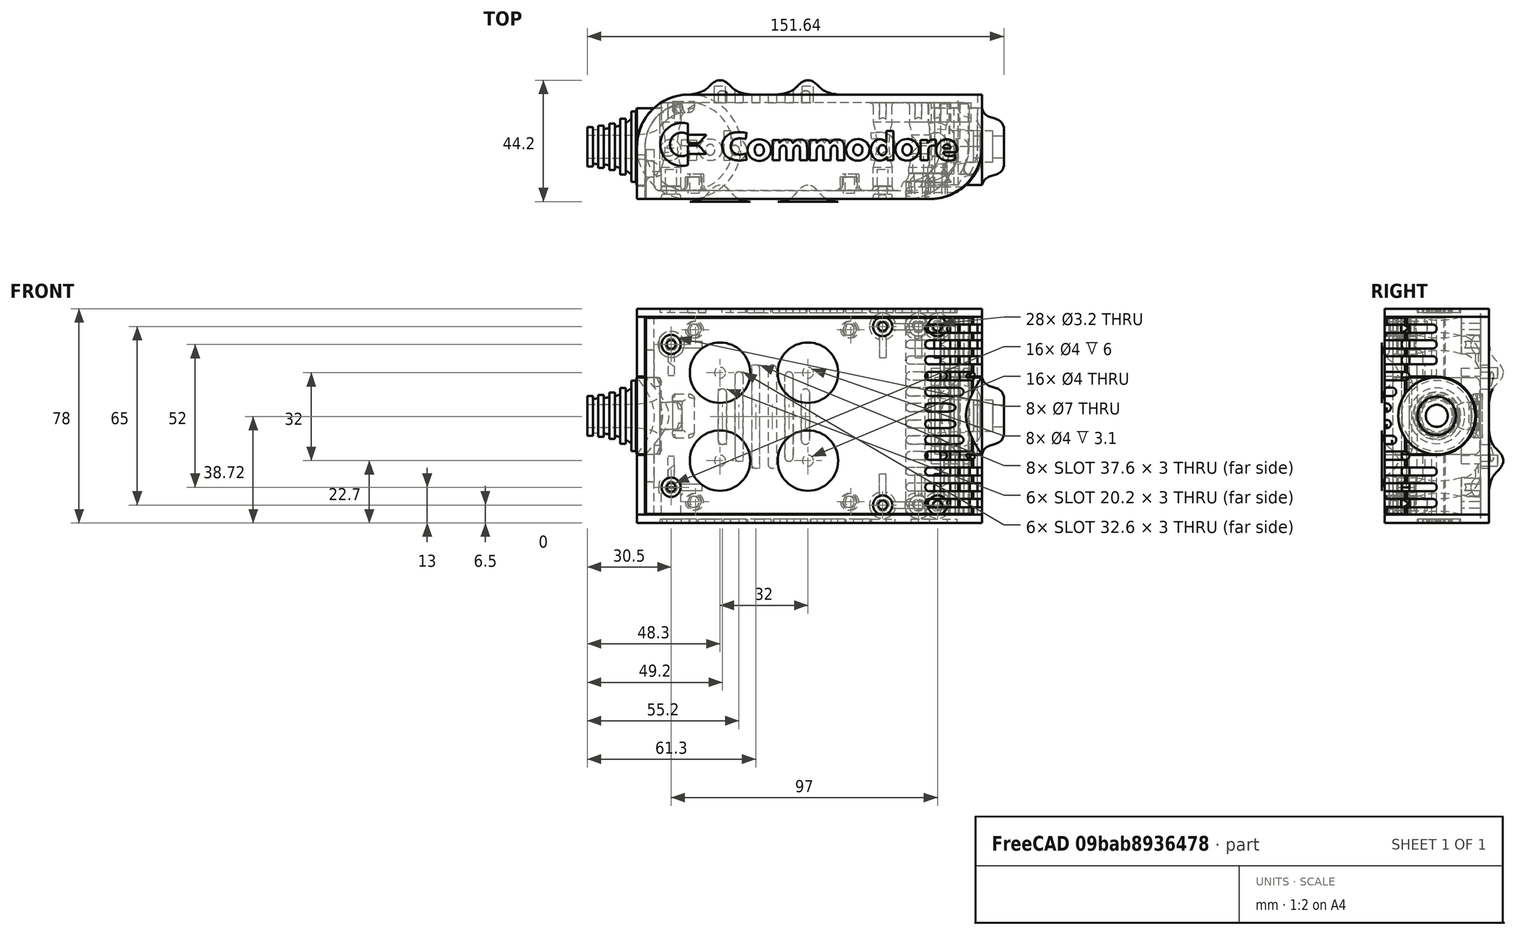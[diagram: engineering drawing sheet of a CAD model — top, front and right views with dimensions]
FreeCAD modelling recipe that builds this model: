
FCSTD DOCUMENT  (FreeCAD 0.19R0.19.2)
Label: enclosure_211FCStd
License: All rights reserved
LicenseURL: http://en.wikipedia.org/wiki/All_rights_reserved
objects: Part::Revolution×152, Part::MultiFuse×146, Part::Feature×146, Sketcher::SketchObject×84, Part::Cut×72, Part::Cylinder×70, Part::Extrusion×69, Part::Fillet×58, Part::Box×37, App::MeasureDistance×4, Part::FeaturePython×2, Image::ImagePlane×1, PartDesign::Body×1, Part::Mirroring×1
note: 838 computed .brp shape members not serialized (recipe doc carries the construction recipe); baked Part::Feature solids carry a one-line shape summary decoded from their .brp

FEATURE [Sketcher::SketchObject] Sketch  label="topSketch"
  FullyConstrained = true
  sketch-geometry (20):
    g0: LineSegment StartX=5.21097e-06 StartY=3 StartZ=0 EndX=5.21097e-06 EndY=19 EndZ=0
    g1: ArcOfCircle CenterX=19 CenterY=19 CenterZ=0 NormalX=0 NormalY=0 NormalZ=1 AngleXU=0 Radius=19 StartAngle=1.5708 EndAngle=3.14159
    g2: ArcOfCircle CenterX=19 CenterY=19 CenterZ=0 NormalX=0 NormalY=0 NormalZ=1 AngleXU=0 Radius=16 StartAngle=1.5708 EndAngle=3.14159
    g3: LineSegment StartX=114 StartY=35 StartZ=0 EndX=19 EndY=35 EndZ=0
    g4: LineSegment StartX=5.21097e-06 StartY=3 StartZ=0 EndX=5.21097e-06 EndY=0 EndZ=0
    g5: LineSegment StartX=3 StartY=0 StartZ=0 EndX=5.21097e-06 EndY=0 EndZ=0
    g6: LineSegment StartX=3 StartY=19 StartZ=0 EndX=3 EndY=0 EndZ=0
    g7: LineSegment StartX=19 StartY=38 StartZ=0 EndX=124 EndY=38 EndZ=0
    g8: Circle CenterX=119 CenterY=35 CenterZ=0 NormalX=0 NormalY=0 NormalZ=1 AngleXU=0 Radius=1
    g9: Circle CenterX=121 CenterY=35 CenterZ=0 NormalX=0 NormalY=0 NormalZ=1 AngleXU=0 Radius=1
    g10: Circle CenterX=121 CenterY=33 CenterZ=0 NormalX=0 NormalY=0 NormalZ=1 AngleXU=0 Radius=1
    g11: BSplineCurve PolesCount=3 KnotsCount=2 Degree=2 IsPeriodic=0
    g12: GeomPoint X=119 Y=35 Z=0
    g13: GeomPoint X=121 Y=33 Z=0
    g14: LineSegment StartX=119 StartY=35 StartZ=0 EndX=114 EndY=35 EndZ=0
    g15: ArcOfCircle CenterX=105 CenterY=19 CenterZ=0 NormalX=0 NormalY=0 NormalZ=1 AngleXU=0 Radius=19 StartAngle=5.7297 EndAngle=6.28319
    g16: ArcOfCircle CenterX=105 CenterY=19 CenterZ=0 NormalX=0 NormalY=0 NormalZ=1 AngleXU=0 Radius=16 StartAngle=5.60905 EndAngle=6.28319
    g17: LineSegment StartX=121 StartY=33 StartZ=0 EndX=121 EndY=19 EndZ=0
    g18: LineSegment StartX=124 StartY=38 StartZ=0 EndX=124 EndY=19 EndZ=0
    g19: LineSegment StartX=117.5 StartY=9.01251 StartZ=0 EndX=121.163 EndY=9.0125 EndZ=0
  constraints (46):
    c: Vertical(g0)
    c: Block(g0)
    c: Coincident(g1,g0)
    c: Block(g1)
    c: Coincident(g2,g1)
    c: Block(g2)
    c: Coincident(g3,g2)
    c: Horizontal(g3)
    c: Tangent(g3,g2)
    c: Coincident(g4,g0)
    c: Distance(g4) = 3
    c: Vertical(g4)
    c: Coincident(g5,g4)
    c: Horizontal(g5)
    c: Coincident(g6,g2)
    c: Coincident(g6,g5)
    c: Vertical(g6)
    c: Horizontal(g7)
    c: Distance(g7) = 105
    c: Coincident(g7,g1)
    c: Block(g3)
    c: Weight(g8) = 1
    c: Equal(g8,g9)
    c: Equal(g8,g10)
    c: InternalAlignment(g8,g11)
    c: InternalAlignment(g9,g11)
    c: InternalAlignment(g10,g11)
    c: InternalAlignment(g12,g11)
    c: InternalAlignment(g13,g11)
    c: Block(g11)
    c: Coincident(g14,g11)
    c: Coincident(g14,g3)
    c: Horizontal(g14)
    c: Block(g15)
    c: Coincident(g16,g15)
    c: Block(g16)
    c: Coincident(g17,g11)
    c: Coincident(g17,g16)
    c: Vertical(g17)
    c: Distance(g17) = 14
    c: Coincident(g18,g7)
    c: Coincident(g18,g15)
    c: Vertical(g18)
    c: Distance(g18) = 19
    c: Coincident(g19,g16)
    c: Coincident(g19,g15)
FEATURE [Sketcher::SketchObject] Sketch001  label="bottomSketch"
  FullyConstrained = true
  sketch-geometry (32):
    g0: LineSegment StartX=3.3 StartY=-6.03275e-07 StartZ=0 EndX=98 EndY=-6.03275e-07 EndZ=0
    g1: ArcOfCircle CenterX=98 CenterY=19 CenterZ=0 NormalX=0 NormalY=0 NormalZ=1 AngleXU=0 Radius=19 StartAngle=4.71239 EndAngle=5.71103
    g2: LineSegment StartX=6.3 StartY=8 StartZ=0 EndX=3.3 EndY=8 EndZ=0
    g3: LineSegment StartX=3.3 StartY=8 StartZ=0 EndX=3.3 EndY=-6.03275e-07 EndZ=0
    g4: ArcOfCircle CenterX=8.3 CenterY=5 CenterZ=0 NormalX=0 NormalY=0 NormalZ=1 AngleXU=0 Radius=2 StartAngle=3.14159 EndAngle=4.71239
    g5: LineSegment StartX=6.3 StartY=8 StartZ=0 EndX=6.3 EndY=5 EndZ=0
    g6: ArcOfCircle CenterX=98 CenterY=19 CenterZ=0 NormalX=0 NormalY=0 NormalZ=1 AngleXU=0 Radius=12.7 StartAngle=4.71239 EndAngle=6.28319
    g7: LineSegment StartX=94.7 StartY=3 StartZ=0 EndX=8.3 EndY=3 EndZ=0
    g8-g12: Circle x5 (B-spline internal-alignment scaffolding for g13; pole/knot coordinates omitted)
    g13: BSplineCurve PolesCount=5 KnotsCount=3 Degree=3 IsPeriodic=0
    g14: GeomPoint X=98 Y=6.3 Z=0
    g15: GeomPoint X=96.3938 Y=4.71946 Z=0
    g16: GeomPoint X=94.7 Y=3 Z=0
    g17-g23: Circle x7 (B-spline internal-alignment scaffolding for g24; pole/knot coordinates omitted)
    g24: BSplineCurve PolesCount=7 KnotsCount=5 Degree=3 IsPeriodic=0
    g25-g29: GeomPoint x5 (B-spline internal-alignment scaffolding for g24; pole/knot coordinates omitted)
    g30: ArcOfCircle CenterX=98 CenterY=19 CenterZ=0 NormalX=0 NormalY=0 NormalZ=1 AngleXU=0 Radius=15.7 StartAngle=5.81226 EndAngle=6.28319
    g31: LineSegment StartX=110.7 StartY=19 StartZ=0 EndX=113.7 EndY=19 EndZ=0
  constraints (41):
    c: Horizontal(g0)
    c: Coincident(g1,g0)
    c: Block(g1)
    c: Horizontal(g2)
    c: Distance(g2) = 3
    c: Coincident(g3,g2)
    c: Vertical(g3)
    c: Coincident(g3,g0)
    c: Block(g4)
    c: Block(g2)
    c: Coincident(g5,g2)
    c: Coincident(g5,g4)
    c: Vertical(g5)
    c: Coincident(g6,g1)
    c: Block(g6)
    c: Coincident(g7,g4)
    c: Horizontal(g7)
    c: Block(g0)
    c: Block(g7)
    c: Block(g3)
    c: Coincident(g13,g6)
    c: Weight(g8) = 1
    c: Equal(g8, g9-g12) x4
    c: Coincident(g13,g7)
    c: InternalAlignment(g8-g12 -> g13) x5
    c: InternalAlignment(g14,g13)
    c: InternalAlignment(g15,g13)
    c: InternalAlignment(g16,g13)
    c: Block(g13)
    c: Weight(g17) = 1
    c: Equal(g17, g18-g23) x6
    c: Coincident(g24,g1)
    c: InternalAlignment(g17-g23 -> g24) x7
    c: InternalAlignment(g25-g29 -> g24) x5
    c: Block(g24)
    c: Coincident(g30,g24)
    c: Coincident(g31,g6)
    c: Coincident(g31,g30)
    c: Horizontal(g31)
    c: Block(g31)
    c: Block(g30)
FEATURE [Part::Extrusion] Extrude  label="top"
  Base = -> Sketch
  Dir = (0,0,1)
  DirMode = 2
  FaceMakerClass = Part::FaceMakerBullseye
  LengthFwd = 72
  LengthRev = 0
  Solid = true
  Symmetric = false
FEATURE [Part::Extrusion] Extrude001  label="bottom"
  Base = -> Sketch001
  Dir = (0,0,1)
  DirMode = 2
  FaceMakerClass = Part::FaceMakerBullseye
  LengthFwd = 71.4
  LengthRev = 0
  Placement = pos=(0,0,0.3) rot=(0,0,1;0rad)
  Solid = true
  Symmetric = false
FEATURE [Sketcher::SketchObject] Sketch002  label="topSketch001"
  FullyConstrained = true
  sketch-geometry (8):
    g0: ArcOfCircle CenterX=19 CenterY=19.0975 CenterZ=0 NormalX=0 NormalY=0 NormalZ=1 AngleXU=0 Radius=18.9025 StartAngle=1.5708 EndAngle=3.14674
    g1: LineSegment StartX=0.0977805 StartY=19.0003 StartZ=0 EndX=0.0977805 EndY=0.000251602 EndZ=0
    g2: LineSegment StartX=19 StartY=38 StartZ=0 EndX=124 EndY=38 EndZ=0
    g3: LineSegment StartX=0.0977805 StartY=0.000251602 StartZ=0 EndX=105.098 EndY=0.000251602 EndZ=0
    g4: LineSegment StartX=124 StartY=38 StartZ=0 EndX=125.616 EndY=38 EndZ=0
    g5: LineSegment StartX=105.098 StartY=0.000251602 StartZ=0 EndX=106.713 EndY=0.000251602 EndZ=0
    g6: ArcOfCircle CenterX=106.616 CenterY=19 CenterZ=0 NormalX=0 NormalY=0 NormalZ=1 AngleXU=0 Radius=19 StartAngle=4.71754 EndAngle=6.28319
    g7: LineSegment StartX=125.616 StartY=38 StartZ=0 EndX=125.616 EndY=19 EndZ=0
  constraints (21):
    c: Block(g0)
    c: Coincident(g1,g0)
    c: Vertical(g1)
    c: Horizontal(g2)
    c: Distance(g2) = 105
    c: Coincident(g2,g0)
    c: Distance(g1) = 19
    c: Coincident(g3,g1)
    c: Horizontal(g3)
    c: Distance(g3) = 105
    c: Coincident(g4,g2)
    c: Horizontal(g4)
    c: Distance(g4) = 1.61553
    c: Horizontal(g5)
    c: Equal(g4,g5) = 1.61553
    c: Coincident(g5,g3)
    c: Block(g6)
    c: Coincident(g6,g5)
    c: Coincident(g7,g4)
    c: Coincident(g7,g6)
    c: Vertical(g7)
FEATURE [Part::Extrusion] Extrude002  label="sideA"
  Base = -> Sketch002
  Dir = (0,0,1)
  DirMode = 2
  FaceMakerClass = Part::FaceMakerBullseye
  LengthFwd = 3
  LengthRev = 0
  Placement = pos=(0,0,-3) rot=(0,0,1;0rad)
  Solid = true
  Symmetric = false
FEATURE [Sketcher::SketchObject] Sketch003  label="topSketch002"
  FullyConstrained = true
  sketch-geometry (6):
    g0: LineSegment StartX=19 StartY=38 StartZ=0 EndX=117 EndY=38 EndZ=0
    g1: ArcOfCircle CenterX=19 CenterY=19 CenterZ=0 NormalX=0 NormalY=0 NormalZ=1 AngleXU=0 Radius=19 StartAngle=1.5708 EndAngle=3.14159
    g2: LineSegment StartX=117 StartY=38 StartZ=0 EndX=117 EndY=19 EndZ=0
    g3: LineSegment StartX=98 StartY=1.0161e-12 StartZ=0 EndX=5.22862e-06 EndY=1.0161e-12 EndZ=0
    g4: LineSegment StartX=5.22862e-06 StartY=19 StartZ=0 EndX=5.22862e-06 EndY=1.0161e-12 EndZ=0
    g5: ArcOfCircle CenterX=98 CenterY=19 CenterZ=0 NormalX=0 NormalY=0 NormalZ=1 AngleXU=0 Radius=19 StartAngle=4.71239 EndAngle=6.28319
  constraints (16):
    c: Horizontal(g0)
    c: Distance(g0) = 98
    c: Coincident(g1,g0)
    c: Block(g1)
    c: Coincident(g2,g0)
    c: Vertical(g2)
    c: Distance(g2) = 19
    c: Horizontal(g3)
    c: Coincident(g4,g1)
    c: Vertical(g4)
    c: Coincident(g3,g4)
    c: Block(g3)
    c: Coincident(g5,g2)
    c: Coincident(g5,g3)
    c: Block(g0)
    c: Block(g5)
FEATURE [Sketcher::SketchObject] Sketch004
  FullyConstrained = true
  MapMode = 3
  Placement = pos=(0,0,0) rot=(1,0,0;1.5708rad)
  Support = -> [Extrude]
  sketch-geometry (8):
    g0: Circle CenterX=80.351 CenterY=-67.6202 CenterZ=0 NormalX=0 NormalY=0 NormalZ=1 AngleXU=0 Radius=2
    g1: Circle CenterX=80.351 CenterY=-67.6202 CenterZ=0 NormalX=0 NormalY=0 NormalZ=1 AngleXU=0 Radius=3
    g2: Circle CenterX=80.351 CenterY=-4.92017 CenterZ=0 NormalX=0 NormalY=0 NormalZ=1 AngleXU=0 Radius=2
    g3: Circle CenterX=80.351 CenterY=-4.92017 CenterZ=0 NormalX=0 NormalY=0 NormalZ=1 AngleXU=0 Radius=3
    g4: Circle CenterX=23.851 CenterY=-4.92017 CenterZ=0 NormalX=0 NormalY=0 NormalZ=1 AngleXU=0 Radius=2
    g5: Circle CenterX=23.851 CenterY=-4.92017 CenterZ=0 NormalX=0 NormalY=0 NormalZ=1 AngleXU=0 Radius=3
    g6: Circle CenterX=23.851 CenterY=-67.6202 CenterZ=0 NormalX=0 NormalY=0 NormalZ=1 AngleXU=0 Radius=2
    g7: Circle CenterX=23.851 CenterY=-67.6202 CenterZ=0 NormalX=0 NormalY=0 NormalZ=1 AngleXU=0 Radius=3
  constraints (8):
    c: Block(g3)
    c: Block(g2)
    c: Block(g1)
    c: Block(g0)
    c: Block(g6)
    c: Block(g7)
    c: Block(g4)
    c: Block(g5)
FEATURE [Part::Extrusion] Extrude004
  Base = -> Sketch004
  Dir = (0,-1,2e-16)
  DirMode = 2
  FaceMakerClass = Part::FaceMakerBullseye
  LengthFwd = 6
  LengthRev = 0
  Placement = pos=(0,9,0) rot=(0,0,1;0rad)
  Solid = true
  Symmetric = false
FEATURE [Sketcher::SketchObject] Sketch005
  FullyConstrained = true
  MapMode = 3
  Placement = pos=(0,0,0) rot=(1,0,0;1.5708rad)
  Support = -> [Extrude]
  sketch-geometry (8):
    g0: Circle CenterX=80.351 CenterY=-67.6202 CenterZ=0 NormalX=0 NormalY=0 NormalZ=1 AngleXU=0 Radius=3
    g1: Circle CenterX=80.351 CenterY=-4.92017 CenterZ=0 NormalX=0 NormalY=0 NormalZ=1 AngleXU=0 Radius=3
    g2: Circle CenterX=23.851 CenterY=-4.92017 CenterZ=0 NormalX=0 NormalY=0 NormalZ=1 AngleXU=0 Radius=3
    g3: Circle CenterX=23.851 CenterY=-67.6202 CenterZ=0 NormalX=0 NormalY=0 NormalZ=1 AngleXU=0 Radius=3
    g4: Circle CenterX=23.851 CenterY=-67.6202 CenterZ=0 NormalX=0 NormalY=0 NormalZ=1 AngleXU=0 Radius=5
    g5: Circle CenterX=80.351 CenterY=-67.6202 CenterZ=0 NormalX=0 NormalY=0 NormalZ=1 AngleXU=0 Radius=5
    g6: Circle CenterX=23.851 CenterY=-4.92017 CenterZ=0 NormalX=0 NormalY=0 NormalZ=1 AngleXU=0 Radius=5
    g7: Circle CenterX=80.351 CenterY=-4.92017 CenterZ=0 NormalX=0 NormalY=0 NormalZ=1 AngleXU=0 Radius=5
  constraints (8):
    c: Block(g1)
    c: Block(g0)
    c: Block(g3)
    c: Block(g2)
    c: Block(g5)
    c: Block(g4)
    c: Block(g6)
    c: Block(g7)
FEATURE [Part::Extrusion] Extrude005
  Base = -> Sketch005
  Dir = (0,-1,2e-16)
  DirMode = 2
  FaceMakerClass = Part::FaceMakerBullseye
  LengthFwd = 2
  LengthRev = 0
  Solid = true
  Symmetric = false
FEATURE [Sketcher::SketchObject] Sketch006
  FullyConstrained = true
  MapMode = 3
  Placement = pos=(0,0,0) rot=(1,0,0;1.5708rad)
  sketch-geometry (8):
    g0: Circle CenterX=80.351 CenterY=-67.6202 CenterZ=0 NormalX=0 NormalY=0 NormalZ=1 AngleXU=0 Radius=3
    g1: Circle CenterX=80.351 CenterY=-4.92017 CenterZ=0 NormalX=0 NormalY=0 NormalZ=1 AngleXU=0 Radius=3
    g2: Circle CenterX=23.851 CenterY=-4.92017 CenterZ=0 NormalX=0 NormalY=0 NormalZ=1 AngleXU=0 Radius=3
    g3: Circle CenterX=23.851 CenterY=-67.6202 CenterZ=0 NormalX=0 NormalY=0 NormalZ=1 AngleXU=0 Radius=3
    g4: Circle CenterX=23.851 CenterY=-67.6202 CenterZ=0 NormalX=0 NormalY=0 NormalZ=1 AngleXU=0 Radius=5
    g5: Circle CenterX=80.351 CenterY=-67.6202 CenterZ=0 NormalX=0 NormalY=0 NormalZ=1 AngleXU=0 Radius=5
    g6: Circle CenterX=23.851 CenterY=-4.92017 CenterZ=0 NormalX=0 NormalY=0 NormalZ=1 AngleXU=0 Radius=5
    g7: Circle CenterX=80.351 CenterY=-4.92017 CenterZ=0 NormalX=0 NormalY=0 NormalZ=1 AngleXU=0 Radius=5
  constraints (8):
    c: Block(g1)
    c: Block(g0)
    c: Block(g3)
    c: Block(g2)
    c: Block(g5)
    c: Block(g4)
    c: Block(g6)
    c: Block(g7)
FEATURE [Part::Extrusion] Extrude007
  Base = -> Sketch006
  Dir = (0,-1,2e-16)
  DirMode = 2
  FaceMakerClass = Part::FaceMakerBullseye
  LengthFwd = 2
  LengthRev = 0
  Solid = true
  Symmetric = false
FEATURE [Part::Fillet] Fillet
  Base = -> Extrude007
  Edges = 4 edges r=1.99: [Edge6,Edge12,Edge18,Edge24]
FEATURE [Part::Cut] Cut
  Base = -> Extrude005
  Placement = pos=(0,5,0) rot=(0,0,1;0rad)
  Tool = -> Fillet
FEATURE [Part::MultiFuse] Fusion  label="pCBScrews"
  Placement = pos=(-2.5,0,72.3) rot=(0,0,1;0rad)
  Shapes = -> [Extrude004,Cut]
FEATURE [App::MeasureDistance] Distance  label="Distance: 0.69 mm"
  Distance = 0.685967
  P1 = (24.0138,2.9647,0.3)
  P2 = (23.8901,3,-0.373787)
FEATURE [App::MeasureDistance] Distance001  label="Distance: 0.53 mm"
  Distance = 0.533607
  P1 = (80.2939,3,72.2334)
  P2 = (80.281,2.99661,71.7)
FEATURE [Part::Fillet] Fillet001
  Base = -> Extrude001
  Edges = 1 edges r=2.4: [Edge17]
FEATURE [Part::Fillet] Fillet002  label="bottom001"
  Base = -> Fillet001
  Edges = 1 edges r=2.4: [Edge36]
FEATURE [Part::Fillet] Fillet003  label="top001"
  Base = -> Extrude
  Edges = 1 edges r=2: [Edge1]
FEATURE [Sketcher::SketchObject] Sketch007
  FullyConstrained = true
  sketch-geometry (16):
    g0: LineSegment StartX=4 StartY=0 StartZ=0 EndX=4 EndY=2.4 EndZ=0
    g1: LineSegment StartX=4 StartY=2.4 StartZ=0 EndX=7 EndY=2.4 EndZ=0
    g2: LineSegment StartX=4 StartY=0 StartZ=0 EndX=5.7 EndY=0 EndZ=0
    g3: LineSegment StartX=5.7 StartY=0 StartZ=0 EndX=5.7 EndY=-5.6 EndZ=0
    g4-g8: Circle x5 (B-spline internal-alignment scaffolding for g9; pole/knot coordinates omitted)
    g9: BSplineCurve PolesCount=5 KnotsCount=3 Degree=3 IsPeriodic=0
    g10: GeomPoint X=7 Y=2.4 Z=0
    g11: GeomPoint X=10.4582 Y=-1.55472 Z=0
    g12: GeomPoint X=14 Y=-5.6 Z=0
    g13: LineSegment StartX=14 StartY=-5.6 StartZ=0 EndX=14 EndY=-14.1 EndZ=0
    g14: LineSegment StartX=14 StartY=-14.1 StartZ=0 EndX=6.5 EndY=-14.1 EndZ=0
    g15: LineSegment StartX=5.7 StartY=-5.6 StartZ=0 EndX=6.5 EndY=-14.1 EndZ=0
  constraints (28):
    c: Distance(g0) = 2.4
    c: Vertical(g0)
    c: Block(g0)
    c: Coincident(g1,g0)
    c: Horizontal(g1)
    c: Distance(g1) = 3
    c: Coincident(g2,g0)
    c: Horizontal(g2)
    c: Distance(g2) = 1.7
    c: Coincident(g3,g2)
    c: Vertical(g3)
    c: Distance(g3) = 5.6
    c: Coincident(g9,g1)
    c: Weight(g4) = 1
    c: Equal(g4, g5-g8) x4
    c: InternalAlignment(g4-g8 -> g9) x5
    c: InternalAlignment(g10,g9)
    c: InternalAlignment(g11,g9)
    c: InternalAlignment(g12,g9)
    c: Block(g9)
    c: Coincident(g13,g9)
    c: Vertical(g13)
    c: Distance(g13) = 8.5
    c: Coincident(g14,g13)
    c: Horizontal(g14)
    c: Distance(g14) = 7.5
    c: Coincident(g15,g3)
    c: Coincident(g15,g14)
FEATURE [Part::Feature] Face
  shape: bbox 10 x 16.5 x 2e-07 mm, 1 faces, 0 solids (baked)
FEATURE [Part::Revolution] Revolve  label="plugHousing"
  Angle = 360
  Axis = (0,1,0)
  Base = (0,0,0)
  FaceMakerClass = Part::FaceMakerBullseye
  Placement = pos=(0,0,36.15) rot=(0,0,1;0rad)
  Solid = false
  Source = -> Face
  Symmetric = false
FEATURE [Part::Feature] Face001
  shape: bbox 10 x 16.5 x 2e-07 mm, 1 faces, 0 solids (baked)
FEATURE [Part::Revolution] Revolve001  label="plugHousing001"
  Angle = 360
  Axis = (0,1,0)
  Base = (0,0,0)
  FaceMakerClass = Part::FaceMakerBullseye
  Placement = pos=(0,0,36.15) rot=(0,0,1;0rad)
  Solid = false
  Source = -> Face001
  Symmetric = false
FEATURE [Part::MultiFuse] Fusion001  label="plugHousing002"
  Placement = pos=(0,0,0) rot=(0,0,1;1.5708rad)
  Shapes = -> [Revolve001,Revolve]
FEATURE [Part::Feature] Face002
  shape: bbox 10 x 16.5 x 2e-07 mm, 1 faces, 0 solids (baked)
FEATURE [Part::Revolution] Revolve003  label="plugHousing005"
  Angle = 360
  Axis = (0,1,0)
  Base = (0,0,0)
  FaceMakerClass = Part::FaceMakerBullseye
  Placement = pos=(0,0,36.15) rot=(0,0,1;0rad)
  Solid = false
  Source = -> Face002
  Symmetric = false
FEATURE [Part::Feature] Face003
  shape: bbox 10 x 16.5 x 2e-07 mm, 1 faces, 0 solids (baked)
FEATURE [Part::Revolution] Revolve002  label="plugHousing003"
  Angle = 360
  Axis = (0,1,0)
  Base = (0,0,0)
  FaceMakerClass = Part::FaceMakerBullseye
  Placement = pos=(0,0,36.15) rot=(0,0,1;0rad)
  Solid = false
  Source = -> Face003
  Symmetric = false
FEATURE [Part::MultiFuse] Fusion002  label="plugHousing004"
  Placement = pos=(0,0,0) rot=(0,0,1;1.5708rad)
  Shapes = -> [Revolve002,Revolve003]
FEATURE [Part::MultiFuse] Fusion003  label="plugHousing006"
  Placement = pos=(0,19,0) rot=(0,0,1;3.14159rad)
  Shapes = -> [Fusion002,Fusion001]
FEATURE [Part::Feature] Face004
  shape: bbox 10 x 16.5 x 2e-07 mm, 1 faces, 0 solids (baked)
FEATURE [Part::Revolution] Revolve006  label="plugHousing010"
  Angle = 360
  Axis = (0,1,0)
  Base = (0,0,0)
  FaceMakerClass = Part::FaceMakerBullseye
  Placement = pos=(0,0,36.15) rot=(0,0,1;0rad)
  Solid = false
  Source = -> Face004
  Symmetric = false
FEATURE [Part::Feature] Face005
  shape: bbox 10 x 16.5 x 2e-07 mm, 1 faces, 0 solids (baked)
FEATURE [Part::Revolution] Revolve007  label="plugHousing011"
  Angle = 360
  Axis = (0,1,0)
  Base = (0,0,0)
  FaceMakerClass = Part::FaceMakerBullseye
  Placement = pos=(0,0,36.15) rot=(0,0,1;0rad)
  Solid = false
  Source = -> Face005
  Symmetric = false
FEATURE [Part::Feature] Face006
  shape: bbox 10 x 16.5 x 2e-07 mm, 1 faces, 0 solids (baked)
FEATURE [Part::Revolution] Revolve004  label="plugHousing007"
  Angle = 360
  Axis = (0,1,0)
  Base = (0,0,0)
  FaceMakerClass = Part::FaceMakerBullseye
  Placement = pos=(0,0,36.15) rot=(0,0,1;0rad)
  Solid = false
  Source = -> Face006
  Symmetric = false
FEATURE [Part::MultiFuse] Fusion004  label="plugHousing009"
  Placement = pos=(0,0,0) rot=(0,0,1;1.5708rad)
  Shapes = -> [Revolve004,Revolve007]
FEATURE [Part::Feature] Face007
  shape: bbox 10 x 16.5 x 2e-07 mm, 1 faces, 0 solids (baked)
FEATURE [Part::Revolution] Revolve005  label="plugHousing008"
  Angle = 360
  Axis = (0,1,0)
  Base = (0,0,0)
  FaceMakerClass = Part::FaceMakerBullseye
  Placement = pos=(0,0,36.15) rot=(0,0,1;0rad)
  Solid = false
  Source = -> Face007
  Symmetric = false
FEATURE [Part::MultiFuse] Fusion005  label="plugHousing012"
  Placement = pos=(0,0,0) rot=(0,0,1;1.5708rad)
  Shapes = -> [Revolve006,Revolve005]
FEATURE [Part::MultiFuse] Fusion006  label="plugHousing013"
  Placement = pos=(0,19,0) rot=(0,0,1;3.14159rad)
  Shapes = -> [Fusion005,Fusion004]
FEATURE [Part::MultiFuse] Fusion007  label="plugHousing014"
  Placement = pos=(122.621,0,-0.15) rot=(0,0,1;0rad)
  Shapes = -> [Fusion003,Fusion006]
FEATURE [Part::Cylinder] Cylinder002
  Angle = 360
  AttacherType = Attacher::AttachEngine3D
  Height = 20
  Placement = pos=(0,0,36.15) rot=(0,0,1;0rad)
  Radius = 4
FEATURE [Part::Cylinder] Cylinder003
  Angle = 360
  AttacherType = Attacher::AttachEngine3D
  Height = 10
  Placement = pos=(0,0,36.15) rot=(0,0,1;0rad)
  Radius = 4
FEATURE [Part::MultiFuse] Fusion009  label="removeToCreateHoleForPlugHousing"
  Placement = pos=(70,19,36.15) rot=(0,1,0;1.5708rad)
  Shapes = -> [Cylinder002,Cylinder003]
FEATURE [Part::Cylinder] Cylinder004
  Angle = 360
  AttacherType = Attacher::AttachEngine3D
  Height = 20
  Placement = pos=(0,0,36.15) rot=(0,0,1;0rad)
  Radius = 4
FEATURE [Part::Cylinder] Cylinder005
  Angle = 360
  AttacherType = Attacher::AttachEngine3D
  Height = 10
  Placement = pos=(0,0,36.15) rot=(0,0,1;0rad)
  Radius = 4
FEATURE [Part::MultiFuse] Fusion010  label="removeToCreateHoleForPlugHousing001"
  Placement = pos=(70,19,36.15) rot=(0,1,0;1.5708rad)
  Shapes = -> [Cylinder004,Cylinder005]
FEATURE [Part::Cut] Cut001
  Base = -> Fillet003
  Tool = -> Fusion010
FEATURE [Part::Cut] Cut002  label="Bottom"
  Base = -> Fillet002
  Tool = -> Fusion009
FEATURE [Part::Feature] Face008
  shape: bbox 10 x 16.5 x 2e-07 mm, 1 faces, 0 solids (baked)
FEATURE [Part::Revolution] Revolve011  label="plugHousing021"
  Angle = 360
  Axis = (0,1,0)
  Base = (0,0,0)
  FaceMakerClass = Part::FaceMakerBullseye
  Placement = pos=(0,0,36.15) rot=(0,0,1;0rad)
  Solid = false
  Source = -> Face008
  Symmetric = false
FEATURE [Part::Feature] Face009
  shape: bbox 10 x 16.5 x 2e-07 mm, 1 faces, 0 solids (baked)
FEATURE [Part::Revolution] Revolve012  label="plugHousing022"
  Angle = 360
  Axis = (0,1,0)
  Base = (0,0,0)
  FaceMakerClass = Part::FaceMakerBullseye
  Placement = pos=(0,0,36.15) rot=(0,0,1;0rad)
  Solid = false
  Source = -> Face009
  Symmetric = false
FEATURE [Part::Feature] Face010 .. Face013  x4 (patterned run collapsed; names and placements below)
  shape: bbox 10 x 16.5 x 2e-07 mm, 1 faces, 0 solids (baked)
FEATURE [Part::Revolution] Revolve015  label="plugHousing027"
  Angle = 360
  Axis = (0,1,0)
  Base = (0,0,0)
  FaceMakerClass = Part::FaceMakerBullseye
  Placement = pos=(0,0,36.15) rot=(0,0,1;0rad)
  Solid = false
  Source = -> Face013
  Symmetric = false
FEATURE [Part::Feature] Face014
  shape: bbox 10 x 16.5 x 2e-07 mm, 1 faces, 0 solids (baked)
FEATURE [Part::Feature] Face015
  shape: bbox 10 x 16.5 x 2e-07 mm, 1 faces, 0 solids (baked)
FEATURE [Part::Feature] Face016
  shape: bbox 10 x 16.5 x 2e-07 mm, 1 faces, 0 solids (baked)
FEATURE [Part::Revolution] Revolve019  label="plugHousing033"
  Angle = 360
  Axis = (0,1,0)
  Base = (0,0,0)
  FaceMakerClass = Part::FaceMakerBullseye
  Placement = pos=(0,0,36.15) rot=(0,0,1;0rad)
  Solid = false
  Source = -> Face016
  Symmetric = false
FEATURE [Part::Feature] Face017
  shape: bbox 10 x 16.5 x 2e-07 mm, 1 faces, 0 solids (baked)
FEATURE [Part::Revolution] Revolve020  label="plugHousing034"
  Angle = 360
  Axis = (0,1,0)
  Base = (0,0,0)
  FaceMakerClass = Part::FaceMakerBullseye
  Placement = pos=(0,0,36.15) rot=(0,0,1;0rad)
  Solid = false
  Source = -> Face017
  Symmetric = false
FEATURE [Part::Feature] Face018
  shape: bbox 10 x 16.5 x 2e-07 mm, 1 faces, 0 solids (baked)
FEATURE [Part::Revolution] Revolve016  label="plugHousing030"
  Angle = 360
  Axis = (0,1,0)
  Base = (0,0,0)
  FaceMakerClass = Part::FaceMakerBullseye
  Placement = pos=(0,0,36.15) rot=(0,0,1;0rad)
  Solid = false
  Source = -> Face018
  Symmetric = false
FEATURE [Part::MultiFuse] Fusion020  label="plugHousing038"
  Placement = pos=(0,0,0) rot=(0,0,1;1.5708rad)
  Shapes = -> [Revolve016,Revolve020]
FEATURE [Part::Feature] Face019
  shape: bbox 10 x 16.5 x 2e-07 mm, 1 faces, 0 solids (baked)
FEATURE [Part::Feature] Face020
  shape: bbox 10 x 16.5 x 2e-07 mm, 1 faces, 0 solids (baked)
FEATURE [Part::Revolution] Revolve017  label="plugHousing031"
  Angle = 360
  Axis = (0,1,0)
  Base = (0,0,0)
  FaceMakerClass = Part::FaceMakerBullseye
  Placement = pos=(0,0,36.15) rot=(0,0,1;0rad)
  Solid = false
  Source = -> Face020
  Symmetric = false
FEATURE [Part::MultiFuse] Fusion021  label="plugHousing039"
  Placement = pos=(0,0,0) rot=(0,0,1;1.5708rad)
  Shapes = -> [Revolve019,Revolve017]
FEATURE [Part::MultiFuse] Fusion023  label="plugHousing041"
  Placement = pos=(0,19,0) rot=(0,0,1;3.14159rad)
  Shapes = -> [Fusion021,Fusion020]
FEATURE [Part::Revolution] Revolve022  label="plugHousing043"
  Angle = 360
  Axis = (0,1,0)
  Base = (0,0,0)
  FaceMakerClass = Part::FaceMakerBullseye
  Placement = pos=(0,0,36.15) rot=(0,0,1;0rad)
  Solid = false
  Source = -> Face019
  Symmetric = false
FEATURE [Part::Feature] Face021
  shape: bbox 10 x 16.5 x 2e-07 mm, 1 faces, 0 solids (baked)
FEATURE [Part::Revolution] Revolve023  label="plugHousing044"
  Angle = 360
  Axis = (0,1,0)
  Base = (0,0,0)
  FaceMakerClass = Part::FaceMakerBullseye
  Placement = pos=(0,0,36.15) rot=(0,0,1;0rad)
  Solid = false
  Source = -> Face021
  Symmetric = false
FEATURE [Part::Feature] Face022
  shape: bbox 10 x 16.5 x 2e-07 mm, 1 faces, 0 solids (baked)
FEATURE [Part::Revolution] Revolve018  label="plugHousing032"
  Angle = 360
  Axis = (0,1,0)
  Base = (0,0,0)
  FaceMakerClass = Part::FaceMakerBullseye
  Placement = pos=(0,0,36.15) rot=(0,0,1;0rad)
  Solid = false
  Source = -> Face022
  Symmetric = false
FEATURE [Part::MultiFuse] Fusion022  label="plugHousing040"
  Placement = pos=(0,0,0) rot=(0,0,1;1.5708rad)
  Shapes = -> [Revolve018,Revolve023]
FEATURE [Part::Feature] Face023
  shape: bbox 10 x 16.5 x 2e-07 mm, 1 faces, 0 solids (baked)
FEATURE [Part::Revolution] Revolve021  label="plugHousing035"
  Angle = 360
  Axis = (0,1,0)
  Base = (0,0,0)
  FaceMakerClass = Part::FaceMakerBullseye
  Placement = pos=(0,0,36.15) rot=(0,0,1;0rad)
  Solid = false
  Source = -> Face023
  Symmetric = false
FEATURE [Part::MultiFuse] Fusion018  label="plugHousing036"
  Placement = pos=(0,0,0) rot=(0,0,1;1.5708rad)
  Shapes = -> [Revolve022,Revolve021]
FEATURE [Part::MultiFuse] Fusion019  label="plugHousing037"
  Placement = pos=(0,19,0) rot=(0,0,1;3.14159rad)
  Shapes = -> [Fusion018,Fusion022]
FEATURE [Part::MultiFuse] Fusion024  label="plugHousing042"
  Placement = pos=(122.621,0,-0.15) rot=(0,0,1;0rad)
  Shapes = -> [Fusion023,Fusion019]
FEATURE [Part::Cylinder] Cylinder006
  Angle = 360
  AttacherType = Attacher::AttachEngine3D
  Height = 20
  Placement = pos=(0,0,36.15) rot=(0,0,1;0rad)
  Radius = 14.3
FEATURE [Part::Cylinder] Cylinder007
  Angle = 360
  AttacherType = Attacher::AttachEngine3D
  Height = 10
  Placement = pos=(0,0,36.15) rot=(0,0,1;0rad)
  Radius = 4
FEATURE [Part::MultiFuse] Fusion026  label="removeToCreteHoleForPlugHousing"
  Placement = pos=(70,19,36) rot=(0,1,0;1.5708rad)
  Shapes = -> [Cylinder006,Cylinder007]
FEATURE [Part::Box] Box001  label="Cube001"
  AttacherType = Attacher::AttachEngine3D
  Height = 28
  Length = 3
  Placement = pos=(110.7,19,22) rot=(0,0,1;0rad)
  Width = 15.7
FEATURE [Part::Cut] Cut003  label="top002"
  Base = -> Cut001
  Tool = -> Fusion007
FEATURE [Part::Revolution] Revolve008  label="plugHousing015"
  Angle = 360
  Axis = (0,1,0)
  Base = (0,0,0)
  FaceMakerClass = Part::FaceMakerBullseye
  Placement = pos=(0,0,36.15) rot=(0,0,1;0rad)
  Solid = false
  Source = -> Face010
  Symmetric = false
FEATURE [Part::MultiFuse] Fusion013  label="plugHousing020"
  Placement = pos=(0,0,0) rot=(0,0,1;1.5708rad)
  Shapes = -> [Revolve008,Revolve012]
FEATURE [Part::Cut] Cut004  label="top003"
  Base = -> Cut003
  Placement = pos=(1,0,0) rot=(0,0,1;0rad)
  Tool = -> Fusion026
FEATURE [Part::Cylinder] Cylinder008
  Angle = 360
  AttacherType = Attacher::AttachEngine3D
  Height = 20
  Placement = pos=(0,0,36.15) rot=(0,0,1;0rad)
  Radius = 10.3
FEATURE [Part::Cylinder] Cylinder009
  Angle = 360
  AttacherType = Attacher::AttachEngine3D
  Height = 10
  Placement = pos=(0,0,36.15) rot=(0,0,1;0rad)
  Radius = 4
FEATURE [Part::MultiFuse] Fusion027  label="removeToCreteHoleForPlugHousing001"
  Placement = pos=(70,19,36) rot=(0,1,0;1.5708rad)
  Shapes = -> [Cylinder008,Cylinder009]
FEATURE [Part::Cut] Cut005  label="plugHousingTab"
  Base = -> Box001
  Tool = -> Fusion027
FEATURE [Part::MultiFuse] Fusion028  label="plugHousing045"
  Shapes = -> [Fusion024,Cut005]
FEATURE [Part::Box] Box002  label="Cube002"
  AttacherType = Attacher::AttachEngine3D
  Height = 28.8
  Length = 3
  Placement = pos=(107.3,28,21.6) rot=(0,0,1;0rad)
  Width = 7
FEATURE [Part::Box] Box003  label="Cube003"
  AttacherType = Attacher::AttachEngine3D
  Height = 3
  Length = 6.4
  Placement = pos=(107.3,28,18.6) rot=(0,0,1;0rad)
  Width = 7
FEATURE [Part::Box] Box004  label="Cube004"
  AttacherType = Attacher::AttachEngine3D
  Height = 3
  Length = 6.4
  Placement = pos=(107.3,28,50.4) rot=(0,0,1;0rad)
  Width = 7
FEATURE [Part::MultiFuse] Fusion029  label="plugHousingBracketHolder"
  Shapes = -> [Box004,Box002,Box003]
FEATURE [Part::Cylinder] Cylinder010
  Angle = 360
  AttacherType = Attacher::AttachEngine3D
  Height = 20
  Placement = pos=(0,0,36.15) rot=(0,0,1;0rad)
  Radius = 14.3
FEATURE [Part::Cylinder] Cylinder011
  Angle = 360
  AttacherType = Attacher::AttachEngine3D
  Height = 10
  Placement = pos=(0,0,36.15) rot=(0,0,1;0rad)
  Radius = 4
FEATURE [Part::MultiFuse] Fusion030  label="removeToCreteHoleForPlugHousing002"
  Placement = pos=(70,19,36) rot=(0,1,0;1.5708rad)
  Shapes = -> [Cylinder010,Cylinder011]
FEATURE [Part::Cut] Cut006  label="plugHousingBracketHolder001"
  Base = -> Fusion029
  Tool = -> Fusion030
FEATURE [Part::Cylinder] Cylinder012
  Angle = 360
  AttacherType = Attacher::AttachEngine3D
  Height = 20
  Placement = pos=(0,0,36.15) rot=(0,0,1;0rad)
  Radius = 7
FEATURE [Part::Cylinder] Cylinder013
  Angle = 360
  AttacherType = Attacher::AttachEngine3D
  Height = 10
  Placement = pos=(0,0,36.15) rot=(0,0,1;0rad)
  Radius = 4
FEATURE [Part::MultiFuse] Fusion032  label="removeToCreteHoleForPlugHousing003"
  Placement = pos=(70,19,36) rot=(0,1,0;1.5708rad)
  Shapes = -> [Cylinder012,Cylinder013]
FEATURE [Part::Cut] Cut007  label="bottom002"
  Base = -> Cut002
  Tool = -> Fusion032
FEATURE [Sketcher::SketchObject] Sketch008
  FullyConstrained = true
  sketch-geometry (54):
    g0: LineSegment StartX=-4.2 StartY=0 StartZ=0 EndX=-6.2 EndY=0 EndZ=0
    g1: LineSegment StartX=-14 StartY=-18 StartZ=0 EndX=-14 EndY=-26.5 EndZ=0
    g2: LineSegment StartX=-4.2 StartY=0 StartZ=0 EndX=-4.2 EndY=-13.4877 EndZ=0
    g3: Circle CenterX=-4.2 CenterY=-13.4877 CenterZ=0 NormalX=0 NormalY=0 NormalZ=1 AngleXU=0 Radius=1
    g4: Circle CenterX=-4.2 CenterY=-26.5 CenterZ=0 NormalX=0 NormalY=0 NormalZ=1 AngleXU=0 Radius=1
    g5: Circle CenterX=-8.2 CenterY=-26.5 CenterZ=0 NormalX=0 NormalY=0 NormalZ=1 AngleXU=0 Radius=1
    g6: BSplineCurve PolesCount=3 KnotsCount=2 Degree=2 IsPeriodic=0
    g7: GeomPoint X=-4.2 Y=-13.4877 Z=0
    g8: GeomPoint X=-8.2 Y=-26.5 Z=0
    g9: LineSegment StartX=-14 StartY=-26.5 StartZ=0 EndX=-8.2 EndY=-26.5 EndZ=0
    g10: LineSegment StartX=-10.15 StartY=-12 StartZ=0 EndX=-10.15 EndY=-14 EndZ=0
    g11: LineSegment StartX=-12.8401 StartY=-16 StartZ=0 EndX=-10.1571 EndY=-16 EndZ=0
    g12: LineSegment StartX=-10.15 StartY=-14 StartZ=0 EndX=-8.70761 EndY=-14 EndZ=0
    g13: LineSegment StartX=-12.8401 StartY=-16 StartZ=0 EndX=-12.8401 EndY=-17.6958 EndZ=0
    g14: LineSegment StartX=-10.15 StartY=-12 StartZ=0 EndX=-7.79258 EndY=-12 EndZ=0
    g15: Circle CenterX=-6.2215 CenterY=-2 CenterZ=0 NormalX=0 NormalY=0 NormalZ=1 AngleXU=0 Radius=1
    g16: Circle CenterX=-6.22762 CenterY=-2.58724 CenterZ=0 NormalX=0 NormalY=0 NormalZ=1 AngleXU=0 Radius=1
    g17: Circle CenterX=-6.32538 CenterY=-4 CenterZ=0 NormalX=0 NormalY=0 NormalZ=1 AngleXU=0 Radius=1
    g18: BSplineCurve PolesCount=3 KnotsCount=2 Degree=2 IsPeriodic=0
    g19: GeomPoint X=-6.2215 Y=-2 Z=0
    g20: GeomPoint X=-6.32538 Y=-4 Z=0
    g21: Circle CenterX=-6.48644 CenterY=-5.99526 CenterZ=0 NormalX=0 NormalY=0 NormalZ=1 AngleXU=0 Radius=1
    g22: Circle CenterX=-6.58486 CenterY=-6.99526 CenterZ=0 NormalX=0 NormalY=0 NormalZ=1 AngleXU=0 Radius=1
    g23: Circle CenterX=-6.77343 CenterY=-8 CenterZ=0 NormalX=0 NormalY=0 NormalZ=1 AngleXU=0 Radius=1
    g24: BSplineCurve PolesCount=3 KnotsCount=2 Degree=2 IsPeriodic=0
    g25: GeomPoint X=-6.48644 Y=-5.99526 Z=0
    g26: GeomPoint X=-6.77343 Y=-8 Z=0
    g27: Circle CenterX=-7.19003 CenterY=-10 CenterZ=0 NormalX=0 NormalY=0 NormalZ=1 AngleXU=0 Radius=1
    g28: Circle CenterX=-7.44407 CenterY=-11.0915 CenterZ=0 NormalX=0 NormalY=0 NormalZ=1 AngleXU=0 Radius=1
    g29: Circle CenterX=-7.79258 CenterY=-12 CenterZ=0 NormalX=0 NormalY=0 NormalZ=1 AngleXU=0 Radius=1
    g30: BSplineCurve PolesCount=3 KnotsCount=2 Degree=2 IsPeriodic=0
    g31: GeomPoint X=-7.19003 Y=-10 Z=0
    g32: GeomPoint X=-7.79258 Y=-12 Z=0
    g33: Circle CenterX=-8.70761 CenterY=-14 CenterZ=0 NormalX=0 NormalY=0 NormalZ=1 AngleXU=0 Radius=1
    g34: Circle CenterX=-9.33087 CenterY=-15.1837 CenterZ=0 NormalX=0 NormalY=0 NormalZ=1 AngleXU=0 Radius=1
    g35: Circle CenterX=-10.1571 CenterY=-16 CenterZ=0 NormalX=0 NormalY=0 NormalZ=1 AngleXU=0 Radius=1
    g36: BSplineCurve PolesCount=3 KnotsCount=2 Degree=2 IsPeriodic=0
    g37: GeomPoint X=-8.70761 Y=-14 Z=0
    g38: GeomPoint X=-10.1571 Y=-16 Z=0
    g39: Circle CenterX=-12.8401 CenterY=-17.6958 CenterZ=0 NormalX=0 NormalY=0 NormalZ=1 AngleXU=0 Radius=1
    g40: Circle CenterX=-13.3521 CenterY=-17.9027 CenterZ=0 NormalX=0 NormalY=0 NormalZ=1 AngleXU=0 Radius=1
    g41: Circle CenterX=-14 CenterY=-18 CenterZ=0 NormalX=0 NormalY=0 NormalZ=1 AngleXU=0 Radius=1
    g42: BSplineCurve PolesCount=3 KnotsCount=2 Degree=2 IsPeriodic=0
    g43: GeomPoint X=-12.8401 Y=-17.6958 Z=0
    g44: GeomPoint X=-14 Y=-18 Z=0
    g45: LineSegment StartX=-6.2 StartY=0 StartZ=0 EndX=-7.2 EndY=0 EndZ=0
    g46: LineSegment StartX=-7.2 StartY=0 StartZ=0 EndX=-7.2 EndY=-2 EndZ=0
    g47: LineSegment StartX=-7.2 StartY=-2 StartZ=0 EndX=-6.2215 EndY=-2 EndZ=0
    g48: LineSegment StartX=-6.32538 StartY=-4 StartZ=0 EndX=-7.65538 EndY=-4 EndZ=0
    g49: LineSegment StartX=-7.65538 StartY=-4 StartZ=0 EndX=-7.65538 EndY=-5.99526 EndZ=0
    g50: LineSegment StartX=-7.65538 StartY=-5.99526 StartZ=0 EndX=-6.48644 EndY=-5.99526 EndZ=0
    g51: LineSegment StartX=-6.77343 StartY=-8 StartZ=0 EndX=-8.43343 EndY=-8 EndZ=0
    g52: LineSegment StartX=-8.43343 StartY=-8 StartZ=0 EndX=-8.43343 EndY=-10 EndZ=0
    g53: LineSegment StartX=-8.43343 StartY=-10 StartZ=0 EndX=-7.19003 EndY=-10 EndZ=0
  constraints (112):
    c: Horizontal(g0)
    c: Distance(g0) = 2
    c: Block(g0)
    c: Vertical(g1)
    c: Coincident(g2,g0)
    c: Vertical(g2)
    c: Block(g2)
    c: Coincident(g6,g2)
    c: Weight(g3) = 1
    c: Equal(g3,g4)
    c: Equal(g3,g5)
    c: InternalAlignment(g3,g6)
    c: InternalAlignment(g4,g6)
    c: InternalAlignment(g5,g6)
    c: InternalAlignment(g7,g6)
    c: InternalAlignment(g8,g6)
    c: Block(g6)
    c: Coincident(g9,g1)
    c: Coincident(g9,g6)
    c: Horizontal(g9)
    c: Vertical(g10)
    c: Block(g10)
    c: Horizontal(g11)
    c: Block(g11)
    c: Coincident(g12,g10)
    c: Horizontal(g12)
    c: Block(g12)
    c: Coincident(g13,g11)
    c: Vertical(g13)
    c: Block(g13)
    c: Coincident(g14,g10)
    c: Horizontal(g14)
    c: Block(g14)
    c: Block(g9)
    c: Block(g1)
    c: Weight(g15) = 1
    c: Equal(g15,g16)
    c: Equal(g15,g17)
    c: InternalAlignment(g15,g18)
    c: InternalAlignment(g16,g18)
    c: InternalAlignment(g17,g18)
    c: InternalAlignment(g19,g18)
    c: InternalAlignment(g20,g18)
    c: Weight(g21) = 1
    c: Equal(g21,g22)
    c: Equal(g21,g23)
    c: InternalAlignment(g21,g24)
    c: InternalAlignment(g22,g24)
    c: InternalAlignment(g23,g24)
    c: InternalAlignment(g25,g24)
    c: InternalAlignment(g26,g24)
    c: Weight(g27) = 1
    c: Equal(g27,g28)
    c: Equal(g27,g29)
    c: Coincident(g30,g14)
    c: InternalAlignment(g27,g30)
    c: InternalAlignment(g28,g30)
    c: InternalAlignment(g29,g30)
    c: InternalAlignment(g31,g30)
    c: InternalAlignment(g32,g30)
    c: Coincident(g36,g12)
    c: Weight(g33) = 1
    c: Equal(g33,g34)
    c: Equal(g33,g35)
    c: Coincident(g36,g11)
    c: InternalAlignment(g33,g36)
    c: InternalAlignment(g34,g36)
    c: InternalAlignment(g35,g36)
    c: InternalAlignment(g37,g36)
    c: InternalAlignment(g38,g36)
    c: Coincident(g42,g13)
    c: Weight(g39) = 1
    c: Equal(g39,g40)
    c: Equal(g39,g41)
    c: Coincident(g42,g1)
    c: InternalAlignment(g39,g42)
    c: InternalAlignment(g40,g42)
    c: InternalAlignment(g41,g42)
    c: InternalAlignment(g43,g42)
    c: InternalAlignment(g44,g42)
    c: Block(g18)
    c: Block(g24)
    c: Block(g30)
    c: Block(g36)
    c: Block(g42)
    c: Horizontal(g45)
    c: Coincident(g45,g0)
    c: Vertical(g46)
    c: Coincident(g46,g45)
    c: Coincident(g47,g46)
    c: Coincident(g47,g18)
    c: Horizontal(g47)
    c: Block(g46)
    c: Coincident(g48,g18)
    c: Horizontal(g48)
    c: Distance(g48) = 1.33
    c: Vertical(g49)
    c: Coincident(g49,g48)
    c: Coincident(g50,g49)
    c: Coincident(g50,g24)
    c: Horizontal(g50)
    c: Tangent(g50,g22)
    c: Horizontal(g51)
    c: Coincident(g51,g24)
    c: Block(g51)
    c: Vertical(g52)
    c: Block(g52)
    c: Coincident(g52,g51)
    c: Coincident(g53,g52)
    c: Coincident(g53,g30)
    c: Horizontal(g53)
    c: Distance(g1) = 8.5
FEATURE [Part::Feature] Face024
  shape: bbox 9.8 x 26.5 x 2e-07 mm, 1 faces, 0 solids (baked)
FEATURE [Part::Revolution] Revolve024
  Angle = 360
  Axis = (0,1,0)
  Base = (0,0,0)
  FaceMakerClass = Part::FaceMakerBullseye
  Placement = pos=(0,0,0) rot=(0,0,1;1.5708rad)
  Solid = false
  Source = -> Face024
  Symmetric = false
FEATURE [Part::Feature] Face025
  shape: bbox 9.8 x 26.5 x 2e-07 mm, 1 faces, 0 solids (baked)
FEATURE [Part::Revolution] Revolve025
  Angle = 360
  Axis = (0,1,0)
  Base = (0,0,0)
  FaceMakerClass = Part::FaceMakerBullseye
  Placement = pos=(0,0,0) rot=(0,0,1;1.5708rad)
  Solid = false
  Source = -> Face025
  Symmetric = false
FEATURE [Part::MultiFuse] Fusion033
  Placement = pos=(-18,19,36) rot=(0,0,1;0rad)
  Shapes = -> [Revolve025,Revolve024]
FEATURE [Part::Cylinder] Cylinder014
  Angle = 360
  AttacherType = Attacher::AttachEngine3D
  Height = 20
  Placement = pos=(0,0,36.15) rot=(0,0,1;0rad)
  Radius = 14.3
FEATURE [Part::Cylinder] Cylinder015
  Angle = 360
  AttacherType = Attacher::AttachEngine3D
  Height = 10
  Placement = pos=(0,0,36.15) rot=(0,0,1;0rad)
  Radius = 4
FEATURE [Part::MultiFuse] Fusion034  label="removeToCreteHoleForPlugHousing004"
  Placement = pos=(-42,19,36) rot=(0,1,0;1.5708rad)
  Shapes = -> [Cylinder014,Cylinder015]
FEATURE [Part::Cut] Cut008  label="top004"
  Base = -> Cut004
  Placement = pos=(-1,0,0) rot=(0,0,1;0rad)
  Tool = -> Fusion034
FEATURE [Part::Box] Box005  label="Cube005"
  AttacherType = Attacher::AttachEngine3D
  Height = 28
  Length = 3
  Placement = pos=(110.7,19,22) rot=(0,0,1;0rad)
  Width = 15.7
FEATURE [Part::Cylinder] Cylinder016
  Angle = 360
  AttacherType = Attacher::AttachEngine3D
  Height = 10
  Placement = pos=(0,0,36.15) rot=(0,0,1;0rad)
  Radius = 4
FEATURE [Part::Cylinder] Cylinder017
  Angle = 360
  AttacherType = Attacher::AttachEngine3D
  Height = 20
  Placement = pos=(0,0,36.15) rot=(0,0,1;0rad)
  Radius = 10.3
FEATURE [Part::MultiFuse] Fusion035  label="removeToCreteHoleForPlugHousing005"
  Placement = pos=(70,19,36) rot=(0,1,0;1.5708rad)
  Shapes = -> [Cylinder017,Cylinder016]
FEATURE [Part::Cut] Cut009  label="plugHousingTab001"
  Base = -> Box005
  Placement = pos=(-107.4,-14,0) rot=(0,0,1;0rad)
  Tool = -> Fusion035
FEATURE [Part::Box] Box006  label="Cube006"
  AttacherType = Attacher::AttachEngine3D
  Height = 28
  Length = 3
  Placement = pos=(110.7,19,22) rot=(0,0,1;0rad)
  Width = 15.7
FEATURE [Part::Cylinder] Cylinder018
  Angle = 360
  AttacherType = Attacher::AttachEngine3D
  Height = 10
  Placement = pos=(0,0,36.15) rot=(0,0,1;0rad)
  Radius = 4
FEATURE [Part::Cylinder] Cylinder019
  Angle = 360
  AttacherType = Attacher::AttachEngine3D
  Height = 20
  Placement = pos=(0,0,36.15) rot=(0,0,1;0rad)
  Radius = 10.3
FEATURE [Part::MultiFuse] Fusion036  label="removeToCreteHoleForPlugHousing006"
  Placement = pos=(70,19,36) rot=(0,1,0;1.5708rad)
  Shapes = -> [Cylinder019,Cylinder018]
FEATURE [Part::Cut] Cut010  label="plugHousingTab002"
  Base = -> Box006
  Placement = pos=(-107.4,-14,0) rot=(0,0,1;0rad)
  Tool = -> Fusion036
FEATURE [Part::MultiFuse] Fusion037
  Placement = pos=(9.6,23,0) rot=(0,0,1;3.14159rad)
  Shapes = -> [Cut009,Cut010]
FEATURE [Part::Box] Box  label="Cube"
  AttacherType = Attacher::AttachEngine3D
  Height = 10
  Length = 3
  Placement = pos=(3.3,4,12) rot=(0,0,1;0rad)
  Width = 10
FEATURE [Part::Fillet] Fillet004
  Base = -> Fusion028
  Edges = 1 edges r=2: [Edge25]
FEATURE [Part::Fillet] Fillet005  label="plugHousing046"
  Base = -> Fillet004
  Edges = 1 edges r=2: [Edge8]
FEATURE [Part::Fillet] Fillet006
  Base = -> Box
  Edges = 1 edges r=2: [Edge11]
FEATURE [Part::Box] Box007  label="Cube007"
  AttacherType = Attacher::AttachEngine3D
  Height = 10
  Length = 3
  Placement = pos=(3.3,4,50) rot=(0,0,1;0rad)
  Width = 10
FEATURE [Part::Fillet] Fillet007
  Base = -> Box007
  Edges = 1 edges r=2: [Edge12]
FEATURE [Part::Box] Box008  label="Cube008"
  AttacherType = Attacher::AttachEngine3D
  Height = 28
  Length = 4
  Placement = pos=(5,0,22) rot=(0,0,1;0rad)
  Width = 10
FEATURE [Part::Fillet] Fillet008
  Base = -> Box008
  Edges = 1 edges r=1: [Edge7]
FEATURE [Part::Fillet] Fillet009
  Base = -> Fillet008
  Edges = 1 edges r=2: [Edge5]
FEATURE [Part::Fillet] Fillet010
  Base = -> Fillet009
  Edges = 1 edges r=2: [Edge2]
FEATURE [Sketcher::SketchObject] Sketch009  label="topSketch003"
  FullyConstrained = true
  sketch-geometry (4):
    g0: LineSegment StartX=16.8446 StartY=31.512 StartZ=0 EndX=16.3251 EndY=34.4666 EndZ=0
    g1: ArcOfCircle CenterX=19 CenterY=19.2524 CenterZ=0 NormalX=0 NormalY=0 NormalZ=1 AngleXU=0 Radius=15.4476 StartAngle=1.74483 EndAngle=2.72717
    g2: ArcOfCircle CenterX=19 CenterY=19.2524 CenterZ=0 NormalX=0 NormalY=0 NormalZ=1 AngleXU=0 Radius=12.4476 StartAngle=1.74483 EndAngle=2.73189
    g3: LineSegment StartX=4.86004 StartY=25.4725 StartZ=0 EndX=7.58253 EndY=24.2107 EndZ=0
  constraints (7):
    c: Block(g0)
    c: Coincident(g1,g0)
    c: Coincident(g2,g0)
    c: Coincident(g3,g1)
    c: Coincident(g3,g2)
    c: Block(g1)
    c: Block(g2)
FEATURE [Part::Extrusion] Extrude008
  Base = -> Sketch009
  Dir = (0,0,1)
  DirMode = 2
  FaceMakerClass = Part::FaceMakerBullseye
  LengthFwd = 10
  LengthRev = 0
  Placement = pos=(0,0,31) rot=(0,0,1;0rad)
  Solid = true
  Symmetric = false
FEATURE [Part::Cylinder] Cylinder020
  Angle = 360
  AttacherType = Attacher::AttachEngine3D
  Height = 20
  Placement = pos=(0,0,36.15) rot=(0,0,1;0rad)
  Radius = 8.2
FEATURE [Part::Cylinder] Cylinder021
  Angle = 360
  AttacherType = Attacher::AttachEngine3D
  Height = 10
  Placement = pos=(0,0,36.15) rot=(0,0,1;0rad)
  Radius = 4
FEATURE [Part::MultiFuse] Fusion038  label="removeToCreteHoleForPlugHousing007"
  Placement = pos=(-42,19,36) rot=(0,1,0;1.5708rad)
  Shapes = -> [Cylinder020,Cylinder021]
FEATURE [Part::Cut] Cut011
  Base = -> Extrude008
  Tool = -> Fusion038
FEATURE [Part::Fillet] Fillet011
  Base = -> Cut011
  Edges = 1 edges r=2: [Edge1]
FEATURE [Part::Fillet] Fillet012
  Base = -> Fillet011
  Edges = 1 edges r=2.5: [Edge1]
FEATURE [Part::Fillet] Fillet013
  Base = -> Fillet012
  Edges = 1 edges r=2.5: [Edge2]
FEATURE [Part::Box] Box010  label="Cube010"
  AttacherType = Attacher::AttachEngine3D
  Height = 16
  Length = 8
  Placement = pos=(12.7,31.52,28) rot=(0,0,1;0rad)
  Width = 4
FEATURE [Sketcher::SketchObject] Sketch010  label="topSketch004"
  FullyConstrained = true
  sketch-geometry (4):
    g0: LineSegment StartX=16.8446 StartY=31.512 StartZ=0 EndX=16.3251 EndY=34.4666 EndZ=0
    g1: ArcOfCircle CenterX=19 CenterY=19.2524 CenterZ=0 NormalX=0 NormalY=0 NormalZ=1 AngleXU=0 Radius=15.4476 StartAngle=1.74483 EndAngle=2.72717
    g2: ArcOfCircle CenterX=19 CenterY=19.2524 CenterZ=0 NormalX=0 NormalY=0 NormalZ=1 AngleXU=0 Radius=12.4476 StartAngle=1.74483 EndAngle=2.73189
    g3: LineSegment StartX=4.86004 StartY=25.4725 StartZ=0 EndX=7.58253 EndY=24.2107 EndZ=0
  constraints (7):
    c: Block(g0)
    c: Coincident(g1,g0)
    c: Coincident(g2,g0)
    c: Coincident(g3,g1)
    c: Coincident(g3,g2)
    c: Block(g1)
    c: Block(g2)
FEATURE [Part::Cylinder] Cylinder022
  Angle = 360
  AttacherType = Attacher::AttachEngine3D
  Height = 10
  Placement = pos=(0,0,36.15) rot=(0,0,1;0rad)
  Radius = 4
FEATURE [Sketcher::SketchObject] Sketch011  label="topSketch005"
  FullyConstrained = true
  sketch-geometry (4):
    g0: LineSegment StartX=16.8446 StartY=31.512 StartZ=0 EndX=16.3251 EndY=34.4666 EndZ=0
    g1: ArcOfCircle CenterX=19 CenterY=19.2524 CenterZ=0 NormalX=0 NormalY=0 NormalZ=1 AngleXU=0 Radius=15.4476 StartAngle=1.74483 EndAngle=2.72717
    g2: ArcOfCircle CenterX=19 CenterY=19.2524 CenterZ=0 NormalX=0 NormalY=0 NormalZ=1 AngleXU=0 Radius=12.4476 StartAngle=1.74483 EndAngle=2.73189
    g3: LineSegment StartX=4.86004 StartY=25.4725 StartZ=0 EndX=7.58253 EndY=24.2107 EndZ=0
  constraints (7):
    c: Block(g0)
    c: Coincident(g1,g0)
    c: Coincident(g2,g0)
    c: Coincident(g3,g1)
    c: Coincident(g3,g2)
    c: Block(g1)
    c: Block(g2)
FEATURE [Part::Extrusion] Extrude010
  Base = -> Sketch011
  Dir = (0,0,1)
  DirMode = 2
  FaceMakerClass = Part::FaceMakerBullseye
  LengthFwd = 10.6
  LengthRev = 0
  Placement = pos=(0,0,31) rot=(0,0,1;0rad)
  Solid = true
  Symmetric = false
FEATURE [Part::Cylinder] Cylinder023
  Angle = 360
  AttacherType = Attacher::AttachEngine3D
  Height = 20
  Placement = pos=(0,0,36.15) rot=(0,0,1;0rad)
  Radius = 8.2
FEATURE [Part::MultiFuse] Fusion039  label="removeToCreteHoleForPlugHousing008"
  Placement = pos=(-42,19,36) rot=(0,1,0;1.5708rad)
  Shapes = -> [Cylinder023,Cylinder022]
FEATURE [Part::Cut] Cut012
  Base = -> Extrude010
  Placement = pos=(0,0,-0.3) rot=(0,0,1;0rad)
  Tool = -> Fusion039
FEATURE [Part::Cut] Cut013
  Base = -> Box010
  Tool = -> Cut012
FEATURE [Part::Fillet] Fillet014
  Base = -> Cut013
  Edges = 1 edges r=0.7: [Edge13]
FEATURE [Part::Fillet] Fillet015
  Base = -> Fillet014
  Edges = 1 edges r=0.7: [Edge13]
FEATURE [Part::Fillet] Fillet016
  Base = -> Fillet015
  Edges = 1 edges r=0.7: [Edge16]
FEATURE [Part::Fillet] Fillet017
  Base = -> Fillet016
  Edges = 1 edges r=0.7: [Edge11]
FEATURE [Part::Fillet] Fillet018
  Base = -> Fillet017
  Edges = 1 edges r=0.7: [Edge10]
FEATURE [Part::Fillet] Fillet019
  Base = -> Fillet018
  Edges = 1 edges r=1.2: [Edge5]
FEATURE [Part::Fillet] Fillet020
  Base = -> Fillet019
  Edges = 1 edges r=1.2: [Edge12]
FEATURE [Part::Fillet] Fillet021
  Base = -> Fillet020
  Edges = 1 edges r=2: [Edge1]
  Placement = pos=(0.3,0,0) rot=(0,0,1;0rad)
FEATURE [Part::MultiFuse] Fusion040  label="top005"
  Shapes = -> [Cut008,Fillet021]
FEATURE [Part::MultiFuse] Fusion041  label="wireHolder"
  Shapes = -> [Fusion033,Fillet013]
FEATURE [Part::MultiFuse] Fusion042
  Shapes = -> [Fillet007,Fusion041]
FEATURE [Part::MultiFuse] Fusion043  label="wireHolder001"
  Shapes = -> [Fusion042,Fillet010]
FEATURE [Part::MultiFuse] Fusion044  label="wireHolder002"
  Shapes = -> [Fillet006,Fusion037,Fusion043]
FEATURE [Part::Feature] Face026
  shape: bbox 11 x 6 x 2e-07 mm, 1 faces, 0 solids (baked)
FEATURE [Part::Revolution] Revolve026
  Angle = 360
  Axis = (0,1,0)
  Base = (0,0,0)
  FaceMakerClass = Part::FaceMakerBullseye
  Placement = pos=(30.3,-1,19.7) rot=(0,0,1;0rad)
  Solid = false
  Source = -> Face026
  Symmetric = false
FEATURE [Sketcher::SketchObject] Sketch013  label="topSketch006"
  FullyConstrained = true
  sketch-geometry (13):
    g0: LineSegment StartX=117 StartY=19 StartZ=0 EndX=117 EndY=38 EndZ=0
    g1: ArcOfCircle CenterX=98 CenterY=19 CenterZ=0 NormalX=0 NormalY=0 NormalZ=1 AngleXU=0 Radius=19 StartAngle=5.7297 EndAngle=6.28319
    g2: LineSegment StartX=0 StartY=3 StartZ=0 EndX=0 EndY=19 EndZ=0
    g3: LineSegment StartX=19 StartY=38 StartZ=0 EndX=117 EndY=38 EndZ=0
    g4: ArcOfCircle CenterX=19 CenterY=19 CenterZ=0 NormalX=0 NormalY=0 NormalZ=1 AngleXU=0 Radius=19 StartAngle=1.5708 EndAngle=3.14159
    g5: ArcOfCircle CenterX=19 CenterY=19 CenterZ=0 NormalX=0 NormalY=0 NormalZ=1 AngleXU=0 Radius=16 StartAngle=1.5708 EndAngle=3.14159
    g6: ArcOfCircle CenterX=98 CenterY=19 CenterZ=0 NormalX=0 NormalY=0 NormalZ=1 AngleXU=0 Radius=16 StartAngle=5.60905 EndAngle=6.28319
    g7: LineSegment StartX=114 StartY=19 StartZ=0 EndX=114 EndY=35 EndZ=0
    g8: LineSegment StartX=110.5 StartY=9.01251 StartZ=0 EndX=114.163 EndY=9.01251 EndZ=0
    g9: LineSegment StartX=114 StartY=35 StartZ=0 EndX=19 EndY=35 EndZ=0
    g10: LineSegment StartX=0 StartY=3 StartZ=0 EndX=0 EndY=0 EndZ=0
    g11: LineSegment StartX=3 StartY=0 StartZ=0 EndX=0 EndY=0 EndZ=0
    g12: LineSegment StartX=3 StartY=19 StartZ=0 EndX=3 EndY=0 EndZ=0
  constraints (33):
    c: Vertical(g0)
    c: Distance(g0) = 19
    c: Block(g0)
    c: Coincident(g1,g0)
    c: Block(g1)
    c: Vertical(g2)
    c: Block(g2)
    c: Coincident(g3,g0)
    c: Horizontal(g3)
    c: Distance(g3) = 98
    c: Coincident(g4,g3)
    c: Coincident(g4,g2)
    c: Block(g4)
    c: Coincident(g5,g4)
    c: Coincident(g6,g1)
    c: Block(g6)
    c: Block(g5)
    c: Coincident(g7,g6)
    c: Vertical(g7)
    c: Coincident(g8,g6)
    c: Coincident(g8,g1)
    c: Coincident(g9,g7)
    c: Coincident(g9,g5)
    c: Horizontal(g9)
    c: Tangent(g9,g5)
    c: Coincident(g10,g2)
    c: Distance(g10) = 3
    c: Vertical(g10)
    c: Coincident(g11,g10)
    c: Horizontal(g11)
    c: Coincident(g12,g5)
    c: Coincident(g12,g11)
    c: Vertical(g12)
FEATURE [Part::Extrusion] Extrude011  label="top006"
  Base = -> Sketch013
  Dir = (0,0,1)
  DirMode = 2
  FaceMakerClass = Part::FaceMakerBullseye
  LengthFwd = 72
  LengthRev = 0
  Solid = true
  Symmetric = false
FEATURE [Sketcher::SketchObject] Sketch014
  FullyConstrained = true
  MapMode = 3
  Placement = pos=(0,0,0) rot=(1,0,0;1.5708rad)
  Support = -> [Extrude011]
  sketch-geometry (8):
    g0: Circle CenterX=80.351 CenterY=-67.6202 CenterZ=0 NormalX=0 NormalY=0 NormalZ=1 AngleXU=0 Radius=2
    g1: Circle CenterX=80.351 CenterY=-67.6202 CenterZ=0 NormalX=0 NormalY=0 NormalZ=1 AngleXU=0 Radius=3
    g2: Circle CenterX=80.351 CenterY=-4.92017 CenterZ=0 NormalX=0 NormalY=0 NormalZ=1 AngleXU=0 Radius=2
    g3: Circle CenterX=80.351 CenterY=-4.92017 CenterZ=0 NormalX=0 NormalY=0 NormalZ=1 AngleXU=0 Radius=3
    g4: Circle CenterX=23.851 CenterY=-4.92017 CenterZ=0 NormalX=0 NormalY=0 NormalZ=1 AngleXU=0 Radius=2
    g5: Circle CenterX=23.851 CenterY=-4.92017 CenterZ=0 NormalX=0 NormalY=0 NormalZ=1 AngleXU=0 Radius=3
    g6: Circle CenterX=23.851 CenterY=-67.6202 CenterZ=0 NormalX=0 NormalY=0 NormalZ=1 AngleXU=0 Radius=2
    g7: Circle CenterX=23.851 CenterY=-67.6202 CenterZ=0 NormalX=0 NormalY=0 NormalZ=1 AngleXU=0 Radius=3
  constraints (8):
    c: Block(g3)
    c: Block(g2)
    c: Block(g1)
    c: Block(g0)
    c: Block(g6)
    c: Block(g7)
    c: Block(g4)
    c: Block(g5)
FEATURE [Part::Feature] Face027
  shape: bbox 11 x 6 x 2e-07 mm, 1 faces, 0 solids (baked)
FEATURE [Part::Revolution] Revolve027
  Angle = 360
  Axis = (0,1,0)
  Base = (0,0,0)
  FaceMakerClass = Part::FaceMakerBullseye
  Placement = pos=(30.3,-1,51.7) rot=(0,0,1;0rad)
  Solid = false
  Source = -> Face027
  Symmetric = false
FEATURE [Part::Feature] Face028
  shape: bbox 11 x 6 x 2e-07 mm, 1 faces, 0 solids (baked)
FEATURE [Part::Revolution] Revolve028
  Angle = 360
  Axis = (0,1,0)
  Base = (0,0,0)
  FaceMakerClass = Part::FaceMakerBullseye
  Placement = pos=(62.3,-1,19.7) rot=(0,0,1;0rad)
  Solid = false
  Source = -> Face028
  Symmetric = false
FEATURE [Part::Feature] Face029
  shape: bbox 11 x 6 x 2e-07 mm, 1 faces, 0 solids (baked)
FEATURE [Part::Revolution] Revolve029
  Angle = 360
  Axis = (0,1,0)
  Base = (0,0,0)
  FaceMakerClass = Part::FaceMakerBullseye
  Placement = pos=(62.3,-1,51.7) rot=(0,0,1;0rad)
  Solid = false
  Source = -> Face029
  Symmetric = false
FEATURE [Part::Feature] Wire
  shape: bbox 11 x 5.2 x 2e-07 mm, 0 faces, 0 solids (baked)
FEATURE [Part::Revolution] Revolve030
  Angle = 360
  Axis = (0,1,0)
  Base = (0,0,0)
  FaceMakerClass = Part::FaceMakerBullseye
  Placement = pos=(30.3,38,19.7) rot=(0,0,1;0rad)
  Solid = true
  Source = -> Wire
  Symmetric = false
FEATURE [Part::Feature] Wire001
  shape: bbox 11 x 5.2 x 2e-07 mm, 0 faces, 0 solids (baked)
FEATURE [Part::Revolution] Revolve031
  Angle = 360
  Axis = (0,1,0)
  Base = (0,0,0)
  FaceMakerClass = Part::FaceMakerBullseye
  Placement = pos=(30.3,38,51.7) rot=(0,0,1;0rad)
  Solid = true
  Source = -> Wire001
  Symmetric = false
FEATURE [Part::Feature] Wire002
  shape: bbox 11 x 5.2 x 2e-07 mm, 0 faces, 0 solids (baked)
FEATURE [Part::Revolution] Revolve032
  Angle = 360
  Axis = (0,1,0)
  Base = (0,0,0)
  FaceMakerClass = Part::FaceMakerBullseye
  Placement = pos=(62.3,38,51.7) rot=(0,0,1;0rad)
  Solid = true
  Source = -> Wire002
  Symmetric = false
FEATURE [Part::Feature] Wire003
  shape: bbox 11 x 5.2 x 2e-07 mm, 0 faces, 0 solids (baked)
FEATURE [Part::Revolution] Revolve033
  Angle = 360
  Axis = (0,1,0)
  Base = (0,0,0)
  FaceMakerClass = Part::FaceMakerBullseye
  Placement = pos=(62.3,38,19.7) rot=(0,0,1;0rad)
  Solid = true
  Source = -> Wire003
  Symmetric = false
FEATURE [Part::MultiFuse] Fusion045  label="altRandScrewHousing"
  Shapes = -> [Revolve029,Revolve027,Revolve028,Revolve026]
FEATURE [Part::MultiFuse] Fusion046  label="fanScrewHousing"
  Shapes = -> [Revolve033,Revolve032,Revolve031,Revolve030]
FEATURE [Sketcher::SketchObject] Sketch015
  FullyConstrained = true
  sketch-geometry (17):
    g0: Circle CenterX=-3.5 CenterY=23.5 CenterZ=0 NormalX=0 NormalY=0 NormalZ=1 AngleXU=0 Radius=1
    g1: Circle CenterX=-1 CenterY=15.25 CenterZ=0 NormalX=0 NormalY=0 NormalZ=1 AngleXU=0 Radius=1
    g2: Circle CenterX=-3.5 CenterY=7 CenterZ=0 NormalX=0 NormalY=0 NormalZ=1 AngleXU=0 Radius=1
    g3: BSplineCurve PolesCount=3 KnotsCount=2 Degree=2 IsPeriodic=0
    g4: GeomPoint X=-3.5 Y=23.5 Z=0
    g5: GeomPoint X=-3.5 Y=7 Z=0
    g6: Circle CenterX=-4.8 CenterY=30.5 CenterZ=0 NormalX=0 NormalY=0 NormalZ=1 AngleXU=0 Radius=1
    g7: Circle CenterX=-3.5 CenterY=30.5 CenterZ=0 NormalX=0 NormalY=0 NormalZ=1 AngleXU=0 Radius=1
    g8: Circle CenterX=-3.5 CenterY=29.2 CenterZ=0 NormalX=0 NormalY=0 NormalZ=1 AngleXU=0 Radius=1
    g9: BSplineCurve PolesCount=3 KnotsCount=2 Degree=2 IsPeriodic=0
    g10: GeomPoint X=-4.8 Y=30.5 Z=0
    g11: GeomPoint X=-3.5 Y=29.2 Z=0
    g12: LineSegment StartX=-3.5 StartY=29.2 StartZ=0 EndX=-3.5 EndY=23.5 EndZ=0
    g13: LineSegment StartX=-4.8 StartY=30.5 StartZ=0 EndX=0 EndY=30.5 EndZ=0
    g14: LineSegment StartX=-3.5 StartY=0.3 StartZ=0 EndX=0 EndY=0.3 EndZ=0
    g15: LineSegment StartX=-3.5 StartY=0.3 StartZ=0 EndX=-3.5 EndY=7 EndZ=0
    g16: LineSegment StartX=0 StartY=0.3 StartZ=0 EndX=0 EndY=30.5 EndZ=0
  constraints (34):
    c: Weight(g0) = 1
    c: Equal(g0,g1)
    c: Equal(g0,g2)
    c: InternalAlignment(g0,g3)
    c: InternalAlignment(g1,g3)
    c: InternalAlignment(g2,g3)
    c: InternalAlignment(g4,g3)
    c: InternalAlignment(g5,g3)
    c: Block(g3)
    c: Weight(g6) = 1
    c: Equal(g6,g7)
    c: Equal(g6,g8)
    c: InternalAlignment(g6,g9)
    c: InternalAlignment(g7,g9)
    c: InternalAlignment(g8,g9)
    c: InternalAlignment(g10,g9)
    c: InternalAlignment(g11,g9)
    c: Block(g9)
    c: Coincident(g12,g9)
    c: Coincident(g12,g3)
    c: Vertical(g12)
    c: Coincident(g13,g9)
    c: Horizontal(g13)
    c: Distance(g13) = 4.8
    c: Horizontal(g14)
    c: Block(g14)
    c: Coincident(g15,g14)
    c: Coincident(g15,g3)
    c: Vertical(g15)
    c: Coincident(g16,g14)
    c: Coincident(g16,g13)
    c: Vertical(g16)
    c: Tangent(g16,g1)
    c: Distance(g14) = 3.5
FEATURE [Sketcher::SketchObject] Sketch016
  FullyConstrained = true
  sketch-geometry (16):
    g0: Circle CenterX=-3.5 CenterY=23.5 CenterZ=0 NormalX=0 NormalY=0 NormalZ=1 AngleXU=0 Radius=1
    g1: Circle CenterX=-1 CenterY=15.25 CenterZ=0 NormalX=0 NormalY=0 NormalZ=1 AngleXU=0 Radius=1
    g2: Circle CenterX=-3.5 CenterY=7 CenterZ=0 NormalX=0 NormalY=0 NormalZ=1 AngleXU=0 Radius=1
    g3: BSplineCurve PolesCount=3 KnotsCount=2 Degree=2 IsPeriodic=0
    g4: GeomPoint X=-3.5 Y=23.5 Z=0
    g5: GeomPoint X=-3.5 Y=7 Z=0
    g6: LineSegment StartX=-3.5 StartY=28.2 StartZ=0 EndX=-3.5 EndY=23.5 EndZ=0
    g7: LineSegment StartX=0 StartY=29.5 StartZ=0 EndX=0 EndY=30 EndZ=0
    g8: LineSegment StartX=-3.5 StartY=28.2 StartZ=0 EndX=-3.5 EndY=30 EndZ=0
    g9: LineSegment StartX=0 StartY=30 StartZ=0 EndX=0 EndY=30.5 EndZ=0
    g10: LineSegment StartX=0 StartY=30.5 StartZ=0 EndX=-3.5 EndY=30.5 EndZ=0
    g11: LineSegment StartX=-3.5 StartY=30.5 StartZ=0 EndX=-3.5 EndY=30 EndZ=0
    g12: LineSegment StartX=0 StartY=29.5 StartZ=0 EndX=0 EndY=5 EndZ=0
    g13: LineSegment StartX=-3.5 StartY=0.3 StartZ=0 EndX=-3.5 EndY=7 EndZ=0
    g14: LineSegment StartX=-3.5 StartY=0.3 StartZ=0 EndX=0 EndY=0.3 EndZ=0
    g15: LineSegment StartX=0 StartY=5 StartZ=0 EndX=0 EndY=0.3 EndZ=0
  constraints (39):
    c: Weight(g0) = 1
    c: Equal(g0,g1)
    c: Equal(g0,g2)
    c: InternalAlignment(g0,g3)
    c: InternalAlignment(g1,g3)
    c: InternalAlignment(g2,g3)
    c: InternalAlignment(g4,g3)
    c: InternalAlignment(g5,g3)
    c: Block(g3)
    c: Coincident(g6,g3)
    c: Vertical(g6)
    c: Vertical(g7)
    c: Distance(g7) = 0.5
    c: Coincident(g8,g6)
    c: Vertical(g8)
    c: Block(g6)
    c: Block(g7)
    c: Vertical(g9)
    c: Equal(g7,g9) = 0.5
    c: Block(g9)
    c: Coincident(g9,g7)
    c: Horizontal(g10)
    c: Coincident(g10,g9)
    c: Coincident(g11,g10)
    c: Coincident(g11,g8)
    c: Vertical(g11)
    c: Block(g11)
    c: Coincident(g12,g7)
    c: Vertical(g12)
    c: Coincident(g13,g3)
    c: Vertical(g13)
    c: Distance(g13) = 6.7
    c: Coincident(g14,g13)
    c: Horizontal(g14)
    c: Block(g14)
    c: Coincident(g15,g12)
    c: Coincident(g15,g14)
    c: Vertical(g15)
    c: Block(g15)
FEATURE [Sketcher::SketchObject] Sketch017
  FullyConstrained = true
  sketch-geometry (11):
    g0: LineSegment StartX=-3.5 StartY=1e-16 StartZ=0 EndX=-1.6 EndY=1e-16 EndZ=0
    g1: LineSegment StartX=-1.6 StartY=1e-16 StartZ=0 EndX=-1.6 EndY=1.5 EndZ=0
    g2: LineSegment StartX=-3.5 StartY=1.5 StartZ=0 EndX=-1.6 EndY=1.5 EndZ=0
    g3: LineSegment StartX=-3.5 StartY=1e-16 StartZ=0 EndX=-4.8 EndY=1e-16 EndZ=0
    g4: Circle CenterX=-3.5 CenterY=1.3 CenterZ=0 NormalX=0 NormalY=0 NormalZ=1 AngleXU=0 Radius=1
    g5: Circle CenterX=-3.5 CenterY=1e-16 CenterZ=0 NormalX=0 NormalY=0 NormalZ=1 AngleXU=0 Radius=1
    g6: Circle CenterX=-4.8 CenterY=1e-16 CenterZ=0 NormalX=0 NormalY=0 NormalZ=1 AngleXU=0 Radius=1
    g7: BSplineCurve PolesCount=3 KnotsCount=2 Degree=2 IsPeriodic=0
    g8: GeomPoint X=-3.5 Y=1.3 Z=0
    g9: GeomPoint X=-4.8 Y=1e-16 Z=0
    g10: LineSegment StartX=-3.5 StartY=1.3 StartZ=0 EndX=-3.5 EndY=1.5 EndZ=0
  constraints (24):
    c: Horizontal(g0)
    c: Distance(g0) = 1.9
    c: Block(g0)
    c: Coincident(g1,g0)
    c: Vertical(g1)
    c: Coincident(g2,g1)
    c: Horizontal(g2)
    c: Coincident(g3,g0)
    c: Horizontal(g3)
    c: Distance(g3) = 1.3
    c: Weight(g4) = 1
    c: Equal(g4,g5)
    c: Coincident(g5,g0)
    c: Equal(g4,g6)
    c: Coincident(g7,g3)
    c: InternalAlignment(g4,g7)
    c: InternalAlignment(g5,g7)
    c: InternalAlignment(g6,g7)
    c: InternalAlignment(g8,g7)
    c: InternalAlignment(g9,g7)
    c: Coincident(g10,g7)
    c: Coincident(g10,g2)
    c: Vertical(g10)
    c: Block(g10)
FEATURE [Part::Feature] Face035
  shape: bbox 3.2 x 1.5 x 2e-07 mm, 1 faces, 0 solids (baked)
FEATURE [Part::Revolution] Revolve039  label="backCaseScrewRetainer"
  Angle = 360
  Axis = (0,1,0)
  Base = (0,0,0)
  FaceMakerClass = Part::FaceMakerBullseye
  Placement = pos=(12.5,3,62) rot=(0,0,1;0rad)
  Solid = false
  Source = -> Face035
  Symmetric = false
FEATURE [Part::Feature] Face036
  shape: bbox 3.2 x 1.5 x 2e-07 mm, 1 faces, 0 solids (baked)
FEATURE [Part::Feature] Face039
  shape: bbox 4.8 x 30.2 x 2e-07 mm, 1 faces, 0 solids (baked)
FEATURE [Part::Revolution] Revolve043  label="frontCaseScrewPost002"
  Angle = 360
  Axis = (0,1,0)
  Base = (0,0,0)
  FaceMakerClass = Part::FaceMakerBullseye
  Placement = pos=(89.5,4.5,3.5) rot=(0,0,1;0rad)
  Solid = false
  Source = -> Face039
  Symmetric = false
FEATURE [Part::Feature] Face042
  shape: bbox 4.8 x 30.2 x 2e-07 mm, 1 faces, 0 solids (baked)
FEATURE [Part::Revolution] Revolve046  label="frontCaseScrewPost003"
  Angle = 360
  Axis = (0,1,0)
  Base = (0,0,0)
  FaceMakerClass = Part::FaceMakerBullseye
  Placement = pos=(89.5,4.5,68.5) rot=(0,0,1;0rad)
  Solid = false
  Source = -> Face042
  Symmetric = false
FEATURE [Part::Feature] Face043
  shape: bbox 3.2 x 1.5 x 2e-07 mm, 1 faces, 0 solids (baked)
FEATURE [Part::Revolution] Revolve047  label="frontCaseScrewRetainer002"
  Angle = 360
  Axis = (0,1,0)
  Base = (0,0,0)
  FaceMakerClass = Part::FaceMakerBullseye
  Placement = pos=(89.5,3,68.5) rot=(0,0,1;0rad)
  Solid = false
  Source = -> Face043
  Symmetric = false
FEATURE [Part::Feature] Face044
  shape: bbox 3.2 x 1.5 x 2e-07 mm, 1 faces, 0 solids (baked)
FEATURE [Part::Revolution] Revolve048  label="frontCaseScrewRetainer003"
  Angle = 360
  Axis = (0,1,0)
  Base = (0,0,0)
  FaceMakerClass = Part::FaceMakerBullseye
  Placement = pos=(89.5,3,3.5) rot=(0,0,1;0rad)
  Solid = false
  Source = -> Face044
  Symmetric = false
FEATURE [App::MeasureDistance] Distance002  label="Distance: 1.67 mm"
  Distance = 1.66921
  P1 = (99.2361,4.7524,71.7)
  P2 = (99.2347,6.42161,71.7)
FEATURE [Sketcher::SketchObject] Sketch018
  FullyConstrained = true
  sketch-geometry (7):
    g0: LineSegment StartX=0 StartY=0 StartZ=0 EndX=0 EndY=6 EndZ=0
    g1: Circle CenterX=0 CenterY=0 CenterZ=0 NormalX=0 NormalY=0 NormalZ=1 AngleXU=0 Radius=1
    g2: Circle CenterX=8 CenterY=6 CenterZ=0 NormalX=0 NormalY=0 NormalZ=1 AngleXU=0 Radius=1
    g3: BSplineCurve PolesCount=3 KnotsCount=2 Degree=2 IsPeriodic=0
    g4: GeomPoint X=0 Y=0 Z=0
    g5: GeomPoint X=8 Y=6 Z=0
    g6: LineSegment StartX=0 StartY=6 StartZ=0 EndX=8 EndY=6 EndZ=0
  constraints (14):
    c: Coincident(g0,g-1)
    c: Distance(g0) = 6
    c: Vertical(g0)
    c: Coincident(g3,g0)
    c: Weight(g1) = 1
    c: Equal(g1,g2)
    c: InternalAlignment(g1,g3)
    c: InternalAlignment(g2,g3)
    c: InternalAlignment(g4,g3)
    c: InternalAlignment(g5,g3)
    c: Block(g3)
    c: Coincident(g6,g0)
    c: Coincident(g6,g3)
    c: Horizontal(g6)
FEATURE [Part::Extrusion] Extrude012  label="caseScrewPillarBracket"
  Base = -> Sketch018
  Dir = (0,0,1)
  DirMode = 2
  FaceMakerClass = Part::FaceMakerBullseye
  LengthFwd = 2.4
  LengthRev = 0
  Placement = pos=(15.76,29,8.8) rot=(0,1,0;0rad)
  Solid = true
  Symmetric = false
FEATURE [Sketcher::SketchObject] Sketch019
  FullyConstrained = true
  sketch-geometry (7):
    g0: LineSegment StartX=0 StartY=0 StartZ=0 EndX=0 EndY=6 EndZ=0
    g1: Circle CenterX=0 CenterY=0 CenterZ=0 NormalX=0 NormalY=0 NormalZ=1 AngleXU=0 Radius=1
    g2: Circle CenterX=8 CenterY=6 CenterZ=0 NormalX=0 NormalY=0 NormalZ=1 AngleXU=0 Radius=1
    g3: BSplineCurve PolesCount=3 KnotsCount=2 Degree=2 IsPeriodic=0
    g4: GeomPoint X=0 Y=0 Z=0
    g5: GeomPoint X=8 Y=6 Z=0
    g6: LineSegment StartX=0 StartY=6 StartZ=0 EndX=8 EndY=6 EndZ=0
  constraints (14):
    c: Coincident(g0,g-1)
    c: Distance(g0) = 6
    c: Vertical(g0)
    c: Coincident(g3,g0)
    c: Weight(g1) = 1
    c: Equal(g1,g2)
    c: InternalAlignment(g1,g3)
    c: InternalAlignment(g2,g3)
    c: InternalAlignment(g4,g3)
    c: InternalAlignment(g5,g3)
    c: Block(g3)
    c: Coincident(g6,g0)
    c: Coincident(g6,g3)
    c: Horizontal(g6)
FEATURE [Part::Extrusion] Extrude013  label="caseScrewPillarBracket001"
  Base = -> Sketch019
  Dir = (0,0,1)
  DirMode = 2
  FaceMakerClass = Part::FaceMakerBullseye
  LengthFwd = 2.4
  LengthRev = 0
  Placement = pos=(15.76,29,60.8) rot=(0,0,1;0rad)
  Solid = true
  Symmetric = false
FEATURE [Sketcher::SketchObject] Sketch020
  FullyConstrained = true
  sketch-geometry (7):
    g0: LineSegment StartX=0 StartY=0 StartZ=0 EndX=0 EndY=6 EndZ=0
    g1: Circle CenterX=0 CenterY=0 CenterZ=0 NormalX=0 NormalY=0 NormalZ=1 AngleXU=0 Radius=1
    g2: Circle CenterX=8 CenterY=6 CenterZ=0 NormalX=0 NormalY=0 NormalZ=1 AngleXU=0 Radius=1
    g3: BSplineCurve PolesCount=3 KnotsCount=2 Degree=2 IsPeriodic=0
    g4: GeomPoint X=0 Y=0 Z=0
    g5: GeomPoint X=8 Y=6 Z=0
    g6: LineSegment StartX=0 StartY=6 StartZ=0 EndX=8 EndY=6 EndZ=0
  constraints (14):
    c: Coincident(g0,g-1)
    c: Distance(g0) = 6
    c: Vertical(g0)
    c: Coincident(g3,g0)
    c: Weight(g1) = 1
    c: Equal(g1,g2)
    c: InternalAlignment(g1,g3)
    c: InternalAlignment(g2,g3)
    c: InternalAlignment(g4,g3)
    c: InternalAlignment(g5,g3)
    c: Block(g3)
    c: Coincident(g6,g0)
    c: Coincident(g6,g3)
    c: Horizontal(g6)
FEATURE [Part::Extrusion] Extrude014  label="caseScrewPillarBracket002"
  Base = -> Sketch020
  Dir = (0,0,1)
  DirMode = 2
  FaceMakerClass = Part::FaceMakerBullseye
  LengthFwd = 2.4
  LengthRev = 0
  Placement = pos=(13.7,29,13.26) rot=(0,-1,0;1.5708rad)
  Solid = true
  Symmetric = false
FEATURE [Sketcher::SketchObject] Sketch021
  FullyConstrained = true
  sketch-geometry (7):
    g0: LineSegment StartX=0 StartY=0 StartZ=0 EndX=0 EndY=6 EndZ=0
    g1: Circle CenterX=0 CenterY=0 CenterZ=0 NormalX=0 NormalY=0 NormalZ=1 AngleXU=0 Radius=1
    g2: Circle CenterX=8 CenterY=6 CenterZ=0 NormalX=0 NormalY=0 NormalZ=1 AngleXU=0 Radius=1
    g3: BSplineCurve PolesCount=3 KnotsCount=2 Degree=2 IsPeriodic=0
    g4: GeomPoint X=0 Y=0 Z=0
    g5: GeomPoint X=8 Y=6 Z=0
    g6: LineSegment StartX=0 StartY=6 StartZ=0 EndX=8 EndY=6 EndZ=0
  constraints (14):
    c: Coincident(g0,g-1)
    c: Distance(g0) = 6
    c: Vertical(g0)
    c: Coincident(g3,g0)
    c: Weight(g1) = 1
    c: Equal(g1,g2)
    c: InternalAlignment(g1,g3)
    c: InternalAlignment(g2,g3)
    c: InternalAlignment(g4,g3)
    c: InternalAlignment(g5,g3)
    c: Block(g3)
    c: Coincident(g6,g0)
    c: Coincident(g6,g3)
    c: Horizontal(g6)
FEATURE [Part::Extrusion] Extrude015  label="caseScrewPillarBracket003"
  Base = -> Sketch021
  Dir = (0,0,1)
  DirMode = 2
  FaceMakerClass = Part::FaceMakerBullseye
  LengthFwd = 2.4
  LengthRev = 0
  Placement = pos=(11.3,29,58.74) rot=(0,1,0;1.5708rad)
  Solid = true
  Symmetric = false
FEATURE [Sketcher::SketchObject] Sketch022
  FullyConstrained = true
  sketch-geometry (7):
    g0: LineSegment StartX=0 StartY=0 StartZ=0 EndX=0 EndY=6 EndZ=0
    g1: Circle CenterX=0 CenterY=0 CenterZ=0 NormalX=0 NormalY=0 NormalZ=1 AngleXU=0 Radius=1
    g2: Circle CenterX=8 CenterY=6 CenterZ=0 NormalX=0 NormalY=0 NormalZ=1 AngleXU=0 Radius=1
    g3: BSplineCurve PolesCount=3 KnotsCount=2 Degree=2 IsPeriodic=0
    g4: GeomPoint X=0 Y=0 Z=0
    g5: GeomPoint X=8 Y=6 Z=0
    g6: LineSegment StartX=0 StartY=6 StartZ=0 EndX=8 EndY=6 EndZ=0
  constraints (14):
    c: Coincident(g0,g-1)
    c: Distance(g0) = 6
    c: Vertical(g0)
    c: Coincident(g3,g0)
    c: Weight(g1) = 1
    c: Equal(g1,g2)
    c: InternalAlignment(g1,g3)
    c: InternalAlignment(g2,g3)
    c: InternalAlignment(g4,g3)
    c: InternalAlignment(g5,g3)
    c: Block(g3)
    c: Coincident(g6,g0)
    c: Coincident(g6,g3)
    c: Horizontal(g6)
FEATURE [Part::Extrusion] Extrude016  label="caseScrewPillarBracket004"
  Base = -> Sketch022
  Dir = (0,0,1)
  DirMode = 2
  FaceMakerClass = Part::FaceMakerBullseye
  LengthFwd = 2.4
  LengthRev = 0
  Placement = pos=(88.3,29,65.23) rot=(0,1,0;1.5708rad)
  Solid = true
  Symmetric = false
FEATURE [Sketcher::SketchObject] Sketch023
  FullyConstrained = true
  sketch-geometry (7):
    g0: LineSegment StartX=0 StartY=0 StartZ=0 EndX=0 EndY=6 EndZ=0
    g1: Circle CenterX=0 CenterY=0 CenterZ=0 NormalX=0 NormalY=0 NormalZ=1 AngleXU=0 Radius=1
    g2: Circle CenterX=8 CenterY=6 CenterZ=0 NormalX=0 NormalY=0 NormalZ=1 AngleXU=0 Radius=1
    g3: BSplineCurve PolesCount=3 KnotsCount=2 Degree=2 IsPeriodic=0
    g4: GeomPoint X=0 Y=0 Z=0
    g5: GeomPoint X=8 Y=6 Z=0
    g6: LineSegment StartX=0 StartY=6 StartZ=0 EndX=8 EndY=6 EndZ=0
  constraints (14):
    c: Coincident(g0,g-1)
    c: Distance(g0) = 6
    c: Vertical(g0)
    c: Coincident(g3,g0)
    c: Weight(g1) = 1
    c: Equal(g1,g2)
    c: InternalAlignment(g1,g3)
    c: InternalAlignment(g2,g3)
    c: InternalAlignment(g4,g3)
    c: InternalAlignment(g5,g3)
    c: Block(g3)
    c: Coincident(g6,g0)
    c: Coincident(g6,g3)
    c: Horizontal(g6)
FEATURE [Part::Extrusion] Extrude017  label="caseScrewPillarBracket005"
  Base = -> Sketch023
  Dir = (0,0,1)
  DirMode = 2
  FaceMakerClass = Part::FaceMakerBullseye
  LengthFwd = 2.4
  LengthRev = 0
  Placement = pos=(90.7,29,6.77) rot=(0,-1,0;1.5708rad)
  Solid = true
  Symmetric = false
FEATURE [Sketcher::SketchObject] Sketch024
  FullyConstrained = true
  sketch-geometry (7):
    g0: LineSegment StartX=0 StartY=0 StartZ=0 EndX=0 EndY=6 EndZ=0
    g1: Circle CenterX=0 CenterY=0 CenterZ=0 NormalX=0 NormalY=0 NormalZ=1 AngleXU=0 Radius=1
    g2: Circle CenterX=8 CenterY=6 CenterZ=0 NormalX=0 NormalY=0 NormalZ=1 AngleXU=0 Radius=1
    g3: BSplineCurve PolesCount=3 KnotsCount=2 Degree=2 IsPeriodic=0
    g4: GeomPoint X=0 Y=0 Z=0
    g5: GeomPoint X=8 Y=6 Z=0
    g6: LineSegment StartX=0 StartY=6 StartZ=0 EndX=8 EndY=6 EndZ=0
  constraints (14):
    c: Coincident(g0,g-1)
    c: Distance(g0) = 6
    c: Vertical(g0)
    c: Coincident(g3,g0)
    c: Weight(g1) = 1
    c: Equal(g1,g2)
    c: InternalAlignment(g1,g3)
    c: InternalAlignment(g2,g3)
    c: InternalAlignment(g4,g3)
    c: InternalAlignment(g5,g3)
    c: Block(g3)
    c: Coincident(g6,g0)
    c: Coincident(g6,g3)
    c: Horizontal(g6)
FEATURE [Part::Extrusion] Extrude018  label="caseScrewPillarBracket006"
  Base = -> Sketch024
  Dir = (0,0,1)
  DirMode = 2
  FaceMakerClass = Part::FaceMakerBullseye
  LengthFwd = 2.4
  LengthRev = 0
  Placement = pos=(103.7,29,6.77) rot=(0,-1,0;1.5708rad)
  Solid = true
  Symmetric = false
FEATURE [Sketcher::SketchObject] Sketch025
  FullyConstrained = true
  sketch-geometry (7):
    g0: LineSegment StartX=0 StartY=0 StartZ=0 EndX=0 EndY=6 EndZ=0
    g1: Circle CenterX=0 CenterY=0 CenterZ=0 NormalX=0 NormalY=0 NormalZ=1 AngleXU=0 Radius=1
    g2: Circle CenterX=8 CenterY=6 CenterZ=0 NormalX=0 NormalY=0 NormalZ=1 AngleXU=0 Radius=1
    g3: BSplineCurve PolesCount=3 KnotsCount=2 Degree=2 IsPeriodic=0
    g4: GeomPoint X=0 Y=0 Z=0
    g5: GeomPoint X=8 Y=6 Z=0
    g6: LineSegment StartX=0 StartY=6 StartZ=0 EndX=8 EndY=6 EndZ=0
  constraints (14):
    c: Coincident(g0,g-1)
    c: Distance(g0) = 6
    c: Vertical(g0)
    c: Coincident(g3,g0)
    c: Weight(g1) = 1
    c: Equal(g1,g2)
    c: InternalAlignment(g1,g3)
    c: InternalAlignment(g2,g3)
    c: InternalAlignment(g4,g3)
    c: InternalAlignment(g5,g3)
    c: Block(g3)
    c: Coincident(g6,g0)
    c: Coincident(g6,g3)
    c: Horizontal(g6)
FEATURE [Part::Extrusion] Extrude019  label="caseScrewPillarBracket007"
  Base = -> Sketch025
  Dir = (0,0,1)
  DirMode = 2
  FaceMakerClass = Part::FaceMakerBullseye
  LengthFwd = 2.4
  LengthRev = 0
  Placement = pos=(101.3,29,65.23) rot=(0,1,0;1.5708rad)
  Solid = true
  Symmetric = false
FEATURE [Part::Box] Box011  label="frontCaseScrewPillarBracket"
  AttacherType = Attacher::AttachEngine3D
  Height = 2.4
  Length = 16
  Placement = pos=(87,28,2.3) rot=(0,0,1;0rad)
  Width = 7
FEATURE [Part::Box] Box012  label="frontCaseScrewPillarBracket001"
  AttacherType = Attacher::AttachEngine3D
  Height = 2.4
  Length = 16
  Placement = pos=(87,28,67.3) rot=(0,0,1;0rad)
  Width = 7
FEATURE [Sketcher::SketchObject] Sketch026
  FullyConstrained = true
  sketch-geometry (17):
    g0: Circle CenterX=-3.5 CenterY=23.5 CenterZ=0 NormalX=0 NormalY=0 NormalZ=1 AngleXU=0 Radius=1
    g1: Circle CenterX=-1 CenterY=15.25 CenterZ=0 NormalX=0 NormalY=0 NormalZ=1 AngleXU=0 Radius=1
    g2: Circle CenterX=-3.5 CenterY=7 CenterZ=0 NormalX=0 NormalY=0 NormalZ=1 AngleXU=0 Radius=1
    g3: BSplineCurve PolesCount=3 KnotsCount=2 Degree=2 IsPeriodic=0
    g4: GeomPoint X=-3.5 Y=23.5 Z=0
    g5: GeomPoint X=-3.5 Y=7 Z=0
    g6: Circle CenterX=-4.8 CenterY=30.5 CenterZ=0 NormalX=0 NormalY=0 NormalZ=1 AngleXU=0 Radius=1
    g7: Circle CenterX=-3.5 CenterY=30.5 CenterZ=0 NormalX=0 NormalY=0 NormalZ=1 AngleXU=0 Radius=1
    g8: Circle CenterX=-3.5 CenterY=29.2 CenterZ=0 NormalX=0 NormalY=0 NormalZ=1 AngleXU=0 Radius=1
    g9: BSplineCurve PolesCount=3 KnotsCount=2 Degree=2 IsPeriodic=0
    g10: GeomPoint X=-4.8 Y=30.5 Z=0
    g11: GeomPoint X=-3.5 Y=29.2 Z=0
    g12: LineSegment StartX=-3.5 StartY=29.2 StartZ=0 EndX=-3.5 EndY=23.5 EndZ=0
    g13: LineSegment StartX=-4.8 StartY=30.5 StartZ=0 EndX=0 EndY=30.5 EndZ=0
    g14: LineSegment StartX=-3.5 StartY=5 StartZ=0 EndX=-3.5 EndY=7 EndZ=0
    g15: LineSegment StartX=0 StartY=5 StartZ=0 EndX=0 EndY=30.5 EndZ=0
    g16: LineSegment StartX=-3.5 StartY=5 StartZ=0 EndX=0 EndY=5 EndZ=0
  constraints (33):
    c: Weight(g0) = 1
    c: Equal(g0,g1)
    c: Equal(g0,g2)
    c: InternalAlignment(g0,g3)
    c: InternalAlignment(g1,g3)
    c: InternalAlignment(g2,g3)
    c: InternalAlignment(g4,g3)
    c: InternalAlignment(g5,g3)
    c: Block(g3)
    c: Weight(g6) = 1
    c: Equal(g6,g7)
    c: Equal(g6,g8)
    c: InternalAlignment(g6,g9)
    c: InternalAlignment(g7,g9)
    c: InternalAlignment(g8,g9)
    c: InternalAlignment(g10,g9)
    c: InternalAlignment(g11,g9)
    c: Block(g9)
    c: Coincident(g12,g9)
    c: Coincident(g12,g3)
    c: Vertical(g12)
    c: Coincident(g13,g9)
    c: Horizontal(g13)
    c: Distance(g13) = 4.8
    c: Coincident(g14,g3)
    c: Vertical(g14)
    c: Coincident(g15,g13)
    c: Vertical(g15)
    c: Tangent(g15,g1)
    c: Distance(g14) = 2
    c: Coincident(g16,g14)
    c: Horizontal(g16)
    c: Coincident(g15,g16)
FEATURE [Part::Feature] Face050
  shape: bbox 4.8 x 25.5 x 2e-07 mm, 1 faces, 0 solids (baked)
FEATURE [Part::Revolution] Revolve054  label="moreFrontCaseScrewPost001"
  Angle = 360
  Axis = (0,1,0)
  Base = (0,0,0)
  FaceMakerClass = Part::FaceMakerBullseye
  Placement = pos=(102.5,4.5,3.5) rot=(0,0,1;0rad)
  Solid = false
  Source = -> Face050
  Symmetric = false
FEATURE [Part::Feature] Face051
  shape: bbox 4.8 x 25.5 x 2e-07 mm, 1 faces, 0 solids (baked)
FEATURE [Part::Revolution] Revolve055  label="moreFrontCaseScrewPost002"
  Angle = 360
  Axis = (0,1,0)
  Base = (0,0,0)
  FaceMakerClass = Part::FaceMakerBullseye
  Placement = pos=(102.5,4.5,68.5) rot=(0,0,1;0rad)
  Solid = false
  Source = -> Face051
  Symmetric = false
FEATURE [Sketcher::SketchObject] Sketch027
  FullyConstrained = true
  sketch-geometry (10):
    g0: LineSegment StartX=-1.6 StartY=4.7 StartZ=0 EndX=-1.6 EndY=1.7 EndZ=0
    g1: LineSegment StartX=-3.5 StartY=4.7 StartZ=0 EndX=-1.6 EndY=4.7 EndZ=0
    g2: LineSegment StartX=-1.6 StartY=1.7 StartZ=0 EndX=-1.6 EndY=1.5 EndZ=0
    g3: LineSegment StartX=-1.6 StartY=1.5 StartZ=0 EndX=-5.2 EndY=1.5 EndZ=0
    g4: Circle CenterX=-3.5 CenterY=4.7 CenterZ=0 NormalX=0 NormalY=0 NormalZ=1 AngleXU=0 Radius=1
    g5: Circle CenterX=-3.59627 CenterY=2.99743 CenterZ=0 NormalX=0 NormalY=0 NormalZ=1 AngleXU=0 Radius=1
    g6: Circle CenterX=-5.2 CenterY=1.5 CenterZ=0 NormalX=0 NormalY=0 NormalZ=1 AngleXU=0 Radius=1
    g7: BSplineCurve PolesCount=3 KnotsCount=2 Degree=2 IsPeriodic=0
    g8: GeomPoint X=-3.5 Y=4.7 Z=0
    g9: GeomPoint X=-5.2 Y=1.5 Z=0
  constraints (23):
    c: Vertical(g0)
    c: Distance(g0) = 3
    c: Coincident(g1,g0)
    c: Horizontal(g1)
    c: Block(g0)
    c: Block(g1)
    c: Coincident(g2,g0)
    c: Vertical(g2)
    c: Distance(g2) = 0.2
    c: Coincident(g3,g2)
    c: Horizontal(g3)
    c: Block(g3)
    c: Coincident(g7,g1)
    c: Weight(g4) = 1
    c: Equal(g4,g5)
    c: Equal(g4,g6)
    c: Coincident(g7,g3)
    c: InternalAlignment(g4,g7)
    c: InternalAlignment(g5,g7)
    c: InternalAlignment(g6,g7)
    c: InternalAlignment(g8,g7)
    c: InternalAlignment(g9,g7)
    c: Block(g7)
FEATURE [Sketcher::SketchObject] Sketch028
  FullyConstrained = true
  sketch-geometry (18):
    g0: LineSegment StartX=0 StartY=3e-16 StartZ=0 EndX=0 EndY=1.7 EndZ=0
    g1: LineSegment StartX=-3.5 StartY=0 StartZ=0 EndX=-3.5 EndY=0.9 EndZ=0
    g2: Circle CenterX=-2.7 CenterY=1.7 CenterZ=0 NormalX=0 NormalY=0 NormalZ=1 AngleXU=0 Radius=1
    g3: Circle CenterX=-3.5 CenterY=1.7 CenterZ=0 NormalX=0 NormalY=0 NormalZ=1 AngleXU=0 Radius=1
    g4: Circle CenterX=-3.5 CenterY=0.9 CenterZ=0 NormalX=0 NormalY=0 NormalZ=1 AngleXU=0 Radius=1
    g5: BSplineCurve PolesCount=3 KnotsCount=2 Degree=2 IsPeriodic=0
    g6: GeomPoint X=-2.7 Y=1.7 Z=0
    g7: GeomPoint X=-3.5 Y=0.9 Z=0
    g8: LineSegment StartX=-3.5 StartY=0 StartZ=0 EndX=-3.5 EndY=-7 EndZ=0
    g9: LineSegment StartX=0 StartY=3e-16 StartZ=0 EndX=0 EndY=-7 EndZ=0
    g10: LineSegment StartX=-3.5 StartY=-7 StartZ=0 EndX=0 EndY=-7 EndZ=0
    g11: LineSegment StartX=-2.7 StartY=1.7 StartZ=0 EndX=-1.6 EndY=1.7 EndZ=0
    g12: LineSegment StartX=0 StartY=1.7 StartZ=0 EndX=0 EndY=4.5 EndZ=0
    g13: LineSegment StartX=0 StartY=4.5 StartZ=0 EndX=0 EndY=10.8 EndZ=0
    g14: LineSegment StartX=0 StartY=10.8 StartZ=0 EndX=-2 EndY=10.8 EndZ=0
    g15: LineSegment StartX=-1.6 StartY=4.7 StartZ=0 EndX=-1.6 EndY=1.7 EndZ=0
    g16: LineSegment StartX=-1.6 StartY=4.7 StartZ=0 EndX=-2 EndY=4.7 EndZ=0
    g17: LineSegment StartX=-2 StartY=4.7 StartZ=0 EndX=-2 EndY=10.8 EndZ=0
  constraints (44):
    c: Vertical(g0)
    c: Vertical(g1)
    c: Distance(g1) = 0.9
    c: Block(g0)
    c: Distance(g0) = 1.7
    c: Weight(g2) = 1
    c: Equal(g2,g3)
    c: Equal(g2,g4)
    c: Coincident(g5,g1)
    c: InternalAlignment(g2,g5)
    c: InternalAlignment(g3,g5)
    c: InternalAlignment(g4,g5)
    c: InternalAlignment(g6,g5)
    c: InternalAlignment(g7,g5)
    c: Block(g5)
    c: Coincident(g8,g1)
    c: Vertical(g8)
    c: Distance(g8) = 7
    c: Vertical(g9)
    c: Equal(g8,g9) = 7
    c: Coincident(g9,g0)
    c: Coincident(g10,g8)
    c: Coincident(g10,g9)
    c: Horizontal(g10)
    c: Coincident(g11,g5)
    c: Horizontal(g11)
    c: Coincident(g12,g0)
    c: Vertical(g12)
    c: Distance(g12) = 2.8
    c: Coincident(g13,g12)
    c: Vertical(g13)
    c: Distance(g13) = 6.3
    c: Coincident(g14,g13)
    c: Horizontal(g14)
    c: Distance(g14) = 2
    c: Vertical(g15)
    c: Distance(g15) = 3
    c: Block(g11)
    c: Coincident(g15,g11)
    c: Coincident(g16,g15)
    c: Horizontal(g16)
    c: Coincident(g17,g16)
    c: Coincident(g17,g14)
    c: Vertical(g17)
FEATURE [Part::Revolution] Revolve040  label="backCaseScrewRetainer001"
  Angle = 360
  Axis = (0,1,0)
  Base = (0,0,0)
  FaceMakerClass = Part::FaceMakerBullseye
  Placement = pos=(12.5,3,10) rot=(0,0,1;0rad)
  Solid = false
  Source = -> Face036
  Symmetric = false
FEATURE [Part::Feature] Face055
  shape: bbox 3.5 x 30.2 x 2e-07 mm, 1 faces, 0 solids (baked)
FEATURE [Part::Revolution] Revolve059  label="backCaseScrewPost"
  Angle = 360
  Axis = (0,1,0)
  Base = (0,0,0)
  FaceMakerClass = Part::FaceMakerBullseye
  Placement = pos=(12.5,4.5,10) rot=(0,0,1;0rad)
  Solid = false
  Source = -> Face055
  Symmetric = false
FEATURE [Part::Feature] Face056
  shape: bbox 3.5 x 30.2 x 2e-07 mm, 1 faces, 0 solids (baked)
FEATURE [Part::Revolution] Revolve060  label="backCaseScrewPost001"
  Angle = 360
  Axis = (0,1,0)
  Base = (0,0,0)
  FaceMakerClass = Part::FaceMakerBullseye
  Placement = pos=(12.5,4.5,62) rot=(0,0,1;0rad)
  Solid = false
  Source = -> Face056
  Symmetric = false
FEATURE [Part::Feature] Face057
  shape: bbox 3.5 x 17.8 x 2e-07 mm, 1 faces, 0 solids (baked)
FEATURE [Part::Revolution] Revolve061  label="removeToCreateScrewAndThreadedInsertHole"
  Angle = 360
  Axis = (0,1,0)
  Base = (0,0,0)
  FaceMakerClass = Part::FaceMakerBullseye
  Placement = pos=(12.5,0,10) rot=(0,0,1;0rad)
  Solid = false
  Source = -> Face057
  Symmetric = false
FEATURE [Part::Feature] Face058
  shape: bbox 3.5 x 17.8 x 2e-07 mm, 1 faces, 0 solids (baked)
FEATURE [Part::Revolution] Revolve062  label="removeToCreateScrewAndThreadedInsertHole001"
  Angle = 360
  Axis = (0,1,0)
  Base = (0,0,0)
  FaceMakerClass = Part::FaceMakerBullseye
  Placement = pos=(12.5,0,62) rot=(0,0,1;0rad)
  Solid = false
  Source = -> Face058
  Symmetric = false
FEATURE [Part::Feature] Face059
  shape: bbox 3.5 x 17.8 x 2e-07 mm, 1 faces, 0 solids (baked)
FEATURE [Part::Revolution] Revolve063  label="removeToCreateScrewAndThreadedInsertHole002"
  Angle = 360
  Axis = (0,1,0)
  Base = (0,0,0)
  FaceMakerClass = Part::FaceMakerBullseye
  Placement = pos=(89.5,0,68.5) rot=(0,0,1;0rad)
  Solid = false
  Source = -> Face059
  Symmetric = false
FEATURE [Part::Feature] Face060
  shape: bbox 3.5 x 17.8 x 2e-07 mm, 1 faces, 0 solids (baked)
FEATURE [Part::Revolution] Revolve064  label="removeToCreateScrewAndThreadedInsertHole003"
  Angle = 360
  Axis = (0,1,0)
  Base = (0,0,0)
  FaceMakerClass = Part::FaceMakerBullseye
  Placement = pos=(89.5,0,3.5) rot=(0,0,1;0rad)
  Solid = false
  Source = -> Face060
  Symmetric = false
FEATURE [Part::Feature] Face061
  shape: bbox 3.5 x 17.8 x 2e-07 mm, 1 faces, 0 solids (baked)
FEATURE [Part::Revolution] Revolve065  label="removeToCreateScrewAndThreadedInsertHole004"
  Angle = 360
  Axis = (0,1,0)
  Base = (0,0,0)
  FaceMakerClass = Part::FaceMakerBullseye
  Placement = pos=(102.5,4.7,3.5) rot=(0,0,1;0rad)
  Solid = false
  Source = -> Face061
  Symmetric = false
FEATURE [Part::Feature] Face062
  shape: bbox 3.5 x 17.8 x 2e-07 mm, 1 faces, 0 solids (baked)
FEATURE [Part::Revolution] Revolve066  label="removeToCreateScrewAndThreadedInsertHole005"
  Angle = 360
  Axis = (0,1,0)
  Base = (0,0,0)
  FaceMakerClass = Part::FaceMakerBullseye
  Placement = pos=(102.5,4.7,68.5) rot=(0,0,1;0rad)
  Solid = false
  Source = -> Face062
  Symmetric = false
FEATURE [Part::MultiFuse] Fusion047  label="makeHoles"
  Shapes = -> [Revolve066,Revolve065,Revolve064,Revolve063,Revolve062,Revolve061]
FEATURE [Part::Feature] Face063
  shape: bbox 3.6 x 3.2 x 2e-07 mm, 1 faces, 0 solids (baked)
FEATURE [Part::Revolution] Revolve067  label="moreFrontCaseScrewRetainer002"
  Angle = 360
  Axis = (0,1,0)
  Base = (0,0,0)
  FaceMakerClass = Part::FaceMakerBullseye
  Placement = pos=(102.5,4.5,68.5) rot=(0,0,1;0rad)
  Solid = false
  Source = -> Face063
  Symmetric = false
FEATURE [Part::Feature] Face064
  shape: bbox 3.6 x 3.2 x 2e-07 mm, 1 faces, 0 solids (baked)
FEATURE [Part::Revolution] Revolve068  label="moreFrontCaseScrewRetainer003"
  Angle = 360
  Axis = (0,1,0)
  Base = (0,0,0)
  FaceMakerClass = Part::FaceMakerBullseye
  Placement = pos=(102.5,4.5,3.5) rot=(0,0,1;0rad)
  Solid = false
  Source = -> Face064
  Symmetric = false
FEATURE [Part::Feature] Face065
  shape: bbox 3.5 x 17.8 x 2e-07 mm, 1 faces, 0 solids (baked)
FEATURE [Part::Revolution] Revolve069  label="removeToCreateScrewAndThreadedInsertHole006"
  Angle = 360
  Axis = (0,1,0)
  Base = (0,0,0)
  FaceMakerClass = Part::FaceMakerBullseye
  Placement = pos=(12.5,0,10) rot=(0,0,1;0rad)
  Solid = false
  Source = -> Face065
  Symmetric = false
FEATURE [Part::Feature] Face066
  shape: bbox 3.5 x 17.8 x 2e-07 mm, 1 faces, 0 solids (baked)
FEATURE [Part::Revolution] Revolve070  label="removeToCreateScrewAndThreadedInsertHole007"
  Angle = 360
  Axis = (0,1,0)
  Base = (0,0,0)
  FaceMakerClass = Part::FaceMakerBullseye
  Placement = pos=(12.5,0,62) rot=(0,0,1;0rad)
  Solid = false
  Source = -> Face066
  Symmetric = false
FEATURE [Part::Feature] Face067
  shape: bbox 3.5 x 17.8 x 2e-07 mm, 1 faces, 0 solids (baked)
FEATURE [Part::Revolution] Revolve071  label="removeToCreateScrewAndThreadedInsertHole008"
  Angle = 360
  Axis = (0,1,0)
  Base = (0,0,0)
  FaceMakerClass = Part::FaceMakerBullseye
  Placement = pos=(89.5,0,68.5) rot=(0,0,1;0rad)
  Solid = false
  Source = -> Face067
  Symmetric = false
FEATURE [Part::Feature] Face068
  shape: bbox 3.5 x 17.8 x 2e-07 mm, 1 faces, 0 solids (baked)
FEATURE [Part::Revolution] Revolve072  label="removeToCreateScrewAndThreadedInsertHole009"
  Angle = 360
  Axis = (0,1,0)
  Base = (0,0,0)
  FaceMakerClass = Part::FaceMakerBullseye
  Placement = pos=(89.5,0,3.5) rot=(0,0,1;0rad)
  Solid = false
  Source = -> Face068
  Symmetric = false
FEATURE [Part::Feature] Face069
  shape: bbox 3.5 x 17.8 x 2e-07 mm, 1 faces, 0 solids (baked)
FEATURE [Part::Feature] Face070
  shape: bbox 3.5 x 17.8 x 2e-07 mm, 1 faces, 0 solids (baked)
FEATURE [Part::Revolution] Revolve073  label="removeToCreateScrewAndThreadedInsertHole010"
  Angle = 360
  Axis = (0,1,0)
  Base = (0,0,0)
  FaceMakerClass = Part::FaceMakerBullseye
  Placement = pos=(102.5,4.7,3.5) rot=(0,0,1;0rad)
  Solid = false
  Source = -> Face069
  Symmetric = false
FEATURE [Part::Revolution] Revolve074  label="removeToCreateScrewAndThreadedInsertHole011"
  Angle = 360
  Axis = (0,1,0)
  Base = (0,0,0)
  FaceMakerClass = Part::FaceMakerBullseye
  Placement = pos=(102.5,4.7,68.5) rot=(0,0,1;0rad)
  Solid = false
  Source = -> Face070
  Symmetric = false
FEATURE [Part::MultiFuse] Fusion048  label="makeHoles001"
  Shapes = -> [Revolve074,Revolve073,Revolve072,Revolve071,Revolve070,Revolve069]
FEATURE [Part::MultiFuse] Fusion049  label="caseScrewRetainers"
  Shapes = -> [Revolve067,Revolve068,Revolve048,Revolve047,Revolve039,Revolve040]
FEATURE [Part::Cut] Cut015  label="caseScrewRetainers001"
  Base = -> Fusion049
  Tool = -> Fusion048
FEATURE [Part::MultiFuse] Fusion050  label="casePillars"
  Shapes = -> [Revolve055,Revolve054,Revolve043,Revolve046,Revolve059,Revolve060]
FEATURE [Part::Feature] Face071 .. Face076  x6 (patterned run collapsed; names and placements below)
  shape: bbox 3.5 x 17.8 x 2e-07 mm, 1 faces, 0 solids (baked)
FEATURE [Part::Revolution] Revolve075  label="removeToCreateScrewAndThreadedInsertHole012"
  Angle = 360
  Axis = (0,1,0)
  Base = (0,0,0)
  FaceMakerClass = Part::FaceMakerBullseye
  Placement = pos=(12.5,0,10) rot=(0,0,1;0rad)
  Solid = false
  Source = -> Face071
  Symmetric = false
FEATURE [Part::Revolution] Revolve076  label="removeToCreateScrewAndThreadedInsertHole013"
  Angle = 360
  Axis = (0,1,0)
  Base = (0,0,0)
  FaceMakerClass = Part::FaceMakerBullseye
  Placement = pos=(12.5,0,62) rot=(0,0,1;0rad)
  Solid = false
  Source = -> Face072
  Symmetric = false
FEATURE [Part::Revolution] Revolve077  label="removeToCreateScrewAndThreadedInsertHole014"
  Angle = 360
  Axis = (0,1,0)
  Base = (0,0,0)
  FaceMakerClass = Part::FaceMakerBullseye
  Placement = pos=(89.5,0,68.5) rot=(0,0,1;0rad)
  Solid = false
  Source = -> Face073
  Symmetric = false
FEATURE [Part::Revolution] Revolve078  label="removeToCreateScrewAndThreadedInsertHole015"
  Angle = 360
  Axis = (0,1,0)
  Base = (0,0,0)
  FaceMakerClass = Part::FaceMakerBullseye
  Placement = pos=(89.5,0,3.5) rot=(0,0,1;0rad)
  Solid = false
  Source = -> Face074
  Symmetric = false
FEATURE [Part::Revolution] Revolve079  label="removeToCreateScrewAndThreadedInsertHole016"
  Angle = 360
  Axis = (0,1,0)
  Base = (0,0,0)
  FaceMakerClass = Part::FaceMakerBullseye
  Placement = pos=(102.5,4.7,3.5) rot=(0,0,1;0rad)
  Solid = false
  Source = -> Face075
  Symmetric = false
FEATURE [Part::Revolution] Revolve080  label="removeToCreateScrewAndThreadedInsertHole017"
  Angle = 360
  Axis = (0,1,0)
  Base = (0,0,0)
  FaceMakerClass = Part::FaceMakerBullseye
  Placement = pos=(102.5,4.7,68.5) rot=(0,0,1;0rad)
  Solid = false
  Source = -> Face076
  Symmetric = false
FEATURE [Part::MultiFuse] Fusion051  label="makeHoles002"
  Shapes = -> [Revolve080,Revolve079,Revolve078,Revolve077,Revolve076,Revolve075]
FEATURE [Part::Cut] Cut016  label="caesPillars"
  Base = -> Fusion050
  Tool = -> Fusion051
FEATURE [Part::Revolution] Revolve009  label="plugHousing016"
  Angle = 360
  Axis = (0,1,0)
  Base = (0,0,0)
  FaceMakerClass = Part::FaceMakerBullseye
  Placement = pos=(0,0,36.15) rot=(0,0,1;0rad)
  Solid = false
  Source = -> Face012
  Symmetric = false
FEATURE [Part::MultiFuse] Fusion014  label="plugHousing023"
  Placement = pos=(0,0,0) rot=(0,0,1;1.5708rad)
  Shapes = -> [Revolve011,Revolve009]
FEATURE [Part::Revolution] Revolve010  label="plugHousing017"
  Angle = 360
  Axis = (0,1,0)
  Base = (0,0,0)
  FaceMakerClass = Part::FaceMakerBullseye
  Placement = pos=(0,0,36.15) rot=(0,0,1;0rad)
  Solid = false
  Source = -> Face014
  Symmetric = false
FEATURE [Part::MultiFuse] Fusion015  label="plugHousing024"
  Placement = pos=(0,0,0) rot=(0,0,1;1.5708rad)
  Shapes = -> [Revolve010,Revolve015]
FEATURE [Part::Revolution] Revolve014  label="plugHousing026"
  Angle = 360
  Axis = (0,1,0)
  Base = (0,0,0)
  FaceMakerClass = Part::FaceMakerBullseye
  Placement = pos=(0,0,36.15) rot=(0,0,1;0rad)
  Solid = false
  Source = -> Face011
  Symmetric = false
FEATURE [Part::Revolution] Revolve013  label="plugHousing025"
  Angle = 360
  Axis = (0,1,0)
  Base = (0,0,0)
  FaceMakerClass = Part::FaceMakerBullseye
  Placement = pos=(0,0,36.15) rot=(0,0,1;0rad)
  Solid = false
  Source = -> Face015
  Symmetric = false
FEATURE [Part::MultiFuse] Fusion016  label="plugHousing028"
  Placement = pos=(0,19,0) rot=(0,0,1;3.14159rad)
  Shapes = -> [Fusion014,Fusion013]
FEATURE [Part::MultiFuse] Fusion011  label="plugHousing018"
  Placement = pos=(0,0,0) rot=(0,0,1;1.5708rad)
  Shapes = -> [Revolve014,Revolve013]
FEATURE [Part::MultiFuse] Fusion012  label="plugHousing019"
  Placement = pos=(0,19,0) rot=(0,0,1;3.14159rad)
  Shapes = -> [Fusion011,Fusion015]
FEATURE [Part::MultiFuse] Fusion017  label="plugHousing029"
  Placement = pos=(122.621,0,-0.15) rot=(0,0,1;0rad)
  Shapes = -> [Fusion016,Fusion012]
FEATURE [Part::MultiFuse] Fusion052  label="casePillarRetainers"
  Shapes = -> [Extrude012,Extrude013,Extrude014,Extrude015,Extrude016,Extrude017,Extrude018,Extrude019,Box011,Box012]
FEATURE [Part::Feature] Face077
  shape: bbox 3.5 x 17.8 x 2e-07 mm, 1 faces, 0 solids (baked)
FEATURE [Part::Revolution] Revolve081  label="removeToCreateScrewAndThreadedInsertHole018"
  Angle = 360
  Axis = (0,1,0)
  Base = (0,0,0)
  FaceMakerClass = Part::FaceMakerBullseye
  Placement = pos=(62.3,30.3,19.7) rot=(0,0,1;0rad)
  Solid = false
  Source = -> Face077
  Symmetric = false
FEATURE [Part::Feature] Face078
  shape: bbox 3.5 x 17.8 x 2e-07 mm, 1 faces, 0 solids (baked)
FEATURE [Part::Revolution] Revolve082  label="removeToCreateScrewAndThreadedInsertHole019"
  Angle = 360
  Axis = (0,1,0)
  Base = (0,0,0)
  FaceMakerClass = Part::FaceMakerBullseye
  Placement = pos=(62.3,30.3,51.7) rot=(0,0,1;0rad)
  Solid = false
  Source = -> Face078
  Symmetric = false
FEATURE [Part::Feature] Face079
  shape: bbox 3.5 x 17.8 x 2e-07 mm, 1 faces, 0 solids (baked)
FEATURE [Part::Revolution] Revolve083  label="removeToCreateScrewAndThreadedInsertHole020"
  Angle = 360
  Axis = (0,1,0)
  Base = (0,0,0)
  FaceMakerClass = Part::FaceMakerBullseye
  Placement = pos=(30.3,30.3,19.7) rot=(0,0,1;0rad)
  Solid = false
  Source = -> Face079
  Symmetric = false
FEATURE [Part::Feature] Face080
  shape: bbox 3.5 x 17.8 x 2e-07 mm, 1 faces, 0 solids (baked)
FEATURE [Part::Revolution] Revolve084  label="removeToCreateScrewAndThreadedInsertHole021"
  Angle = 360
  Axis = (0,1,0)
  Base = (0,0,0)
  FaceMakerClass = Part::FaceMakerBullseye
  Placement = pos=(30.3,30.3,51.7) rot=(0,0,1;0rad)
  Solid = false
  Source = -> Face080
  Symmetric = false
FEATURE [Part::MultiFuse] Fusion053  label="createThreadedInsertHolesForFan"
  Shapes = -> [Revolve081,Revolve082,Revolve083,Revolve084]
FEATURE [Part::Cut] Cut017  label="fanScrewHousing001"
  Base = -> Fusion046
  Tool = -> Fusion053
FEATURE [Part::Feature] Face081
  shape: bbox 3.5 x 17.8 x 2e-07 mm, 1 faces, 0 solids (baked)
FEATURE [Part::Revolution] Revolve085  label="removeToCreateScrewAndThreadedInsertHole022"
  Angle = 360
  Axis = (0,1,0)
  Base = (0,0,0)
  FaceMakerClass = Part::FaceMakerBullseye
  Placement = pos=(62.3,30.3,19.7) rot=(0,0,1;0rad)
  Solid = false
  Source = -> Face081
  Symmetric = false
FEATURE [Part::Feature] Face082
  shape: bbox 3.5 x 17.8 x 2e-07 mm, 1 faces, 0 solids (baked)
FEATURE [Part::Revolution] Revolve086  label="removeToCreateScrewAndThreadedInsertHole023"
  Angle = 360
  Axis = (0,1,0)
  Base = (0,0,0)
  FaceMakerClass = Part::FaceMakerBullseye
  Placement = pos=(62.3,30.3,51.7) rot=(0,0,1;0rad)
  Solid = false
  Source = -> Face082
  Symmetric = false
FEATURE [Part::Feature] Face083
  shape: bbox 3.5 x 17.8 x 2e-07 mm, 1 faces, 0 solids (baked)
FEATURE [Part::Revolution] Revolve087  label="removeToCreateScrewAndThreadedInsertHole024"
  Angle = 360
  Axis = (0,1,0)
  Base = (0,0,0)
  FaceMakerClass = Part::FaceMakerBullseye
  Placement = pos=(30.3,30.3,19.7) rot=(0,0,1;0rad)
  Solid = false
  Source = -> Face083
  Symmetric = false
FEATURE [Part::Feature] Face084
  shape: bbox 3.5 x 17.8 x 2e-07 mm, 1 faces, 0 solids (baked)
FEATURE [Part::Revolution] Revolve088  label="removeToCreateScrewAndThreadedInsertHole025"
  Angle = 360
  Axis = (0,1,0)
  Base = (0,0,0)
  FaceMakerClass = Part::FaceMakerBullseye
  Placement = pos=(30.3,30.3,51.7) rot=(0,0,1;0rad)
  Solid = false
  Source = -> Face084
  Symmetric = false
FEATURE [Part::MultiFuse] Fusion054  label="createThreadedInsertHolesForFan001"
  Shapes = -> [Revolve085,Revolve086,Revolve087,Revolve088]
FEATURE [Part::Cut] Cut018  label="top007"
  Base = -> Fusion040
  Tool = -> Fusion054
FEATURE [Sketcher::SketchObject] Sketch029
  FullyConstrained = false
  Placement = pos=(0,0,0) rot=(1,0,0;1.5708rad)
  sketch-geometry (24):
    g0: ArcOfCircle CenterX=-4 CenterY=-10.5 CenterZ=0 NormalX=0 NormalY=0 NormalZ=1 AngleXU=0 Radius=1.5 StartAngle=6e-16 EndAngle=3.14159
    g1: ArcOfCircle CenterX=-34.2 CenterY=-10.5 CenterZ=0 NormalX=0 NormalY=0 NormalZ=1 AngleXU=0 Radius=1.5 StartAngle=0 EndAngle=3.14159
    g2: ArcOfCircle CenterX=-34.2 CenterY=-27.7 CenterZ=0 NormalX=0 NormalY=0 NormalZ=1 AngleXU=0 Radius=1.5 StartAngle=3.14159 EndAngle=6.28319
    g3: ArcOfCircle CenterX=-4 CenterY=-27.7 CenterZ=0 NormalX=0 NormalY=0 NormalZ=1 AngleXU=0 Radius=1.5 StartAngle=3.1416 EndAngle=6.28319
    g4: ArcOfCircle CenterX=-10 CenterY=-4.3 CenterZ=0 NormalX=0 NormalY=0 NormalZ=1 AngleXU=0 Radius=1.5 StartAngle=2e-16 EndAngle=3.14159
    g5: ArcOfCircle CenterX=-16.1 CenterY=-1.8 CenterZ=0 NormalX=0 NormalY=0 NormalZ=1 AngleXU=0 Radius=1.5 StartAngle=5e-16 EndAngle=3.14159
    g6: ArcOfCircle CenterX=-22.1 CenterY=-1.8 CenterZ=0 NormalX=0 NormalY=0 NormalZ=1 AngleXU=0 Radius=1.5 StartAngle=5e-16 EndAngle=3.14159
    g7: ArcOfCircle CenterX=-28.2 CenterY=-4.3 CenterZ=0 NormalX=0 NormalY=0 NormalZ=1 AngleXU=0 Radius=1.5 StartAngle=2e-16 EndAngle=3.14159
    g8: ArcOfCircle CenterX=-10 CenterY=-33.9 CenterZ=0 NormalX=0 NormalY=0 NormalZ=1 AngleXU=0 Radius=1.5 StartAngle=3.14159 EndAngle=6.28319
    g9: ArcOfCircle CenterX=-16.1 CenterY=-36.4 CenterZ=0 NormalX=0 NormalY=0 NormalZ=1 AngleXU=0 Radius=1.5 StartAngle=3.14159 EndAngle=6.28319
    g10: ArcOfCircle CenterX=-22.1 CenterY=-36.4 CenterZ=0 NormalX=0 NormalY=0 NormalZ=1 AngleXU=0 Radius=1.5 StartAngle=3.14159 EndAngle=6.28319
    g11: ArcOfCircle CenterX=-28.2 CenterY=-33.9 CenterZ=0 NormalX=0 NormalY=0 NormalZ=1 AngleXU=0 Radius=1.5 StartAngle=3.14159 EndAngle=6.28319
    g12: LineSegment StartX=-35.7 StartY=-10.5 StartZ=0 EndX=-35.7 EndY=-27.7 EndZ=0
    g13: LineSegment StartX=-32.7 StartY=-10.5 StartZ=0 EndX=-32.7 EndY=-27.7 EndZ=0
    g14: LineSegment StartX=-29.7 StartY=-33.9 StartZ=0 EndX=-29.7 EndY=-4.3 EndZ=0
    g15: LineSegment StartX=-26.7 StartY=-33.9 StartZ=0 EndX=-26.7 EndY=-4.3 EndZ=0
    g16: LineSegment StartX=-2.5 StartY=-10.5 StartZ=0 EndX=-2.5 EndY=-27.7 EndZ=0
    g17: LineSegment StartX=-8.5 StartY=-4.3 StartZ=0 EndX=-8.5 EndY=-33.9 EndZ=0
    g18: LineSegment StartX=-5.5 StartY=-10.5 StartZ=0 EndX=-5.5 EndY=-27.7 EndZ=0
    g19: LineSegment StartX=-11.5 StartY=-4.3 StartZ=0 EndX=-11.5 EndY=-33.9 EndZ=0
    g20: LineSegment StartX=-14.6 StartY=-1.8 StartZ=0 EndX=-14.6 EndY=-36.4 EndZ=0
    g21: LineSegment StartX=-17.6 StartY=-1.8 StartZ=0 EndX=-17.6 EndY=-36.4 EndZ=0
    g22: LineSegment StartX=-20.6 StartY=-36.4 StartZ=0 EndX=-20.6 EndY=-1.8 EndZ=0
    g23: LineSegment StartX=-23.6 StartY=-1.8 StartZ=0 EndX=-23.6 EndY=-36.4 EndZ=0
  constraints (48):
    c: Block(g0)
    c: Block(g1)
    c: Block(g2)
    c: Block(g3)
    c: Block(g4)
    c: Block(g5)
    c: Block(g6)
    c: Block(g7)
    c: Block(g8)
    c: Block(g9)
    c: Block(g10)
    c: Block(g11)
    c: Coincident(g12,g1)
    c: Coincident(g12,g2)
    c: Vertical(g12)
    c: Coincident(g13,g1)
    c: Coincident(g13,g2)
    c: Vertical(g13)
    c: Coincident(g14,g11)
    c: Coincident(g14,g7)
    c: Vertical(g14)
    c: Coincident(g15,g11)
    c: Coincident(g15,g7)
    c: Vertical(g15)
    c: Coincident(g16,g0)
    c: Coincident(g16,g3)
    c: Vertical(g16)
    c: Coincident(g17,g4)
    c: Coincident(g17,g8)
    c: Vertical(g17)
    c: Coincident(g18,g0)
    c: Coincident(g18,g3)
    c: Vertical(g18)
    c: Coincident(g19,g4)
    c: Coincident(g19,g8)
    c: Vertical(g19)
    c: Coincident(g20,g5)
    c: Coincident(g20,g9)
    c: Vertical(g20)
    c: Coincident(g21,g5)
    c: Coincident(g21,g9)
    c: Vertical(g21)
    c: Coincident(g22,g10)
    c: Coincident(g22,g6)
    c: Vertical(g22)
    c: Coincident(g23,g6)
    c: Coincident(g23,g10)
    c: Vertical(g23)
FEATURE [Part::Extrusion] Extrude020  label="removeToCreateFanGrillHoles"
  Base = -> Sketch029
  Dir = (0,-1,6e-16)
  DirMode = 2
  FaceMakerClass = Part::FaceMakerBullseye
  LengthFwd = 10
  LengthRev = 0
  Placement = pos=(65.4,44,54.82) rot=(0,0,1;0rad)
  Solid = true
  Symmetric = false
FEATURE [Part::MultiFuse] Fusion055  label="top008"
  Shapes = -> [Cut017,Cut018]
FEATURE [Part::Cut] Cut019  label="top009"
  Base = -> Fusion055
  Tool = -> Extrude020
FEATURE [App::MeasureDistance] Distance003  label="Distance: 71.95 mm"
  Distance = 71.9513
  P1 = (117,38,72)
  P2 = (117,38,0.0487319)
FEATURE [Sketcher::SketchObject] Sketch030
  FullyConstrained = true
  Placement = pos=(117,19,0) rot=(0.57735,0.57735,0.57735;2.0944rad)
  sketch-geometry (48):
    g0: LineSegment StartX=-49.19 StartY=69.25 StartZ=0 EndX=-49.19 EndY=66.25 EndZ=0
    g1: LineSegment StartX=-49.19 StartY=63.5 StartZ=0 EndX=-49.19 EndY=60.5 EndZ=0
    g2: LineSegment StartX=-49.19 StartY=57.75 StartZ=0 EndX=-49.19 EndY=54.75 EndZ=0
    g3: LineSegment StartX=-49.19 StartY=52 StartZ=0 EndX=-49.19 EndY=49 EndZ=0
    g4: LineSegment StartX=-49.19 StartY=46.25 StartZ=0 EndX=-49.19 EndY=43.25 EndZ=0
    g5: LineSegment StartX=-49.19 StartY=40.5 StartZ=0 EndX=-49.19 EndY=37.5 EndZ=0
    g6: LineSegment StartX=-49.19 StartY=34.5 StartZ=0 EndX=-49.19 EndY=31.5 EndZ=0
    g7: LineSegment StartX=-49.19 StartY=28.75 StartZ=0 EndX=-49.19 EndY=25.75 EndZ=0
    g8: LineSegment StartX=-49.19 StartY=23 StartZ=0 EndX=-49.19 EndY=20 EndZ=0
    g9: LineSegment StartX=-49.19 StartY=17.25 StartZ=0 EndX=-49.19 EndY=14.25 EndZ=0
    g10: LineSegment StartX=-49.19 StartY=11.5 StartZ=0 EndX=-49.19 EndY=8.5 EndZ=0
    g11: LineSegment StartX=-49.19 StartY=5.75 StartZ=0 EndX=-49.19 EndY=2.75 EndZ=0
    g12: ArcOfCircle CenterX=-1.5 CenterY=67.75 CenterZ=0 NormalX=0 NormalY=0 NormalZ=1 AngleXU=0 Radius=1.5 StartAngle=4.71239 EndAngle=7.85398
    g13: ArcOfCircle CenterX=-1.5 CenterY=62 CenterZ=0 NormalX=0 NormalY=0 NormalZ=1 AngleXU=0 Radius=1.5 StartAngle=4.71239 EndAngle=7.85398
    g14: ArcOfCircle CenterX=-1.5 CenterY=56.25 CenterZ=0 NormalX=0 NormalY=0 NormalZ=1 AngleXU=0 Radius=1.5 StartAngle=4.71239 EndAngle=7.85398
    g15: ArcOfCircle CenterX=-11.49 CenterY=50.5 CenterZ=0 NormalX=0 NormalY=0 NormalZ=1 AngleXU=0 Radius=1.5 StartAngle=4.71239 EndAngle=7.85398
    g16: ArcOfCircle CenterX=-16.28 CenterY=44.75 CenterZ=0 NormalX=0 NormalY=0 NormalZ=1 AngleXU=0 Radius=1.5 StartAngle=4.71239 EndAngle=7.85398
    g17: ArcOfCircle CenterX=-18.2337 CenterY=39 CenterZ=0 NormalX=0 NormalY=0 NormalZ=1 AngleXU=0 Radius=1.5 StartAngle=4.71485 EndAngle=7.85398
    g18: ArcOfCircle CenterX=-16.2837 CenterY=27.25 CenterZ=0 NormalX=0 NormalY=0 NormalZ=1 AngleXU=0 Radius=1.5 StartAngle=4.71485 EndAngle=7.85398
    g19: ArcOfCircle CenterX=-18.2337 CenterY=33 CenterZ=0 NormalX=0 NormalY=0 NormalZ=1 AngleXU=0 Radius=1.5 StartAngle=4.71485 EndAngle=7.85398
    g20: ArcOfCircle CenterX=-11.49 CenterY=21.5 CenterZ=0 NormalX=0 NormalY=0 NormalZ=1 AngleXU=0 Radius=1.5 StartAngle=4.71239 EndAngle=7.85398
    g21: ArcOfCircle CenterX=-1.5 CenterY=4.25 CenterZ=0 NormalX=0 NormalY=0 NormalZ=1 AngleXU=0 Radius=1.5 StartAngle=4.71239 EndAngle=7.85398
    g22: ArcOfCircle CenterX=-1.5 CenterY=10 CenterZ=0 NormalX=0 NormalY=0 NormalZ=1 AngleXU=0 Radius=1.5 StartAngle=4.71239 EndAngle=7.85398
    g23: ArcOfCircle CenterX=-1.5 CenterY=15.75 CenterZ=0 NormalX=0 NormalY=0 NormalZ=1 AngleXU=0 Radius=1.5 StartAngle=4.71239 EndAngle=7.85398
    g24: LineSegment StartX=-49.19 StartY=69.25 StartZ=0 EndX=-1.5 EndY=69.25 EndZ=0
    g25: LineSegment StartX=-49.19 StartY=66.25 StartZ=0 EndX=-1.5 EndY=66.25 EndZ=0
    g26: LineSegment StartX=-49.19 StartY=63.5 StartZ=0 EndX=-1.5 EndY=63.5 EndZ=0
    g27: LineSegment StartX=-49.19 StartY=60.5 StartZ=0 EndX=-1.5 EndY=60.5 EndZ=0
    g28: LineSegment StartX=-49.19 StartY=57.75 StartZ=0 EndX=-1.5 EndY=57.75 EndZ=0
    g29: LineSegment StartX=-49.19 StartY=54.75 StartZ=0 EndX=-1.5 EndY=54.75 EndZ=0
    g30: LineSegment StartX=-49.19 StartY=52 StartZ=0 EndX=-11.49 EndY=52 EndZ=0
    g31: LineSegment StartX=-49.19 StartY=49 StartZ=0 EndX=-11.49 EndY=49 EndZ=0
    g32: LineSegment StartX=-49.19 StartY=46.25 StartZ=0 EndX=-16.28 EndY=46.25 EndZ=0
    g33: LineSegment StartX=-49.19 StartY=43.25 StartZ=0 EndX=-16.28 EndY=43.25 EndZ=0
    g34: LineSegment StartX=-49.19 StartY=40.5 StartZ=0 EndX=-18.2337 EndY=40.5 EndZ=0
    g35: LineSegment StartX=-49.19 StartY=37.5 StartZ=0 EndX=-18.23 EndY=37.5 EndZ=0
    g36: LineSegment StartX=-49.19 StartY=34.5 StartZ=0 EndX=-18.2337 EndY=34.5 EndZ=0
    g37: LineSegment StartX=-49.19 StartY=31.5 StartZ=0 EndX=-18.23 EndY=31.5 EndZ=0
    g38: LineSegment StartX=-49.19 StartY=28.75 StartZ=0 EndX=-16.2837 EndY=28.75 EndZ=0
    g39: LineSegment StartX=-49.19 StartY=25.75 StartZ=0 EndX=-16.28 EndY=25.75 EndZ=0
    g40: LineSegment StartX=-49.19 StartY=23 StartZ=0 EndX=-11.49 EndY=23 EndZ=0
    g41: LineSegment StartX=-49.19 StartY=20 StartZ=0 EndX=-11.49 EndY=20 EndZ=0
    g42: LineSegment StartX=-49.19 StartY=17.25 StartZ=0 EndX=-1.5 EndY=17.25 EndZ=0
    g43: LineSegment StartX=-49.19 StartY=14.25 StartZ=0 EndX=-1.5 EndY=14.25 EndZ=0
    g44: LineSegment StartX=-49.19 StartY=11.5 StartZ=0 EndX=-1.5 EndY=11.5 EndZ=0
    g45: LineSegment StartX=-49.19 StartY=8.5 StartZ=0 EndX=-1.5 EndY=8.5 EndZ=0
    g46: LineSegment StartX=-49.19 StartY=5.75 StartZ=0 EndX=-1.5 EndY=5.75 EndZ=0
    g47: LineSegment StartX=-49.19 StartY=2.75 StartZ=0 EndX=-1.5 EndY=2.75 EndZ=0
  constraints (120):
    c: Vertical(g0)
    c: Distance(g0) = 3
    c: Block(g0)
    c: Vertical(g1)
    c: Distance(g1) = 3
    c: Vertical(g2)
    c: Equal(g0,g2) = 3
    c: Block(g2)
    c: Vertical(g3)
    c: Equal(g1,g3) = 3
    c: Vertical(g4)
    c: Equal(g0,g4) = 3
    c: Block(g4)
    c: Vertical(g5)
    c: Equal(g1,g5) = 3
    c: Vertical(g6)
    c: Equal(g0,g6) = 3
    c: Block(g6)
    c: Vertical(g7)
    c: Equal(g1,g7) = 3
    c: Vertical(g8)
    c: Equal(g0,g8) = 3
    c: Block(g8)
    c: Vertical(g9)
    c: Equal(g1,g9) = 3
    c: Vertical(g10)
    c: Equal(g0,g10) = 3
    c: Block(g10)
    c: Vertical(g11)
    c: Equal(g1,g11) = 3
    c: Block(g12)
    c: Block(g13)
    c: Block(g14)
    c: Block(g15)
    c: Block(g16)
    c: Block(g17)
    c: Block(g18)
    c: Block(g19)
    c: Block(g20)
    c: Block(g21)
    c: Block(g22)
    c: Block(g23)
    c: Block(g11)
    c: Block(g9)
    c: Block(g7)
    c: Block(g5)
    c: Block(g3)
    c: Block(g1)
    c: Coincident(g24,g0)
    c: Coincident(g24,g12)
    c: Horizontal(g24)
    c: Coincident(g25,g0)
    c: Coincident(g25,g12)
    c: Horizontal(g25)
    c: Coincident(g26,g1)
    c: Coincident(g26,g13)
    c: Horizontal(g26)
    c: Coincident(g27,g1)
    c: Coincident(g27,g13)
    c: Horizontal(g27)
    c: Coincident(g28,g2)
    c: Coincident(g28,g14)
    c: Horizontal(g28)
    c: Coincident(g29,g2)
    c: Coincident(g29,g14)
    c: Horizontal(g29)
    c: Coincident(g30,g3)
    c: Coincident(g30,g15)
    c: Horizontal(g30)
    c: Coincident(g31,g3)
    c: Coincident(g31,g15)
    c: Horizontal(g31)
    c: Coincident(g32,g4)
    c: Coincident(g32,g16)
    c: Horizontal(g32)
    c: Coincident(g33,g4)
    c: Coincident(g33,g16)
    c: Horizontal(g33)
    c: Coincident(g34,g5)
    c: Coincident(g34,g17)
    c: Horizontal(g34)
    c: Coincident(g35,g5)
    c: Coincident(g35,g17)
    c: Horizontal(g35)
    c: Coincident(g36,g6)
    c: Coincident(g36,g19)
    c: Horizontal(g36)
    c: Coincident(g37,g6)
    c: Coincident(g37,g19)
    c: Horizontal(g37)
    c: Coincident(g38,g7)
    c: Coincident(g38,g18)
    c: Horizontal(g38)
    c: Coincident(g39,g7)
    c: Coincident(g39,g18)
    c: Horizontal(g39)
    c: Coincident(g40,g8)
    c: Coincident(g40,g20)
    c: Horizontal(g40)
    c: Coincident(g41,g8)
    c: Coincident(g41,g20)
    c: Horizontal(g41)
    c: Coincident(g42,g9)
    c: Coincident(g42,g23)
    c: Horizontal(g42)
    c: Coincident(g43,g9)
    c: Coincident(g43,g23)
    c: Horizontal(g43)
    c: Coincident(g44,g10)
    c: Coincident(g44,g22)
    c: Horizontal(g44)
    c: Coincident(g45,g10)
    c: Coincident(g45,g22)
    c: Horizontal(g45)
    c: Coincident(g46,g11)
    c: Coincident(g46,g21)
    c: Horizontal(g46)
    c: Coincident(g47,g11)
    c: Coincident(g47,g21)
    c: Horizontal(g47)
FEATURE [Sketcher::SketchObject] Sketch031
  FullyConstrained = true
  Placement = pos=(117,19,0) rot=(0.57735,0.57735,0.57735;2.0944rad)
  sketch-geometry (24):
    g0: ArcOfCircle CenterX=-49.19 CenterY=67.75 CenterZ=0 NormalX=0 NormalY=0 NormalZ=1 AngleXU=0 Radius=1.5 StartAngle=1.5708 EndAngle=4.71239
    g1: ArcOfCircle CenterX=-49.19 CenterY=62 CenterZ=0 NormalX=0 NormalY=0 NormalZ=1 AngleXU=0 Radius=1.5 StartAngle=1.5708 EndAngle=4.71239
    g2: ArcOfCircle CenterX=-49.19 CenterY=56.25 CenterZ=0 NormalX=0 NormalY=0 NormalZ=1 AngleXU=0 Radius=1.5 StartAngle=1.5708 EndAngle=4.71239
    g3: ArcOfCircle CenterX=-49.19 CenterY=50.5 CenterZ=0 NormalX=0 NormalY=0 NormalZ=1 AngleXU=0 Radius=1.5 StartAngle=1.5708 EndAngle=4.71239
    g4: ArcOfCircle CenterX=-49.19 CenterY=44.75 CenterZ=0 NormalX=0 NormalY=0 NormalZ=1 AngleXU=0 Radius=1.5 StartAngle=1.5708 EndAngle=4.71239
    g5: ArcOfCircle CenterX=-49.19 CenterY=39 CenterZ=0 NormalX=0 NormalY=0 NormalZ=1 AngleXU=0 Radius=1.5 StartAngle=1.5708 EndAngle=4.71239
    g6: ArcOfCircle CenterX=-49.19 CenterY=33 CenterZ=0 NormalX=0 NormalY=0 NormalZ=1 AngleXU=0 Radius=1.5 StartAngle=1.5708 EndAngle=4.71239
    g7: ArcOfCircle CenterX=-49.19 CenterY=27.25 CenterZ=0 NormalX=0 NormalY=0 NormalZ=1 AngleXU=0 Radius=1.5 StartAngle=1.5708 EndAngle=4.71239
    g8: ArcOfCircle CenterX=-49.19 CenterY=21.5 CenterZ=0 NormalX=0 NormalY=0 NormalZ=1 AngleXU=0 Radius=1.5 StartAngle=1.5708 EndAngle=4.71239
    g9: ArcOfCircle CenterX=-49.19 CenterY=15.75 CenterZ=0 NormalX=0 NormalY=0 NormalZ=1 AngleXU=0 Radius=1.5 StartAngle=1.5708 EndAngle=4.71239
    g10: ArcOfCircle CenterX=-49.19 CenterY=10 CenterZ=0 NormalX=0 NormalY=0 NormalZ=1 AngleXU=0 Radius=1.5 StartAngle=1.5708 EndAngle=4.71239
    g11: ArcOfCircle CenterX=-49.19 CenterY=4.25 CenterZ=0 NormalX=0 NormalY=0 NormalZ=1 AngleXU=0 Radius=1.5 StartAngle=1.5708 EndAngle=4.71239
    g12: LineSegment StartX=-49.19 StartY=69.25 StartZ=0 EndX=-49.19 EndY=66.25 EndZ=0
    g13: LineSegment StartX=-49.19 StartY=63.5 StartZ=0 EndX=-49.19 EndY=60.5 EndZ=0
    g14: LineSegment StartX=-49.19 StartY=57.75 StartZ=0 EndX=-49.19 EndY=54.75 EndZ=0
    g15: LineSegment StartX=-49.19 StartY=52 StartZ=0 EndX=-49.19 EndY=49 EndZ=0
    g16: LineSegment StartX=-49.19 StartY=46.25 StartZ=0 EndX=-49.19 EndY=43.25 EndZ=0
    g17: LineSegment StartX=-49.19 StartY=40.5 StartZ=0 EndX=-49.19 EndY=37.5 EndZ=0
    g18: LineSegment StartX=-49.19 StartY=34.5 StartZ=0 EndX=-49.19 EndY=31.5 EndZ=0
    g19: LineSegment StartX=-49.19 StartY=28.75 StartZ=0 EndX=-49.19 EndY=25.75 EndZ=0
    g20: LineSegment StartX=-49.19 StartY=23 StartZ=0 EndX=-49.19 EndY=20 EndZ=0
    g21: LineSegment StartX=-49.19 StartY=17.25 StartZ=0 EndX=-49.19 EndY=14.25 EndZ=0
    g22: LineSegment StartX=-49.19 StartY=11.5 StartZ=0 EndX=-49.19 EndY=8.5 EndZ=0
    g23: LineSegment StartX=-49.19 StartY=5.75 StartZ=0 EndX=-49.19 EndY=2.75 EndZ=0
  constraints (48):
    c: Block(g0)
    c: Block(g1)
    c: Block(g2)
    c: Block(g3)
    c: Block(g4)
    c: Block(g5)
    c: Block(g6)
    c: Block(g7)
    c: Block(g8)
    c: Block(g9)
    c: Block(g10)
    c: Block(g11)
    c: Coincident(g12,g0)
    c: Coincident(g12,g0)
    c: Vertical(g12)
    c: Vertical(g13)
    c: Coincident(g13,g1)
    c: Vertical(g14)
    c: Coincident(g14,g2)
    c: Vertical(g15)
    c: Coincident(g15,g3)
    c: Vertical(g16)
    c: Coincident(g16,g4)
    c: Vertical(g17)
    c: Coincident(g17,g5)
    c: Vertical(g18)
    c: Coincident(g18,g6)
    c: Vertical(g19)
    c: Coincident(g19,g7)
    c: Vertical(g20)
    c: Coincident(g20,g8)
    c: Vertical(g21)
    c: Coincident(g21,g9)
    c: Vertical(g22)
    c: Coincident(g22,g10)
    c: Vertical(g23)
    c: Coincident(g23,g11)
    c: Block(g23)
    c: Block(g22)
    c: Block(g21)
    c: Block(g20)
    c: Block(g13)
    c: Block(g14)
    c: Block(g15)
    c: Block(g16)
    c: Block(g17)
    c: Block(g18)
    c: Block(g19)
FEATURE [Part::Extrusion] Extrude022
  Base = -> Sketch030
  Dir = (1,-2e-16,2e-16)
  DirMode = 2
  FaceMakerClass = Part::FaceMakerBullseye
  LengthFwd = 19
  LengthRev = 0
  Placement = pos=(-19,0,0) rot=(0,0,1;0rad)
  Solid = true
  Symmetric = false
FEATURE [Part::Fillet] Fillet022
  Base = -> Extrude022
  Edges = 24 edges r=1.49: [Edge6,Edge11,Edge18,Edge23,Edge30,Edge35,Edge42,Edge47,Edge54,Edge59,Edge66,Edge71,Edge78,Edge83,Edge90,Edge95,Edge102,Edge107,Edge114,Edge119,Edge126,Edge131,Edge138,Edge143]
FEATURE [Part::Cut] Cut020  label="top010"
  Base = -> Cut019
  Tool = -> Fillet022
FEATURE [Sketcher::SketchObject] Sketch032
  FullyConstrained = true
  Placement = pos=(117,19,0) rot=(0.57735,0.57735,0.57735;2.0944rad)
  sketch-geometry (48):
    g0: LineSegment StartX=-49.19 StartY=69.25 StartZ=0 EndX=-49.19 EndY=66.25 EndZ=0
    g1: LineSegment StartX=-49.19 StartY=63.5 StartZ=0 EndX=-49.19 EndY=60.5 EndZ=0
    g2: LineSegment StartX=-49.19 StartY=57.75 StartZ=0 EndX=-49.19 EndY=54.75 EndZ=0
    g3: LineSegment StartX=-49.19 StartY=52 StartZ=0 EndX=-49.19 EndY=49 EndZ=0
    g4: LineSegment StartX=-49.19 StartY=46.25 StartZ=0 EndX=-49.19 EndY=43.25 EndZ=0
    g5: LineSegment StartX=-49.19 StartY=40.5 StartZ=0 EndX=-49.19 EndY=37.5 EndZ=0
    g6: LineSegment StartX=-49.19 StartY=34.5 StartZ=0 EndX=-49.19 EndY=31.5 EndZ=0
    g7: LineSegment StartX=-49.19 StartY=28.75 StartZ=0 EndX=-49.19 EndY=25.75 EndZ=0
    g8: LineSegment StartX=-49.19 StartY=23 StartZ=0 EndX=-49.19 EndY=20 EndZ=0
    g9: LineSegment StartX=-49.19 StartY=17.25 StartZ=0 EndX=-49.19 EndY=14.25 EndZ=0
    g10: LineSegment StartX=-49.19 StartY=11.5 StartZ=0 EndX=-49.19 EndY=8.5 EndZ=0
    g11: LineSegment StartX=-49.19 StartY=5.75 StartZ=0 EndX=-49.19 EndY=2.75 EndZ=0
    g12: ArcOfCircle CenterX=-1.5 CenterY=67.75 CenterZ=0 NormalX=0 NormalY=0 NormalZ=1 AngleXU=0 Radius=1.5 StartAngle=4.71239 EndAngle=7.85398
    g13: ArcOfCircle CenterX=-1.5 CenterY=62 CenterZ=0 NormalX=0 NormalY=0 NormalZ=1 AngleXU=0 Radius=1.5 StartAngle=4.71239 EndAngle=7.85398
    g14: ArcOfCircle CenterX=-1.5 CenterY=56.25 CenterZ=0 NormalX=0 NormalY=0 NormalZ=1 AngleXU=0 Radius=1.5 StartAngle=4.71239 EndAngle=7.85398
    g15: ArcOfCircle CenterX=-11.49 CenterY=50.5 CenterZ=0 NormalX=0 NormalY=0 NormalZ=1 AngleXU=0 Radius=1.5 StartAngle=4.71239 EndAngle=7.85398
    g16: ArcOfCircle CenterX=-16.28 CenterY=44.75 CenterZ=0 NormalX=0 NormalY=0 NormalZ=1 AngleXU=0 Radius=1.5 StartAngle=4.71239 EndAngle=7.85398
    g17: ArcOfCircle CenterX=-18.2337 CenterY=39 CenterZ=0 NormalX=0 NormalY=0 NormalZ=1 AngleXU=0 Radius=1.5 StartAngle=4.71485 EndAngle=7.85398
    g18: ArcOfCircle CenterX=-16.2837 CenterY=27.25 CenterZ=0 NormalX=0 NormalY=0 NormalZ=1 AngleXU=0 Radius=1.5 StartAngle=4.71485 EndAngle=7.85398
    g19: ArcOfCircle CenterX=-18.2337 CenterY=33 CenterZ=0 NormalX=0 NormalY=0 NormalZ=1 AngleXU=0 Radius=1.5 StartAngle=4.71485 EndAngle=7.85398
    g20: ArcOfCircle CenterX=-11.49 CenterY=21.5 CenterZ=0 NormalX=0 NormalY=0 NormalZ=1 AngleXU=0 Radius=1.5 StartAngle=4.71239 EndAngle=7.85398
    g21: ArcOfCircle CenterX=-1.5 CenterY=4.25 CenterZ=0 NormalX=0 NormalY=0 NormalZ=1 AngleXU=0 Radius=1.5 StartAngle=4.71239 EndAngle=7.85398
    g22: ArcOfCircle CenterX=-1.5 CenterY=10 CenterZ=0 NormalX=0 NormalY=0 NormalZ=1 AngleXU=0 Radius=1.5 StartAngle=4.71239 EndAngle=7.85398
    g23: ArcOfCircle CenterX=-1.5 CenterY=15.75 CenterZ=0 NormalX=0 NormalY=0 NormalZ=1 AngleXU=0 Radius=1.5 StartAngle=4.71239 EndAngle=7.85398
    g24: LineSegment StartX=-49.19 StartY=69.25 StartZ=0 EndX=-1.5 EndY=69.25 EndZ=0
    g25: LineSegment StartX=-49.19 StartY=66.25 StartZ=0 EndX=-1.5 EndY=66.25 EndZ=0
    g26: LineSegment StartX=-49.19 StartY=63.5 StartZ=0 EndX=-1.5 EndY=63.5 EndZ=0
    g27: LineSegment StartX=-49.19 StartY=60.5 StartZ=0 EndX=-1.5 EndY=60.5 EndZ=0
    g28: LineSegment StartX=-49.19 StartY=57.75 StartZ=0 EndX=-1.5 EndY=57.75 EndZ=0
    g29: LineSegment StartX=-49.19 StartY=54.75 StartZ=0 EndX=-1.5 EndY=54.75 EndZ=0
    g30: LineSegment StartX=-49.19 StartY=52 StartZ=0 EndX=-11.49 EndY=52 EndZ=0
    g31: LineSegment StartX=-49.19 StartY=49 StartZ=0 EndX=-11.49 EndY=49 EndZ=0
    g32: LineSegment StartX=-49.19 StartY=46.25 StartZ=0 EndX=-16.28 EndY=46.25 EndZ=0
    g33: LineSegment StartX=-49.19 StartY=43.25 StartZ=0 EndX=-16.28 EndY=43.25 EndZ=0
    g34: LineSegment StartX=-49.19 StartY=40.5 StartZ=0 EndX=-18.2337 EndY=40.5 EndZ=0
    g35: LineSegment StartX=-49.19 StartY=37.5 StartZ=0 EndX=-18.23 EndY=37.5 EndZ=0
    g36: LineSegment StartX=-49.19 StartY=34.5 StartZ=0 EndX=-18.2337 EndY=34.5 EndZ=0
    g37: LineSegment StartX=-49.19 StartY=31.5 StartZ=0 EndX=-18.23 EndY=31.5 EndZ=0
    g38: LineSegment StartX=-49.19 StartY=28.75 StartZ=0 EndX=-16.2837 EndY=28.75 EndZ=0
    g39: LineSegment StartX=-49.19 StartY=25.75 StartZ=0 EndX=-16.28 EndY=25.75 EndZ=0
    g40: LineSegment StartX=-49.19 StartY=23 StartZ=0 EndX=-11.49 EndY=23 EndZ=0
    g41: LineSegment StartX=-49.19 StartY=20 StartZ=0 EndX=-11.49 EndY=20 EndZ=0
    g42: LineSegment StartX=-49.19 StartY=17.25 StartZ=0 EndX=-1.5 EndY=17.25 EndZ=0
    g43: LineSegment StartX=-49.19 StartY=14.25 StartZ=0 EndX=-1.5 EndY=14.25 EndZ=0
    g44: LineSegment StartX=-49.19 StartY=11.5 StartZ=0 EndX=-1.5 EndY=11.5 EndZ=0
    g45: LineSegment StartX=-49.19 StartY=8.5 StartZ=0 EndX=-1.5 EndY=8.5 EndZ=0
    g46: LineSegment StartX=-49.19 StartY=5.75 StartZ=0 EndX=-1.5 EndY=5.75 EndZ=0
    g47: LineSegment StartX=-49.19 StartY=2.75 StartZ=0 EndX=-1.5 EndY=2.75 EndZ=0
  constraints (120):
    c: Vertical(g0)
    c: Distance(g0) = 3
    c: Block(g0)
    c: Vertical(g1)
    c: Distance(g1) = 3
    c: Vertical(g2)
    c: Equal(g0,g2) = 3
    c: Block(g2)
    c: Vertical(g3)
    c: Equal(g1,g3) = 3
    c: Vertical(g4)
    c: Equal(g0,g4) = 3
    c: Block(g4)
    c: Vertical(g5)
    c: Equal(g1,g5) = 3
    c: Vertical(g6)
    c: Equal(g0,g6) = 3
    c: Block(g6)
    c: Vertical(g7)
    c: Equal(g1,g7) = 3
    c: Vertical(g8)
    c: Equal(g0,g8) = 3
    c: Block(g8)
    c: Vertical(g9)
    c: Equal(g1,g9) = 3
    c: Vertical(g10)
    c: Equal(g0,g10) = 3
    c: Block(g10)
    c: Vertical(g11)
    c: Equal(g1,g11) = 3
    c: Block(g12)
    c: Block(g13)
    c: Block(g14)
    c: Block(g15)
    c: Block(g16)
    c: Block(g17)
    c: Block(g18)
    c: Block(g19)
    c: Block(g20)
    c: Block(g21)
    c: Block(g22)
    c: Block(g23)
    c: Block(g11)
    c: Block(g9)
    c: Block(g7)
    c: Block(g5)
    c: Block(g3)
    c: Block(g1)
    c: Coincident(g24,g0)
    c: Coincident(g24,g12)
    c: Horizontal(g24)
    c: Coincident(g25,g0)
    c: Coincident(g25,g12)
    c: Horizontal(g25)
    c: Coincident(g26,g1)
    c: Coincident(g26,g13)
    c: Horizontal(g26)
    c: Coincident(g27,g1)
    c: Coincident(g27,g13)
    c: Horizontal(g27)
    c: Coincident(g28,g2)
    c: Coincident(g28,g14)
    c: Horizontal(g28)
    c: Coincident(g29,g2)
    c: Coincident(g29,g14)
    c: Horizontal(g29)
    c: Coincident(g30,g3)
    c: Coincident(g30,g15)
    c: Horizontal(g30)
    c: Coincident(g31,g3)
    c: Coincident(g31,g15)
    c: Horizontal(g31)
    c: Coincident(g32,g4)
    c: Coincident(g32,g16)
    c: Horizontal(g32)
    c: Coincident(g33,g4)
    c: Coincident(g33,g16)
    c: Horizontal(g33)
    c: Coincident(g34,g5)
    c: Coincident(g34,g17)
    c: Horizontal(g34)
    c: Coincident(g35,g5)
    c: Coincident(g35,g17)
    c: Horizontal(g35)
    c: Coincident(g36,g6)
    c: Coincident(g36,g19)
    c: Horizontal(g36)
    c: Coincident(g37,g6)
    c: Coincident(g37,g19)
    c: Horizontal(g37)
    c: Coincident(g38,g7)
    c: Coincident(g38,g18)
    c: Horizontal(g38)
    c: Coincident(g39,g7)
    c: Coincident(g39,g18)
    c: Horizontal(g39)
    c: Coincident(g40,g8)
    c: Coincident(g40,g20)
    c: Horizontal(g40)
    c: Coincident(g41,g8)
    c: Coincident(g41,g20)
    c: Horizontal(g41)
    c: Coincident(g42,g9)
    c: Coincident(g42,g23)
    c: Horizontal(g42)
    c: Coincident(g43,g9)
    c: Coincident(g43,g23)
    c: Horizontal(g43)
    c: Coincident(g44,g10)
    c: Coincident(g44,g22)
    c: Horizontal(g44)
    c: Coincident(g45,g10)
    c: Coincident(g45,g22)
    c: Horizontal(g45)
    c: Coincident(g46,g11)
    c: Coincident(g46,g21)
    c: Horizontal(g46)
    c: Coincident(g47,g11)
    c: Coincident(g47,g21)
    c: Horizontal(g47)
FEATURE [Part::Extrusion] Extrude023
  Base = -> Sketch032
  Dir = (1,-2e-16,2e-16)
  DirMode = 2
  FaceMakerClass = Part::FaceMakerBullseye
  LengthFwd = 19
  LengthRev = 0
  Placement = pos=(-19,0,0) rot=(0,0,1;0rad)
  Solid = true
  Symmetric = false
FEATURE [Part::Fillet] Fillet023
  Base = -> Extrude023
  Edges = <same value as first occurrence — deduplicated (x6 in doc)>
  Placement = pos=(0,0.05,0) rot=(0,0,1;0rad)
FEATURE [Part::Cut] Cut014  label="bottom003"
  Base = -> Cut007
  Tool = -> Fusion047
FEATURE [Part::Cut] Cut021  label="bottom004"
  Base = -> Cut014
  Tool = -> Fillet023
FEATURE [Sketcher::SketchObject] Sketch033
  FullyConstrained = true
  Placement = pos=(117,19,0) rot=(0.57735,0.57735,0.57735;2.0944rad)
  sketch-geometry (8):
    g0: LineSegment StartX=-49.19 StartY=69.25 StartZ=0 EndX=-49.19 EndY=66.25 EndZ=0
    g1: LineSegment StartX=-49.19 StartY=5.75 StartZ=0 EndX=-49.19 EndY=2.75 EndZ=0
    g2: ArcOfCircle CenterX=-1.5 CenterY=67.75 CenterZ=0 NormalX=0 NormalY=0 NormalZ=1 AngleXU=0 Radius=1.5 StartAngle=4.71239 EndAngle=7.85398
    g3: ArcOfCircle CenterX=-1.5 CenterY=4.25 CenterZ=0 NormalX=0 NormalY=0 NormalZ=1 AngleXU=0 Radius=1.5 StartAngle=4.71239 EndAngle=7.85398
    g4: LineSegment StartX=-49.19 StartY=69.25 StartZ=0 EndX=-1.5 EndY=69.25 EndZ=0
    g5: LineSegment StartX=-49.19 StartY=66.25 StartZ=0 EndX=-1.5 EndY=66.25 EndZ=0
    g6: LineSegment StartX=-49.19 StartY=5.75 StartZ=0 EndX=-1.5 EndY=5.75 EndZ=0
    g7: LineSegment StartX=-49.19 StartY=2.75 StartZ=0 EndX=-1.5 EndY=2.75 EndZ=0
  constraints (19):
    c: Vertical(g0)
    c: Distance(g0) = 3
    c: Block(g0)
    c: Vertical(g1)
    c: Block(g2)
    c: Block(g3)
    c: Block(g1)
    c: Coincident(g4,g0)
    c: Coincident(g4,g2)
    c: Horizontal(g4)
    c: Coincident(g5,g0)
    c: Coincident(g5,g2)
    c: Horizontal(g5)
    c: Coincident(g6,g1)
    c: Coincident(g6,g3)
    c: Horizontal(g6)
    c: Coincident(g7,g1)
    c: Coincident(g7,g3)
    c: Horizontal(g7)
FEATURE [Sketcher::SketchObject] Sketch034
  FullyConstrained = true
  Placement = pos=(117,19,0) rot=(0.57735,0.57735,0.57735;2.0944rad)
  sketch-geometry (8):
    g0: LineSegment StartX=-49.19 StartY=63.5 StartZ=0 EndX=-49.19 EndY=60.5 EndZ=0
    g1: LineSegment StartX=-49.19 StartY=11.5 StartZ=0 EndX=-49.19 EndY=8.5 EndZ=0
    g2: ArcOfCircle CenterX=-1.5 CenterY=62 CenterZ=0 NormalX=0 NormalY=0 NormalZ=1 AngleXU=0 Radius=1.5 StartAngle=4.71239 EndAngle=7.85398
    g3: ArcOfCircle CenterX=-1.5 CenterY=10 CenterZ=0 NormalX=0 NormalY=0 NormalZ=1 AngleXU=0 Radius=1.5 StartAngle=4.71239 EndAngle=7.85398
    g4: LineSegment StartX=-49.19 StartY=63.5 StartZ=0 EndX=-1.5 EndY=63.5 EndZ=0
    g5: LineSegment StartX=-49.19 StartY=60.5 StartZ=0 EndX=-1.5 EndY=60.5 EndZ=0
    g6: LineSegment StartX=-49.19 StartY=11.5 StartZ=0 EndX=-1.5 EndY=11.5 EndZ=0
    g7: LineSegment StartX=-49.19 StartY=8.5 StartZ=0 EndX=-1.5 EndY=8.5 EndZ=0
  constraints (19):
    c: Vertical(g0)
    c: Distance(g0) = 3
    c: Vertical(g1)
    c: Block(g1)
    c: Block(g2)
    c: Block(g3)
    c: Block(g0)
    c: Coincident(g4,g0)
    c: Coincident(g4,g2)
    c: Horizontal(g4)
    c: Coincident(g5,g0)
    c: Coincident(g5,g2)
    c: Horizontal(g5)
    c: Coincident(g6,g1)
    c: Coincident(g6,g3)
    c: Horizontal(g6)
    c: Coincident(g7,g1)
    c: Coincident(g7,g3)
    c: Horizontal(g7)
FEATURE [Part::Extrusion] Extrude024
  Base = -> Sketch033
  Dir = (1,0,0)
  DirMode = 2
  FaceMakerClass = Part::FaceMakerBullseye
  LengthFwd = 10
  LengthRev = 0
  Solid = true
  Symmetric = false
FEATURE [Part::Extrusion] Extrude025
  Base = -> Sketch034
  Dir = (1,0,0)
  DirMode = 2
  FaceMakerClass = Part::FaceMakerBullseye
  LengthFwd = 10
  LengthRev = 0
  Solid = true
  Symmetric = false
FEATURE [Part::Fillet] Fillet024  label="removeFromtMoreFrontCaseScrewRetainers"
  Base = -> Extrude024
  Edges = 4 edges r=1.49: [Edge6,Edge11,Edge18,Edge23]
  Placement = pos=(-11,0,0) rot=(0,0,1;0rad)
FEATURE [Part::Fillet] Fillet025  label="removeFromtMoreFrontCaseScrewRetainers001"
  Base = -> Extrude025
  Edges = 4 edges r=1.49: [Edge6,Edge11,Edge18,Edge23]
  Placement = pos=(-19,0,0) rot=(0,0,1;0rad)
FEATURE [Part::Cut] Cut022
  Base = -> Cut015
  Tool = -> Fillet025
FEATURE [Part::Cut] Cut023  label="screwRetainers"
  Base = -> Cut022
  Tool = -> Fillet024
FEATURE [Part::MultiFuse] Fusion056  label="bottom005"
  Shapes = -> [Fusion044,Cut021]
FEATURE [Part::MultiFuse] Fusion057  label="casePillars001"
  Shapes = -> [Cut016,Fusion052]
FEATURE [Part::MultiFuse] Fusion058  label="bottom006"
  Shapes = -> [Fusion056,Cut023]
FEATURE [Part::MultiFuse] Fusion059  label="bottom007"
  Shapes = -> [Fusion058,Fillet005]
FEATURE [Part::MultiFuse] Fusion060  label="bottom008"
  Shapes = -> [Fusion059,Fusion]
FEATURE [Part::MultiFuse] Fusion061  label="top011"
  Shapes = -> [Cut006,Cut020]
FEATURE [Part::MultiFuse] Fusion062  label="top012"
  Shapes = -> [Fusion057,Fusion061]
FEATURE [Sketcher::SketchObject] Sketch035  label="topSketch007"
  FullyConstrained = true
  sketch-geometry (6):
    g0: LineSegment StartX=19 StartY=38 StartZ=0 EndX=117 EndY=38 EndZ=0
    g1: ArcOfCircle CenterX=19 CenterY=19 CenterZ=0 NormalX=0 NormalY=0 NormalZ=1 AngleXU=0 Radius=19 StartAngle=1.5708 EndAngle=3.14159
    g2: LineSegment StartX=117 StartY=38 StartZ=0 EndX=117 EndY=19 EndZ=0
    g3: LineSegment StartX=98 StartY=1.0161e-12 StartZ=0 EndX=5.22862e-06 EndY=1.0161e-12 EndZ=0
    g4: LineSegment StartX=5.22862e-06 StartY=19 StartZ=0 EndX=5.22862e-06 EndY=1.0161e-12 EndZ=0
    g5: ArcOfCircle CenterX=98 CenterY=19 CenterZ=0 NormalX=0 NormalY=0 NormalZ=1 AngleXU=0 Radius=19 StartAngle=4.71239 EndAngle=6.28319
  constraints (16):
    c: Horizontal(g0)
    c: Distance(g0) = 98
    c: Coincident(g1,g0)
    c: Block(g1)
    c: Coincident(g2,g0)
    c: Vertical(g2)
    c: Distance(g2) = 19
    c: Horizontal(g3)
    c: Coincident(g4,g1)
    c: Vertical(g4)
    c: Coincident(g3,g4)
    c: Block(g3)
    c: Coincident(g5,g2)
    c: Coincident(g5,g3)
    c: Block(g0)
    c: Block(g5)
FEATURE [Part::Extrusion] Extrude026  label="sideA001"
  Base = -> Sketch035
  Dir = (0,0,1)
  DirMode = 2
  FaceMakerClass = Part::FaceMakerBullseye
  LengthFwd = 3
  LengthRev = 0
  Placement = pos=(0,0,-2.7) rot=(0,0,1;0rad)
  Solid = true
  Symmetric = false
FEATURE [Sketcher::SketchObject] Sketch036  label="topSketch008"
  FullyConstrained = true
  sketch-geometry (6):
    g0: LineSegment StartX=19 StartY=38 StartZ=0 EndX=117 EndY=38 EndZ=0
    g1: ArcOfCircle CenterX=19 CenterY=19 CenterZ=0 NormalX=0 NormalY=0 NormalZ=1 AngleXU=0 Radius=19 StartAngle=1.5708 EndAngle=3.14159
    g2: LineSegment StartX=117 StartY=38 StartZ=0 EndX=117 EndY=19 EndZ=0
    g3: LineSegment StartX=98 StartY=1.0161e-12 StartZ=0 EndX=5.22862e-06 EndY=1.0161e-12 EndZ=0
    g4: LineSegment StartX=5.22862e-06 StartY=19 StartZ=0 EndX=5.22862e-06 EndY=1.0161e-12 EndZ=0
    g5: ArcOfCircle CenterX=98 CenterY=19 CenterZ=0 NormalX=0 NormalY=0 NormalZ=1 AngleXU=0 Radius=19 StartAngle=4.71239 EndAngle=6.28319
  constraints (16):
    c: Horizontal(g0)
    c: Distance(g0) = 98
    c: Coincident(g1,g0)
    c: Block(g1)
    c: Coincident(g2,g0)
    c: Vertical(g2)
    c: Distance(g2) = 19
    c: Horizontal(g3)
    c: Coincident(g4,g1)
    c: Vertical(g4)
    c: Coincident(g3,g4)
    c: Block(g3)
    c: Coincident(g5,g2)
    c: Coincident(g5,g3)
    c: Block(g0)
    c: Block(g5)
FEATURE [Part::Extrusion] Extrude027  label="sideB001"
  Base = -> Sketch036
  Dir = (0,0,1)
  DirMode = 2
  FaceMakerClass = Part::FaceMakerBullseye
  LengthFwd = 3
  LengthRev = 0
  Placement = pos=(0,0,71.7) rot=(0,0,1;0rad)
  Solid = true
  Symmetric = false
FEATURE [Part::MultiFuse] Fusion064  label="removeFromBottom"
  Shapes = -> [Extrude026,Extrude027]
FEATURE [Part::Cut] Cut024  label="bottom009"
  Base = -> Fusion060
  Tool = -> Fusion064
FEATURE [Sketcher::SketchObject] Sketch037  label="topSketch009"
  FullyConstrained = true
  sketch-geometry (8):
    g0: ArcOfCircle CenterX=19 CenterY=19.1201 CenterZ=0 NormalX=0 NormalY=0 NormalZ=1 AngleXU=0 Radius=18.8799 StartAngle=1.5708 EndAngle=3.14793
    g1: LineSegment StartX=0.120501 StartY=19.0004 StartZ=0 EndX=0.120501 EndY=0.000382114 EndZ=0
    g2: LineSegment StartX=19 StartY=38 StartZ=0 EndX=124 EndY=38 EndZ=0
    g3: LineSegment StartX=0.120501 StartY=0.000382114 StartZ=0 EndX=105.121 EndY=0.000382114 EndZ=0
    g4: LineSegment StartX=124 StartY=38 StartZ=0 EndX=125.616 EndY=38 EndZ=0
    g5: LineSegment StartX=105.121 StartY=0.000382114 StartZ=0 EndX=106.736 EndY=0.000382114 EndZ=0
    g6: ArcOfCircle CenterX=106.616 CenterY=19 CenterZ=0 NormalX=0 NormalY=0 NormalZ=1 AngleXU=0 Radius=19 StartAngle=4.71873 EndAngle=6.28319
    g7: LineSegment StartX=125.616 StartY=38 StartZ=0 EndX=125.616 EndY=19 EndZ=0
  constraints (21):
    c: Block(g0)
    c: Coincident(g1,g0)
    c: Vertical(g1)
    c: Horizontal(g2)
    c: Distance(g2) = 105
    c: Coincident(g2,g0)
    c: Distance(g1) = 19
    c: Coincident(g3,g1)
    c: Horizontal(g3)
    c: Distance(g3) = 105
    c: Coincident(g4,g2)
    c: Horizontal(g4)
    c: Distance(g4) = 1.61553
    c: Horizontal(g5)
    c: Equal(g4,g5) = 1.61553
    c: Coincident(g5,g3)
    c: Block(g6)
    c: Coincident(g6,g5)
    c: Coincident(g7,g4)
    c: Coincident(g7,g6)
    c: Vertical(g7)
FEATURE [Part::Extrusion] Extrude028  label="sideB"
  Base = -> Sketch037
  Dir = (0,0,1)
  DirMode = 2
  FaceMakerClass = Part::FaceMakerBullseye
  LengthFwd = 3
  LengthRev = 0
  Placement = pos=(0,0,72) rot=(0,0,1;0rad)
  Solid = true
  Symmetric = false
FEATURE [Sketcher::SketchObject] Sketch038  label="topSketch010"
  FullyConstrained = true
  sketch-geometry (22):
    g0: LineSegment StartX=5.21097e-06 StartY=3 StartZ=0 EndX=5.21097e-06 EndY=19 EndZ=0
    g1: ArcOfCircle CenterX=19 CenterY=19 CenterZ=0 NormalX=0 NormalY=0 NormalZ=1 AngleXU=0 Radius=19 StartAngle=1.5708 EndAngle=3.14159
    g2: ArcOfCircle CenterX=19 CenterY=19 CenterZ=0 NormalX=0 NormalY=0 NormalZ=1 AngleXU=0 Radius=16 StartAngle=1.5708 EndAngle=3.14159
    g3: LineSegment StartX=114 StartY=35 StartZ=0 EndX=19 EndY=35 EndZ=0
    g4: LineSegment StartX=5.21097e-06 StartY=3 StartZ=0 EndX=5.21097e-06 EndY=0 EndZ=0
    g5: LineSegment StartX=3 StartY=0 StartZ=0 EndX=5.21097e-06 EndY=0 EndZ=0
    g6: LineSegment StartX=3 StartY=19 StartZ=0 EndX=3 EndY=0 EndZ=0
    g7: LineSegment StartX=19 StartY=38 StartZ=0 EndX=124 EndY=38 EndZ=0
    g8: Circle CenterX=119 CenterY=35 CenterZ=0 NormalX=0 NormalY=0 NormalZ=1 AngleXU=0 Radius=1
    g9: Circle CenterX=121 CenterY=35 CenterZ=0 NormalX=0 NormalY=0 NormalZ=1 AngleXU=0 Radius=1
    g10: Circle CenterX=121 CenterY=33 CenterZ=0 NormalX=0 NormalY=0 NormalZ=1 AngleXU=0 Radius=1
    g11: BSplineCurve PolesCount=3 KnotsCount=2 Degree=2 IsPeriodic=0
    g12: GeomPoint X=119 Y=35 Z=0
    g13: GeomPoint X=121 Y=33 Z=0
    g14: LineSegment StartX=119 StartY=35 StartZ=0 EndX=114 EndY=35 EndZ=0
    g15: ArcOfCircle CenterX=105 CenterY=19 CenterZ=0 NormalX=0 NormalY=0 NormalZ=1 AngleXU=0 Radius=16 StartAngle=5.60905 EndAngle=6.28319
    g16: LineSegment StartX=121 StartY=33 StartZ=0 EndX=121 EndY=19 EndZ=0
    g17: LineSegment StartX=117.5 StartY=9.01251 StartZ=0 EndX=121.163 EndY=9.0125 EndZ=0
    g18: ArcOfCircle CenterX=105 CenterY=19 CenterZ=0 NormalX=0 NormalY=0 NormalZ=1 AngleXU=0 Radius=20.6155 StartAngle=5.7297 EndAngle=6.28319
    g19: LineSegment StartX=121.163 StartY=9.0125 StartZ=0 EndX=122.538 EndY=8.16329 EndZ=0
    g20: LineSegment StartX=124 StartY=38 StartZ=0 EndX=125.616 EndY=38 EndZ=0
    g21: LineSegment StartX=125.616 StartY=19 StartZ=0 EndX=125.616 EndY=38 EndZ=0
  constraints (49):
    c: Vertical(g0)
    c: Block(g0)
    c: Coincident(g1,g0)
    c: Block(g1)
    c: Coincident(g2,g1)
    c: Block(g2)
    c: Coincident(g3,g2)
    c: Horizontal(g3)
    c: Tangent(g3,g2)
    c: Coincident(g4,g0)
    c: Distance(g4) = 3
    c: Vertical(g4)
    c: Coincident(g5,g4)
    c: Horizontal(g5)
    c: Coincident(g6,g2)
    c: Coincident(g6,g5)
    c: Vertical(g6)
    c: Horizontal(g7)
    c: Distance(g7) = 105
    c: Coincident(g7,g1)
    c: Block(g3)
    c: Weight(g8) = 1
    c: Equal(g8,g9)
    c: Equal(g8,g10)
    c: InternalAlignment(g8,g11)
    c: InternalAlignment(g9,g11)
    c: InternalAlignment(g10,g11)
    c: InternalAlignment(g12,g11)
    c: InternalAlignment(g13,g11)
    c: Block(g11)
    c: Coincident(g14,g11)
    c: Coincident(g14,g3)
    c: Horizontal(g14)
    c: Block(g15)
    c: Coincident(g16,g11)
    c: Coincident(g16,g15)
    c: Vertical(g16)
    c: Distance(g16) = 14
    c: Coincident(g17,g15)
    c: Block(g18)
    c: Coincident(g19,g18)
    c: Coincident(g20,g7)
    c: Horizontal(g20)
    c: Vertical(g21)
    c: Coincident(g20,g21)
    c: Block(g20)
    c: Block(g21)
    c: Block(g19)
    c: Block(g17)
FEATURE [Part::Extrusion] Extrude029
  Base = -> Sketch038
  Dir = (0,0,1)
  DirMode = 2
  FaceMakerClass = Part::FaceMakerBullseye
  LengthFwd = 72
  LengthRev = 0
  Solid = true
  Symmetric = false
FEATURE [Part::Feature] Face085
  shape: bbox 4.8 x 25.5 x 2e-07 mm, 1 faces, 0 solids (baked)
FEATURE [Part::Revolution] Revolve089  label="moreFrontCaseScrewPost003"
  Angle = 360
  Axis = (0,1,0)
  Base = (0,0,0)
  FaceMakerClass = Part::FaceMakerBullseye
  Placement = pos=(109.5,4.5,3.5) rot=(0,0,1;0rad)
  Solid = false
  Source = -> Face085
  Symmetric = false
FEATURE [Part::Feature] Face086
  shape: bbox 4.8 x 25.5 x 2e-07 mm, 1 faces, 0 solids (baked)
FEATURE [Part::Revolution] Revolve090  label="moreFrontCaseScrewPost004"
  Angle = 360
  Axis = (0,1,0)
  Base = (0,0,0)
  FaceMakerClass = Part::FaceMakerBullseye
  Placement = pos=(109.5,4.5,68.5) rot=(0,0,1;0rad)
  Solid = false
  Source = -> Face086
  Symmetric = false
FEATURE [Part::Fillet] Fillet026  label="top013"
  Base = -> Extrude029
  Edges = 1 edges r=2: [Edge35]
FEATURE [Sketcher::SketchObject] Sketch039
  FullyConstrained = true
  sketch-geometry (7):
    g0: LineSegment StartX=0 StartY=0 StartZ=0 EndX=0 EndY=6 EndZ=0
    g1: Circle CenterX=0 CenterY=0 CenterZ=0 NormalX=0 NormalY=0 NormalZ=1 AngleXU=0 Radius=1
    g2: Circle CenterX=8 CenterY=6 CenterZ=0 NormalX=0 NormalY=0 NormalZ=1 AngleXU=0 Radius=1
    g3: BSplineCurve PolesCount=3 KnotsCount=2 Degree=2 IsPeriodic=0
    g4: GeomPoint X=0 Y=0 Z=0
    g5: GeomPoint X=8 Y=6 Z=0
    g6: LineSegment StartX=0 StartY=6 StartZ=0 EndX=8 EndY=6 EndZ=0
  constraints (14):
    c: Coincident(g0,g-1)
    c: Distance(g0) = 6
    c: Vertical(g0)
    c: Coincident(g3,g0)
    c: Weight(g1) = 1
    c: Equal(g1,g2)
    c: InternalAlignment(g1,g3)
    c: InternalAlignment(g2,g3)
    c: InternalAlignment(g4,g3)
    c: InternalAlignment(g5,g3)
    c: Block(g3)
    c: Coincident(g6,g0)
    c: Coincident(g6,g3)
    c: Horizontal(g6)
FEATURE [Sketcher::SketchObject] Sketch040
  FullyConstrained = true
  sketch-geometry (7):
    g0: LineSegment StartX=0 StartY=0 StartZ=0 EndX=0 EndY=6 EndZ=0
    g1: Circle CenterX=0 CenterY=0 CenterZ=0 NormalX=0 NormalY=0 NormalZ=1 AngleXU=0 Radius=1
    g2: Circle CenterX=8 CenterY=6 CenterZ=0 NormalX=0 NormalY=0 NormalZ=1 AngleXU=0 Radius=1
    g3: BSplineCurve PolesCount=3 KnotsCount=2 Degree=2 IsPeriodic=0
    g4: GeomPoint X=0 Y=0 Z=0
    g5: GeomPoint X=8 Y=6 Z=0
    g6: LineSegment StartX=0 StartY=6 StartZ=0 EndX=8 EndY=6 EndZ=0
  constraints (14):
    c: Coincident(g0,g-1)
    c: Distance(g0) = 6
    c: Vertical(g0)
    c: Coincident(g3,g0)
    c: Weight(g1) = 1
    c: Equal(g1,g2)
    c: InternalAlignment(g1,g3)
    c: InternalAlignment(g2,g3)
    c: InternalAlignment(g4,g3)
    c: InternalAlignment(g5,g3)
    c: Block(g3)
    c: Coincident(g6,g0)
    c: Coincident(g6,g3)
    c: Horizontal(g6)
FEATURE [Sketcher::SketchObject] Sketch041
  FullyConstrained = true
  sketch-geometry (7):
    g0: LineSegment StartX=0 StartY=0 StartZ=0 EndX=0 EndY=6 EndZ=0
    g1: Circle CenterX=0 CenterY=0 CenterZ=0 NormalX=0 NormalY=0 NormalZ=1 AngleXU=0 Radius=1
    g2: Circle CenterX=8 CenterY=6 CenterZ=0 NormalX=0 NormalY=0 NormalZ=1 AngleXU=0 Radius=1
    g3: BSplineCurve PolesCount=3 KnotsCount=2 Degree=2 IsPeriodic=0
    g4: GeomPoint X=0 Y=0 Z=0
    g5: GeomPoint X=8 Y=6 Z=0
    g6: LineSegment StartX=0 StartY=6 StartZ=0 EndX=8 EndY=6 EndZ=0
  constraints (14):
    c: Coincident(g0,g-1)
    c: Distance(g0) = 6
    c: Vertical(g0)
    c: Coincident(g3,g0)
    c: Weight(g1) = 1
    c: Equal(g1,g2)
    c: InternalAlignment(g1,g3)
    c: InternalAlignment(g2,g3)
    c: InternalAlignment(g4,g3)
    c: InternalAlignment(g5,g3)
    c: Block(g3)
    c: Coincident(g6,g0)
    c: Coincident(g6,g3)
    c: Horizontal(g6)
FEATURE [Sketcher::SketchObject] Sketch042
  FullyConstrained = true
  sketch-geometry (7):
    g0: LineSegment StartX=0 StartY=0 StartZ=0 EndX=0 EndY=6 EndZ=0
    g1: Circle CenterX=0 CenterY=0 CenterZ=0 NormalX=0 NormalY=0 NormalZ=1 AngleXU=0 Radius=1
    g2: Circle CenterX=8 CenterY=6 CenterZ=0 NormalX=0 NormalY=0 NormalZ=1 AngleXU=0 Radius=1
    g3: BSplineCurve PolesCount=3 KnotsCount=2 Degree=2 IsPeriodic=0
    g4: GeomPoint X=0 Y=0 Z=0
    g5: GeomPoint X=8 Y=6 Z=0
    g6: LineSegment StartX=0 StartY=6 StartZ=0 EndX=8 EndY=6 EndZ=0
  constraints (14):
    c: Coincident(g0,g-1)
    c: Distance(g0) = 6
    c: Vertical(g0)
    c: Coincident(g3,g0)
    c: Weight(g1) = 1
    c: Equal(g1,g2)
    c: InternalAlignment(g1,g3)
    c: InternalAlignment(g2,g3)
    c: InternalAlignment(g4,g3)
    c: InternalAlignment(g5,g3)
    c: Block(g3)
    c: Coincident(g6,g0)
    c: Coincident(g6,g3)
    c: Horizontal(g6)
FEATURE [Part::Extrusion] Extrude030  label="caseScrewPillarBracket008"
  Base = -> Sketch039
  Dir = (0,0,1)
  DirMode = 2
  FaceMakerClass = Part::FaceMakerBullseye
  LengthFwd = 2.4
  LengthRev = 0
  Placement = pos=(15.76,29,8.8) rot=(0,1,0;0rad)
  Solid = true
  Symmetric = false
FEATURE [Part::Extrusion] Extrude031  label="caseScrewPillarBracket009"
  Base = -> Sketch040
  Dir = (0,0,1)
  DirMode = 2
  FaceMakerClass = Part::FaceMakerBullseye
  LengthFwd = 2.4
  LengthRev = 0
  Placement = pos=(15.76,29,60.8) rot=(0,0,1;0rad)
  Solid = true
  Symmetric = false
FEATURE [Part::Extrusion] Extrude032  label="caseScrewPillarBracket010"
  Base = -> Sketch041
  Dir = (0,0,1)
  DirMode = 2
  FaceMakerClass = Part::FaceMakerBullseye
  LengthFwd = 2.4
  LengthRev = 0
  Placement = pos=(13.7,29,13.26) rot=(0,-1,0;1.5708rad)
  Solid = true
  Symmetric = false
FEATURE [Part::Extrusion] Extrude033  label="caseScrewPillarBracket011"
  Base = -> Sketch042
  Dir = (0,0,1)
  DirMode = 2
  FaceMakerClass = Part::FaceMakerBullseye
  LengthFwd = 2.4
  LengthRev = 0
  Placement = pos=(11.3,29,58.74) rot=(0,1,0;1.5708rad)
  Solid = true
  Symmetric = false
FEATURE [Sketcher::SketchObject] Sketch043
  FullyConstrained = true
  sketch-geometry (7):
    g0: LineSegment StartX=0 StartY=0 StartZ=0 EndX=0 EndY=6 EndZ=0
    g1: Circle CenterX=0 CenterY=0 CenterZ=0 NormalX=0 NormalY=0 NormalZ=1 AngleXU=0 Radius=1
    g2: Circle CenterX=8 CenterY=6 CenterZ=0 NormalX=0 NormalY=0 NormalZ=1 AngleXU=0 Radius=1
    g3: BSplineCurve PolesCount=3 KnotsCount=2 Degree=2 IsPeriodic=0
    g4: GeomPoint X=0 Y=0 Z=0
    g5: GeomPoint X=8 Y=6 Z=0
    g6: LineSegment StartX=0 StartY=6 StartZ=0 EndX=8 EndY=6 EndZ=0
  constraints (14):
    c: Coincident(g0,g-1)
    c: Distance(g0) = 6
    c: Vertical(g0)
    c: Coincident(g3,g0)
    c: Weight(g1) = 1
    c: Equal(g1,g2)
    c: InternalAlignment(g1,g3)
    c: InternalAlignment(g2,g3)
    c: InternalAlignment(g4,g3)
    c: InternalAlignment(g5,g3)
    c: Block(g3)
    c: Coincident(g6,g0)
    c: Coincident(g6,g3)
    c: Horizontal(g6)
FEATURE [Part::Extrusion] Extrude034  label="caseScrewPillarBracket012"
  Base = -> Sketch043
  Dir = (0,0,1)
  DirMode = 2
  FaceMakerClass = Part::FaceMakerBullseye
  LengthFwd = 2.4
  LengthRev = 0
  Placement = pos=(88.3,29,65.23) rot=(0,1,0;1.5708rad)
  Solid = true
  Symmetric = false
FEATURE [Sketcher::SketchObject] Sketch044
  FullyConstrained = true
  sketch-geometry (7):
    g0: LineSegment StartX=0 StartY=0 StartZ=0 EndX=0 EndY=6 EndZ=0
    g1: Circle CenterX=0 CenterY=0 CenterZ=0 NormalX=0 NormalY=0 NormalZ=1 AngleXU=0 Radius=1
    g2: Circle CenterX=8 CenterY=6 CenterZ=0 NormalX=0 NormalY=0 NormalZ=1 AngleXU=0 Radius=1
    g3: BSplineCurve PolesCount=3 KnotsCount=2 Degree=2 IsPeriodic=0
    g4: GeomPoint X=0 Y=0 Z=0
    g5: GeomPoint X=8 Y=6 Z=0
    g6: LineSegment StartX=0 StartY=6 StartZ=0 EndX=8 EndY=6 EndZ=0
  constraints (14):
    c: Coincident(g0,g-1)
    c: Distance(g0) = 6
    c: Vertical(g0)
    c: Coincident(g3,g0)
    c: Weight(g1) = 1
    c: Equal(g1,g2)
    c: InternalAlignment(g1,g3)
    c: InternalAlignment(g2,g3)
    c: InternalAlignment(g4,g3)
    c: InternalAlignment(g5,g3)
    c: Block(g3)
    c: Coincident(g6,g0)
    c: Coincident(g6,g3)
    c: Horizontal(g6)
FEATURE [Part::Extrusion] Extrude035  label="caseScrewPillarBracket013"
  Base = -> Sketch044
  Dir = (0,0,1)
  DirMode = 2
  FaceMakerClass = Part::FaceMakerBullseye
  LengthFwd = 2.4
  LengthRev = 0
  Placement = pos=(90.7,29,6.77) rot=(0,-1,0;1.5708rad)
  Solid = true
  Symmetric = false
FEATURE [Sketcher::SketchObject] Sketch045
  FullyConstrained = true
  sketch-geometry (7):
    g0: LineSegment StartX=0 StartY=0 StartZ=0 EndX=0 EndY=6 EndZ=0
    g1: Circle CenterX=0 CenterY=0 CenterZ=0 NormalX=0 NormalY=0 NormalZ=1 AngleXU=0 Radius=1
    g2: Circle CenterX=8 CenterY=6 CenterZ=0 NormalX=0 NormalY=0 NormalZ=1 AngleXU=0 Radius=1
    g3: BSplineCurve PolesCount=3 KnotsCount=2 Degree=2 IsPeriodic=0
    g4: GeomPoint X=0 Y=0 Z=0
    g5: GeomPoint X=8 Y=6 Z=0
    g6: LineSegment StartX=0 StartY=6 StartZ=0 EndX=8 EndY=6 EndZ=0
  constraints (14):
    c: Coincident(g0,g-1)
    c: Distance(g0) = 6
    c: Vertical(g0)
    c: Coincident(g3,g0)
    c: Weight(g1) = 1
    c: Equal(g1,g2)
    c: InternalAlignment(g1,g3)
    c: InternalAlignment(g2,g3)
    c: InternalAlignment(g4,g3)
    c: InternalAlignment(g5,g3)
    c: Block(g3)
    c: Coincident(g6,g0)
    c: Coincident(g6,g3)
    c: Horizontal(g6)
FEATURE [Sketcher::SketchObject] Sketch046
  FullyConstrained = true
  sketch-geometry (7):
    g0: LineSegment StartX=0 StartY=0 StartZ=0 EndX=0 EndY=6 EndZ=0
    g1: Circle CenterX=0 CenterY=0 CenterZ=0 NormalX=0 NormalY=0 NormalZ=1 AngleXU=0 Radius=1
    g2: Circle CenterX=8 CenterY=6 CenterZ=0 NormalX=0 NormalY=0 NormalZ=1 AngleXU=0 Radius=1
    g3: BSplineCurve PolesCount=3 KnotsCount=2 Degree=2 IsPeriodic=0
    g4: GeomPoint X=0 Y=0 Z=0
    g5: GeomPoint X=8 Y=6 Z=0
    g6: LineSegment StartX=0 StartY=6 StartZ=0 EndX=8 EndY=6 EndZ=0
  constraints (14):
    c: Coincident(g0,g-1)
    c: Distance(g0) = 6
    c: Vertical(g0)
    c: Coincident(g3,g0)
    c: Weight(g1) = 1
    c: Equal(g1,g2)
    c: InternalAlignment(g1,g3)
    c: InternalAlignment(g2,g3)
    c: InternalAlignment(g4,g3)
    c: InternalAlignment(g5,g3)
    c: Block(g3)
    c: Coincident(g6,g0)
    c: Coincident(g6,g3)
    c: Horizontal(g6)
FEATURE [Part::Extrusion] Extrude036  label="caseScrewPillarBracket014"
  Base = -> Sketch045
  Dir = (0,0,1)
  DirMode = 2
  FaceMakerClass = Part::FaceMakerBullseye
  LengthFwd = 2.4
  LengthRev = 0
  Placement = pos=(110.7,29,6.77) rot=(0,-1,0;1.5708rad)
  Solid = true
  Symmetric = false
FEATURE [Part::Extrusion] Extrude037  label="caseScrewPillarBracket015"
  Base = -> Sketch046
  Dir = (0,0,1)
  DirMode = 2
  FaceMakerClass = Part::FaceMakerBullseye
  LengthFwd = 2.4
  LengthRev = 0
  Placement = pos=(108.3,29,65.23) rot=(0,1,0;1.5708rad)
  Solid = true
  Symmetric = false
FEATURE [Part::Box] Box013  label="frontCaseScrewPillarBracket002"
  AttacherType = Attacher::AttachEngine3D
  Height = 2.4
  Length = 22
  Placement = pos=(87,28,2.3) rot=(0,0,1;0rad)
  Width = 7
FEATURE [Part::Box] Box014  label="frontCaseScrewPillarBracket003"
  AttacherType = Attacher::AttachEngine3D
  Height = 2.4
  Length = 22
  Placement = pos=(87,28,67.3) rot=(0,0,1;0rad)
  Width = 7
FEATURE [Part::Feature] Face087
  shape: bbox 4.8 x 30.2 x 2e-07 mm, 1 faces, 0 solids (baked)
FEATURE [Part::Revolution] Revolve091  label="frontCaseScrewPost004"
  Angle = 360
  Axis = (0,1,0)
  Base = (0,0,0)
  FaceMakerClass = Part::FaceMakerBullseye
  Placement = pos=(89.5,4.5,3.5) rot=(0,0,1;0rad)
  Solid = false
  Source = -> Face087
  Symmetric = false
FEATURE [Part::Feature] Face088
  shape: bbox 4.8 x 30.2 x 2e-07 mm, 1 faces, 0 solids (baked)
FEATURE [Part::Revolution] Revolve092  label="frontCaseScrewPost005"
  Angle = 360
  Axis = (0,1,0)
  Base = (0,0,0)
  FaceMakerClass = Part::FaceMakerBullseye
  Placement = pos=(89.5,4.5,68.5) rot=(0,0,1;0rad)
  Solid = false
  Source = -> Face088
  Symmetric = false
FEATURE [Part::Feature] Face089
  shape: bbox 3.5 x 30.2 x 2e-07 mm, 1 faces, 0 solids (baked)
FEATURE [Part::Revolution] Revolve093  label="backCaseScrewPost002"
  Angle = 360
  Axis = (0,1,0)
  Base = (0,0,0)
  FaceMakerClass = Part::FaceMakerBullseye
  Placement = pos=(12.5,4.5,10) rot=(0,0,1;0rad)
  Solid = false
  Source = -> Face089
  Symmetric = false
FEATURE [Part::Feature] Face090
  shape: bbox 3.5 x 30.2 x 2e-07 mm, 1 faces, 0 solids (baked)
FEATURE [Part::Revolution] Revolve094  label="backCaseScrewPost003"
  Angle = 360
  Axis = (0,1,0)
  Base = (0,0,0)
  FaceMakerClass = Part::FaceMakerBullseye
  Placement = pos=(12.5,4.5,62) rot=(0,0,1;0rad)
  Solid = false
  Source = -> Face090
  Symmetric = false
FEATURE [Part::Box] Box015  label="Cube011"
  AttacherType = Attacher::AttachEngine3D
  Height = 28.8
  Length = 3
  Placement = pos=(107.3,28,21.6) rot=(0,0,1;0rad)
  Width = 7
FEATURE [Part::Box] Box016  label="Cube012"
  AttacherType = Attacher::AttachEngine3D
  Height = 3
  Length = 7.4
  Placement = pos=(107.3,28,18.6) rot=(0,0,1;0rad)
  Width = 7
FEATURE [Part::Box] Box017  label="Cube013"
  AttacherType = Attacher::AttachEngine3D
  Height = 3
  Length = 7.4
  Placement = pos=(107.3,28,50.4) rot=(0,0,1;0rad)
  Width = 7
FEATURE [Part::Cylinder] Cylinder024
  Angle = 360
  AttacherType = Attacher::AttachEngine3D
  Height = 20
  Placement = pos=(0,0,36.15) rot=(0,0,1;0rad)
  Radius = 14.3
FEATURE [Part::Cylinder] Cylinder025
  Angle = 360
  AttacherType = Attacher::AttachEngine3D
  Height = 10
  Placement = pos=(0,0,36.15) rot=(0,0,1;0rad)
  Radius = 4
FEATURE [Part::MultiFuse] Fusion066  label="removeToCreteHoleForPlugHousing009"
  Placement = pos=(70,19,36) rot=(0,1,0;1.5708rad)
  Shapes = -> [Cylinder024,Cylinder025]
FEATURE [Part::MultiFuse] Fusion065  label="plugHousingBracketHolder002"
  Shapes = -> [Box017,Box015,Box016]
FEATURE [Part::Cut] Cut025  label="plugHousingBracketHolder003"
  Base = -> Fusion065
  Placement = pos=(7,0,0) rot=(0,0,1;0rad)
  Tool = -> Fusion066
FEATURE [Sketcher::SketchObject] Sketch047
  FullyConstrained = false
  Placement = pos=(0,0,0) rot=(1,0,0;1.5708rad)
  sketch-geometry (24):
    g0: ArcOfCircle CenterX=-4 CenterY=-10.5 CenterZ=0 NormalX=0 NormalY=0 NormalZ=1 AngleXU=0 Radius=1.5 StartAngle=6e-16 EndAngle=3.14159
    g1: ArcOfCircle CenterX=-34.2 CenterY=-10.5 CenterZ=0 NormalX=0 NormalY=0 NormalZ=1 AngleXU=0 Radius=1.5 StartAngle=0 EndAngle=3.14159
    g2: ArcOfCircle CenterX=-34.2 CenterY=-27.7 CenterZ=0 NormalX=0 NormalY=0 NormalZ=1 AngleXU=0 Radius=1.5 StartAngle=3.14159 EndAngle=6.28319
    g3: ArcOfCircle CenterX=-4 CenterY=-27.7 CenterZ=0 NormalX=0 NormalY=0 NormalZ=1 AngleXU=0 Radius=1.5 StartAngle=3.1416 EndAngle=6.28319
    g4: ArcOfCircle CenterX=-10 CenterY=-4.3 CenterZ=0 NormalX=0 NormalY=0 NormalZ=1 AngleXU=0 Radius=1.5 StartAngle=2e-16 EndAngle=3.14159
    g5: ArcOfCircle CenterX=-16.1 CenterY=-1.8 CenterZ=0 NormalX=0 NormalY=0 NormalZ=1 AngleXU=0 Radius=1.5 StartAngle=5e-16 EndAngle=3.14159
    g6: ArcOfCircle CenterX=-22.1 CenterY=-1.8 CenterZ=0 NormalX=0 NormalY=0 NormalZ=1 AngleXU=0 Radius=1.5 StartAngle=5e-16 EndAngle=3.14159
    g7: ArcOfCircle CenterX=-28.2 CenterY=-4.3 CenterZ=0 NormalX=0 NormalY=0 NormalZ=1 AngleXU=0 Radius=1.5 StartAngle=2e-16 EndAngle=3.14159
    g8: ArcOfCircle CenterX=-10 CenterY=-33.9 CenterZ=0 NormalX=0 NormalY=0 NormalZ=1 AngleXU=0 Radius=1.5 StartAngle=3.14159 EndAngle=6.28319
    g9: ArcOfCircle CenterX=-16.1 CenterY=-36.4 CenterZ=0 NormalX=0 NormalY=0 NormalZ=1 AngleXU=0 Radius=1.5 StartAngle=3.14159 EndAngle=6.28319
    g10: ArcOfCircle CenterX=-22.1 CenterY=-36.4 CenterZ=0 NormalX=0 NormalY=0 NormalZ=1 AngleXU=0 Radius=1.5 StartAngle=3.14159 EndAngle=6.28319
    g11: ArcOfCircle CenterX=-28.2 CenterY=-33.9 CenterZ=0 NormalX=0 NormalY=0 NormalZ=1 AngleXU=0 Radius=1.5 StartAngle=3.14159 EndAngle=6.28319
    g12: LineSegment StartX=-35.7 StartY=-10.5 StartZ=0 EndX=-35.7 EndY=-27.7 EndZ=0
    g13: LineSegment StartX=-32.7 StartY=-10.5 StartZ=0 EndX=-32.7 EndY=-27.7 EndZ=0
    g14: LineSegment StartX=-29.7 StartY=-33.9 StartZ=0 EndX=-29.7 EndY=-4.3 EndZ=0
    g15: LineSegment StartX=-26.7 StartY=-33.9 StartZ=0 EndX=-26.7 EndY=-4.3 EndZ=0
    g16: LineSegment StartX=-2.5 StartY=-10.5 StartZ=0 EndX=-2.5 EndY=-27.7 EndZ=0
    g17: LineSegment StartX=-8.5 StartY=-4.3 StartZ=0 EndX=-8.5 EndY=-33.9 EndZ=0
    g18: LineSegment StartX=-5.5 StartY=-10.5 StartZ=0 EndX=-5.5 EndY=-27.7 EndZ=0
    g19: LineSegment StartX=-11.5 StartY=-4.3 StartZ=0 EndX=-11.5 EndY=-33.9 EndZ=0
    g20: LineSegment StartX=-14.6 StartY=-1.8 StartZ=0 EndX=-14.6 EndY=-36.4 EndZ=0
    g21: LineSegment StartX=-17.6 StartY=-1.8 StartZ=0 EndX=-17.6 EndY=-36.4 EndZ=0
    g22: LineSegment StartX=-20.6 StartY=-36.4 StartZ=0 EndX=-20.6 EndY=-1.8 EndZ=0
    g23: LineSegment StartX=-23.6 StartY=-1.8 StartZ=0 EndX=-23.6 EndY=-36.4 EndZ=0
  constraints (48):
    c: Block(g0)
    c: Block(g1)
    c: Block(g2)
    c: Block(g3)
    c: Block(g4)
    c: Block(g5)
    c: Block(g6)
    c: Block(g7)
    c: Block(g8)
    c: Block(g9)
    c: Block(g10)
    c: Block(g11)
    c: Coincident(g12,g1)
    c: Coincident(g12,g2)
    c: Vertical(g12)
    c: Coincident(g13,g1)
    c: Coincident(g13,g2)
    c: Vertical(g13)
    c: Coincident(g14,g11)
    c: Coincident(g14,g7)
    c: Vertical(g14)
    c: Coincident(g15,g11)
    c: Coincident(g15,g7)
    c: Vertical(g15)
    c: Coincident(g16,g0)
    c: Coincident(g16,g3)
    c: Vertical(g16)
    c: Coincident(g17,g4)
    c: Coincident(g17,g8)
    c: Vertical(g17)
    c: Coincident(g18,g0)
    c: Coincident(g18,g3)
    c: Vertical(g18)
    c: Coincident(g19,g4)
    c: Coincident(g19,g8)
    c: Vertical(g19)
    c: Coincident(g20,g5)
    c: Coincident(g20,g9)
    c: Vertical(g20)
    c: Coincident(g21,g5)
    c: Coincident(g21,g9)
    c: Vertical(g21)
    c: Coincident(g22,g10)
    c: Coincident(g22,g6)
    c: Vertical(g22)
    c: Coincident(g23,g6)
    c: Coincident(g23,g10)
    c: Vertical(g23)
FEATURE [Part::Extrusion] Extrude038  label="removeToCreateFanGrillHoles001"
  Base = -> Sketch047
  Dir = (0,-1,6e-16)
  DirMode = 2
  FaceMakerClass = Part::FaceMakerBullseye
  LengthFwd = 10
  LengthRev = 0
  Placement = pos=(65.4,44,54.82) rot=(0,0,1;0rad)
  Solid = true
  Symmetric = false
FEATURE [Part::Feature] Wire004
  shape: bbox 11 x 5.2 x 2e-07 mm, 0 faces, 0 solids (baked)
FEATURE [Part::Revolution] Revolve095
  Angle = 360
  Axis = (0,1,0)
  Base = (0,0,0)
  FaceMakerClass = Part::FaceMakerBullseye
  Placement = pos=(30.3,38,19.7) rot=(0,0,1;0rad)
  Solid = true
  Source = -> Wire004
  Symmetric = false
FEATURE [Part::Feature] Wire005
  shape: bbox 11 x 5.2 x 2e-07 mm, 0 faces, 0 solids (baked)
FEATURE [Part::Revolution] Revolve096
  Angle = 360
  Axis = (0,1,0)
  Base = (0,0,0)
  FaceMakerClass = Part::FaceMakerBullseye
  Placement = pos=(30.3,38,51.7) rot=(0,0,1;0rad)
  Solid = true
  Source = -> Wire005
  Symmetric = false
FEATURE [Part::Feature] Wire006
  shape: bbox 11 x 5.2 x 2e-07 mm, 0 faces, 0 solids (baked)
FEATURE [Part::Revolution] Revolve097
  Angle = 360
  Axis = (0,1,0)
  Base = (0,0,0)
  FaceMakerClass = Part::FaceMakerBullseye
  Placement = pos=(62.3,38,51.7) rot=(0,0,1;0rad)
  Solid = true
  Source = -> Wire006
  Symmetric = false
FEATURE [Part::Feature] Wire007
  shape: bbox 11 x 5.2 x 2e-07 mm, 0 faces, 0 solids (baked)
FEATURE [Part::Revolution] Revolve098
  Angle = 360
  Axis = (0,1,0)
  Base = (0,0,0)
  FaceMakerClass = Part::FaceMakerBullseye
  Placement = pos=(62.3,38,19.7) rot=(0,0,1;0rad)
  Solid = true
  Source = -> Wire007
  Symmetric = false
FEATURE [Part::MultiFuse] Fusion067  label="fanScrewHousing002"
  Shapes = -> [Revolve098,Revolve097,Revolve096,Revolve095]
FEATURE [Part::Feature] Face091 .. Face094  x4 (patterned run collapsed; names and placements below)
  shape: bbox 3.5 x 17.8 x 2e-07 mm, 1 faces, 0 solids (baked)
FEATURE [Part::Revolution] Revolve099  label="removeToCreateScrewAndThreadedInsertHole026"
  Angle = 360
  Axis = (0,1,0)
  Base = (0,0,0)
  FaceMakerClass = Part::FaceMakerBullseye
  Placement = pos=(62.3,30.3,19.7) rot=(0,0,1;0rad)
  Solid = false
  Source = -> Face091
  Symmetric = false
FEATURE [Part::Revolution] Revolve100  label="removeToCreateScrewAndThreadedInsertHole027"
  Angle = 360
  Axis = (0,1,0)
  Base = (0,0,0)
  FaceMakerClass = Part::FaceMakerBullseye
  Placement = pos=(62.3,30.3,51.7) rot=(0,0,1;0rad)
  Solid = false
  Source = -> Face092
  Symmetric = false
FEATURE [Part::Revolution] Revolve101  label="removeToCreateScrewAndThreadedInsertHole028"
  Angle = 360
  Axis = (0,1,0)
  Base = (0,0,0)
  FaceMakerClass = Part::FaceMakerBullseye
  Placement = pos=(30.3,30.3,19.7) rot=(0,0,1;0rad)
  Solid = false
  Source = -> Face093
  Symmetric = false
FEATURE [Part::Revolution] Revolve102  label="removeToCreateScrewAndThreadedInsertHole029"
  Angle = 360
  Axis = (0,1,0)
  Base = (0,0,0)
  FaceMakerClass = Part::FaceMakerBullseye
  Placement = pos=(30.3,30.3,51.7) rot=(0,0,1;0rad)
  Solid = false
  Source = -> Face094
  Symmetric = false
FEATURE [Part::MultiFuse] Fusion068  label="createThreadedInsertHolesForFan002"
  Shapes = -> [Revolve099,Revolve100,Revolve101,Revolve102]
FEATURE [Part::Cut] Cut026  label="fanScrewHousing003"
  Base = -> Fusion067
  Tool = -> Fusion068
FEATURE [Sketcher::SketchObject] Sketch048
  FullyConstrained = false
  Placement = pos=(0,0,0) rot=(1,0,0;1.5708rad)
  sketch-geometry (24):
    g0: ArcOfCircle CenterX=-4 CenterY=-10.5 CenterZ=0 NormalX=0 NormalY=0 NormalZ=1 AngleXU=0 Radius=1.5 StartAngle=6e-16 EndAngle=3.14159
    g1: ArcOfCircle CenterX=-34.2 CenterY=-10.5 CenterZ=0 NormalX=0 NormalY=0 NormalZ=1 AngleXU=0 Radius=1.5 StartAngle=0 EndAngle=3.14159
    g2: ArcOfCircle CenterX=-34.2 CenterY=-27.7 CenterZ=0 NormalX=0 NormalY=0 NormalZ=1 AngleXU=0 Radius=1.5 StartAngle=3.14159 EndAngle=6.28319
    g3: ArcOfCircle CenterX=-4 CenterY=-27.7 CenterZ=0 NormalX=0 NormalY=0 NormalZ=1 AngleXU=0 Radius=1.5 StartAngle=3.1416 EndAngle=6.28319
    g4: ArcOfCircle CenterX=-10 CenterY=-4.3 CenterZ=0 NormalX=0 NormalY=0 NormalZ=1 AngleXU=0 Radius=1.5 StartAngle=2e-16 EndAngle=3.14159
    g5: ArcOfCircle CenterX=-16.1 CenterY=-1.8 CenterZ=0 NormalX=0 NormalY=0 NormalZ=1 AngleXU=0 Radius=1.5 StartAngle=5e-16 EndAngle=3.14159
    g6: ArcOfCircle CenterX=-22.1 CenterY=-1.8 CenterZ=0 NormalX=0 NormalY=0 NormalZ=1 AngleXU=0 Radius=1.5 StartAngle=5e-16 EndAngle=3.14159
    g7: ArcOfCircle CenterX=-28.2 CenterY=-4.3 CenterZ=0 NormalX=0 NormalY=0 NormalZ=1 AngleXU=0 Radius=1.5 StartAngle=2e-16 EndAngle=3.14159
    g8: ArcOfCircle CenterX=-10 CenterY=-33.9 CenterZ=0 NormalX=0 NormalY=0 NormalZ=1 AngleXU=0 Radius=1.5 StartAngle=3.14159 EndAngle=6.28319
    g9: ArcOfCircle CenterX=-16.1 CenterY=-36.4 CenterZ=0 NormalX=0 NormalY=0 NormalZ=1 AngleXU=0 Radius=1.5 StartAngle=3.14159 EndAngle=6.28319
    g10: ArcOfCircle CenterX=-22.1 CenterY=-36.4 CenterZ=0 NormalX=0 NormalY=0 NormalZ=1 AngleXU=0 Radius=1.5 StartAngle=3.14159 EndAngle=6.28319
    g11: ArcOfCircle CenterX=-28.2 CenterY=-33.9 CenterZ=0 NormalX=0 NormalY=0 NormalZ=1 AngleXU=0 Radius=1.5 StartAngle=3.14159 EndAngle=6.28319
    g12: LineSegment StartX=-35.7 StartY=-10.5 StartZ=0 EndX=-35.7 EndY=-27.7 EndZ=0
    g13: LineSegment StartX=-32.7 StartY=-10.5 StartZ=0 EndX=-32.7 EndY=-27.7 EndZ=0
    g14: LineSegment StartX=-29.7 StartY=-33.9 StartZ=0 EndX=-29.7 EndY=-4.3 EndZ=0
    g15: LineSegment StartX=-26.7 StartY=-33.9 StartZ=0 EndX=-26.7 EndY=-4.3 EndZ=0
    g16: LineSegment StartX=-2.5 StartY=-10.5 StartZ=0 EndX=-2.5 EndY=-27.7 EndZ=0
    g17: LineSegment StartX=-8.5 StartY=-4.3 StartZ=0 EndX=-8.5 EndY=-33.9 EndZ=0
    g18: LineSegment StartX=-5.5 StartY=-10.5 StartZ=0 EndX=-5.5 EndY=-27.7 EndZ=0
    g19: LineSegment StartX=-11.5 StartY=-4.3 StartZ=0 EndX=-11.5 EndY=-33.9 EndZ=0
    g20: LineSegment StartX=-14.6 StartY=-1.8 StartZ=0 EndX=-14.6 EndY=-36.4 EndZ=0
    g21: LineSegment StartX=-17.6 StartY=-1.8 StartZ=0 EndX=-17.6 EndY=-36.4 EndZ=0
    g22: LineSegment StartX=-20.6 StartY=-36.4 StartZ=0 EndX=-20.6 EndY=-1.8 EndZ=0
    g23: LineSegment StartX=-23.6 StartY=-1.8 StartZ=0 EndX=-23.6 EndY=-36.4 EndZ=0
  constraints (48):
    c: Block(g0)
    c: Block(g1)
    c: Block(g2)
    c: Block(g3)
    c: Block(g4)
    c: Block(g5)
    c: Block(g6)
    c: Block(g7)
    c: Block(g8)
    c: Block(g9)
    c: Block(g10)
    c: Block(g11)
    c: Coincident(g12,g1)
    c: Coincident(g12,g2)
    c: Vertical(g12)
    c: Coincident(g13,g1)
    c: Coincident(g13,g2)
    c: Vertical(g13)
    c: Coincident(g14,g11)
    c: Coincident(g14,g7)
    c: Vertical(g14)
    c: Coincident(g15,g11)
    c: Coincident(g15,g7)
    c: Vertical(g15)
    c: Coincident(g16,g0)
    c: Coincident(g16,g3)
    c: Vertical(g16)
    c: Coincident(g17,g4)
    c: Coincident(g17,g8)
    c: Vertical(g17)
    c: Coincident(g18,g0)
    c: Coincident(g18,g3)
    c: Vertical(g18)
    c: Coincident(g19,g4)
    c: Coincident(g19,g8)
    c: Vertical(g19)
    c: Coincident(g20,g5)
    c: Coincident(g20,g9)
    c: Vertical(g20)
    c: Coincident(g21,g5)
    c: Coincident(g21,g9)
    c: Vertical(g21)
    c: Coincident(g22,g10)
    c: Coincident(g22,g6)
    c: Vertical(g22)
    c: Coincident(g23,g6)
    c: Coincident(g23,g10)
    c: Vertical(g23)
FEATURE [Part::Extrusion] Extrude039  label="removeToCreateFanGrillHoles002"
  Base = -> Sketch048
  Dir = (0,-1,6e-16)
  DirMode = 2
  FaceMakerClass = Part::FaceMakerBullseye
  LengthFwd = 10
  LengthRev = 0
  Placement = pos=(65.4,44,54.82) rot=(0,0,1;0rad)
  Solid = true
  Symmetric = false
FEATURE [Part::Cut] Cut027  label="fanScrewHousing004"
  Base = -> Cut026
  Tool = -> Extrude038
FEATURE [Part::Cut] Cut028  label="top014"
  Base = -> Fillet026
  Tool = -> Extrude039
FEATURE [Part::Feature] Face095 .. Face098  x4 (patterned run collapsed; names and placements below)
  shape: bbox 3.5 x 17.8 x 2e-07 mm, 1 faces, 0 solids (baked)
FEATURE [Part::Revolution] Revolve103  label="removeToCreateScrewAndThreadedInsertHole030"
  Angle = 360
  Axis = (0,1,0)
  Base = (0,0,0)
  FaceMakerClass = Part::FaceMakerBullseye
  Placement = pos=(62.3,30.3,19.7) rot=(0,0,1;0rad)
  Solid = false
  Source = -> Face095
  Symmetric = false
FEATURE [Part::Revolution] Revolve104  label="removeToCreateScrewAndThreadedInsertHole031"
  Angle = 360
  Axis = (0,1,0)
  Base = (0,0,0)
  FaceMakerClass = Part::FaceMakerBullseye
  Placement = pos=(62.3,30.3,51.7) rot=(0,0,1;0rad)
  Solid = false
  Source = -> Face096
  Symmetric = false
FEATURE [Part::Revolution] Revolve105  label="removeToCreateScrewAndThreadedInsertHole032"
  Angle = 360
  Axis = (0,1,0)
  Base = (0,0,0)
  FaceMakerClass = Part::FaceMakerBullseye
  Placement = pos=(30.3,30.3,19.7) rot=(0,0,1;0rad)
  Solid = false
  Source = -> Face097
  Symmetric = false
FEATURE [Part::Revolution] Revolve106  label="removeToCreateScrewAndThreadedInsertHole033"
  Angle = 360
  Axis = (0,1,0)
  Base = (0,0,0)
  FaceMakerClass = Part::FaceMakerBullseye
  Placement = pos=(30.3,30.3,51.7) rot=(0,0,1;0rad)
  Solid = false
  Source = -> Face098
  Symmetric = false
FEATURE [Part::MultiFuse] Fusion069  label="createThreadedInsertHolesForFan003"
  Shapes = -> [Revolve103,Revolve104,Revolve105,Revolve106]
FEATURE [Part::Cut] Cut029  label="top015"
  Base = -> Cut028
  Tool = -> Fusion054
FEATURE [Part::Cut] Cut030  label="fanScrewHousing005"
  Base = -> Cut027
  Tool = -> Fusion069
FEATURE [Part::Cylinder] Cylinder026  label="removeToCreteHoleForPlugHousing010"
  Angle = 360
  AttacherType = Attacher::AttachEngine3D
  Height = 20
  Placement = pos=(-2,19,36) rot=(0,1,0;1.5708rad)
  Radius = 14.3
FEATURE [Part::Box] Box018  label="removeToCreteHoleForPlugHousing011"
  AttacherType = Attacher::AttachEngine3D
  Height = 28.6
  Length = 10
  Placement = pos=(-2,0,21.7) rot=(0,0,1;0rad)
  Width = 19
FEATURE [Part::Box] Box019  label="wireHolderBottomCaseBit"
  AttacherType = Attacher::AttachEngine3D
  Height = 28
  Length = 3
  Placement = pos=(0,0,22) rot=(0,0,1;0rad)
  Width = 21
FEATURE [Part::Cylinder] Cylinder027  label="removeToCreteHoleForPlugHousing012"
  Angle = 360
  AttacherType = Attacher::AttachEngine3D
  Height = 20
  Placement = pos=(-2,19,36) rot=(0,1,0;1.5708rad)
  Radius = 14.3
FEATURE [Part::Cut] Cut031  label="wireHolderBottomCaseBit001"
  Base = -> Box019
  Tool = -> Cylinder027
FEATURE [Part::MultiFuse] Fusion070  label="removeToCreteHoleForPlugHousing013"
  Shapes = -> [Box018,Cylinder026]
FEATURE [Part::Cut] Cut032  label="top016"
  Base = -> Cut029
  Tool = -> Fusion070
FEATURE [Part::Cylinder] Cylinder028
  Angle = 360
  AttacherType = Attacher::AttachEngine3D
  Height = 20
  Placement = pos=(0,0,36.15) rot=(0,0,1;0rad)
  Radius = 14.3
FEATURE [Part::Cylinder] Cylinder029
  Angle = 360
  AttacherType = Attacher::AttachEngine3D
  Height = 10
  Placement = pos=(0,0,36.15) rot=(0,0,1;0rad)
  Radius = 4
FEATURE [Part::MultiFuse] Fusion071  label="removeToCreteHoleForPlugHousing014"
  Placement = pos=(70,19,36) rot=(0,1,0;1.5708rad)
  Shapes = -> [Cylinder028,Cylinder029]
FEATURE [Sketcher::SketchObject] Sketch049  label="topSketch011"
  FullyConstrained = true
  sketch-geometry (4):
    g0: ArcOfCircle CenterX=105 CenterY=19 CenterZ=0 NormalX=0 NormalY=0 NormalZ=1 AngleXU=0 Radius=20.6155 StartAngle=5.54125 EndAngle=6.28319
    g1: ArcOfCircle CenterX=105 CenterY=19 CenterZ=0 NormalX=0 NormalY=0 NormalZ=1 AngleXU=0 Radius=13 StartAngle=5.54125 EndAngle=6.28319
    g2: LineSegment StartX=118 StartY=19 StartZ=0 EndX=125.616 EndY=19 EndZ=0
    g3: LineSegment StartX=114.583 StartY=10.2157 StartZ=0 EndX=120.197 EndY=5.06982 EndZ=0
  constraints (7):
    c: Block(g0)
    c: Block(g1)
    c: Coincident(g2,g1)
    c: Coincident(g2,g0)
    c: Horizontal(g2)
    c: Coincident(g3,g1)
    c: Coincident(g3,g0)
FEATURE [Part::Box] Box020  label="removeToCreteHoleForPlugHousing015"
  AttacherType = Attacher::AttachEngine3D
  Height = 28.6
  Length = 20
  Placement = pos=(106.15,0,21.7) rot=(0,0,1;0rad)
  Width = 19
FEATURE [Part::MultiFuse] Fusion072  label="removeToCreteHoleForPlugHousing016"
  Shapes = -> [Box020,Fusion071]
FEATURE [Part::Cut] Cut033  label="removeToCreteHoleForPlugHousing017"
  Base = -> Cut032
  Tool = -> Fusion072
FEATURE [Part::Cylinder] Cylinder030
  Angle = 360
  AttacherType = Attacher::AttachEngine3D
  Height = 20
  Placement = pos=(0,0,36.15) rot=(0,0,1;0rad)
  Radius = 14.3
FEATURE [Part::Cylinder] Cylinder031
  Angle = 360
  AttacherType = Attacher::AttachEngine3D
  Height = 10
  Placement = pos=(0,0,36.15) rot=(0,0,1;0rad)
  Radius = 4
FEATURE [Part::Box] Box021  label="removeToCreteHoleForPlugHousing019"
  AttacherType = Attacher::AttachEngine3D
  Height = 28.6
  Length = 20
  Placement = pos=(106.15,0,21.7) rot=(0,0,1;0rad)
  Width = 19
FEATURE [Part::MultiFuse] Fusion074  label="removeToCreteHoleForPlugHousing020"
  Placement = pos=(70,19,36) rot=(0,1,0;1.5708rad)
  Shapes = -> [Cylinder030,Cylinder031]
FEATURE [Part::MultiFuse] Fusion073  label="removeToCreteHoleForPlugHousing018"
  Placement = pos=(0,0,28.3) rot=(0,0,1;0rad)
  Shapes = -> [Box021,Fusion074]
FEATURE [Part::Cylinder] Cylinder032
  Angle = 360
  AttacherType = Attacher::AttachEngine3D
  Height = 20
  Placement = pos=(0,0,36.15) rot=(0,0,1;0rad)
  Radius = 14.3
FEATURE [Part::Cylinder] Cylinder033
  Angle = 360
  AttacherType = Attacher::AttachEngine3D
  Height = 10
  Placement = pos=(0,0,36.15) rot=(0,0,1;0rad)
  Radius = 4
FEATURE [Part::Box] Box022  label="removeToCreteHoleForPlugHousing021"
  AttacherType = Attacher::AttachEngine3D
  Height = 28.6
  Length = 20
  Placement = pos=(106.15,0,21.7) rot=(0,0,1;0rad)
  Width = 19
FEATURE [Part::MultiFuse] Fusion076  label="removeToCreteHoleForPlugHousing023"
  Placement = pos=(70,19,36) rot=(0,1,0;1.5708rad)
  Shapes = -> [Cylinder032,Cylinder033]
FEATURE [Part::MultiFuse] Fusion075  label="removeToCreteHoleForPlugHousing022"
  Placement = pos=(0,0,-28.3) rot=(0,0,1;0rad)
  Shapes = -> [Box022,Fusion076]
FEATURE [Part::MultiFuse] Fusion077  label="removeToCreatePlugHousingBottomBit"
  Shapes = -> [Fusion075,Fusion073]
FEATURE [Part::Cylinder] Cylinder034
  Angle = 360
  AttacherType = Attacher::AttachEngine3D
  Height = 20
  Placement = pos=(0,0,36.15) rot=(0,0,1;0rad)
  Radius = 14
FEATURE [Part::Cylinder] Cylinder035
  Angle = 360
  AttacherType = Attacher::AttachEngine3D
  Height = 10
  Placement = pos=(0,0,36.15) rot=(0,0,1;0rad)
  Radius = 4
FEATURE [Part::MultiFuse] Fusion078  label="removeToCreteHoleForPlugHousing024"
  Placement = pos=(70,19,36) rot=(0,1,0;1.5708rad)
  Shapes = -> [Cylinder034,Cylinder035]
FEATURE [Part::MultiFuse] Fusion079  label="removeToCreatePlugHousingBottomBit001"
  Shapes = -> [Fusion078,Fusion077]
FEATURE [Part::Extrusion] Extrude040  label="bottomPlugHousingBit"
  Base = -> Sketch049
  Dir = (0,0,1)
  DirMode = 2
  FaceMakerClass = Part::FaceMakerBullseye
  LengthFwd = 72
  LengthRev = 0
  Solid = true
  Symmetric = false
FEATURE [Part::Cut] Cut034  label="bottomPlugHousingBit001"
  Base = -> Extrude040
  Placement = pos=(-0.09,0,0) rot=(0,0,1;0rad)
  Tool = -> Fusion079
FEATURE [Part::Box] Box023  label="Cube014"
  AttacherType = Attacher::AttachEngine3D
  Height = 16
  Length = 8
  Placement = pos=(12.7,31.52,28) rot=(0,0,1;0rad)
  Width = 4
FEATURE [Part::Cylinder] Cylinder036
  Angle = 360
  AttacherType = Attacher::AttachEngine3D
  Height = 10
  Placement = pos=(0,0,36.15) rot=(0,0,1;0rad)
  Radius = 4
FEATURE [Part::Cylinder] Cylinder037
  Angle = 360
  AttacherType = Attacher::AttachEngine3D
  Height = 20
  Placement = pos=(0,0,36.15) rot=(0,0,1;0rad)
  Radius = 8.2
FEATURE [Part::MultiFuse] Fusion080  label="removeToCreteHoleForPlugHousing025"
  Placement = pos=(-42,19,36) rot=(0,1,0;1.5708rad)
  Shapes = -> [Cylinder037,Cylinder036]
FEATURE [Sketcher::SketchObject] Sketch050  label="topSketch012"
  FullyConstrained = true
  sketch-geometry (4):
    g0: LineSegment StartX=16.8446 StartY=31.512 StartZ=0 EndX=16.3251 EndY=34.4666 EndZ=0
    g1: ArcOfCircle CenterX=19 CenterY=19.2524 CenterZ=0 NormalX=0 NormalY=0 NormalZ=1 AngleXU=0 Radius=15.4476 StartAngle=1.74483 EndAngle=2.72717
    g2: ArcOfCircle CenterX=19 CenterY=19.2524 CenterZ=0 NormalX=0 NormalY=0 NormalZ=1 AngleXU=0 Radius=12.4476 StartAngle=1.74483 EndAngle=2.73189
    g3: LineSegment StartX=4.86004 StartY=25.4725 StartZ=0 EndX=7.58253 EndY=24.2107 EndZ=0
  constraints (7):
    c: Block(g0)
    c: Coincident(g1,g0)
    c: Coincident(g2,g0)
    c: Coincident(g3,g1)
    c: Coincident(g3,g2)
    c: Block(g1)
    c: Block(g2)
FEATURE [Part::Extrusion] Extrude041
  Base = -> Sketch050
  Dir = (0,0,1)
  DirMode = 2
  FaceMakerClass = Part::FaceMakerBullseye
  LengthFwd = 10.6
  LengthRev = 0
  Placement = pos=(0,0,31) rot=(0,0,1;0rad)
  Solid = true
  Symmetric = false
FEATURE [Part::Cut] Cut035
  Base = -> Extrude041
  Placement = pos=(0,0,-0.3) rot=(0,0,1;0rad)
  Tool = -> Fusion080
FEATURE [Part::Cut] Cut036
  Base = -> Box023
  Tool = -> Cut035
FEATURE [Part::Fillet] Fillet027
  Base = -> Cut036
  Edges = 1 edges r=0.7: [Edge13]
FEATURE [Part::Fillet] Fillet028
  Base = -> Fillet027
  Edges = 1 edges r=0.7: [Edge13]
FEATURE [Part::Fillet] Fillet029
  Base = -> Fillet028
  Edges = 1 edges r=0.7: [Edge16]
FEATURE [Part::Fillet] Fillet030
  Base = -> Fillet029
  Edges = 1 edges r=0.7: [Edge11]
FEATURE [Part::Fillet] Fillet031
  Base = -> Fillet030
  Edges = 1 edges r=0.7: [Edge10]
FEATURE [Part::Fillet] Fillet032
  Base = -> Fillet031
  Edges = 1 edges r=1.2: [Edge5]
FEATURE [Part::Fillet] Fillet033
  Base = -> Fillet032
  Edges = 1 edges r=1.2: [Edge12]
FEATURE [Part::Fillet] Fillet034  label="wireHousingRetainer"
  Base = -> Fillet033
  Edges = 1 edges r=2: [Edge1]
  Placement = pos=(0.3,0,0) rot=(0,0,1;0rad)
FEATURE [Part::Feature] Face099
  shape: bbox 3.5 x 17.8 x 2e-07 mm, 1 faces, 0 solids (baked)
FEATURE [Part::Revolution] Revolve107  label="removeToCreateScrewAndThreadedInsertHole034"
  Angle = 360
  Axis = (0,1,0)
  Base = (0,0,0)
  FaceMakerClass = Part::FaceMakerBullseye
  Placement = pos=(12.5,0,10) rot=(0,0,1;0rad)
  Solid = false
  Source = -> Face099
  Symmetric = false
FEATURE [Part::Feature] Face100
  shape: bbox 3.5 x 17.8 x 2e-07 mm, 1 faces, 0 solids (baked)
FEATURE [Part::Revolution] Revolve108  label="removeToCreateScrewAndThreadedInsertHole035"
  Angle = 360
  Axis = (0,1,0)
  Base = (0,0,0)
  FaceMakerClass = Part::FaceMakerBullseye
  Placement = pos=(12.5,0,62) rot=(0,0,1;0rad)
  Solid = false
  Source = -> Face100
  Symmetric = false
FEATURE [Part::Feature] Face101
  shape: bbox 3.5 x 17.8 x 2e-07 mm, 1 faces, 0 solids (baked)
FEATURE [Part::Revolution] Revolve109  label="removeToCreateScrewAndThreadedInsertHole036"
  Angle = 360
  Axis = (0,1,0)
  Base = (0,0,0)
  FaceMakerClass = Part::FaceMakerBullseye
  Placement = pos=(89.5,0,68.5) rot=(0,0,1;0rad)
  Solid = false
  Source = -> Face101
  Symmetric = false
FEATURE [Part::Feature] Face102
  shape: bbox 3.5 x 17.8 x 2e-07 mm, 1 faces, 0 solids (baked)
FEATURE [Part::Revolution] Revolve110  label="removeToCreateScrewAndThreadedInsertHole037"
  Angle = 360
  Axis = (0,1,0)
  Base = (0,0,0)
  FaceMakerClass = Part::FaceMakerBullseye
  Placement = pos=(89.5,0,3.5) rot=(0,0,1;0rad)
  Solid = false
  Source = -> Face102
  Symmetric = false
FEATURE [Part::Feature] Face103
  shape: bbox 3.5 x 17.8 x 2e-07 mm, 1 faces, 0 solids (baked)
FEATURE [Part::Revolution] Revolve111  label="removeToCreateScrewAndThreadedInsertHole038"
  Angle = 360
  Axis = (0,1,0)
  Base = (0,0,0)
  FaceMakerClass = Part::FaceMakerBullseye
  Placement = pos=(109.5,4.7,3.5) rot=(0,0,1;0rad)
  Solid = false
  Source = -> Face103
  Symmetric = false
FEATURE [Part::Feature] Face104
  shape: bbox 3.5 x 17.8 x 2e-07 mm, 1 faces, 0 solids (baked)
FEATURE [Part::Revolution] Revolve112  label="removeToCreateScrewAndThreadedInsertHole039"
  Angle = 360
  Axis = (0,1,0)
  Base = (0,0,0)
  FaceMakerClass = Part::FaceMakerBullseye
  Placement = pos=(109.5,4.7,68.5) rot=(0,0,1;0rad)
  Solid = false
  Source = -> Face104
  Symmetric = false
FEATURE [Part::MultiFuse] Fusion081  label="removeToCreateScrewAndThreadedInsertHole040"
  Shapes = -> [Revolve107,Revolve108,Revolve109,Revolve110,Revolve111,Revolve112]
FEATURE [Part::MultiFuse] Fusion082  label="casePillars002"
  Shapes = -> [Revolve094,Revolve092,Revolve090,Revolve089,Revolve091,Revolve093]
FEATURE [Part::Cut] Cut037  label="casePillars003"
  Base = -> Fusion082
  Tool = -> Fusion081
FEATURE [Sketcher::SketchObject] Sketch051
  FullyConstrained = true
  Placement = pos=(117,19,0) rot=(0.57735,0.57735,0.57735;2.0944rad)
  sketch-geometry (48):
    g0: LineSegment StartX=-49.19 StartY=69.25 StartZ=0 EndX=-49.19 EndY=66.25 EndZ=0
    g1: LineSegment StartX=-49.19 StartY=63.5 StartZ=0 EndX=-49.19 EndY=60.5 EndZ=0
    g2: LineSegment StartX=-49.19 StartY=57.75 StartZ=0 EndX=-49.19 EndY=54.75 EndZ=0
    g3: LineSegment StartX=-49.19 StartY=52 StartZ=0 EndX=-49.19 EndY=49 EndZ=0
    g4: LineSegment StartX=-49.19 StartY=46.25 StartZ=0 EndX=-49.19 EndY=43.25 EndZ=0
    g5: LineSegment StartX=-49.19 StartY=40.5 StartZ=0 EndX=-49.19 EndY=37.5 EndZ=0
    g6: LineSegment StartX=-49.19 StartY=34.5 StartZ=0 EndX=-49.19 EndY=31.5 EndZ=0
    g7: LineSegment StartX=-49.19 StartY=28.75 StartZ=0 EndX=-49.19 EndY=25.75 EndZ=0
    g8: LineSegment StartX=-49.19 StartY=23 StartZ=0 EndX=-49.19 EndY=20 EndZ=0
    g9: LineSegment StartX=-49.19 StartY=17.25 StartZ=0 EndX=-49.19 EndY=14.25 EndZ=0
    g10: LineSegment StartX=-49.19 StartY=11.5 StartZ=0 EndX=-49.19 EndY=8.5 EndZ=0
    g11: LineSegment StartX=-49.19 StartY=5.75 StartZ=0 EndX=-49.19 EndY=2.75 EndZ=0
    g12: ArcOfCircle CenterX=-1.5 CenterY=67.75 CenterZ=0 NormalX=0 NormalY=0 NormalZ=1 AngleXU=0 Radius=1.5 StartAngle=4.71239 EndAngle=7.85398
    g13: ArcOfCircle CenterX=-1.5 CenterY=62 CenterZ=0 NormalX=0 NormalY=0 NormalZ=1 AngleXU=0 Radius=1.5 StartAngle=4.71239 EndAngle=7.85398
    g14: ArcOfCircle CenterX=-1.5 CenterY=56.25 CenterZ=0 NormalX=0 NormalY=0 NormalZ=1 AngleXU=0 Radius=1.5 StartAngle=4.71239 EndAngle=7.85398
    g15: ArcOfCircle CenterX=-11.49 CenterY=50.5 CenterZ=0 NormalX=0 NormalY=0 NormalZ=1 AngleXU=0 Radius=1.5 StartAngle=4.71239 EndAngle=7.85398
    g16: ArcOfCircle CenterX=-16.28 CenterY=44.75 CenterZ=0 NormalX=0 NormalY=0 NormalZ=1 AngleXU=0 Radius=1.5 StartAngle=4.71239 EndAngle=7.85398
    g17: ArcOfCircle CenterX=-18.2337 CenterY=39 CenterZ=0 NormalX=0 NormalY=0 NormalZ=1 AngleXU=0 Radius=1.5 StartAngle=4.71485 EndAngle=7.85398
    g18: ArcOfCircle CenterX=-16.2837 CenterY=27.25 CenterZ=0 NormalX=0 NormalY=0 NormalZ=1 AngleXU=0 Radius=1.5 StartAngle=4.71485 EndAngle=7.85398
    g19: ArcOfCircle CenterX=-18.2337 CenterY=33 CenterZ=0 NormalX=0 NormalY=0 NormalZ=1 AngleXU=0 Radius=1.5 StartAngle=4.71485 EndAngle=7.85398
    g20: ArcOfCircle CenterX=-11.49 CenterY=21.5 CenterZ=0 NormalX=0 NormalY=0 NormalZ=1 AngleXU=0 Radius=1.5 StartAngle=4.71239 EndAngle=7.85398
    g21: ArcOfCircle CenterX=-1.5 CenterY=4.25 CenterZ=0 NormalX=0 NormalY=0 NormalZ=1 AngleXU=0 Radius=1.5 StartAngle=4.71239 EndAngle=7.85398
    g22: ArcOfCircle CenterX=-1.5 CenterY=10 CenterZ=0 NormalX=0 NormalY=0 NormalZ=1 AngleXU=0 Radius=1.5 StartAngle=4.71239 EndAngle=7.85398
    g23: ArcOfCircle CenterX=-1.5 CenterY=15.75 CenterZ=0 NormalX=0 NormalY=0 NormalZ=1 AngleXU=0 Radius=1.5 StartAngle=4.71239 EndAngle=7.85398
    g24: LineSegment StartX=-49.19 StartY=69.25 StartZ=0 EndX=-1.5 EndY=69.25 EndZ=0
    g25: LineSegment StartX=-49.19 StartY=66.25 StartZ=0 EndX=-1.5 EndY=66.25 EndZ=0
    g26: LineSegment StartX=-49.19 StartY=63.5 StartZ=0 EndX=-1.5 EndY=63.5 EndZ=0
    g27: LineSegment StartX=-49.19 StartY=60.5 StartZ=0 EndX=-1.5 EndY=60.5 EndZ=0
    g28: LineSegment StartX=-49.19 StartY=57.75 StartZ=0 EndX=-1.5 EndY=57.75 EndZ=0
    g29: LineSegment StartX=-49.19 StartY=54.75 StartZ=0 EndX=-1.5 EndY=54.75 EndZ=0
    g30: LineSegment StartX=-49.19 StartY=52 StartZ=0 EndX=-11.49 EndY=52 EndZ=0
    g31: LineSegment StartX=-49.19 StartY=49 StartZ=0 EndX=-11.49 EndY=49 EndZ=0
    g32: LineSegment StartX=-49.19 StartY=46.25 StartZ=0 EndX=-16.28 EndY=46.25 EndZ=0
    g33: LineSegment StartX=-49.19 StartY=43.25 StartZ=0 EndX=-16.28 EndY=43.25 EndZ=0
    g34: LineSegment StartX=-49.19 StartY=40.5 StartZ=0 EndX=-18.2337 EndY=40.5 EndZ=0
    g35: LineSegment StartX=-49.19 StartY=37.5 StartZ=0 EndX=-18.23 EndY=37.5 EndZ=0
    g36: LineSegment StartX=-49.19 StartY=34.5 StartZ=0 EndX=-18.2337 EndY=34.5 EndZ=0
    g37: LineSegment StartX=-49.19 StartY=31.5 StartZ=0 EndX=-18.23 EndY=31.5 EndZ=0
    g38: LineSegment StartX=-49.19 StartY=28.75 StartZ=0 EndX=-16.2837 EndY=28.75 EndZ=0
    g39: LineSegment StartX=-49.19 StartY=25.75 StartZ=0 EndX=-16.28 EndY=25.75 EndZ=0
    g40: LineSegment StartX=-49.19 StartY=23 StartZ=0 EndX=-11.49 EndY=23 EndZ=0
    g41: LineSegment StartX=-49.19 StartY=20 StartZ=0 EndX=-11.49 EndY=20 EndZ=0
    g42: LineSegment StartX=-49.19 StartY=17.25 StartZ=0 EndX=-1.5 EndY=17.25 EndZ=0
    g43: LineSegment StartX=-49.19 StartY=14.25 StartZ=0 EndX=-1.5 EndY=14.25 EndZ=0
    g44: LineSegment StartX=-49.19 StartY=11.5 StartZ=0 EndX=-1.5 EndY=11.5 EndZ=0
    g45: LineSegment StartX=-49.19 StartY=8.5 StartZ=0 EndX=-1.5 EndY=8.5 EndZ=0
    g46: LineSegment StartX=-49.19 StartY=5.75 StartZ=0 EndX=-1.5 EndY=5.75 EndZ=0
    g47: LineSegment StartX=-49.19 StartY=2.75 StartZ=0 EndX=-1.5 EndY=2.75 EndZ=0
  constraints (120):
    c: Vertical(g0)
    c: Distance(g0) = 3
    c: Block(g0)
    c: Vertical(g1)
    c: Distance(g1) = 3
    c: Vertical(g2)
    c: Equal(g0,g2) = 3
    c: Block(g2)
    c: Vertical(g3)
    c: Equal(g1,g3) = 3
    c: Vertical(g4)
    c: Equal(g0,g4) = 3
    c: Block(g4)
    c: Vertical(g5)
    c: Equal(g1,g5) = 3
    c: Vertical(g6)
    c: Equal(g0,g6) = 3
    c: Block(g6)
    c: Vertical(g7)
    c: Equal(g1,g7) = 3
    c: Vertical(g8)
    c: Equal(g0,g8) = 3
    c: Block(g8)
    c: Vertical(g9)
    c: Equal(g1,g9) = 3
    c: Vertical(g10)
    c: Equal(g0,g10) = 3
    c: Block(g10)
    c: Vertical(g11)
    c: Equal(g1,g11) = 3
    c: Block(g12)
    c: Block(g13)
    c: Block(g14)
    c: Block(g15)
    c: Block(g16)
    c: Block(g17)
    c: Block(g18)
    c: Block(g19)
    c: Block(g20)
    c: Block(g21)
    c: Block(g22)
    c: Block(g23)
    c: Block(g11)
    c: Block(g9)
    c: Block(g7)
    c: Block(g5)
    c: Block(g3)
    c: Block(g1)
    c: Coincident(g24,g0)
    c: Coincident(g24,g12)
    c: Horizontal(g24)
    c: Coincident(g25,g0)
    c: Coincident(g25,g12)
    c: Horizontal(g25)
    c: Coincident(g26,g1)
    c: Coincident(g26,g13)
    c: Horizontal(g26)
    c: Coincident(g27,g1)
    c: Coincident(g27,g13)
    c: Horizontal(g27)
    c: Coincident(g28,g2)
    c: Coincident(g28,g14)
    c: Horizontal(g28)
    c: Coincident(g29,g2)
    c: Coincident(g29,g14)
    c: Horizontal(g29)
    c: Coincident(g30,g3)
    c: Coincident(g30,g15)
    c: Horizontal(g30)
    c: Coincident(g31,g3)
    c: Coincident(g31,g15)
    c: Horizontal(g31)
    c: Coincident(g32,g4)
    c: Coincident(g32,g16)
    c: Horizontal(g32)
    c: Coincident(g33,g4)
    c: Coincident(g33,g16)
    c: Horizontal(g33)
    c: Coincident(g34,g5)
    c: Coincident(g34,g17)
    c: Horizontal(g34)
    c: Coincident(g35,g5)
    c: Coincident(g35,g17)
    c: Horizontal(g35)
    c: Coincident(g36,g6)
    c: Coincident(g36,g19)
    c: Horizontal(g36)
    c: Coincident(g37,g6)
    c: Coincident(g37,g19)
    c: Horizontal(g37)
    c: Coincident(g38,g7)
    c: Coincident(g38,g18)
    c: Horizontal(g38)
    c: Coincident(g39,g7)
    c: Coincident(g39,g18)
    c: Horizontal(g39)
    c: Coincident(g40,g8)
    c: Coincident(g40,g20)
    c: Horizontal(g40)
    c: Coincident(g41,g8)
    c: Coincident(g41,g20)
    c: Horizontal(g41)
    c: Coincident(g42,g9)
    c: Coincident(g42,g23)
    c: Horizontal(g42)
    c: Coincident(g43,g9)
    c: Coincident(g43,g23)
    c: Horizontal(g43)
    c: Coincident(g44,g10)
    c: Coincident(g44,g22)
    c: Horizontal(g44)
    c: Coincident(g45,g10)
    c: Coincident(g45,g22)
    c: Horizontal(g45)
    c: Coincident(g46,g11)
    c: Coincident(g46,g21)
    c: Horizontal(g46)
    c: Coincident(g47,g11)
    c: Coincident(g47,g21)
    c: Horizontal(g47)
FEATURE [Part::Extrusion] Extrude042
  Base = -> Sketch051
  Dir = (1,-2e-16,2e-16)
  DirMode = 2
  FaceMakerClass = Part::FaceMakerBullseye
  LengthFwd = 19
  LengthRev = 0
  Placement = pos=(-19,0,0) rot=(0,0,1;0rad)
  Solid = true
  Symmetric = false
FEATURE [Part::Fillet] Fillet035  label="removeToCreateVentalationHoles"
  Base = -> Extrude042
  Edges = <same value as first occurrence — deduplicated (x6 in doc)>
  Placement = pos=(7,0,0) rot=(0,0,1;0rad)
FEATURE [Part::Cut] Cut038  label="top017"
  Base = -> Cut033
  Tool = -> Fillet035
FEATURE [Sketcher::SketchObject] Sketch052  label="bottomSketch001"
  FullyConstrained = true
  sketch-geometry (45):
    g0: LineSegment StartX=6.29999 StartY=8 StartZ=0 EndX=3.29999 EndY=8 EndZ=0
    g1: LineSegment StartX=3.29999 StartY=8 StartZ=0 EndX=3.29999 EndY=-6.03275e-07 EndZ=0
    g2: ArcOfCircle CenterX=8.29999 CenterY=5 CenterZ=0 NormalX=0 NormalY=0 NormalZ=1 AngleXU=0 Radius=2 StartAngle=3.14159 EndAngle=4.71239
    g3: LineSegment StartX=6.29999 StartY=8 StartZ=0 EndX=6.29999 EndY=5 EndZ=0
    g4: ArcOfCircle CenterX=105 CenterY=19 CenterZ=0 NormalX=0 NormalY=0 NormalZ=1 AngleXU=0 Radius=12.7 StartAngle=4.71239 EndAngle=5.94289
    g5-g11: Circle x7 (B-spline internal-alignment scaffolding for g12; pole/knot coordinates omitted)
    g12: BSplineCurve PolesCount=7 KnotsCount=5 Degree=3 IsPeriodic=0
    g13-g17: GeomPoint x5 (B-spline internal-alignment scaffolding for g12; pole/knot coordinates omitted)
    g18: ArcOfCircle CenterX=105 CenterY=19 CenterZ=0 NormalX=0 NormalY=0 NormalZ=1 AngleXU=0 Radius=15.7 StartAngle=5.81226 EndAngle=6.28319
    g19: BSplineCurve PolesCount=5 KnotsCount=3 Degree=3 IsPeriodic=0
    g20: LineSegment StartX=8.29999 StartY=3 StartZ=0 EndX=101.7 EndY=3 EndZ=0
    g21: LineSegment StartX=3.29999 StartY=-6.03275e-07 StartZ=0 EndX=105 EndY=-6.03275e-07 EndZ=0
    g22: LineSegment StartX=120.974 StartY=8.71251 StartZ=0 EndX=122.332 EndY=7.83778 EndZ=0
    g23: LineSegment StartX=105 StartY=-6.03274e-07 StartZ=0 EndX=113 EndY=-6.03274e-07 EndZ=0
    g24: ArcOfCircle CenterX=105 CenterY=19 CenterZ=0 NormalX=0 NormalY=0 NormalZ=1 AngleXU=0 Radius=20.6155 StartAngle=5.11091 EndAngle=5.71103
    g25: ArcOfCircle CenterX=117.7 CenterY=19 CenterZ=0 NormalX=0 NormalY=0 NormalZ=1 AngleXU=0 Radius=3 StartAngle=1.2e-15 EndAngle=2.10468
    g26: Circle CenterX=116.345 CenterY=16.3232 CenterZ=0 NormalX=0 NormalY=0 NormalZ=1 AngleXU=0 Radius=1
    g27: Circle CenterX=117.24 CenterY=15.7584 CenterZ=0 NormalX=0 NormalY=0 NormalZ=1 AngleXU=0 Radius=1
    g28: Circle CenterX=116.972 CenterY=14.7612 CenterZ=0 NormalX=0 NormalY=0 NormalZ=1 AngleXU=0 Radius=1
    g29: BSplineCurve PolesCount=3 KnotsCount=2 Degree=2 IsPeriodic=0
    g30: GeomPoint X=116.345 Y=16.3232 Z=0
    g31: GeomPoint X=116.972 Y=14.7612 Z=0
    g32: Circle CenterX=115.828 CenterY=17.157 CenterZ=0 NormalX=0 NormalY=0 NormalZ=1 AngleXU=0 Radius=1
    g33: Circle CenterX=115.841 CenterY=16.639 CenterZ=0 NormalX=0 NormalY=0 NormalZ=1 AngleXU=0 Radius=1
    g34: Circle CenterX=116.345 CenterY=16.3232 CenterZ=0 NormalX=0 NormalY=0 NormalZ=1 AngleXU=0 Radius=1
    g35: BSplineCurve PolesCount=3 KnotsCount=2 Degree=2 IsPeriodic=0
    g36: GeomPoint X=115.828 Y=17.157 Z=0
    g37: GeomPoint X=116.345 Y=16.3232 Z=0
    g38: LineSegment StartX=115.828 StartY=17.157 StartZ=0 EndX=115.828 EndY=20.8307 EndZ=0
    g39: Circle CenterX=115.828 CenterY=20.8307 CenterZ=0 NormalX=0 NormalY=0 NormalZ=1 AngleXU=0 Radius=1
    g40: Circle CenterX=115.831 CenterY=21.3396 CenterZ=0 NormalX=0 NormalY=0 NormalZ=1 AngleXU=0 Radius=1
    g41: Circle CenterX=116.173 CenterY=21.5825 CenterZ=0 NormalX=0 NormalY=0 NormalZ=1 AngleXU=0 Radius=1
    g42: BSplineCurve PolesCount=3 KnotsCount=2 Degree=2 IsPeriodic=0
    g43: GeomPoint X=115.828 Y=20.8307 Z=0
    g44: GeomPoint X=116.173 Y=21.5825 Z=0
  constraints (70):
    c: Horizontal(g0)
    c: Distance(g0) = 3
    c: Coincident(g1,g0)
    c: Vertical(g1)
    c: Block(g2)
    c: Block(g0)
    c: Coincident(g3,g0)
    c: Coincident(g3,g2)
    c: Vertical(g3)
    c: Block(g1)
    c: Block(g4)
    c: Coincident(g19,g4)
    c: Block(g19)
    c: Equal(g5, g6-g11) x6
    c: InternalAlignment(g5-g11 -> g12) x7
    c: InternalAlignment(g13-g17 -> g12) x5
    c: Block(g12)
    c: Coincident(g18,g12)
    c: Block(g18)
    c: Coincident(g20,g2)
    c: Coincident(g20,g19)
    c: Horizontal(g20)
    c: Distance(g20) = 93.4
    c: Coincident(g21,g1)
    c: Horizontal(g21)
    c: Distance(g21) = 101.7
    c: Horizontal(g23)
    c: Distance(g23) = 8
    c: Coincident(g24,g23)
    c: Block(g23)
    c: Coincident(g22,g24)
    c: Block(g24)
    c: Block(g22)
    c: Distance(g22) = 1.61553
    c: Coincident(g25,g18)
    c: Block(g25)
    c: Weight(g26) = 1
    c: Equal(g26,g27)
    c: Equal(g26,g28)
    c: Coincident(g29,g4)
    c: InternalAlignment(g26,g29)
    c: InternalAlignment(g27,g29)
    c: InternalAlignment(g28,g29)
    c: InternalAlignment(g30,g29)
    c: InternalAlignment(g31,g29)
    c: Block(g29)
    c: Weight(g32) = 1
    c: Equal(g32,g33)
    c: Equal(g32,g34)
    c: Coincident(g35,g29)
    c: InternalAlignment(g32,g35)
    c: InternalAlignment(g33,g35)
    c: InternalAlignment(g34,g35)
    c: InternalAlignment(g36,g35)
    c: InternalAlignment(g37,g35)
    c: Block(g35)
    c: Coincident(g38,g35)
    c: Vertical(g38)
    c: Block(g38)
    c: Coincident(g42,g38)
    c: Weight(g39) = 1
    c: Equal(g39,g40)
    c: Equal(g39,g41)
    c: Coincident(g42,g25)
    c: InternalAlignment(g39,g42)
    c: InternalAlignment(g40,g42)
    c: InternalAlignment(g41,g42)
    c: InternalAlignment(g43,g42)
    c: InternalAlignment(g44,g42)
    c: Block(g42)
FEATURE [Part::Extrusion] Extrude043  label="bottom010"
  Base = -> Sketch052
  Dir = (0,0,1)
  DirMode = 2
  FaceMakerClass = Part::FaceMakerBullseye
  LengthFwd = 71.4
  LengthRev = 0
  Placement = pos=(0,0,0.3) rot=(0,0,1;0rad)
  Solid = true
  Symmetric = false
FEATURE [Sketcher::SketchObject] Sketch053  label="topSketch013"
  FullyConstrained = true
  sketch-geometry (22):
    g0: LineSegment StartX=5.21097e-06 StartY=3 StartZ=0 EndX=5.21097e-06 EndY=19 EndZ=0
    g1: ArcOfCircle CenterX=19 CenterY=19 CenterZ=0 NormalX=0 NormalY=0 NormalZ=1 AngleXU=0 Radius=19 StartAngle=1.5708 EndAngle=3.14159
    g2: ArcOfCircle CenterX=19 CenterY=19 CenterZ=0 NormalX=0 NormalY=0 NormalZ=1 AngleXU=0 Radius=16 StartAngle=1.5708 EndAngle=3.14159
    g3: LineSegment StartX=114 StartY=35 StartZ=0 EndX=19 EndY=35 EndZ=0
    g4: LineSegment StartX=5.21097e-06 StartY=3 StartZ=0 EndX=5.21097e-06 EndY=0 EndZ=0
    g5: LineSegment StartX=3 StartY=0 StartZ=0 EndX=5.21097e-06 EndY=0 EndZ=0
    g6: LineSegment StartX=3 StartY=19 StartZ=0 EndX=3 EndY=0 EndZ=0
    g7: LineSegment StartX=19 StartY=38 StartZ=0 EndX=124 EndY=38 EndZ=0
    g8: Circle CenterX=119 CenterY=35 CenterZ=0 NormalX=0 NormalY=0 NormalZ=1 AngleXU=0 Radius=1
    g9: Circle CenterX=121 CenterY=35 CenterZ=0 NormalX=0 NormalY=0 NormalZ=1 AngleXU=0 Radius=1
    g10: Circle CenterX=121 CenterY=33 CenterZ=0 NormalX=0 NormalY=0 NormalZ=1 AngleXU=0 Radius=1
    g11: BSplineCurve PolesCount=3 KnotsCount=2 Degree=2 IsPeriodic=0
    g12: GeomPoint X=119 Y=35 Z=0
    g13: GeomPoint X=121 Y=33 Z=0
    g14: LineSegment StartX=119 StartY=35 StartZ=0 EndX=114 EndY=35 EndZ=0
    g15: ArcOfCircle CenterX=105 CenterY=19 CenterZ=0 NormalX=0 NormalY=0 NormalZ=1 AngleXU=0 Radius=16 StartAngle=5.60905 EndAngle=6.28319
    g16: LineSegment StartX=121 StartY=33 StartZ=0 EndX=121 EndY=19 EndZ=0
    g17: LineSegment StartX=117.5 StartY=9.01251 StartZ=0 EndX=121.163 EndY=9.0125 EndZ=0
    g18: ArcOfCircle CenterX=105 CenterY=19 CenterZ=0 NormalX=0 NormalY=0 NormalZ=1 AngleXU=0 Radius=20.6155 StartAngle=5.7297 EndAngle=6.28319
    g19: LineSegment StartX=121.163 StartY=9.0125 StartZ=0 EndX=122.538 EndY=8.16329 EndZ=0
    g20: LineSegment StartX=124 StartY=38 StartZ=0 EndX=125.616 EndY=38 EndZ=0
    g21: LineSegment StartX=125.616 StartY=19 StartZ=0 EndX=125.616 EndY=38 EndZ=0
  constraints (50):
    c: Vertical(g0)
    c: Block(g0)
    c: Coincident(g1,g0)
    c: Block(g1)
    c: Coincident(g2,g1)
    c: Block(g2)
    c: Coincident(g3,g2)
    c: Horizontal(g3)
    c: Tangent(g3,g2)
    c: Coincident(g4,g0)
    c: Distance(g4) = 3
    c: Vertical(g4)
    c: Coincident(g5,g4)
    c: Horizontal(g5)
    c: Coincident(g6,g2)
    c: Coincident(g6,g5)
    c: Vertical(g6)
    c: Horizontal(g7)
    c: Distance(g7) = 105
    c: Coincident(g7,g1)
    c: Block(g3)
    c: Weight(g8) = 1
    c: Equal(g8,g9)
    c: Equal(g8,g10)
    c: InternalAlignment(g8,g11)
    c: InternalAlignment(g9,g11)
    c: InternalAlignment(g10,g11)
    c: InternalAlignment(g12,g11)
    c: InternalAlignment(g13,g11)
    c: Block(g11)
    c: Coincident(g14,g11)
    c: Coincident(g14,g3)
    c: Horizontal(g14)
    c: Block(g15)
    c: Coincident(g16,g11)
    c: Coincident(g16,g15)
    c: Vertical(g16)
    c: Distance(g16) = 14
    c: Coincident(g17,g15)
    c: Block(g18)
    c: Coincident(g19,g18)
    c: Coincident(g20,g7)
    c: Horizontal(g20)
    c: Vertical(g21)
    c: Coincident(g20,g21)
    c: Block(g20)
    c: Block(g21)
    c: Block(g19)
    c: Block(g17)
    c: Distance(g20) = 1.61553
FEATURE [Part::Extrusion] Extrude044
  Base = -> Sketch053
  Dir = (0,0,1)
  DirMode = 2
  FaceMakerClass = Part::FaceMakerBullseye
  LengthFwd = 72
  LengthRev = 0
  Solid = true
  Symmetric = false
FEATURE [Part::Fillet] Fillet036  label="top018"
  Base = -> Extrude044
  Edges = 1 edges r=2: [Edge41]
FEATURE [Sketcher::SketchObject] Sketch054
  FullyConstrained = false
  Placement = pos=(0,0,0) rot=(1,0,0;1.5708rad)
  sketch-geometry (24):
    g0: ArcOfCircle CenterX=-4 CenterY=-10.5 CenterZ=0 NormalX=0 NormalY=0 NormalZ=1 AngleXU=0 Radius=1.5 StartAngle=6e-16 EndAngle=3.14159
    g1: ArcOfCircle CenterX=-34.2 CenterY=-10.5 CenterZ=0 NormalX=0 NormalY=0 NormalZ=1 AngleXU=0 Radius=1.5 StartAngle=0 EndAngle=3.14159
    g2: ArcOfCircle CenterX=-34.2 CenterY=-27.7 CenterZ=0 NormalX=0 NormalY=0 NormalZ=1 AngleXU=0 Radius=1.5 StartAngle=3.14159 EndAngle=6.28319
    g3: ArcOfCircle CenterX=-4 CenterY=-27.7 CenterZ=0 NormalX=0 NormalY=0 NormalZ=1 AngleXU=0 Radius=1.5 StartAngle=3.1416 EndAngle=6.28319
    g4: ArcOfCircle CenterX=-10 CenterY=-4.3 CenterZ=0 NormalX=0 NormalY=0 NormalZ=1 AngleXU=0 Radius=1.5 StartAngle=2e-16 EndAngle=3.14159
    g5: ArcOfCircle CenterX=-16.1 CenterY=-1.8 CenterZ=0 NormalX=0 NormalY=0 NormalZ=1 AngleXU=0 Radius=1.5 StartAngle=5e-16 EndAngle=3.14159
    g6: ArcOfCircle CenterX=-22.1 CenterY=-1.8 CenterZ=0 NormalX=0 NormalY=0 NormalZ=1 AngleXU=0 Radius=1.5 StartAngle=5e-16 EndAngle=3.14159
    g7: ArcOfCircle CenterX=-28.2 CenterY=-4.3 CenterZ=0 NormalX=0 NormalY=0 NormalZ=1 AngleXU=0 Radius=1.5 StartAngle=2e-16 EndAngle=3.14159
    g8: ArcOfCircle CenterX=-10 CenterY=-33.9 CenterZ=0 NormalX=0 NormalY=0 NormalZ=1 AngleXU=0 Radius=1.5 StartAngle=3.14159 EndAngle=6.28319
    g9: ArcOfCircle CenterX=-16.1 CenterY=-36.4 CenterZ=0 NormalX=0 NormalY=0 NormalZ=1 AngleXU=0 Radius=1.5 StartAngle=3.14159 EndAngle=6.28319
    g10: ArcOfCircle CenterX=-22.1 CenterY=-36.4 CenterZ=0 NormalX=0 NormalY=0 NormalZ=1 AngleXU=0 Radius=1.5 StartAngle=3.14159 EndAngle=6.28319
    g11: ArcOfCircle CenterX=-28.2 CenterY=-33.9 CenterZ=0 NormalX=0 NormalY=0 NormalZ=1 AngleXU=0 Radius=1.5 StartAngle=3.14159 EndAngle=6.28319
    g12: LineSegment StartX=-35.7 StartY=-10.5 StartZ=0 EndX=-35.7 EndY=-27.7 EndZ=0
    g13: LineSegment StartX=-32.7 StartY=-10.5 StartZ=0 EndX=-32.7 EndY=-27.7 EndZ=0
    g14: LineSegment StartX=-29.7 StartY=-33.9 StartZ=0 EndX=-29.7 EndY=-4.3 EndZ=0
    g15: LineSegment StartX=-26.7 StartY=-33.9 StartZ=0 EndX=-26.7 EndY=-4.3 EndZ=0
    g16: LineSegment StartX=-2.5 StartY=-10.5 StartZ=0 EndX=-2.5 EndY=-27.7 EndZ=0
    g17: LineSegment StartX=-8.5 StartY=-4.3 StartZ=0 EndX=-8.5 EndY=-33.9 EndZ=0
    g18: LineSegment StartX=-5.5 StartY=-10.5 StartZ=0 EndX=-5.5 EndY=-27.7 EndZ=0
    g19: LineSegment StartX=-11.5 StartY=-4.3 StartZ=0 EndX=-11.5 EndY=-33.9 EndZ=0
    g20: LineSegment StartX=-14.6 StartY=-1.8 StartZ=0 EndX=-14.6 EndY=-36.4 EndZ=0
    g21: LineSegment StartX=-17.6 StartY=-1.8 StartZ=0 EndX=-17.6 EndY=-36.4 EndZ=0
    g22: LineSegment StartX=-20.6 StartY=-36.4 StartZ=0 EndX=-20.6 EndY=-1.8 EndZ=0
    g23: LineSegment StartX=-23.6 StartY=-1.8 StartZ=0 EndX=-23.6 EndY=-36.4 EndZ=0
  constraints (48):
    c: Block(g0)
    c: Block(g1)
    c: Block(g2)
    c: Block(g3)
    c: Block(g4)
    c: Block(g5)
    c: Block(g6)
    c: Block(g7)
    c: Block(g8)
    c: Block(g9)
    c: Block(g10)
    c: Block(g11)
    c: Coincident(g12,g1)
    c: Coincident(g12,g2)
    c: Vertical(g12)
    c: Coincident(g13,g1)
    c: Coincident(g13,g2)
    c: Vertical(g13)
    c: Coincident(g14,g11)
    c: Coincident(g14,g7)
    c: Vertical(g14)
    c: Coincident(g15,g11)
    c: Coincident(g15,g7)
    c: Vertical(g15)
    c: Coincident(g16,g0)
    c: Coincident(g16,g3)
    c: Vertical(g16)
    c: Coincident(g17,g4)
    c: Coincident(g17,g8)
    c: Vertical(g17)
    c: Coincident(g18,g0)
    c: Coincident(g18,g3)
    c: Vertical(g18)
    c: Coincident(g19,g4)
    c: Coincident(g19,g8)
    c: Vertical(g19)
    c: Coincident(g20,g5)
    c: Coincident(g20,g9)
    c: Vertical(g20)
    c: Coincident(g21,g5)
    c: Coincident(g21,g9)
    c: Vertical(g21)
    c: Coincident(g22,g10)
    c: Coincident(g22,g6)
    c: Vertical(g22)
    c: Coincident(g23,g6)
    c: Coincident(g23,g10)
    c: Vertical(g23)
FEATURE [Part::Extrusion] Extrude045  label="removeToCreateFanGrillHoles003"
  Base = -> Sketch054
  Dir = (0,-1,6e-16)
  DirMode = 2
  FaceMakerClass = Part::FaceMakerBullseye
  LengthFwd = 10
  LengthRev = 0
  Placement = pos=(65.4,44,54.82) rot=(0,0,1;0rad)
  Solid = true
  Symmetric = false
FEATURE [Part::Feature] Face105 .. Face108  x4 (patterned run collapsed; names and placements below)
  shape: bbox 3.5 x 17.8 x 2e-07 mm, 1 faces, 0 solids (baked)
FEATURE [Part::Revolution] Revolve113  label="removeToCreateScrewAndThreadedInsertHole041"
  Angle = 360
  Axis = (0,1,0)
  Base = (0,0,0)
  FaceMakerClass = Part::FaceMakerBullseye
  Placement = pos=(62.3,30.3,19.7) rot=(0,0,1;0rad)
  Solid = false
  Source = -> Face105
  Symmetric = false
FEATURE [Part::Revolution] Revolve114  label="removeToCreateScrewAndThreadedInsertHole042"
  Angle = 360
  Axis = (0,1,0)
  Base = (0,0,0)
  FaceMakerClass = Part::FaceMakerBullseye
  Placement = pos=(62.3,30.3,51.7) rot=(0,0,1;0rad)
  Solid = false
  Source = -> Face106
  Symmetric = false
FEATURE [Part::Revolution] Revolve115  label="removeToCreateScrewAndThreadedInsertHole043"
  Angle = 360
  Axis = (0,1,0)
  Base = (0,0,0)
  FaceMakerClass = Part::FaceMakerBullseye
  Placement = pos=(30.3,30.3,19.7) rot=(0,0,1;0rad)
  Solid = false
  Source = -> Face107
  Symmetric = false
FEATURE [Part::Revolution] Revolve116  label="removeToCreateScrewAndThreadedInsertHole044"
  Angle = 360
  Axis = (0,1,0)
  Base = (0,0,0)
  FaceMakerClass = Part::FaceMakerBullseye
  Placement = pos=(30.3,30.3,51.7) rot=(0,0,1;0rad)
  Solid = false
  Source = -> Face108
  Symmetric = false
FEATURE [Part::MultiFuse] Fusion083  label="createThreadedInsertHolesForFan004"
  Shapes = -> [Revolve113,Revolve114,Revolve115,Revolve116]
FEATURE [Part::Box] Box024  label="removeToCreteHoleForPlugHousing026"
  AttacherType = Attacher::AttachEngine3D
  Height = 28.6
  Length = 10
  Placement = pos=(-2,0,21.7) rot=(0,0,1;0rad)
  Width = 19
FEATURE [Part::Cylinder] Cylinder038  label="removeToCreteHoleForPlugHousing027"
  Angle = 360
  AttacherType = Attacher::AttachEngine3D
  Height = 20
  Placement = pos=(-2,19,36) rot=(0,1,0;1.5708rad)
  Radius = 14.3
FEATURE [Part::MultiFuse] Fusion084  label="removeToCreteHoleForPlugHousing028"
  Shapes = -> [Box024,Cylinder038]
FEATURE [Part::Cylinder] Cylinder039
  Angle = 360
  AttacherType = Attacher::AttachEngine3D
  Height = 20
  Placement = pos=(0,0,36.15) rot=(0,0,1;0rad)
  Radius = 14.3
FEATURE [Part::Cylinder] Cylinder040
  Angle = 360
  AttacherType = Attacher::AttachEngine3D
  Height = 10
  Placement = pos=(0,0,36.15) rot=(0,0,1;0rad)
  Radius = 4
FEATURE [Part::Box] Box025  label="removeToCreteHoleForPlugHousing030"
  AttacherType = Attacher::AttachEngine3D
  Height = 28.6
  Length = 20
  Placement = pos=(106.15,0,21.7) rot=(0,0,1;0rad)
  Width = 19
FEATURE [Part::MultiFuse] Fusion086  label="removeToCreteHoleForPlugHousing031"
  Placement = pos=(70,19,36) rot=(0,1,0;1.5708rad)
  Shapes = -> [Cylinder039,Cylinder040]
FEATURE [Part::MultiFuse] Fusion085  label="removeToCreteHoleForPlugHousing029"
  Shapes = -> [Box025,Fusion086]
FEATURE [Sketcher::SketchObject] Sketch055
  FullyConstrained = true
  Placement = pos=(117,19,0) rot=(0.57735,0.57735,0.57735;2.0944rad)
  sketch-geometry (48):
    g0: LineSegment StartX=-49.19 StartY=69.25 StartZ=0 EndX=-49.19 EndY=66.25 EndZ=0
    g1: LineSegment StartX=-49.19 StartY=63.5 StartZ=0 EndX=-49.19 EndY=60.5 EndZ=0
    g2: LineSegment StartX=-49.19 StartY=57.75 StartZ=0 EndX=-49.19 EndY=54.75 EndZ=0
    g3: LineSegment StartX=-49.19 StartY=52 StartZ=0 EndX=-49.19 EndY=49 EndZ=0
    g4: LineSegment StartX=-49.19 StartY=46.25 StartZ=0 EndX=-49.19 EndY=43.25 EndZ=0
    g5: LineSegment StartX=-49.19 StartY=40.5 StartZ=0 EndX=-49.19 EndY=37.5 EndZ=0
    g6: LineSegment StartX=-49.19 StartY=34.5 StartZ=0 EndX=-49.19 EndY=31.5 EndZ=0
    g7: LineSegment StartX=-49.19 StartY=28.75 StartZ=0 EndX=-49.19 EndY=25.75 EndZ=0
    g8: LineSegment StartX=-49.19 StartY=23 StartZ=0 EndX=-49.19 EndY=20 EndZ=0
    g9: LineSegment StartX=-49.19 StartY=17.25 StartZ=0 EndX=-49.19 EndY=14.25 EndZ=0
    g10: LineSegment StartX=-49.19 StartY=11.5 StartZ=0 EndX=-49.19 EndY=8.5 EndZ=0
    g11: LineSegment StartX=-49.19 StartY=5.75 StartZ=0 EndX=-49.19 EndY=2.75 EndZ=0
    g12: ArcOfCircle CenterX=-1.5 CenterY=67.75 CenterZ=0 NormalX=0 NormalY=0 NormalZ=1 AngleXU=0 Radius=1.5 StartAngle=4.71239 EndAngle=7.85398
    g13: ArcOfCircle CenterX=-1.5 CenterY=62 CenterZ=0 NormalX=0 NormalY=0 NormalZ=1 AngleXU=0 Radius=1.5 StartAngle=4.71239 EndAngle=7.85398
    g14: ArcOfCircle CenterX=-1.5 CenterY=56.25 CenterZ=0 NormalX=0 NormalY=0 NormalZ=1 AngleXU=0 Radius=1.5 StartAngle=4.71239 EndAngle=7.85398
    g15: ArcOfCircle CenterX=-11.49 CenterY=50.5 CenterZ=0 NormalX=0 NormalY=0 NormalZ=1 AngleXU=0 Radius=1.5 StartAngle=4.71239 EndAngle=7.85398
    g16: ArcOfCircle CenterX=-16.28 CenterY=44.75 CenterZ=0 NormalX=0 NormalY=0 NormalZ=1 AngleXU=0 Radius=1.5 StartAngle=4.71239 EndAngle=7.85398
    g17: ArcOfCircle CenterX=-18.2337 CenterY=39 CenterZ=0 NormalX=0 NormalY=0 NormalZ=1 AngleXU=0 Radius=1.5 StartAngle=4.71485 EndAngle=7.85398
    g18: ArcOfCircle CenterX=-16.2837 CenterY=27.25 CenterZ=0 NormalX=0 NormalY=0 NormalZ=1 AngleXU=0 Radius=1.5 StartAngle=4.71485 EndAngle=7.85398
    g19: ArcOfCircle CenterX=-18.2337 CenterY=33 CenterZ=0 NormalX=0 NormalY=0 NormalZ=1 AngleXU=0 Radius=1.5 StartAngle=4.71485 EndAngle=7.85398
    g20: ArcOfCircle CenterX=-11.49 CenterY=21.5 CenterZ=0 NormalX=0 NormalY=0 NormalZ=1 AngleXU=0 Radius=1.5 StartAngle=4.71239 EndAngle=7.85398
    g21: ArcOfCircle CenterX=-1.5 CenterY=4.25 CenterZ=0 NormalX=0 NormalY=0 NormalZ=1 AngleXU=0 Radius=1.5 StartAngle=4.71239 EndAngle=7.85398
    g22: ArcOfCircle CenterX=-1.5 CenterY=10 CenterZ=0 NormalX=0 NormalY=0 NormalZ=1 AngleXU=0 Radius=1.5 StartAngle=4.71239 EndAngle=7.85398
    g23: ArcOfCircle CenterX=-1.5 CenterY=15.75 CenterZ=0 NormalX=0 NormalY=0 NormalZ=1 AngleXU=0 Radius=1.5 StartAngle=4.71239 EndAngle=7.85398
    g24: LineSegment StartX=-49.19 StartY=69.25 StartZ=0 EndX=-1.5 EndY=69.25 EndZ=0
    g25: LineSegment StartX=-49.19 StartY=66.25 StartZ=0 EndX=-1.5 EndY=66.25 EndZ=0
    g26: LineSegment StartX=-49.19 StartY=63.5 StartZ=0 EndX=-1.5 EndY=63.5 EndZ=0
    g27: LineSegment StartX=-49.19 StartY=60.5 StartZ=0 EndX=-1.5 EndY=60.5 EndZ=0
    g28: LineSegment StartX=-49.19 StartY=57.75 StartZ=0 EndX=-1.5 EndY=57.75 EndZ=0
    g29: LineSegment StartX=-49.19 StartY=54.75 StartZ=0 EndX=-1.5 EndY=54.75 EndZ=0
    g30: LineSegment StartX=-49.19 StartY=52 StartZ=0 EndX=-11.49 EndY=52 EndZ=0
    g31: LineSegment StartX=-49.19 StartY=49 StartZ=0 EndX=-11.49 EndY=49 EndZ=0
    g32: LineSegment StartX=-49.19 StartY=46.25 StartZ=0 EndX=-16.28 EndY=46.25 EndZ=0
    g33: LineSegment StartX=-49.19 StartY=43.25 StartZ=0 EndX=-16.28 EndY=43.25 EndZ=0
    g34: LineSegment StartX=-49.19 StartY=40.5 StartZ=0 EndX=-18.2337 EndY=40.5 EndZ=0
    g35: LineSegment StartX=-49.19 StartY=37.5 StartZ=0 EndX=-18.23 EndY=37.5 EndZ=0
    g36: LineSegment StartX=-49.19 StartY=34.5 StartZ=0 EndX=-18.2337 EndY=34.5 EndZ=0
    g37: LineSegment StartX=-49.19 StartY=31.5 StartZ=0 EndX=-18.23 EndY=31.5 EndZ=0
    g38: LineSegment StartX=-49.19 StartY=28.75 StartZ=0 EndX=-16.2837 EndY=28.75 EndZ=0
    g39: LineSegment StartX=-49.19 StartY=25.75 StartZ=0 EndX=-16.28 EndY=25.75 EndZ=0
    g40: LineSegment StartX=-49.19 StartY=23 StartZ=0 EndX=-11.49 EndY=23 EndZ=0
    g41: LineSegment StartX=-49.19 StartY=20 StartZ=0 EndX=-11.49 EndY=20 EndZ=0
    g42: LineSegment StartX=-49.19 StartY=17.25 StartZ=0 EndX=-1.5 EndY=17.25 EndZ=0
    g43: LineSegment StartX=-49.19 StartY=14.25 StartZ=0 EndX=-1.5 EndY=14.25 EndZ=0
    g44: LineSegment StartX=-49.19 StartY=11.5 StartZ=0 EndX=-1.5 EndY=11.5 EndZ=0
    g45: LineSegment StartX=-49.19 StartY=8.5 StartZ=0 EndX=-1.5 EndY=8.5 EndZ=0
    g46: LineSegment StartX=-49.19 StartY=5.75 StartZ=0 EndX=-1.5 EndY=5.75 EndZ=0
    g47: LineSegment StartX=-49.19 StartY=2.75 StartZ=0 EndX=-1.5 EndY=2.75 EndZ=0
  constraints (120):
    c: Vertical(g0)
    c: Distance(g0) = 3
    c: Block(g0)
    c: Vertical(g1)
    c: Distance(g1) = 3
    c: Vertical(g2)
    c: Equal(g0,g2) = 3
    c: Block(g2)
    c: Vertical(g3)
    c: Equal(g1,g3) = 3
    c: Vertical(g4)
    c: Equal(g0,g4) = 3
    c: Block(g4)
    c: Vertical(g5)
    c: Equal(g1,g5) = 3
    c: Vertical(g6)
    c: Equal(g0,g6) = 3
    c: Block(g6)
    c: Vertical(g7)
    c: Equal(g1,g7) = 3
    c: Vertical(g8)
    c: Equal(g0,g8) = 3
    c: Block(g8)
    c: Vertical(g9)
    c: Equal(g1,g9) = 3
    c: Vertical(g10)
    c: Equal(g0,g10) = 3
    c: Block(g10)
    c: Vertical(g11)
    c: Equal(g1,g11) = 3
    c: Block(g12)
    c: Block(g13)
    c: Block(g14)
    c: Block(g15)
    c: Block(g16)
    c: Block(g17)
    c: Block(g18)
    c: Block(g19)
    c: Block(g20)
    c: Block(g21)
    c: Block(g22)
    c: Block(g23)
    c: Block(g11)
    c: Block(g9)
    c: Block(g7)
    c: Block(g5)
    c: Block(g3)
    c: Block(g1)
    c: Coincident(g24,g0)
    c: Coincident(g24,g12)
    c: Horizontal(g24)
    c: Coincident(g25,g0)
    c: Coincident(g25,g12)
    c: Horizontal(g25)
    c: Coincident(g26,g1)
    c: Coincident(g26,g13)
    c: Horizontal(g26)
    c: Coincident(g27,g1)
    c: Coincident(g27,g13)
    c: Horizontal(g27)
    c: Coincident(g28,g2)
    c: Coincident(g28,g14)
    c: Horizontal(g28)
    c: Coincident(g29,g2)
    c: Coincident(g29,g14)
    c: Horizontal(g29)
    c: Coincident(g30,g3)
    c: Coincident(g30,g15)
    c: Horizontal(g30)
    c: Coincident(g31,g3)
    c: Coincident(g31,g15)
    c: Horizontal(g31)
    c: Coincident(g32,g4)
    c: Coincident(g32,g16)
    c: Horizontal(g32)
    c: Coincident(g33,g4)
    c: Coincident(g33,g16)
    c: Horizontal(g33)
    c: Coincident(g34,g5)
    c: Coincident(g34,g17)
    c: Horizontal(g34)
    c: Coincident(g35,g5)
    c: Coincident(g35,g17)
    c: Horizontal(g35)
    c: Coincident(g36,g6)
    c: Coincident(g36,g19)
    c: Horizontal(g36)
    c: Coincident(g37,g6)
    c: Coincident(g37,g19)
    c: Horizontal(g37)
    c: Coincident(g38,g7)
    c: Coincident(g38,g18)
    c: Horizontal(g38)
    c: Coincident(g39,g7)
    c: Coincident(g39,g18)
    c: Horizontal(g39)
    c: Coincident(g40,g8)
    c: Coincident(g40,g20)
    c: Horizontal(g40)
    c: Coincident(g41,g8)
    c: Coincident(g41,g20)
    c: Horizontal(g41)
    c: Coincident(g42,g9)
    c: Coincident(g42,g23)
    c: Horizontal(g42)
    c: Coincident(g43,g9)
    c: Coincident(g43,g23)
    c: Horizontal(g43)
    c: Coincident(g44,g10)
    c: Coincident(g44,g22)
    c: Horizontal(g44)
    c: Coincident(g45,g10)
    c: Coincident(g45,g22)
    c: Horizontal(g45)
    c: Coincident(g46,g11)
    c: Coincident(g46,g21)
    c: Horizontal(g46)
    c: Coincident(g47,g11)
    c: Coincident(g47,g21)
    c: Horizontal(g47)
FEATURE [Part::Extrusion] Extrude046
  Base = -> Sketch055
  Dir = (1,0,0)
  DirMode = 2
  FaceMakerClass = Part::FaceMakerBullseye
  LengthFwd = 23
  LengthRev = 0
  Placement = pos=(-19,0,0) rot=(0,0,1;0rad)
  Solid = true
  Symmetric = false
FEATURE [Part::Fillet] Fillet038  label="removeToCreateVentalationHoles001"
  Base = -> Extrude046
  Edges = <same value as first occurrence — deduplicated (x6 in doc)>
  Placement = pos=(7,0,0) rot=(0,0,1;0rad)
FEATURE [Sketcher::SketchObject] Sketch056  label="topSketch014"
  FullyConstrained = true
  sketch-geometry (22):
    g0: LineSegment StartX=5.21097e-06 StartY=3 StartZ=0 EndX=5.21097e-06 EndY=19 EndZ=0
    g1: ArcOfCircle CenterX=19 CenterY=19 CenterZ=0 NormalX=0 NormalY=0 NormalZ=1 AngleXU=0 Radius=19 StartAngle=1.5708 EndAngle=3.14159
    g2: ArcOfCircle CenterX=19 CenterY=19 CenterZ=0 NormalX=0 NormalY=0 NormalZ=1 AngleXU=0 Radius=16 StartAngle=1.5708 EndAngle=3.14159
    g3: LineSegment StartX=114 StartY=35 StartZ=0 EndX=19 EndY=35 EndZ=0
    g4: LineSegment StartX=5.21097e-06 StartY=3 StartZ=0 EndX=5.21097e-06 EndY=0 EndZ=0
    g5: LineSegment StartX=3 StartY=0 StartZ=0 EndX=5.21097e-06 EndY=0 EndZ=0
    g6: LineSegment StartX=3 StartY=19 StartZ=0 EndX=3 EndY=0 EndZ=0
    g7: LineSegment StartX=19 StartY=38 StartZ=0 EndX=124 EndY=38 EndZ=0
    g8: Circle CenterX=119 CenterY=35 CenterZ=0 NormalX=0 NormalY=0 NormalZ=1 AngleXU=0 Radius=1
    g9: Circle CenterX=121 CenterY=35 CenterZ=0 NormalX=0 NormalY=0 NormalZ=1 AngleXU=0 Radius=1
    g10: Circle CenterX=121 CenterY=33 CenterZ=0 NormalX=0 NormalY=0 NormalZ=1 AngleXU=0 Radius=1
    g11: BSplineCurve PolesCount=3 KnotsCount=2 Degree=2 IsPeriodic=0
    g12: GeomPoint X=119 Y=35 Z=0
    g13: GeomPoint X=121 Y=33 Z=0
    g14: LineSegment StartX=119 StartY=35 StartZ=0 EndX=114 EndY=35 EndZ=0
    g15: ArcOfCircle CenterX=105 CenterY=19 CenterZ=0 NormalX=0 NormalY=0 NormalZ=1 AngleXU=0 Radius=16 StartAngle=5.60905 EndAngle=6.28319
    g16: LineSegment StartX=121 StartY=33 StartZ=0 EndX=121 EndY=19 EndZ=0
    g17: LineSegment StartX=117.5 StartY=9.01251 StartZ=0 EndX=121.163 EndY=9.0125 EndZ=0
    g18: ArcOfCircle CenterX=105 CenterY=19 CenterZ=0 NormalX=0 NormalY=0 NormalZ=1 AngleXU=0 Radius=20.6155 StartAngle=5.7297 EndAngle=6.28319
    g19: LineSegment StartX=121.163 StartY=9.0125 StartZ=0 EndX=122.538 EndY=8.16329 EndZ=0
    g20: LineSegment StartX=124 StartY=38 StartZ=0 EndX=125.616 EndY=38 EndZ=0
    g21: LineSegment StartX=125.616 StartY=19 StartZ=0 EndX=125.616 EndY=38 EndZ=0
  constraints (49):
    c: Vertical(g0)
    c: Block(g0)
    c: Coincident(g1,g0)
    c: Block(g1)
    c: Coincident(g2,g1)
    c: Block(g2)
    c: Coincident(g3,g2)
    c: Horizontal(g3)
    c: Tangent(g3,g2)
    c: Coincident(g4,g0)
    c: Distance(g4) = 3
    c: Vertical(g4)
    c: Coincident(g5,g4)
    c: Horizontal(g5)
    c: Coincident(g6,g2)
    c: Coincident(g6,g5)
    c: Vertical(g6)
    c: Horizontal(g7)
    c: Distance(g7) = 105
    c: Coincident(g7,g1)
    c: Block(g3)
    c: Weight(g8) = 1
    c: Equal(g8,g9)
    c: Equal(g8,g10)
    c: InternalAlignment(g8,g11)
    c: InternalAlignment(g9,g11)
    c: InternalAlignment(g10,g11)
    c: InternalAlignment(g12,g11)
    c: InternalAlignment(g13,g11)
    c: Block(g11)
    c: Coincident(g14,g11)
    c: Coincident(g14,g3)
    c: Horizontal(g14)
    c: Block(g15)
    c: Coincident(g16,g11)
    c: Coincident(g16,g15)
    c: Vertical(g16)
    c: Distance(g16) = 14
    c: Coincident(g17,g15)
    c: Block(g18)
    c: Coincident(g19,g18)
    c: Coincident(g20,g7)
    c: Horizontal(g20)
    c: Vertical(g21)
    c: Coincident(g20,g21)
    c: Block(g20)
    c: Block(g21)
    c: Block(g19)
    c: Block(g17)
FEATURE [Part::Box] Box026  label="removeToCreteHoleForPlugHousing032"
  AttacherType = Attacher::AttachEngine3D
  Height = 28.6
  Length = 10
  Placement = pos=(-2,0,21.7) rot=(0,0,1;0rad)
  Width = 19
FEATURE [Part::Feature] Face109 .. Face112  x4 (patterned run collapsed; names and placements below)
  shape: bbox 3.5 x 17.8 x 2e-07 mm, 1 faces, 0 solids (baked)
FEATURE [Part::Revolution] Revolve117  label="removeToCreateScrewAndThreadedInsertHole045"
  Angle = 360
  Axis = (0,1,0)
  Base = (0,0,0)
  FaceMakerClass = Part::FaceMakerBullseye
  Placement = pos=(62.3,30.3,19.7) rot=(0,0,1;0rad)
  Solid = false
  Source = -> Face109
  Symmetric = false
FEATURE [Part::Revolution] Revolve118  label="removeToCreateScrewAndThreadedInsertHole046"
  Angle = 360
  Axis = (0,1,0)
  Base = (0,0,0)
  FaceMakerClass = Part::FaceMakerBullseye
  Placement = pos=(62.3,30.3,51.7) rot=(0,0,1;0rad)
  Solid = false
  Source = -> Face110
  Symmetric = false
FEATURE [Part::Revolution] Revolve119  label="removeToCreateScrewAndThreadedInsertHole047"
  Angle = 360
  Axis = (0,1,0)
  Base = (0,0,0)
  FaceMakerClass = Part::FaceMakerBullseye
  Placement = pos=(30.3,30.3,19.7) rot=(0,0,1;0rad)
  Solid = false
  Source = -> Face111
  Symmetric = false
FEATURE [Part::Revolution] Revolve120  label="removeToCreateScrewAndThreadedInsertHole048"
  Angle = 360
  Axis = (0,1,0)
  Base = (0,0,0)
  FaceMakerClass = Part::FaceMakerBullseye
  Placement = pos=(30.3,30.3,51.7) rot=(0,0,1;0rad)
  Solid = false
  Source = -> Face112
  Symmetric = false
FEATURE [Part::MultiFuse] Fusion087  label="createThreadedInsertHolesForFan005"
  Shapes = -> [Revolve117,Revolve118,Revolve119,Revolve120]
FEATURE [Part::Extrusion] Extrude047
  Base = -> Sketch056
  Dir = (0,0,1)
  DirMode = 2
  FaceMakerClass = Part::FaceMakerBullseye
  LengthFwd = 72
  LengthRev = 0
  Solid = true
  Symmetric = false
FEATURE [Part::Fillet] Fillet039  label="top019"
  Base = -> Extrude047
  Edges = 1 edges r=2: [Edge35]
FEATURE [Sketcher::SketchObject] Sketch057
  FullyConstrained = false
  Placement = pos=(0,0,0) rot=(1,0,0;1.5708rad)
  sketch-geometry (24):
    g0: ArcOfCircle CenterX=-4 CenterY=-10.5 CenterZ=0 NormalX=0 NormalY=0 NormalZ=1 AngleXU=0 Radius=1.5 StartAngle=6e-16 EndAngle=3.14159
    g1: ArcOfCircle CenterX=-34.2 CenterY=-10.5 CenterZ=0 NormalX=0 NormalY=0 NormalZ=1 AngleXU=0 Radius=1.5 StartAngle=0 EndAngle=3.14159
    g2: ArcOfCircle CenterX=-34.2 CenterY=-27.7 CenterZ=0 NormalX=0 NormalY=0 NormalZ=1 AngleXU=0 Radius=1.5 StartAngle=3.14159 EndAngle=6.28319
    g3: ArcOfCircle CenterX=-4 CenterY=-27.7 CenterZ=0 NormalX=0 NormalY=0 NormalZ=1 AngleXU=0 Radius=1.5 StartAngle=3.1416 EndAngle=6.28319
    g4: ArcOfCircle CenterX=-10 CenterY=-4.3 CenterZ=0 NormalX=0 NormalY=0 NormalZ=1 AngleXU=0 Radius=1.5 StartAngle=2e-16 EndAngle=3.14159
    g5: ArcOfCircle CenterX=-16.1 CenterY=-1.8 CenterZ=0 NormalX=0 NormalY=0 NormalZ=1 AngleXU=0 Radius=1.5 StartAngle=5e-16 EndAngle=3.14159
    g6: ArcOfCircle CenterX=-22.1 CenterY=-1.8 CenterZ=0 NormalX=0 NormalY=0 NormalZ=1 AngleXU=0 Radius=1.5 StartAngle=5e-16 EndAngle=3.14159
    g7: ArcOfCircle CenterX=-28.2 CenterY=-4.3 CenterZ=0 NormalX=0 NormalY=0 NormalZ=1 AngleXU=0 Radius=1.5 StartAngle=2e-16 EndAngle=3.14159
    g8: ArcOfCircle CenterX=-10 CenterY=-33.9 CenterZ=0 NormalX=0 NormalY=0 NormalZ=1 AngleXU=0 Radius=1.5 StartAngle=3.14159 EndAngle=6.28319
    g9: ArcOfCircle CenterX=-16.1 CenterY=-36.4 CenterZ=0 NormalX=0 NormalY=0 NormalZ=1 AngleXU=0 Radius=1.5 StartAngle=3.14159 EndAngle=6.28319
    g10: ArcOfCircle CenterX=-22.1 CenterY=-36.4 CenterZ=0 NormalX=0 NormalY=0 NormalZ=1 AngleXU=0 Radius=1.5 StartAngle=3.14159 EndAngle=6.28319
    g11: ArcOfCircle CenterX=-28.2 CenterY=-33.9 CenterZ=0 NormalX=0 NormalY=0 NormalZ=1 AngleXU=0 Radius=1.5 StartAngle=3.14159 EndAngle=6.28319
    g12: LineSegment StartX=-35.7 StartY=-10.5 StartZ=0 EndX=-35.7 EndY=-27.7 EndZ=0
    g13: LineSegment StartX=-32.7 StartY=-10.5 StartZ=0 EndX=-32.7 EndY=-27.7 EndZ=0
    g14: LineSegment StartX=-29.7 StartY=-33.9 StartZ=0 EndX=-29.7 EndY=-4.3 EndZ=0
    g15: LineSegment StartX=-26.7 StartY=-33.9 StartZ=0 EndX=-26.7 EndY=-4.3 EndZ=0
    g16: LineSegment StartX=-2.5 StartY=-10.5 StartZ=0 EndX=-2.5 EndY=-27.7 EndZ=0
    g17: LineSegment StartX=-8.5 StartY=-4.3 StartZ=0 EndX=-8.5 EndY=-33.9 EndZ=0
    g18: LineSegment StartX=-5.5 StartY=-10.5 StartZ=0 EndX=-5.5 EndY=-27.7 EndZ=0
    g19: LineSegment StartX=-11.5 StartY=-4.3 StartZ=0 EndX=-11.5 EndY=-33.9 EndZ=0
    g20: LineSegment StartX=-14.6 StartY=-1.8 StartZ=0 EndX=-14.6 EndY=-36.4 EndZ=0
    g21: LineSegment StartX=-17.6 StartY=-1.8 StartZ=0 EndX=-17.6 EndY=-36.4 EndZ=0
    g22: LineSegment StartX=-20.6 StartY=-36.4 StartZ=0 EndX=-20.6 EndY=-1.8 EndZ=0
    g23: LineSegment StartX=-23.6 StartY=-1.8 StartZ=0 EndX=-23.6 EndY=-36.4 EndZ=0
  constraints (48):
    c: Block(g0)
    c: Block(g1)
    c: Block(g2)
    c: Block(g3)
    c: Block(g4)
    c: Block(g5)
    c: Block(g6)
    c: Block(g7)
    c: Block(g8)
    c: Block(g9)
    c: Block(g10)
    c: Block(g11)
    c: Coincident(g12,g1)
    c: Coincident(g12,g2)
    c: Vertical(g12)
    c: Coincident(g13,g1)
    c: Coincident(g13,g2)
    c: Vertical(g13)
    c: Coincident(g14,g11)
    c: Coincident(g14,g7)
    c: Vertical(g14)
    c: Coincident(g15,g11)
    c: Coincident(g15,g7)
    c: Vertical(g15)
    c: Coincident(g16,g0)
    c: Coincident(g16,g3)
    c: Vertical(g16)
    c: Coincident(g17,g4)
    c: Coincident(g17,g8)
    c: Vertical(g17)
    c: Coincident(g18,g0)
    c: Coincident(g18,g3)
    c: Vertical(g18)
    c: Coincident(g19,g4)
    c: Coincident(g19,g8)
    c: Vertical(g19)
    c: Coincident(g20,g5)
    c: Coincident(g20,g9)
    c: Vertical(g20)
    c: Coincident(g21,g5)
    c: Coincident(g21,g9)
    c: Vertical(g21)
    c: Coincident(g22,g10)
    c: Coincident(g22,g6)
    c: Vertical(g22)
    c: Coincident(g23,g6)
    c: Coincident(g23,g10)
    c: Vertical(g23)
FEATURE [Part::Extrusion] Extrude048  label="removeToCreateFanGrillHoles004"
  Base = -> Sketch057
  Dir = (0,-1,6e-16)
  DirMode = 2
  FaceMakerClass = Part::FaceMakerBullseye
  LengthFwd = 10
  LengthRev = 0
  Placement = pos=(65.4,44,54.82) rot=(0,0,1;0rad)
  Solid = true
  Symmetric = false
FEATURE [Part::Cut] Cut040  label="top021"
  Base = -> Fillet039
  Tool = -> Extrude048
FEATURE [Part::Cylinder] Cylinder041  label="removeToCreteHoleForPlugHousing034"
  Angle = 360
  AttacherType = Attacher::AttachEngine3D
  Height = 20
  Placement = pos=(-2,19,36) rot=(0,1,0;1.5708rad)
  Radius = 14.3
FEATURE [Part::MultiFuse] Fusion089  label="removeToCreteHoleForPlugHousing035"
  Shapes = -> [Box026,Cylinder041]
FEATURE [Part::Cylinder] Cylinder042
  Angle = 360
  AttacherType = Attacher::AttachEngine3D
  Height = 20
  Placement = pos=(0,0,36.15) rot=(0,0,1;0rad)
  Radius = 14.3
FEATURE [Part::Cylinder] Cylinder043
  Angle = 360
  AttacherType = Attacher::AttachEngine3D
  Height = 10
  Placement = pos=(0,0,36.15) rot=(0,0,1;0rad)
  Radius = 4
FEATURE [Part::Box] Box027  label="removeToCreteHoleForPlugHousing036"
  AttacherType = Attacher::AttachEngine3D
  Height = 28.6
  Length = 20
  Placement = pos=(106.15,0,21.7) rot=(0,0,1;0rad)
  Width = 19
FEATURE [Part::Cut] Cut041  label="top022"
  Base = -> Cut040
  Tool = -> Fusion087
FEATURE [Part::Cut] Cut039  label="top020"
  Base = -> Cut041
  Tool = -> Fusion089
FEATURE [Part::MultiFuse] Fusion090  label="removeToCreteHoleForPlugHousing037"
  Placement = pos=(70,19,36) rot=(0,1,0;1.5708rad)
  Shapes = -> [Cylinder042,Cylinder043]
FEATURE [Part::MultiFuse] Fusion088  label="removeToCreteHoleForPlugHousing033"
  Shapes = -> [Box027,Fusion090]
FEATURE [Part::Cut] Cut042  label="removeToCreteHoleForPlugHousing038"
  Base = -> Cut039
  Tool = -> Fusion088
FEATURE [Part::MultiFuse] Fusion091  label="removeFromTop"
  Shapes = -> [Fillet038,Fusion085,Fusion084,Fusion083,Extrude045]
FEATURE [Part::Cut] Cut043  label="REAL TOP ====="
  Base = -> Fillet036
  Tool = -> Fusion091
FEATURE [Part::MultiFuse] Fusion092  label="caseScrewPillarBracket016"
  Shapes = -> [Extrude030,Extrude031,Extrude032,Extrude033,Extrude034,Extrude035,Extrude036,Extrude037,Box013,Box014]
FEATURE [Sketcher::SketchObject] Sketch058  label="topSketch015"
  FullyConstrained = true
  sketch-geometry (20):
    g0: LineSegment StartX=5.21097e-06 StartY=3 StartZ=0 EndX=5.21097e-06 EndY=19 EndZ=0
    g1: ArcOfCircle CenterX=19 CenterY=19 CenterZ=0 NormalX=0 NormalY=0 NormalZ=1 AngleXU=0 Radius=19 StartAngle=1.5708 EndAngle=3.14159
    g2: ArcOfCircle CenterX=19 CenterY=19 CenterZ=0 NormalX=0 NormalY=0 NormalZ=1 AngleXU=0 Radius=16 StartAngle=1.5708 EndAngle=3.14159
    g3: LineSegment StartX=114 StartY=35 StartZ=0 EndX=19 EndY=35 EndZ=0
    g4: LineSegment StartX=5.21097e-06 StartY=3 StartZ=0 EndX=5.21097e-06 EndY=0 EndZ=0
    g5: LineSegment StartX=3 StartY=0 StartZ=0 EndX=5.21097e-06 EndY=0 EndZ=0
    g6: LineSegment StartX=3 StartY=19 StartZ=0 EndX=3 EndY=0 EndZ=0
    g7: LineSegment StartX=19 StartY=38 StartZ=0 EndX=124 EndY=38 EndZ=0
    g8: Circle CenterX=119 CenterY=35 CenterZ=0 NormalX=0 NormalY=0 NormalZ=1 AngleXU=0 Radius=1
    g9: Circle CenterX=121 CenterY=35 CenterZ=0 NormalX=0 NormalY=0 NormalZ=1 AngleXU=0 Radius=1
    g10: Circle CenterX=121 CenterY=33 CenterZ=0 NormalX=0 NormalY=0 NormalZ=1 AngleXU=0 Radius=1
    g11: BSplineCurve PolesCount=3 KnotsCount=2 Degree=2 IsPeriodic=0
    g12: GeomPoint X=119 Y=35 Z=0
    g13: GeomPoint X=121 Y=33 Z=0
    g14: LineSegment StartX=119 StartY=35 StartZ=0 EndX=114 EndY=35 EndZ=0
    g15: ArcOfCircle CenterX=105 CenterY=19 CenterZ=0 NormalX=0 NormalY=0 NormalZ=1 AngleXU=0 Radius=19 StartAngle=5.7297 EndAngle=6.28319
    g16: ArcOfCircle CenterX=105 CenterY=19 CenterZ=0 NormalX=0 NormalY=0 NormalZ=1 AngleXU=0 Radius=16 StartAngle=5.60905 EndAngle=6.28319
    g17: LineSegment StartX=121 StartY=33 StartZ=0 EndX=121 EndY=19 EndZ=0
    g18: LineSegment StartX=124 StartY=38 StartZ=0 EndX=124 EndY=19 EndZ=0
    g19: LineSegment StartX=117.5 StartY=9.01251 StartZ=0 EndX=121.163 EndY=9.0125 EndZ=0
  constraints (46):
    c: Vertical(g0)
    c: Block(g0)
    c: Coincident(g1,g0)
    c: Block(g1)
    c: Coincident(g2,g1)
    c: Block(g2)
    c: Coincident(g3,g2)
    c: Horizontal(g3)
    c: Tangent(g3,g2)
    c: Coincident(g4,g0)
    c: Distance(g4) = 3
    c: Vertical(g4)
    c: Coincident(g5,g4)
    c: Horizontal(g5)
    c: Coincident(g6,g2)
    c: Coincident(g6,g5)
    c: Vertical(g6)
    c: Horizontal(g7)
    c: Distance(g7) = 105
    c: Coincident(g7,g1)
    c: Block(g3)
    c: Weight(g8) = 1
    c: Equal(g8,g9)
    c: Equal(g8,g10)
    c: InternalAlignment(g8,g11)
    c: InternalAlignment(g9,g11)
    c: InternalAlignment(g10,g11)
    c: InternalAlignment(g12,g11)
    c: InternalAlignment(g13,g11)
    c: Block(g11)
    c: Coincident(g14,g11)
    c: Coincident(g14,g3)
    c: Horizontal(g14)
    c: Block(g15)
    c: Coincident(g16,g15)
    c: Block(g16)
    c: Coincident(g17,g11)
    c: Coincident(g17,g16)
    c: Vertical(g17)
    c: Distance(g17) = 14
    c: Coincident(g18,g7)
    c: Coincident(g18,g15)
    c: Vertical(g18)
    c: Distance(g18) = 19
    c: Coincident(g19,g16)
    c: Coincident(g19,g15)
FEATURE [Part::Extrusion] Extrude049  label="top023"
  Base = -> Sketch058
  Dir = (0,0,1)
  DirMode = 2
  FaceMakerClass = Part::FaceMakerBullseye
  LengthFwd = 72
  LengthRev = 0
  Solid = true
  Symmetric = false
FEATURE [Sketcher::SketchObject] Sketch059
  FullyConstrained = true
  MapMode = 3
  Placement = pos=(0,0,0) rot=(1,0,0;1.5708rad)
  Support = -> [Extrude049]
  sketch-geometry (8):
    g0: Circle CenterX=80.351 CenterY=-67.6202 CenterZ=0 NormalX=0 NormalY=0 NormalZ=1 AngleXU=0 Radius=2
    g1: Circle CenterX=80.351 CenterY=-67.6202 CenterZ=0 NormalX=0 NormalY=0 NormalZ=1 AngleXU=0 Radius=3
    g2: Circle CenterX=80.351 CenterY=-4.92017 CenterZ=0 NormalX=0 NormalY=0 NormalZ=1 AngleXU=0 Radius=2
    g3: Circle CenterX=80.351 CenterY=-4.92017 CenterZ=0 NormalX=0 NormalY=0 NormalZ=1 AngleXU=0 Radius=3
    g4: Circle CenterX=23.851 CenterY=-4.92017 CenterZ=0 NormalX=0 NormalY=0 NormalZ=1 AngleXU=0 Radius=2
    g5: Circle CenterX=23.851 CenterY=-4.92017 CenterZ=0 NormalX=0 NormalY=0 NormalZ=1 AngleXU=0 Radius=3
    g6: Circle CenterX=23.851 CenterY=-67.6202 CenterZ=0 NormalX=0 NormalY=0 NormalZ=1 AngleXU=0 Radius=2
    g7: Circle CenterX=23.851 CenterY=-67.6202 CenterZ=0 NormalX=0 NormalY=0 NormalZ=1 AngleXU=0 Radius=3
  constraints (8):
    c: Block(g3)
    c: Block(g2)
    c: Block(g1)
    c: Block(g0)
    c: Block(g6)
    c: Block(g7)
    c: Block(g4)
    c: Block(g5)
FEATURE [Sketcher::SketchObject] Sketch060
  FullyConstrained = true
  MapMode = 3
  Placement = pos=(0,0,0) rot=(1,0,0;1.5708rad)
  Support = -> [Extrude049]
  sketch-geometry (8):
    g0: Circle CenterX=80.351 CenterY=-67.6202 CenterZ=0 NormalX=0 NormalY=0 NormalZ=1 AngleXU=0 Radius=3
    g1: Circle CenterX=80.351 CenterY=-4.92017 CenterZ=0 NormalX=0 NormalY=0 NormalZ=1 AngleXU=0 Radius=3
    g2: Circle CenterX=23.851 CenterY=-4.92017 CenterZ=0 NormalX=0 NormalY=0 NormalZ=1 AngleXU=0 Radius=3
    g3: Circle CenterX=23.851 CenterY=-67.6202 CenterZ=0 NormalX=0 NormalY=0 NormalZ=1 AngleXU=0 Radius=3
    g4: Circle CenterX=23.851 CenterY=-67.6202 CenterZ=0 NormalX=0 NormalY=0 NormalZ=1 AngleXU=0 Radius=5
    g5: Circle CenterX=80.351 CenterY=-67.6202 CenterZ=0 NormalX=0 NormalY=0 NormalZ=1 AngleXU=0 Radius=5
    g6: Circle CenterX=23.851 CenterY=-4.92017 CenterZ=0 NormalX=0 NormalY=0 NormalZ=1 AngleXU=0 Radius=5
    g7: Circle CenterX=80.351 CenterY=-4.92017 CenterZ=0 NormalX=0 NormalY=0 NormalZ=1 AngleXU=0 Radius=5
  constraints (8):
    c: Block(g1)
    c: Block(g0)
    c: Block(g3)
    c: Block(g2)
    c: Block(g5)
    c: Block(g4)
    c: Block(g6)
    c: Block(g7)
FEATURE [Sketcher::SketchObject] Sketch061
  FullyConstrained = true
  MapMode = 3
  Placement = pos=(0,0,0) rot=(1,0,0;1.5708rad)
  sketch-geometry (8):
    g0: Circle CenterX=80.351 CenterY=-67.6202 CenterZ=0 NormalX=0 NormalY=0 NormalZ=1 AngleXU=0 Radius=3
    g1: Circle CenterX=80.351 CenterY=-4.92017 CenterZ=0 NormalX=0 NormalY=0 NormalZ=1 AngleXU=0 Radius=3
    g2: Circle CenterX=23.851 CenterY=-4.92017 CenterZ=0 NormalX=0 NormalY=0 NormalZ=1 AngleXU=0 Radius=3
    g3: Circle CenterX=23.851 CenterY=-67.6202 CenterZ=0 NormalX=0 NormalY=0 NormalZ=1 AngleXU=0 Radius=3
    g4: Circle CenterX=23.851 CenterY=-67.6202 CenterZ=0 NormalX=0 NormalY=0 NormalZ=1 AngleXU=0 Radius=5
    g5: Circle CenterX=80.351 CenterY=-67.6202 CenterZ=0 NormalX=0 NormalY=0 NormalZ=1 AngleXU=0 Radius=5
    g6: Circle CenterX=23.851 CenterY=-4.92017 CenterZ=0 NormalX=0 NormalY=0 NormalZ=1 AngleXU=0 Radius=5
    g7: Circle CenterX=80.351 CenterY=-4.92017 CenterZ=0 NormalX=0 NormalY=0 NormalZ=1 AngleXU=0 Radius=5
  constraints (8):
    c: Block(g1)
    c: Block(g0)
    c: Block(g3)
    c: Block(g2)
    c: Block(g5)
    c: Block(g4)
    c: Block(g6)
    c: Block(g7)
FEATURE [Sketcher::SketchObject] Sketch062  label="topSketch016"
  FullyConstrained = true
  sketch-geometry (20):
    g0: LineSegment StartX=5.21097e-06 StartY=3 StartZ=0 EndX=5.21097e-06 EndY=19 EndZ=0
    g1: ArcOfCircle CenterX=19 CenterY=19 CenterZ=0 NormalX=0 NormalY=0 NormalZ=1 AngleXU=0 Radius=19 StartAngle=1.5708 EndAngle=3.14159
    g2: ArcOfCircle CenterX=19 CenterY=19 CenterZ=0 NormalX=0 NormalY=0 NormalZ=1 AngleXU=0 Radius=16 StartAngle=1.5708 EndAngle=3.14159
    g3: LineSegment StartX=114 StartY=35 StartZ=0 EndX=19 EndY=35 EndZ=0
    g4: LineSegment StartX=5.21097e-06 StartY=3 StartZ=0 EndX=5.21097e-06 EndY=0 EndZ=0
    g5: LineSegment StartX=3 StartY=0 StartZ=0 EndX=5.21097e-06 EndY=0 EndZ=0
    g6: LineSegment StartX=3 StartY=19 StartZ=0 EndX=3 EndY=0 EndZ=0
    g7: LineSegment StartX=19 StartY=38 StartZ=0 EndX=124 EndY=38 EndZ=0
    g8: Circle CenterX=119 CenterY=35 CenterZ=0 NormalX=0 NormalY=0 NormalZ=1 AngleXU=0 Radius=1
    g9: Circle CenterX=121 CenterY=35 CenterZ=0 NormalX=0 NormalY=0 NormalZ=1 AngleXU=0 Radius=1
    g10: Circle CenterX=121 CenterY=33 CenterZ=0 NormalX=0 NormalY=0 NormalZ=1 AngleXU=0 Radius=1
    g11: BSplineCurve PolesCount=3 KnotsCount=2 Degree=2 IsPeriodic=0
    g12: GeomPoint X=119 Y=35 Z=0
    g13: GeomPoint X=121 Y=33 Z=0
    g14: LineSegment StartX=119 StartY=35 StartZ=0 EndX=114 EndY=35 EndZ=0
    g15: ArcOfCircle CenterX=105 CenterY=19 CenterZ=0 NormalX=0 NormalY=0 NormalZ=1 AngleXU=0 Radius=19 StartAngle=5.7297 EndAngle=6.28319
    g16: ArcOfCircle CenterX=105 CenterY=19 CenterZ=0 NormalX=0 NormalY=0 NormalZ=1 AngleXU=0 Radius=16 StartAngle=5.60905 EndAngle=6.28319
    g17: LineSegment StartX=121 StartY=33 StartZ=0 EndX=121 EndY=19 EndZ=0
    g18: LineSegment StartX=124 StartY=38 StartZ=0 EndX=124 EndY=19 EndZ=0
    g19: LineSegment StartX=117.5 StartY=9.01251 StartZ=0 EndX=121.163 EndY=9.0125 EndZ=0
  constraints (46):
    c: Vertical(g0)
    c: Block(g0)
    c: Coincident(g1,g0)
    c: Block(g1)
    c: Coincident(g2,g1)
    c: Block(g2)
    c: Coincident(g3,g2)
    c: Horizontal(g3)
    c: Tangent(g3,g2)
    c: Coincident(g4,g0)
    c: Distance(g4) = 3
    c: Vertical(g4)
    c: Coincident(g5,g4)
    c: Horizontal(g5)
    c: Coincident(g6,g2)
    c: Coincident(g6,g5)
    c: Vertical(g6)
    c: Horizontal(g7)
    c: Distance(g7) = 105
    c: Coincident(g7,g1)
    c: Block(g3)
    c: Weight(g8) = 1
    c: Equal(g8,g9)
    c: Equal(g8,g10)
    c: InternalAlignment(g8,g11)
    c: InternalAlignment(g9,g11)
    c: InternalAlignment(g10,g11)
    c: InternalAlignment(g12,g11)
    c: InternalAlignment(g13,g11)
    c: Block(g11)
    c: Coincident(g14,g11)
    c: Coincident(g14,g3)
    c: Horizontal(g14)
    c: Block(g15)
    c: Coincident(g16,g15)
    c: Block(g16)
    c: Coincident(g17,g11)
    c: Coincident(g17,g16)
    c: Vertical(g17)
    c: Distance(g17) = 14
    c: Coincident(g18,g7)
    c: Coincident(g18,g15)
    c: Vertical(g18)
    c: Distance(g18) = 19
    c: Coincident(g19,g16)
    c: Coincident(g19,g15)
FEATURE [Part::Extrusion] Extrude053  label="top024"
  Base = -> Sketch062
  Dir = (0,0,1)
  DirMode = 2
  FaceMakerClass = Part::FaceMakerBullseye
  LengthFwd = 72
  LengthRev = 0
  Solid = true
  Symmetric = false
FEATURE [Sketcher::SketchObject] Sketch063
  FullyConstrained = true
  MapMode = 3
  Placement = pos=(0,0,0) rot=(1,0,0;1.5708rad)
  Support = -> [Extrude053]
  sketch-geometry (8):
    g0: Circle CenterX=80.351 CenterY=-67.6202 CenterZ=0 NormalX=0 NormalY=0 NormalZ=1 AngleXU=0 Radius=2
    g1: Circle CenterX=80.351 CenterY=-67.6202 CenterZ=0 NormalX=0 NormalY=0 NormalZ=1 AngleXU=0 Radius=3
    g2: Circle CenterX=80.351 CenterY=-4.92017 CenterZ=0 NormalX=0 NormalY=0 NormalZ=1 AngleXU=0 Radius=2
    g3: Circle CenterX=80.351 CenterY=-4.92017 CenterZ=0 NormalX=0 NormalY=0 NormalZ=1 AngleXU=0 Radius=3
    g4: Circle CenterX=23.851 CenterY=-4.92017 CenterZ=0 NormalX=0 NormalY=0 NormalZ=1 AngleXU=0 Radius=2
    g5: Circle CenterX=23.851 CenterY=-4.92017 CenterZ=0 NormalX=0 NormalY=0 NormalZ=1 AngleXU=0 Radius=3
    g6: Circle CenterX=23.851 CenterY=-67.6202 CenterZ=0 NormalX=0 NormalY=0 NormalZ=1 AngleXU=0 Radius=2
    g7: Circle CenterX=23.851 CenterY=-67.6202 CenterZ=0 NormalX=0 NormalY=0 NormalZ=1 AngleXU=0 Radius=3
  constraints (8):
    c: Block(g3)
    c: Block(g2)
    c: Block(g1)
    c: Block(g0)
    c: Block(g6)
    c: Block(g7)
    c: Block(g4)
    c: Block(g5)
FEATURE [Part::Extrusion] Extrude054
  Base = -> Sketch063
  Dir = (0,-1,2e-16)
  DirMode = 2
  FaceMakerClass = Part::FaceMakerBullseye
  LengthFwd = 6
  LengthRev = 0
  Placement = pos=(0,9,0) rot=(0,0,1;0rad)
  Solid = true
  Symmetric = false
FEATURE [Sketcher::SketchObject] Sketch064  label="topSketch017"
  FullyConstrained = true
  sketch-geometry (20):
    g0: LineSegment StartX=5.21097e-06 StartY=3 StartZ=0 EndX=5.21097e-06 EndY=19 EndZ=0
    g1: ArcOfCircle CenterX=19 CenterY=19 CenterZ=0 NormalX=0 NormalY=0 NormalZ=1 AngleXU=0 Radius=19 StartAngle=1.5708 EndAngle=3.14159
    g2: ArcOfCircle CenterX=19 CenterY=19 CenterZ=0 NormalX=0 NormalY=0 NormalZ=1 AngleXU=0 Radius=16 StartAngle=1.5708 EndAngle=3.14159
    g3: LineSegment StartX=114 StartY=35 StartZ=0 EndX=19 EndY=35 EndZ=0
    g4: LineSegment StartX=5.21097e-06 StartY=3 StartZ=0 EndX=5.21097e-06 EndY=0 EndZ=0
    g5: LineSegment StartX=3 StartY=0 StartZ=0 EndX=5.21097e-06 EndY=0 EndZ=0
    g6: LineSegment StartX=3 StartY=19 StartZ=0 EndX=3 EndY=0 EndZ=0
    g7: LineSegment StartX=19 StartY=38 StartZ=0 EndX=124 EndY=38 EndZ=0
    g8: Circle CenterX=119 CenterY=35 CenterZ=0 NormalX=0 NormalY=0 NormalZ=1 AngleXU=0 Radius=1
    g9: Circle CenterX=121 CenterY=35 CenterZ=0 NormalX=0 NormalY=0 NormalZ=1 AngleXU=0 Radius=1
    g10: Circle CenterX=121 CenterY=33 CenterZ=0 NormalX=0 NormalY=0 NormalZ=1 AngleXU=0 Radius=1
    g11: BSplineCurve PolesCount=3 KnotsCount=2 Degree=2 IsPeriodic=0
    g12: GeomPoint X=119 Y=35 Z=0
    g13: GeomPoint X=121 Y=33 Z=0
    g14: LineSegment StartX=119 StartY=35 StartZ=0 EndX=114 EndY=35 EndZ=0
    g15: ArcOfCircle CenterX=105 CenterY=19 CenterZ=0 NormalX=0 NormalY=0 NormalZ=1 AngleXU=0 Radius=19 StartAngle=5.7297 EndAngle=6.28319
    g16: ArcOfCircle CenterX=105 CenterY=19 CenterZ=0 NormalX=0 NormalY=0 NormalZ=1 AngleXU=0 Radius=16 StartAngle=5.60905 EndAngle=6.28319
    g17: LineSegment StartX=121 StartY=33 StartZ=0 EndX=121 EndY=19 EndZ=0
    g18: LineSegment StartX=124 StartY=38 StartZ=0 EndX=124 EndY=19 EndZ=0
    g19: LineSegment StartX=117.5 StartY=9.01251 StartZ=0 EndX=121.163 EndY=9.0125 EndZ=0
  constraints (46):
    c: Vertical(g0)
    c: Block(g0)
    c: Coincident(g1,g0)
    c: Block(g1)
    c: Coincident(g2,g1)
    c: Block(g2)
    c: Coincident(g3,g2)
    c: Horizontal(g3)
    c: Tangent(g3,g2)
    c: Coincident(g4,g0)
    c: Distance(g4) = 3
    c: Vertical(g4)
    c: Coincident(g5,g4)
    c: Horizontal(g5)
    c: Coincident(g6,g2)
    c: Coincident(g6,g5)
    c: Vertical(g6)
    c: Horizontal(g7)
    c: Distance(g7) = 105
    c: Coincident(g7,g1)
    c: Block(g3)
    c: Weight(g8) = 1
    c: Equal(g8,g9)
    c: Equal(g8,g10)
    c: InternalAlignment(g8,g11)
    c: InternalAlignment(g9,g11)
    c: InternalAlignment(g10,g11)
    c: InternalAlignment(g12,g11)
    c: InternalAlignment(g13,g11)
    c: Block(g11)
    c: Coincident(g14,g11)
    c: Coincident(g14,g3)
    c: Horizontal(g14)
    c: Block(g15)
    c: Coincident(g16,g15)
    c: Block(g16)
    c: Coincident(g17,g11)
    c: Coincident(g17,g16)
    c: Vertical(g17)
    c: Distance(g17) = 14
    c: Coincident(g18,g7)
    c: Coincident(g18,g15)
    c: Vertical(g18)
    c: Distance(g18) = 19
    c: Coincident(g19,g16)
    c: Coincident(g19,g15)
FEATURE [Sketcher::SketchObject] Sketch065
  FullyConstrained = true
  MapMode = 3
  Placement = pos=(0,0,0) rot=(1,0,0;1.5708rad)
  sketch-geometry (8):
    g0: Circle CenterX=80.351 CenterY=-67.6202 CenterZ=0 NormalX=0 NormalY=0 NormalZ=1 AngleXU=0 Radius=3
    g1: Circle CenterX=80.351 CenterY=-4.92017 CenterZ=0 NormalX=0 NormalY=0 NormalZ=1 AngleXU=0 Radius=3
    g2: Circle CenterX=23.851 CenterY=-4.92017 CenterZ=0 NormalX=0 NormalY=0 NormalZ=1 AngleXU=0 Radius=3
    g3: Circle CenterX=23.851 CenterY=-67.6202 CenterZ=0 NormalX=0 NormalY=0 NormalZ=1 AngleXU=0 Radius=3
    g4: Circle CenterX=23.851 CenterY=-67.6202 CenterZ=0 NormalX=0 NormalY=0 NormalZ=1 AngleXU=0 Radius=5
    g5: Circle CenterX=80.351 CenterY=-67.6202 CenterZ=0 NormalX=0 NormalY=0 NormalZ=1 AngleXU=0 Radius=5
    g6: Circle CenterX=23.851 CenterY=-4.92017 CenterZ=0 NormalX=0 NormalY=0 NormalZ=1 AngleXU=0 Radius=5
    g7: Circle CenterX=80.351 CenterY=-4.92017 CenterZ=0 NormalX=0 NormalY=0 NormalZ=1 AngleXU=0 Radius=5
  constraints (8):
    c: Block(g1)
    c: Block(g0)
    c: Block(g3)
    c: Block(g2)
    c: Block(g5)
    c: Block(g4)
    c: Block(g6)
    c: Block(g7)
FEATURE [Part::Extrusion] Extrude056
  Base = -> Sketch065
  Dir = (0,-1,2e-16)
  DirMode = 2
  FaceMakerClass = Part::FaceMakerBullseye
  LengthFwd = 2
  LengthRev = 0
  Solid = true
  Symmetric = false
FEATURE [Part::Extrusion] Extrude057  label="top025"
  Base = -> Sketch064
  Dir = (0,0,1)
  DirMode = 2
  FaceMakerClass = Part::FaceMakerBullseye
  LengthFwd = 72
  LengthRev = 0
  Solid = true
  Symmetric = false
FEATURE [Sketcher::SketchObject] Sketch066
  FullyConstrained = true
  MapMode = 3
  Placement = pos=(0,0,0) rot=(1,0,0;1.5708rad)
  Support = -> [Extrude057]
  sketch-geometry (8):
    g0: Circle CenterX=80.351 CenterY=-67.6202 CenterZ=0 NormalX=0 NormalY=0 NormalZ=1 AngleXU=0 Radius=3
    g1: Circle CenterX=80.351 CenterY=-4.92017 CenterZ=0 NormalX=0 NormalY=0 NormalZ=1 AngleXU=0 Radius=3
    g2: Circle CenterX=23.851 CenterY=-4.92017 CenterZ=0 NormalX=0 NormalY=0 NormalZ=1 AngleXU=0 Radius=3
    g3: Circle CenterX=23.851 CenterY=-67.6202 CenterZ=0 NormalX=0 NormalY=0 NormalZ=1 AngleXU=0 Radius=3
    g4: Circle CenterX=23.851 CenterY=-67.6202 CenterZ=0 NormalX=0 NormalY=0 NormalZ=1 AngleXU=0 Radius=5
    g5: Circle CenterX=80.351 CenterY=-67.6202 CenterZ=0 NormalX=0 NormalY=0 NormalZ=1 AngleXU=0 Radius=5
    g6: Circle CenterX=23.851 CenterY=-4.92017 CenterZ=0 NormalX=0 NormalY=0 NormalZ=1 AngleXU=0 Radius=5
    g7: Circle CenterX=80.351 CenterY=-4.92017 CenterZ=0 NormalX=0 NormalY=0 NormalZ=1 AngleXU=0 Radius=5
  constraints (8):
    c: Block(g1)
    c: Block(g0)
    c: Block(g3)
    c: Block(g2)
    c: Block(g5)
    c: Block(g4)
    c: Block(g6)
    c: Block(g7)
FEATURE [Part::Extrusion] Extrude055
  Base = -> Sketch066
  Dir = (0,-1,2e-16)
  DirMode = 2
  FaceMakerClass = Part::FaceMakerBullseye
  LengthFwd = 2
  LengthRev = 0
  Solid = true
  Symmetric = false
FEATURE [Part::Fillet] Fillet041
  Base = -> Extrude056
  Edges = 4 edges r=1.99: [Edge6,Edge12,Edge18,Edge24]
FEATURE [Part::Cut] Cut045
  Base = -> Extrude055
  Placement = pos=(0,6,0) rot=(0,0,1;0rad)
  Tool = -> Fillet041
FEATURE [Part::MultiFuse] Fusion095  label="pcbScrewPillars"
  Placement = pos=(-3.2,-1,72.3) rot=(0,0,1;0rad)
  Shapes = -> [Cut045,Extrude054]
FEATURE [Part::Feature] Face113
  shape: bbox 3.2 x 1.5 x 2e-07 mm, 1 faces, 0 solids (baked)
FEATURE [Part::Revolution] Revolve121  label="backCaseScrewRetainer002"
  Angle = 360
  Axis = (0,1,0)
  Base = (0,0,0)
  FaceMakerClass = Part::FaceMakerBullseye
  Placement = pos=(12.5,3,62) rot=(0,0,1;0rad)
  Solid = false
  Source = -> Face113
  Symmetric = false
FEATURE [Part::Feature] Face114
  shape: bbox 3.2 x 1.5 x 2e-07 mm, 1 faces, 0 solids (baked)
FEATURE [Part::Feature] Face115
  shape: bbox 3.2 x 1.5 x 2e-07 mm, 1 faces, 0 solids (baked)
FEATURE [Part::Feature] Face116
  shape: bbox 3.2 x 1.5 x 2e-07 mm, 1 faces, 0 solids (baked)
FEATURE [Part::Revolution] Revolve122  label="frontCaseScrewRetainer004"
  Angle = 360
  Axis = (0,1,0)
  Base = (0,0,0)
  FaceMakerClass = Part::FaceMakerBullseye
  Placement = pos=(89.5,3,68.5) rot=(0,0,1;0rad)
  Solid = false
  Source = -> Face115
  Symmetric = false
FEATURE [Part::Revolution] Revolve123  label="frontCaseScrewRetainer005"
  Angle = 360
  Axis = (0,1,0)
  Base = (0,0,0)
  FaceMakerClass = Part::FaceMakerBullseye
  Placement = pos=(89.5,3,3.5) rot=(0,0,1;0rad)
  Solid = false
  Source = -> Face116
  Symmetric = false
FEATURE [Part::Revolution] Revolve124  label="backCaseScrewRetainer003"
  Angle = 360
  Axis = (0,1,0)
  Base = (0,0,0)
  FaceMakerClass = Part::FaceMakerBullseye
  Placement = pos=(12.5,3,10) rot=(0,0,1;0rad)
  Solid = false
  Source = -> Face114
  Symmetric = false
FEATURE [Part::Feature] Face117
  shape: bbox 3.6 x 3.2 x 2e-07 mm, 1 faces, 0 solids (baked)
FEATURE [Part::Revolution] Revolve125  label="moreFrontCaseScrewRetainer004"
  Angle = 360
  Axis = (0,1,0)
  Base = (0,0,0)
  FaceMakerClass = Part::FaceMakerBullseye
  Placement = pos=(109.5,4.5,68.5) rot=(0,0,1;0rad)
  Solid = false
  Source = -> Face117
  Symmetric = false
FEATURE [Part::Feature] Face118
  shape: bbox 3.6 x 3.2 x 2e-07 mm, 1 faces, 0 solids (baked)
FEATURE [Part::Revolution] Revolve126  label="moreFrontCaseScrewRetainer005"
  Angle = 360
  Axis = (0,1,0)
  Base = (0,0,0)
  FaceMakerClass = Part::FaceMakerBullseye
  Placement = pos=(109.5,4.5,3.5) rot=(0,0,1;0rad)
  Solid = false
  Source = -> Face118
  Symmetric = false
FEATURE [Part::MultiFuse] Fusion096  label="screwRetainers001"
  Shapes = -> [Revolve126,Revolve125,Revolve124,Revolve123,Revolve122,Revolve121]
FEATURE [Part::Feature] Face119
  shape: bbox 10 x 16.5 x 2e-07 mm, 1 faces, 0 solids (baked)
FEATURE [Part::Revolution] Revolve130  label="plugHousing050"
  Angle = 360
  Axis = (0,1,0)
  Base = (0,0,0)
  FaceMakerClass = Part::FaceMakerBullseye
  Placement = pos=(0,0,36.15) rot=(0,0,1;0rad)
  Solid = false
  Source = -> Face119
  Symmetric = false
FEATURE [Part::Feature] Face120
  shape: bbox 10 x 16.5 x 2e-07 mm, 1 faces, 0 solids (baked)
FEATURE [Part::Feature] Face121
  shape: bbox 10 x 16.5 x 2e-07 mm, 1 faces, 0 solids (baked)
FEATURE [Part::Revolution] Revolve127  label="plugHousing047"
  Angle = 360
  Axis = (0,1,0)
  Base = (0,0,0)
  FaceMakerClass = Part::FaceMakerBullseye
  Placement = pos=(0,0,36.15) rot=(0,0,1;0rad)
  Solid = false
  Source = -> Face121
  Symmetric = false
FEATURE [Part::Feature] Face122
  shape: bbox 10 x 16.5 x 2e-07 mm, 1 faces, 0 solids (baked)
FEATURE [Part::Feature] Face123
  shape: bbox 10 x 16.5 x 2e-07 mm, 1 faces, 0 solids (baked)
FEATURE [Part::Revolution] Revolve128  label="plugHousing048"
  Angle = 360
  Axis = (0,1,0)
  Base = (0,0,0)
  FaceMakerClass = Part::FaceMakerBullseye
  Placement = pos=(0,0,36.15) rot=(0,0,1;0rad)
  Solid = false
  Source = -> Face123
  Symmetric = false
FEATURE [Part::MultiFuse] Fusion100  label="plugHousing054"
  Placement = pos=(0,0,0) rot=(0,0,1;1.5708rad)
  Shapes = -> [Revolve130,Revolve128]
FEATURE [Part::Feature] Face124
  shape: bbox 10 x 16.5 x 2e-07 mm, 1 faces, 0 solids (baked)
FEATURE [Part::Feature] Face125
  shape: bbox 10 x 16.5 x 2e-07 mm, 1 faces, 0 solids (baked)
FEATURE [Part::Revolution] Revolve129  label="plugHousing049"
  Angle = 360
  Axis = (0,1,0)
  Base = (0,0,0)
  FaceMakerClass = Part::FaceMakerBullseye
  Placement = pos=(0,0,36.15) rot=(0,0,1;0rad)
  Solid = false
  Source = -> Face125
  Symmetric = false
FEATURE [Part::Feature] Face126
  shape: bbox 10 x 16.5 x 2e-07 mm, 1 faces, 0 solids (baked)
FEATURE [Part::Revolution] Revolve131  label="plugHousing058"
  Angle = 360
  Axis = (0,1,0)
  Base = (0,0,0)
  FaceMakerClass = Part::FaceMakerBullseye
  Placement = pos=(0,0,36.15) rot=(0,0,1;0rad)
  Solid = false
  Source = -> Face120
  Symmetric = false
FEATURE [Part::MultiFuse] Fusion099  label="plugHousing053"
  Placement = pos=(0,0,0) rot=(0,0,1;1.5708rad)
  Shapes = -> [Revolve127,Revolve131]
FEATURE [Part::MultiFuse] Fusion102  label="plugHousing056"
  Placement = pos=(0,19,0) rot=(0,0,1;3.14159rad)
  Shapes = -> [Fusion100,Fusion099]
FEATURE [Part::Revolution] Revolve132  label="plugHousing059"
  Angle = 360
  Axis = (0,1,0)
  Base = (0,0,0)
  FaceMakerClass = Part::FaceMakerBullseye
  Placement = pos=(0,0,36.15) rot=(0,0,1;0rad)
  Solid = false
  Source = -> Face126
  Symmetric = false
FEATURE [Part::Revolution] Revolve133  label="plugHousing060"
  Angle = 360
  Axis = (0,1,0)
  Base = (0,0,0)
  FaceMakerClass = Part::FaceMakerBullseye
  Placement = pos=(0,0,36.15) rot=(0,0,1;0rad)
  Solid = false
  Source = -> Face122
  Symmetric = false
FEATURE [Part::MultiFuse] Fusion097  label="plugHousing051"
  Placement = pos=(0,0,0) rot=(0,0,1;1.5708rad)
  Shapes = -> [Revolve133,Revolve132]
FEATURE [Part::Revolution] Revolve134  label="plugHousing061"
  Angle = 360
  Axis = (0,1,0)
  Base = (0,0,0)
  FaceMakerClass = Part::FaceMakerBullseye
  Placement = pos=(0,0,36.15) rot=(0,0,1;0rad)
  Solid = false
  Source = -> Face124
  Symmetric = false
FEATURE [Part::MultiFuse] Fusion101  label="plugHousing055"
  Placement = pos=(0,0,0) rot=(0,0,1;1.5708rad)
  Shapes = -> [Revolve129,Revolve134]
FEATURE [Part::MultiFuse] Fusion098  label="plugHousing052"
  Placement = pos=(0,19,0) rot=(0,0,1;3.14159rad)
  Shapes = -> [Fusion097,Fusion101]
FEATURE [Part::MultiFuse] Fusion103  label="plugHousing057"
  Placement = pos=(122.621,0,-0.15) rot=(0,0,1;0rad)
  Shapes = -> [Fusion102,Fusion098]
FEATURE [Part::Box] Box028  label="Cube015"
  AttacherType = Attacher::AttachEngine3D
  Height = 28
  Length = 3
  Placement = pos=(110.7,19,22) rot=(0,0,1;0rad)
  Width = 15.7
FEATURE [Part::Cylinder] Cylinder044
  Angle = 360
  AttacherType = Attacher::AttachEngine3D
  Height = 20
  Placement = pos=(0,0,36.15) rot=(0,0,1;0rad)
  Radius = 10.3
FEATURE [Part::Cylinder] Cylinder045
  Angle = 360
  AttacherType = Attacher::AttachEngine3D
  Height = 10
  Placement = pos=(0,0,36.15) rot=(0,0,1;0rad)
  Radius = 4
FEATURE [Part::MultiFuse] Fusion104  label="removeToCreteHoleForPlugHousing040"
  Placement = pos=(70,19,36) rot=(0,1,0;1.5708rad)
  Shapes = -> [Cylinder044,Cylinder045]
FEATURE [Part::Cut] Cut046  label="plugHousingTab003"
  Base = -> Box028
  Tool = -> Fusion104
FEATURE [Part::MultiFuse] Fusion105  label="plugHousing062"
  Shapes = -> [Fusion103,Cut046]
FEATURE [Part::Fillet] Fillet042
  Base = -> Fusion105
  Edges = 1 edges r=2: [Edge25]
FEATURE [Part::Fillet] Fillet043  label="plugHousing063"
  Base = -> Fillet042
  Edges = 1 edges r=2: [Edge8]
  Placement = pos=(7,0,0) rot=(0,0,1;0rad)
FEATURE [Part::Feature] Face127
  shape: bbox 10 x 16.5 x 2e-07 mm, 1 faces, 0 solids (baked)
FEATURE [Part::Feature] Face128
  shape: bbox 10 x 16.5 x 2e-07 mm, 1 faces, 0 solids (baked)
FEATURE [Part::Revolution] Revolve137  label="plugHousing070"
  Angle = 360
  Axis = (0,1,0)
  Base = (0,0,0)
  FaceMakerClass = Part::FaceMakerBullseye
  Placement = pos=(0,0,36.15) rot=(0,0,1;0rad)
  Solid = false
  Source = -> Face127
  Symmetric = false
FEATURE [Part::Revolution] Revolve140  label="plugHousing073"
  Angle = 360
  Axis = (0,1,0)
  Base = (0,0,0)
  FaceMakerClass = Part::FaceMakerBullseye
  Placement = pos=(0,0,36.15) rot=(0,0,1;0rad)
  Solid = false
  Source = -> Face128
  Symmetric = false
FEATURE [Part::Feature] Face129
  shape: bbox 10 x 16.5 x 2e-07 mm, 1 faces, 0 solids (baked)
FEATURE [Part::Revolution] Revolve138  label="plugHousing071"
  Angle = 360
  Axis = (0,1,0)
  Base = (0,0,0)
  FaceMakerClass = Part::FaceMakerBullseye
  Placement = pos=(0,0,36.15) rot=(0,0,1;0rad)
  Solid = false
  Source = -> Face129
  Symmetric = false
FEATURE [Part::Feature] Face130
  shape: bbox 10 x 16.5 x 2e-07 mm, 1 faces, 0 solids (baked)
FEATURE [Part::Revolution] Revolve139  label="plugHousing072"
  Angle = 360
  Axis = (0,1,0)
  Base = (0,0,0)
  FaceMakerClass = Part::FaceMakerBullseye
  Placement = pos=(0,0,36.15) rot=(0,0,1;0rad)
  Solid = false
  Source = -> Face130
  Symmetric = false
FEATURE [Part::Feature] Face131
  shape: bbox 10 x 16.5 x 2e-07 mm, 1 faces, 0 solids (baked)
FEATURE [Part::Revolution] Revolve135  label="plugHousing068"
  Angle = 360
  Axis = (0,1,0)
  Base = (0,0,0)
  FaceMakerClass = Part::FaceMakerBullseye
  Placement = pos=(0,0,36.15) rot=(0,0,1;0rad)
  Solid = false
  Source = -> Face131
  Symmetric = false
FEATURE [Part::MultiFuse] Fusion112  label="plugHousing078"
  Placement = pos=(0,0,0) rot=(0,0,1;1.5708rad)
  Shapes = -> [Revolve135,Revolve139]
FEATURE [Part::Feature] Face132
  shape: bbox 10 x 16.5 x 2e-07 mm, 1 faces, 0 solids (baked)
FEATURE [Part::Revolution] Revolve141  label="plugHousing074"
  Angle = 360
  Axis = (0,1,0)
  Base = (0,0,0)
  FaceMakerClass = Part::FaceMakerBullseye
  Placement = pos=(0,0,36.15) rot=(0,0,1;0rad)
  Solid = false
  Source = -> Face132
  Symmetric = false
FEATURE [Part::MultiFuse] Fusion110  label="plugHousing076"
  Placement = pos=(0,0,0) rot=(0,0,1;1.5708rad)
  Shapes = -> [Revolve141,Revolve140]
FEATURE [Part::Feature] Face133
  shape: bbox 10 x 16.5 x 2e-07 mm, 1 faces, 0 solids (baked)
FEATURE [Part::Revolution] Revolve136  label="plugHousing069"
  Angle = 360
  Axis = (0,1,0)
  Base = (0,0,0)
  FaceMakerClass = Part::FaceMakerBullseye
  Placement = pos=(0,0,36.15) rot=(0,0,1;0rad)
  Solid = false
  Source = -> Face133
  Symmetric = false
FEATURE [Part::MultiFuse] Fusion106  label="plugHousing064"
  Placement = pos=(0,0,0) rot=(0,0,1;1.5708rad)
  Shapes = -> [Revolve138,Revolve136]
FEATURE [Part::MultiFuse] Fusion108  label="plugHousing066"
  Placement = pos=(0,19,0) rot=(0,0,1;3.14159rad)
  Shapes = -> [Fusion106,Fusion112]
FEATURE [Part::Feature] Face134
  shape: bbox 10 x 16.5 x 2e-07 mm, 1 faces, 0 solids (baked)
FEATURE [Part::Revolution] Revolve142  label="plugHousing075"
  Angle = 360
  Axis = (0,1,0)
  Base = (0,0,0)
  FaceMakerClass = Part::FaceMakerBullseye
  Placement = pos=(0,0,36.15) rot=(0,0,1;0rad)
  Solid = false
  Source = -> Face134
  Symmetric = false
FEATURE [Part::MultiFuse] Fusion107  label="plugHousing065"
  Placement = pos=(0,0,0) rot=(0,0,1;1.5708rad)
  Shapes = -> [Revolve137,Revolve142]
FEATURE [Part::MultiFuse] Fusion111  label="plugHousing077"
  Placement = pos=(0,19,0) rot=(0,0,1;3.14159rad)
  Shapes = -> [Fusion110,Fusion107]
FEATURE [Part::MultiFuse] Fusion109  label="plugHousing067"
  Placement = pos=(131.236,0,-0.15) rot=(0,0,1;0rad)
  Shapes = -> [Fusion108,Fusion111]
FEATURE [Part::MultiFuse] Fusion113  label="plugHousing079"
  Shapes = -> [Fillet043,Fusion109]
FEATURE [Part::Feature] Face135
  shape: bbox 3.5 x 17.8 x 2e-07 mm, 1 faces, 0 solids (baked)
FEATURE [Part::Revolution] Revolve143  label="removeToCreateScrewAndThreadedInsertHole049"
  Angle = 360
  Axis = (0,1,0)
  Base = (0,0,0)
  FaceMakerClass = Part::FaceMakerBullseye
  Placement = pos=(12.5,0,10) rot=(0,0,1;0rad)
  Solid = false
  Source = -> Face135
  Symmetric = false
FEATURE [Part::Feature] Face136
  shape: bbox 3.5 x 17.8 x 2e-07 mm, 1 faces, 0 solids (baked)
FEATURE [Part::Revolution] Revolve144  label="removeToCreateScrewAndThreadedInsertHole050"
  Angle = 360
  Axis = (0,1,0)
  Base = (0,0,0)
  FaceMakerClass = Part::FaceMakerBullseye
  Placement = pos=(12.5,0,62) rot=(0,0,1;0rad)
  Solid = false
  Source = -> Face136
  Symmetric = false
FEATURE [Part::Feature] Face137
  shape: bbox 3.5 x 17.8 x 2e-07 mm, 1 faces, 0 solids (baked)
FEATURE [Part::Revolution] Revolve145  label="removeToCreateScrewAndThreadedInsertHole051"
  Angle = 360
  Axis = (0,1,0)
  Base = (0,0,0)
  FaceMakerClass = Part::FaceMakerBullseye
  Placement = pos=(89.5,0,68.5) rot=(0,0,1;0rad)
  Solid = false
  Source = -> Face137
  Symmetric = false
FEATURE [Part::Feature] Face138
  shape: bbox 3.5 x 17.8 x 2e-07 mm, 1 faces, 0 solids (baked)
FEATURE [Part::Revolution] Revolve146  label="removeToCreateScrewAndThreadedInsertHole052"
  Angle = 360
  Axis = (0,1,0)
  Base = (0,0,0)
  FaceMakerClass = Part::FaceMakerBullseye
  Placement = pos=(89.5,0,3.5) rot=(0,0,1;0rad)
  Solid = false
  Source = -> Face138
  Symmetric = false
FEATURE [Part::Feature] Face139
  shape: bbox 3.5 x 17.8 x 2e-07 mm, 1 faces, 0 solids (baked)
FEATURE [Part::Revolution] Revolve147  label="removeToCreateScrewAndThreadedInsertHole053"
  Angle = 360
  Axis = (0,1,0)
  Base = (0,0,0)
  FaceMakerClass = Part::FaceMakerBullseye
  Placement = pos=(109.5,4.7,3.5) rot=(0,0,1;0rad)
  Solid = false
  Source = -> Face139
  Symmetric = false
FEATURE [Part::Feature] Face140
  shape: bbox 3.5 x 17.8 x 2e-07 mm, 1 faces, 0 solids (baked)
FEATURE [Part::Revolution] Revolve148  label="removeToCreateScrewAndThreadedInsertHole054"
  Angle = 360
  Axis = (0,1,0)
  Base = (0,0,0)
  FaceMakerClass = Part::FaceMakerBullseye
  Placement = pos=(109.5,4.7,68.5) rot=(0,0,1;0rad)
  Solid = false
  Source = -> Face140
  Symmetric = false
FEATURE [Part::MultiFuse] Fusion114  label="removeToCreateScrewAndThreadedInsertHole055"
  Shapes = -> [Revolve148,Revolve147,Revolve146,Revolve145,Revolve144,Revolve143]
FEATURE [Part::Cut] Cut047  label="casePillars004"
  Base = -> Cut037
  Tool = -> Fusion114
FEATURE [Part::Feature] Face141
  shape: bbox 3.5 x 17.8 x 2e-07 mm, 1 faces, 0 solids (baked)
FEATURE [Part::Feature] Face142
  shape: bbox 3.5 x 17.8 x 2e-07 mm, 1 faces, 0 solids (baked)
FEATURE [Part::Feature] Face143
  shape: bbox 3.5 x 17.8 x 2e-07 mm, 1 faces, 0 solids (baked)
FEATURE [Part::Revolution] Revolve149  label="removeToCreateScrewAndThreadedInsertHole057"
  Angle = 360
  Axis = (0,1,0)
  Base = (0,0,0)
  FaceMakerClass = Part::FaceMakerBullseye
  Placement = pos=(12.5,0,10) rot=(0,0,1;0rad)
  Solid = false
  Source = -> Face141
  Symmetric = false
FEATURE [Part::Feature] Face144
  shape: bbox 3.5 x 17.8 x 2e-07 mm, 1 faces, 0 solids (baked)
FEATURE [Part::Feature] Face145
  shape: bbox 3.5 x 17.8 x 2e-07 mm, 1 faces, 0 solids (baked)
FEATURE [Part::Feature] Face146
  shape: bbox 3.5 x 17.8 x 2e-07 mm, 1 faces, 0 solids (baked)
FEATURE [Part::Revolution] Revolve150  label="removeToCreateScrewAndThreadedInsertHole058"
  Angle = 360
  Axis = (0,1,0)
  Base = (0,0,0)
  FaceMakerClass = Part::FaceMakerBullseye
  Placement = pos=(12.5,0,62) rot=(0,0,1;0rad)
  Solid = false
  Source = -> Face146
  Symmetric = false
FEATURE [Part::Revolution] Revolve151  label="removeToCreateScrewAndThreadedInsertHole059"
  Angle = 360
  Axis = (0,1,0)
  Base = (0,0,0)
  FaceMakerClass = Part::FaceMakerBullseye
  Placement = pos=(89.5,0,68.5) rot=(0,0,1;0rad)
  Solid = false
  Source = -> Face143
  Symmetric = false
FEATURE [Part::Revolution] Revolve152  label="removeToCreateScrewAndThreadedInsertHole060"
  Angle = 360
  Axis = (0,1,0)
  Base = (0,0,0)
  FaceMakerClass = Part::FaceMakerBullseye
  Placement = pos=(89.5,0,3.5) rot=(0,0,1;0rad)
  Solid = false
  Source = -> Face142
  Symmetric = false
FEATURE [Part::Revolution] Revolve153  label="removeToCreateScrewAndThreadedInsertHole061"
  Angle = 360
  Axis = (0,1,0)
  Base = (0,0,0)
  FaceMakerClass = Part::FaceMakerBullseye
  Placement = pos=(109.5,4.7,3.5) rot=(0,0,1;0rad)
  Solid = false
  Source = -> Face145
  Symmetric = false
FEATURE [Part::Revolution] Revolve154  label="removeToCreateScrewAndThreadedInsertHole062"
  Angle = 360
  Axis = (0,1,0)
  Base = (0,0,0)
  FaceMakerClass = Part::FaceMakerBullseye
  Placement = pos=(109.5,4.7,68.5) rot=(0,0,1;0rad)
  Solid = false
  Source = -> Face144
  Symmetric = false
FEATURE [Part::MultiFuse] Fusion115  label="removeToCreateScrewAndThreadedInsertHole056"
  Shapes = -> [Revolve154,Revolve153,Revolve152,Revolve151,Revolve150,Revolve149]
FEATURE [Part::Feature] Face147
  shape: bbox 9.8 x 26.5 x 2e-07 mm, 1 faces, 0 solids (baked)
FEATURE [Part::Revolution] Revolve155
  Angle = 360
  Axis = (0,1,0)
  Base = (0,0,0)
  FaceMakerClass = Part::FaceMakerBullseye
  Placement = pos=(0,0,0) rot=(0,0,1;1.5708rad)
  Solid = false
  Source = -> Face147
  Symmetric = false
FEATURE [Part::Feature] Face148
  shape: bbox 9.8 x 26.5 x 2e-07 mm, 1 faces, 0 solids (baked)
FEATURE [Part::Revolution] Revolve156
  Angle = 360
  Axis = (0,1,0)
  Base = (0,0,0)
  FaceMakerClass = Part::FaceMakerBullseye
  Placement = pos=(0,0,0) rot=(0,0,1;1.5708rad)
  Solid = false
  Source = -> Face148
  Symmetric = false
FEATURE [Part::MultiFuse] Fusion116
  Placement = pos=(-18,19,36) rot=(0,0,1;0rad)
  Shapes = -> [Revolve156,Revolve155]
FEATURE [Part::Box] Box029  label="Cube016"
  AttacherType = Attacher::AttachEngine3D
  Height = 28
  Length = 3
  Placement = pos=(110.7,19,22) rot=(0,0,1;0rad)
  Width = 15.7
FEATURE [Part::Cylinder] Cylinder046
  Angle = 360
  AttacherType = Attacher::AttachEngine3D
  Height = 10
  Placement = pos=(0,0,36.15) rot=(0,0,1;0rad)
  Radius = 4
FEATURE [Part::Cylinder] Cylinder047
  Angle = 360
  AttacherType = Attacher::AttachEngine3D
  Height = 20
  Placement = pos=(0,0,36.15) rot=(0,0,1;0rad)
  Radius = 10.3
FEATURE [Part::MultiFuse] Fusion117  label="removeToCreteHoleForPlugHousing041"
  Placement = pos=(70,19,36) rot=(0,1,0;1.5708rad)
  Shapes = -> [Cylinder047,Cylinder046]
FEATURE [Part::Cut] Cut049  label="plugHousingTab004"
  Base = -> Box029
  Placement = pos=(-107.4,-14,0) rot=(0,0,1;0rad)
  Tool = -> Fusion117
FEATURE [Part::Box] Box030  label="Cube017"
  AttacherType = Attacher::AttachEngine3D
  Height = 28
  Length = 3
  Placement = pos=(110.7,19,22) rot=(0,0,1;0rad)
  Width = 15.7
FEATURE [Part::Cylinder] Cylinder048
  Angle = 360
  AttacherType = Attacher::AttachEngine3D
  Height = 10
  Placement = pos=(0,0,36.15) rot=(0,0,1;0rad)
  Radius = 4
FEATURE [Part::Cylinder] Cylinder049
  Angle = 360
  AttacherType = Attacher::AttachEngine3D
  Height = 20
  Placement = pos=(0,0,36.15) rot=(0,0,1;0rad)
  Radius = 10.3
FEATURE [Part::MultiFuse] Fusion118  label="removeToCreteHoleForPlugHousing042"
  Placement = pos=(70,19,36) rot=(0,1,0;1.5708rad)
  Shapes = -> [Cylinder049,Cylinder048]
FEATURE [Part::Cut] Cut050  label="plugHousingTab005"
  Base = -> Box030
  Placement = pos=(-107.4,-14,0) rot=(0,0,1;0rad)
  Tool = -> Fusion118
FEATURE [Part::MultiFuse] Fusion119
  Placement = pos=(9.6,23,0) rot=(0,0,1;3.14159rad)
  Shapes = -> [Cut049,Cut050]
FEATURE [Part::Box] Box031  label="Cube018"
  AttacherType = Attacher::AttachEngine3D
  Height = 10
  Length = 3
  Placement = pos=(3.3,4,12) rot=(0,0,1;0rad)
  Width = 10
FEATURE [Part::Fillet] Fillet044
  Base = -> Box031
  Edges = 1 edges r=2: [Edge11]
FEATURE [Part::Box] Box032  label="Cube019"
  AttacherType = Attacher::AttachEngine3D
  Height = 10
  Length = 3
  Placement = pos=(3.3,4,50) rot=(0,0,1;0rad)
  Width = 10
FEATURE [Part::Fillet] Fillet045
  Base = -> Box032
  Edges = 1 edges r=2: [Edge12]
FEATURE [Part::Box] Box033  label="Cube020"
  AttacherType = Attacher::AttachEngine3D
  Height = 28
  Length = 4
  Placement = pos=(5,0,22) rot=(0,0,1;0rad)
  Width = 10
FEATURE [Part::Fillet] Fillet046
  Base = -> Box033
  Edges = 1 edges r=1: [Edge7]
FEATURE [Part::Fillet] Fillet047
  Base = -> Fillet046
  Edges = 1 edges r=2: [Edge5]
FEATURE [Part::Fillet] Fillet048
  Base = -> Fillet047
  Edges = 1 edges r=2: [Edge2]
FEATURE [Part::Cylinder] Cylinder050
  Angle = 360
  AttacherType = Attacher::AttachEngine3D
  Height = 20
  Placement = pos=(0,0,36.15) rot=(0,0,1;0rad)
  Radius = 8.2
FEATURE [Part::Cylinder] Cylinder051
  Angle = 360
  AttacherType = Attacher::AttachEngine3D
  Height = 10
  Placement = pos=(0,0,36.15) rot=(0,0,1;0rad)
  Radius = 4
FEATURE [Part::MultiFuse] Fusion120  label="removeToCreteHoleForPlugHousing043"
  Placement = pos=(-42,19,36) rot=(0,1,0;1.5708rad)
  Shapes = -> [Cylinder050,Cylinder051]
FEATURE [Sketcher::SketchObject] Sketch067  label="topSketch018"
  FullyConstrained = true
  sketch-geometry (4):
    g0: LineSegment StartX=16.8446 StartY=31.512 StartZ=0 EndX=16.3251 EndY=34.4666 EndZ=0
    g1: ArcOfCircle CenterX=19 CenterY=19.2524 CenterZ=0 NormalX=0 NormalY=0 NormalZ=1 AngleXU=0 Radius=15.4476 StartAngle=1.74483 EndAngle=2.72717
    g2: ArcOfCircle CenterX=19 CenterY=19.2524 CenterZ=0 NormalX=0 NormalY=0 NormalZ=1 AngleXU=0 Radius=12.4476 StartAngle=1.74483 EndAngle=2.73189
    g3: LineSegment StartX=4.86004 StartY=25.4725 StartZ=0 EndX=7.58253 EndY=24.2107 EndZ=0
  constraints (7):
    c: Block(g0)
    c: Coincident(g1,g0)
    c: Coincident(g2,g0)
    c: Coincident(g3,g1)
    c: Coincident(g3,g2)
    c: Block(g1)
    c: Block(g2)
FEATURE [Part::Extrusion] Extrude058
  Base = -> Sketch067
  Dir = (0,0,1)
  DirMode = 2
  FaceMakerClass = Part::FaceMakerBullseye
  LengthFwd = 10
  LengthRev = 0
  Placement = pos=(0,0,31) rot=(0,0,1;0rad)
  Solid = true
  Symmetric = false
FEATURE [Part::Cut] Cut051
  Base = -> Extrude058
  Tool = -> Fusion120
FEATURE [Part::Fillet] Fillet049
  Base = -> Cut051
  Edges = 1 edges r=2: [Edge1]
FEATURE [Part::Fillet] Fillet050
  Base = -> Fillet049
  Edges = 1 edges r=2.5: [Edge1]
FEATURE [Part::Fillet] Fillet051
  Base = -> Fillet050
  Edges = 1 edges r=2.5: [Edge2]
FEATURE [Part::MultiFuse] Fusion121  label="wireHolder003"
  Shapes = -> [Fusion116,Fillet051]
FEATURE [Part::MultiFuse] Fusion122
  Shapes = -> [Fillet045,Fusion121]
FEATURE [Part::MultiFuse] Fusion123  label="wireHolder004"
  Shapes = -> [Fusion122,Fillet048]
FEATURE [Part::MultiFuse] Fusion124  label="wireHolder005"
  Shapes = -> [Fillet044,Fusion119,Fusion123]
FEATURE [Sketcher::SketchObject] Sketch068  label="topSketch019"
  FullyConstrained = true
  sketch-geometry (6):
    g0: LineSegment StartX=19 StartY=38 StartZ=0 EndX=117 EndY=38 EndZ=0
    g1: ArcOfCircle CenterX=19 CenterY=19 CenterZ=0 NormalX=0 NormalY=0 NormalZ=1 AngleXU=0 Radius=19 StartAngle=1.5708 EndAngle=3.14159
    g2: LineSegment StartX=117 StartY=38 StartZ=0 EndX=117 EndY=19 EndZ=0
    g3: LineSegment StartX=98 StartY=1.0161e-12 StartZ=0 EndX=5.22862e-06 EndY=1.0161e-12 EndZ=0
    g4: LineSegment StartX=5.22862e-06 StartY=19 StartZ=0 EndX=5.22862e-06 EndY=1.0161e-12 EndZ=0
    g5: ArcOfCircle CenterX=98 CenterY=19 CenterZ=0 NormalX=0 NormalY=0 NormalZ=1 AngleXU=0 Radius=19 StartAngle=4.71239 EndAngle=6.28319
  constraints (16):
    c: Horizontal(g0)
    c: Distance(g0) = 98
    c: Coincident(g1,g0)
    c: Block(g1)
    c: Coincident(g2,g0)
    c: Vertical(g2)
    c: Distance(g2) = 19
    c: Horizontal(g3)
    c: Coincident(g4,g1)
    c: Vertical(g4)
    c: Coincident(g3,g4)
    c: Block(g3)
    c: Coincident(g5,g2)
    c: Coincident(g5,g3)
    c: Block(g0)
    c: Block(g5)
FEATURE [Part::Extrusion] Extrude059  label="sideA002"
  Base = -> Sketch068
  Dir = (0,0,1)
  DirMode = 2
  FaceMakerClass = Part::FaceMakerBullseye
  LengthFwd = 3
  LengthRev = 0
  Placement = pos=(0,0,-2.7) rot=(0,0,1;0rad)
  Solid = true
  Symmetric = false
FEATURE [Sketcher::SketchObject] Sketch069  label="topSketch020"
  FullyConstrained = true
  sketch-geometry (6):
    g0: LineSegment StartX=19 StartY=38 StartZ=0 EndX=117 EndY=38 EndZ=0
    g1: ArcOfCircle CenterX=19 CenterY=19 CenterZ=0 NormalX=0 NormalY=0 NormalZ=1 AngleXU=0 Radius=19 StartAngle=1.5708 EndAngle=3.14159
    g2: LineSegment StartX=117 StartY=38 StartZ=0 EndX=117 EndY=19 EndZ=0
    g3: LineSegment StartX=98 StartY=1.0161e-12 StartZ=0 EndX=5.22862e-06 EndY=1.0161e-12 EndZ=0
    g4: LineSegment StartX=5.22862e-06 StartY=19 StartZ=0 EndX=5.22862e-06 EndY=1.0161e-12 EndZ=0
    g5: ArcOfCircle CenterX=98 CenterY=19 CenterZ=0 NormalX=0 NormalY=0 NormalZ=1 AngleXU=0 Radius=19 StartAngle=4.71239 EndAngle=6.28319
  constraints (16):
    c: Horizontal(g0)
    c: Distance(g0) = 98
    c: Coincident(g1,g0)
    c: Block(g1)
    c: Coincident(g2,g0)
    c: Vertical(g2)
    c: Distance(g2) = 19
    c: Horizontal(g3)
    c: Coincident(g4,g1)
    c: Vertical(g4)
    c: Coincident(g3,g4)
    c: Block(g3)
    c: Coincident(g5,g2)
    c: Coincident(g5,g3)
    c: Block(g0)
    c: Block(g5)
FEATURE [Part::Extrusion] Extrude060  label="sideB002"
  Base = -> Sketch069
  Dir = (0,0,1)
  DirMode = 2
  FaceMakerClass = Part::FaceMakerBullseye
  LengthFwd = 3
  LengthRev = 0
  Placement = pos=(0,0,71.7) rot=(0,0,1;0rad)
  Solid = true
  Symmetric = false
FEATURE [Part::MultiFuse] Fusion127  label="removeFromBottom001"
  Placement = pos=(2,0,0) rot=(0,0,1;0rad)
  Shapes = -> [Extrude059,Extrude060]
FEATURE [Part::Cylinder] Cylinder052
  Angle = 360
  AttacherType = Attacher::AttachEngine3D
  Height = 20
  Placement = pos=(0,0,36.15) rot=(0,0,1;0rad)
  Radius = 14
FEATURE [Part::Cylinder] Cylinder053
  Angle = 360
  AttacherType = Attacher::AttachEngine3D
  Height = 10
  Placement = pos=(0,0,36.15) rot=(0,0,1;0rad)
  Radius = 4
FEATURE [Part::MultiFuse] Fusion128  label="removeToCreteHoleForPlugHousing044"
  Placement = pos=(70,19,36) rot=(0,1,0;1.5708rad)
  Shapes = -> [Cylinder052,Cylinder053]
FEATURE [Part::Cut] Cut052  label="bottom011"
  Base = -> Extrude043
  Tool = -> Fusion128
FEATURE [Part::Cut] Cut054  label="bottom012"
  Base = -> Cut052
  Tool = -> Fusion115
FEATURE [Sketcher::SketchObject] Sketch070
  FullyConstrained = true
  Placement = pos=(117,19,0) rot=(0.57735,0.57735,0.57735;2.0944rad)
  sketch-geometry (48):
    g0: LineSegment StartX=-49.19 StartY=69.25 StartZ=0 EndX=-49.19 EndY=66.25 EndZ=0
    g1: LineSegment StartX=-49.19 StartY=63.5 StartZ=0 EndX=-49.19 EndY=60.5 EndZ=0
    g2: LineSegment StartX=-49.19 StartY=57.75 StartZ=0 EndX=-49.19 EndY=54.75 EndZ=0
    g3: LineSegment StartX=-49.19 StartY=52 StartZ=0 EndX=-49.19 EndY=49 EndZ=0
    g4: LineSegment StartX=-49.19 StartY=46.25 StartZ=0 EndX=-49.19 EndY=43.25 EndZ=0
    g5: LineSegment StartX=-49.19 StartY=40.5 StartZ=0 EndX=-49.19 EndY=37.5 EndZ=0
    g6: LineSegment StartX=-49.19 StartY=34.5 StartZ=0 EndX=-49.19 EndY=31.5 EndZ=0
    g7: LineSegment StartX=-49.19 StartY=28.75 StartZ=0 EndX=-49.19 EndY=25.75 EndZ=0
    g8: LineSegment StartX=-49.19 StartY=23 StartZ=0 EndX=-49.19 EndY=20 EndZ=0
    g9: LineSegment StartX=-49.19 StartY=17.25 StartZ=0 EndX=-49.19 EndY=14.25 EndZ=0
    g10: LineSegment StartX=-49.19 StartY=11.5 StartZ=0 EndX=-49.19 EndY=8.5 EndZ=0
    g11: LineSegment StartX=-49.19 StartY=5.75 StartZ=0 EndX=-49.19 EndY=2.75 EndZ=0
    g12: ArcOfCircle CenterX=-1.5 CenterY=67.75 CenterZ=0 NormalX=0 NormalY=0 NormalZ=1 AngleXU=0 Radius=1.5 StartAngle=4.71239 EndAngle=7.85398
    g13: ArcOfCircle CenterX=-1.5 CenterY=62 CenterZ=0 NormalX=0 NormalY=0 NormalZ=1 AngleXU=0 Radius=1.5 StartAngle=4.71239 EndAngle=7.85398
    g14: ArcOfCircle CenterX=-1.5 CenterY=56.25 CenterZ=0 NormalX=0 NormalY=0 NormalZ=1 AngleXU=0 Radius=1.5 StartAngle=4.71239 EndAngle=7.85398
    g15: ArcOfCircle CenterX=-11.49 CenterY=50.5 CenterZ=0 NormalX=0 NormalY=0 NormalZ=1 AngleXU=0 Radius=1.5 StartAngle=4.71239 EndAngle=7.85398
    g16: ArcOfCircle CenterX=-16.28 CenterY=44.75 CenterZ=0 NormalX=0 NormalY=0 NormalZ=1 AngleXU=0 Radius=1.5 StartAngle=4.71239 EndAngle=7.85398
    g17: ArcOfCircle CenterX=-18.2337 CenterY=39 CenterZ=0 NormalX=0 NormalY=0 NormalZ=1 AngleXU=0 Radius=1.5 StartAngle=4.71485 EndAngle=7.85398
    g18: ArcOfCircle CenterX=-16.2837 CenterY=27.25 CenterZ=0 NormalX=0 NormalY=0 NormalZ=1 AngleXU=0 Radius=1.5 StartAngle=4.71485 EndAngle=7.85398
    g19: ArcOfCircle CenterX=-18.2337 CenterY=33 CenterZ=0 NormalX=0 NormalY=0 NormalZ=1 AngleXU=0 Radius=1.5 StartAngle=4.71485 EndAngle=7.85398
    g20: ArcOfCircle CenterX=-11.49 CenterY=21.5 CenterZ=0 NormalX=0 NormalY=0 NormalZ=1 AngleXU=0 Radius=1.5 StartAngle=4.71239 EndAngle=7.85398
    g21: ArcOfCircle CenterX=-1.5 CenterY=4.25 CenterZ=0 NormalX=0 NormalY=0 NormalZ=1 AngleXU=0 Radius=1.5 StartAngle=4.71239 EndAngle=7.85398
    g22: ArcOfCircle CenterX=-1.5 CenterY=10 CenterZ=0 NormalX=0 NormalY=0 NormalZ=1 AngleXU=0 Radius=1.5 StartAngle=4.71239 EndAngle=7.85398
    g23: ArcOfCircle CenterX=-1.5 CenterY=15.75 CenterZ=0 NormalX=0 NormalY=0 NormalZ=1 AngleXU=0 Radius=1.5 StartAngle=4.71239 EndAngle=7.85398
    g24: LineSegment StartX=-49.19 StartY=69.25 StartZ=0 EndX=-1.5 EndY=69.25 EndZ=0
    g25: LineSegment StartX=-49.19 StartY=66.25 StartZ=0 EndX=-1.5 EndY=66.25 EndZ=0
    g26: LineSegment StartX=-49.19 StartY=63.5 StartZ=0 EndX=-1.5 EndY=63.5 EndZ=0
    g27: LineSegment StartX=-49.19 StartY=60.5 StartZ=0 EndX=-1.5 EndY=60.5 EndZ=0
    g28: LineSegment StartX=-49.19 StartY=57.75 StartZ=0 EndX=-1.5 EndY=57.75 EndZ=0
    g29: LineSegment StartX=-49.19 StartY=54.75 StartZ=0 EndX=-1.5 EndY=54.75 EndZ=0
    g30: LineSegment StartX=-49.19 StartY=52 StartZ=0 EndX=-11.49 EndY=52 EndZ=0
    g31: LineSegment StartX=-49.19 StartY=49 StartZ=0 EndX=-11.49 EndY=49 EndZ=0
    g32: LineSegment StartX=-49.19 StartY=46.25 StartZ=0 EndX=-16.28 EndY=46.25 EndZ=0
    g33: LineSegment StartX=-49.19 StartY=43.25 StartZ=0 EndX=-16.28 EndY=43.25 EndZ=0
    g34: LineSegment StartX=-49.19 StartY=40.5 StartZ=0 EndX=-18.2337 EndY=40.5 EndZ=0
    g35: LineSegment StartX=-49.19 StartY=37.5 StartZ=0 EndX=-18.23 EndY=37.5 EndZ=0
    g36: LineSegment StartX=-49.19 StartY=34.5 StartZ=0 EndX=-18.2337 EndY=34.5 EndZ=0
    g37: LineSegment StartX=-49.19 StartY=31.5 StartZ=0 EndX=-18.23 EndY=31.5 EndZ=0
    g38: LineSegment StartX=-49.19 StartY=28.75 StartZ=0 EndX=-16.2837 EndY=28.75 EndZ=0
    g39: LineSegment StartX=-49.19 StartY=25.75 StartZ=0 EndX=-16.28 EndY=25.75 EndZ=0
    g40: LineSegment StartX=-49.19 StartY=23 StartZ=0 EndX=-11.49 EndY=23 EndZ=0
    g41: LineSegment StartX=-49.19 StartY=20 StartZ=0 EndX=-11.49 EndY=20 EndZ=0
    g42: LineSegment StartX=-49.19 StartY=17.25 StartZ=0 EndX=-1.5 EndY=17.25 EndZ=0
    g43: LineSegment StartX=-49.19 StartY=14.25 StartZ=0 EndX=-1.5 EndY=14.25 EndZ=0
    g44: LineSegment StartX=-49.19 StartY=11.5 StartZ=0 EndX=-1.5 EndY=11.5 EndZ=0
    g45: LineSegment StartX=-49.19 StartY=8.5 StartZ=0 EndX=-1.5 EndY=8.5 EndZ=0
    g46: LineSegment StartX=-49.19 StartY=5.75 StartZ=0 EndX=-1.5 EndY=5.75 EndZ=0
    g47: LineSegment StartX=-49.19 StartY=2.75 StartZ=0 EndX=-1.5 EndY=2.75 EndZ=0
  constraints (120):
    c: Vertical(g0)
    c: Distance(g0) = 3
    c: Block(g0)
    c: Vertical(g1)
    c: Distance(g1) = 3
    c: Vertical(g2)
    c: Equal(g0,g2) = 3
    c: Block(g2)
    c: Vertical(g3)
    c: Equal(g1,g3) = 3
    c: Vertical(g4)
    c: Equal(g0,g4) = 3
    c: Block(g4)
    c: Vertical(g5)
    c: Equal(g1,g5) = 3
    c: Vertical(g6)
    c: Equal(g0,g6) = 3
    c: Block(g6)
    c: Vertical(g7)
    c: Equal(g1,g7) = 3
    c: Vertical(g8)
    c: Equal(g0,g8) = 3
    c: Block(g8)
    c: Vertical(g9)
    c: Equal(g1,g9) = 3
    c: Vertical(g10)
    c: Equal(g0,g10) = 3
    c: Block(g10)
    c: Vertical(g11)
    c: Equal(g1,g11) = 3
    c: Block(g12)
    c: Block(g13)
    c: Block(g14)
    c: Block(g15)
    c: Block(g16)
    c: Block(g17)
    c: Block(g18)
    c: Block(g19)
    c: Block(g20)
    c: Block(g21)
    c: Block(g22)
    c: Block(g23)
    c: Block(g11)
    c: Block(g9)
    c: Block(g7)
    c: Block(g5)
    c: Block(g3)
    c: Block(g1)
    c: Coincident(g24,g0)
    c: Coincident(g24,g12)
    c: Horizontal(g24)
    c: Coincident(g25,g0)
    c: Coincident(g25,g12)
    c: Horizontal(g25)
    c: Coincident(g26,g1)
    c: Coincident(g26,g13)
    c: Horizontal(g26)
    c: Coincident(g27,g1)
    c: Coincident(g27,g13)
    c: Horizontal(g27)
    c: Coincident(g28,g2)
    c: Coincident(g28,g14)
    c: Horizontal(g28)
    c: Coincident(g29,g2)
    c: Coincident(g29,g14)
    c: Horizontal(g29)
    c: Coincident(g30,g3)
    c: Coincident(g30,g15)
    c: Horizontal(g30)
    c: Coincident(g31,g3)
    c: Coincident(g31,g15)
    c: Horizontal(g31)
    c: Coincident(g32,g4)
    c: Coincident(g32,g16)
    c: Horizontal(g32)
    c: Coincident(g33,g4)
    c: Coincident(g33,g16)
    c: Horizontal(g33)
    c: Coincident(g34,g5)
    c: Coincident(g34,g17)
    c: Horizontal(g34)
    c: Coincident(g35,g5)
    c: Coincident(g35,g17)
    c: Horizontal(g35)
    c: Coincident(g36,g6)
    c: Coincident(g36,g19)
    c: Horizontal(g36)
    c: Coincident(g37,g6)
    c: Coincident(g37,g19)
    c: Horizontal(g37)
    c: Coincident(g38,g7)
    c: Coincident(g38,g18)
    c: Horizontal(g38)
    c: Coincident(g39,g7)
    c: Coincident(g39,g18)
    c: Horizontal(g39)
    c: Coincident(g40,g8)
    c: Coincident(g40,g20)
    c: Horizontal(g40)
    c: Coincident(g41,g8)
    c: Coincident(g41,g20)
    c: Horizontal(g41)
    c: Coincident(g42,g9)
    c: Coincident(g42,g23)
    c: Horizontal(g42)
    c: Coincident(g43,g9)
    c: Coincident(g43,g23)
    c: Horizontal(g43)
    c: Coincident(g44,g10)
    c: Coincident(g44,g22)
    c: Horizontal(g44)
    c: Coincident(g45,g10)
    c: Coincident(g45,g22)
    c: Horizontal(g45)
    c: Coincident(g46,g11)
    c: Coincident(g46,g21)
    c: Horizontal(g46)
    c: Coincident(g47,g11)
    c: Coincident(g47,g21)
    c: Horizontal(g47)
FEATURE [Part::Extrusion] Extrude061
  Base = -> Sketch070
  Dir = (1,0,0)
  DirMode = 2
  FaceMakerClass = Part::FaceMakerBullseye
  LengthFwd = 23
  LengthRev = 0
  Placement = pos=(-19,0,0) rot=(0,0,1;0rad)
  Solid = true
  Symmetric = false
FEATURE [Part::Fillet] Fillet052  label="removeToCreateVentalationHoles002"
  Base = -> Extrude061
  Edges = <same value as first occurrence — deduplicated (x6 in doc)>
  Placement = pos=(7,0.02,0) rot=(0,0,1;0rad)
FEATURE [Part::MultiFuse] Fusion130  label="bottom013"
  Shapes = -> [Cut054,Cut034]
FEATURE [Part::Cut] Cut055
  Base = -> Fusion130
  Tool = -> Fillet052
FEATURE [Part::Cylinder] Cylinder054
  Angle = 360
  AttacherType = Attacher::AttachEngine3D
  Height = 20
  Placement = pos=(0,0,36.15) rot=(0,0,1;0rad)
  Radius = 4
FEATURE [Sketcher::SketchObject] Sketch071  label="bottomSketch002"
  FullyConstrained = true
  sketch-geometry (32):
    g0: LineSegment StartX=3.3 StartY=-6.03275e-07 StartZ=0 EndX=98 EndY=-6.03275e-07 EndZ=0
    g1: ArcOfCircle CenterX=98 CenterY=19 CenterZ=0 NormalX=0 NormalY=0 NormalZ=1 AngleXU=0 Radius=19 StartAngle=4.71239 EndAngle=5.71103
    g2: LineSegment StartX=6.3 StartY=8 StartZ=0 EndX=3.3 EndY=8 EndZ=0
    g3: LineSegment StartX=3.3 StartY=8 StartZ=0 EndX=3.3 EndY=-6.03275e-07 EndZ=0
    g4: ArcOfCircle CenterX=8.3 CenterY=5 CenterZ=0 NormalX=0 NormalY=0 NormalZ=1 AngleXU=0 Radius=2 StartAngle=3.14159 EndAngle=4.71239
    g5: LineSegment StartX=6.3 StartY=8 StartZ=0 EndX=6.3 EndY=5 EndZ=0
    g6: ArcOfCircle CenterX=98 CenterY=19 CenterZ=0 NormalX=0 NormalY=0 NormalZ=1 AngleXU=0 Radius=12.7 StartAngle=4.71239 EndAngle=6.28319
    g7: LineSegment StartX=94.7 StartY=3 StartZ=0 EndX=8.3 EndY=3 EndZ=0
    g8-g12: Circle x5 (B-spline internal-alignment scaffolding for g13; pole/knot coordinates omitted)
    g13: BSplineCurve PolesCount=5 KnotsCount=3 Degree=3 IsPeriodic=0
    g14: GeomPoint X=98 Y=6.3 Z=0
    g15: GeomPoint X=96.3938 Y=4.71946 Z=0
    g16: GeomPoint X=94.7 Y=3 Z=0
    g17-g23: Circle x7 (B-spline internal-alignment scaffolding for g24; pole/knot coordinates omitted)
    g24: BSplineCurve PolesCount=7 KnotsCount=5 Degree=3 IsPeriodic=0
    g25-g29: GeomPoint x5 (B-spline internal-alignment scaffolding for g24; pole/knot coordinates omitted)
    g30: ArcOfCircle CenterX=98 CenterY=19 CenterZ=0 NormalX=0 NormalY=0 NormalZ=1 AngleXU=0 Radius=15.7 StartAngle=5.81226 EndAngle=6.28319
    g31: LineSegment StartX=110.7 StartY=19 StartZ=0 EndX=113.7 EndY=19 EndZ=0
  constraints (41):
    c: Horizontal(g0)
    c: Coincident(g1,g0)
    c: Block(g1)
    c: Horizontal(g2)
    c: Distance(g2) = 3
    c: Coincident(g3,g2)
    c: Vertical(g3)
    c: Coincident(g3,g0)
    c: Block(g4)
    c: Block(g2)
    c: Coincident(g5,g2)
    c: Coincident(g5,g4)
    c: Vertical(g5)
    c: Coincident(g6,g1)
    c: Block(g6)
    c: Coincident(g7,g4)
    c: Horizontal(g7)
    c: Block(g0)
    c: Block(g7)
    c: Block(g3)
    c: Coincident(g13,g6)
    c: Weight(g8) = 1
    c: Equal(g8, g9-g12) x4
    c: Coincident(g13,g7)
    c: InternalAlignment(g8-g12 -> g13) x5
    c: InternalAlignment(g14,g13)
    c: InternalAlignment(g15,g13)
    c: InternalAlignment(g16,g13)
    c: Block(g13)
    c: Weight(g17) = 1
    c: Equal(g17, g18-g23) x6
    c: Coincident(g24,g1)
    c: InternalAlignment(g17-g23 -> g24) x7
    c: InternalAlignment(g25-g29 -> g24) x5
    c: Block(g24)
    c: Coincident(g30,g24)
    c: Coincident(g31,g6)
    c: Coincident(g31,g30)
    c: Horizontal(g31)
    c: Block(g31)
    c: Block(g30)
FEATURE [Part::Extrusion] Extrude062  label="bottom014"
  Base = -> Sketch071
  Dir = (0,0,1)
  DirMode = 2
  FaceMakerClass = Part::FaceMakerBullseye
  LengthFwd = 71.4
  LengthRev = 0
  Placement = pos=(0,0,0.3) rot=(0,0,1;0rad)
  Solid = true
  Symmetric = false
FEATURE [Part::Fillet] Fillet054
  Base = -> Extrude062
  Edges = 1 edges r=2.4: [Edge17]
FEATURE [Part::Fillet] Fillet055  label="bottom015"
  Base = -> Fillet054
  Edges = 1 edges r=2.4: [Edge36]
FEATURE [Part::Cylinder] Cylinder055
  Angle = 360
  AttacherType = Attacher::AttachEngine3D
  Height = 10
  Placement = pos=(0,0,36.15) rot=(0,0,1;0rad)
  Radius = 4
FEATURE [Part::MultiFuse] Fusion131  label="removeToCreateHoleForPlugHousing002"
  Placement = pos=(70,19,36.15) rot=(0,1,0;1.5708rad)
  Shapes = -> [Cylinder054,Cylinder055]
FEATURE [Part::Cut] Cut056  label="Bottom001"
  Base = -> Fillet055
  Placement = pos=(9,0,0) rot=(0,0,1;0rad)
  Tool = -> Fusion131
FEATURE [Part::Cut] Cut057
  Base = -> Cut055
  Tool = -> Cut056
FEATURE [Sketcher::SketchObject] Sketch072  label="topSketch021"
  FullyConstrained = true
  sketch-geometry (4):
    g0: ArcOfCircle CenterX=105 CenterY=19 CenterZ=0 NormalX=0 NormalY=0 NormalZ=1 AngleXU=0 Radius=20.6155 StartAngle=5.54125 EndAngle=6.28319
    g1: ArcOfCircle CenterX=105 CenterY=19 CenterZ=0 NormalX=0 NormalY=0 NormalZ=1 AngleXU=0 Radius=13 StartAngle=5.54125 EndAngle=6.28319
    g2: LineSegment StartX=118 StartY=19 StartZ=0 EndX=125.616 EndY=19 EndZ=0
    g3: LineSegment StartX=114.583 StartY=10.2157 StartZ=0 EndX=120.197 EndY=5.06982 EndZ=0
  constraints (7):
    c: Block(g0)
    c: Block(g1)
    c: Coincident(g2,g1)
    c: Coincident(g2,g0)
    c: Horizontal(g2)
    c: Coincident(g3,g1)
    c: Coincident(g3,g0)
FEATURE [Part::Extrusion] Extrude063  label="bottomPlugHousingBit003"
  Base = -> Sketch072
  Dir = (0,0,1)
  DirMode = 2
  FaceMakerClass = Part::FaceMakerBullseye
  LengthFwd = 72
  LengthRev = 0
  Solid = true
  Symmetric = false
FEATURE [Part::Cylinder] Cylinder056
  Angle = 360
  AttacherType = Attacher::AttachEngine3D
  Height = 20
  Placement = pos=(0,0,36.15) rot=(0,0,1;0rad)
  Radius = 14.3
FEATURE [Part::Cylinder] Cylinder057
  Angle = 360
  AttacherType = Attacher::AttachEngine3D
  Height = 10
  Placement = pos=(0,0,36.15) rot=(0,0,1;0rad)
  Radius = 4
FEATURE [Part::Box] Box034  label="removeToCreteHoleForPlugHousing047"
  AttacherType = Attacher::AttachEngine3D
  Height = 28.6
  Length = 20
  Placement = pos=(106.15,0,21.7) rot=(0,0,1;0rad)
  Width = 19
FEATURE [Part::Cylinder] Cylinder058
  Angle = 360
  AttacherType = Attacher::AttachEngine3D
  Height = 20
  Placement = pos=(0,0,36.15) rot=(0,0,1;0rad)
  Radius = 14.3
FEATURE [Part::Cylinder] Cylinder059
  Angle = 360
  AttacherType = Attacher::AttachEngine3D
  Height = 10
  Placement = pos=(0,0,36.15) rot=(0,0,1;0rad)
  Radius = 4
FEATURE [Part::MultiFuse] Fusion134  label="removeToCreteHoleForPlugHousing046"
  Placement = pos=(70,19,36) rot=(0,1,0;1.5708rad)
  Shapes = -> [Cylinder058,Cylinder059]
FEATURE [Part::Cylinder] Cylinder060
  Angle = 360
  AttacherType = Attacher::AttachEngine3D
  Height = 20
  Placement = pos=(0,0,36.15) rot=(0,0,1;0rad)
  Radius = 14
FEATURE [Part::Cylinder] Cylinder061
  Angle = 360
  AttacherType = Attacher::AttachEngine3D
  Height = 10
  Placement = pos=(0,0,36.15) rot=(0,0,1;0rad)
  Radius = 4
FEATURE [Part::MultiFuse] Fusion135  label="removeToCreteHoleForPlugHousing048"
  Placement = pos=(70,19,36) rot=(0,1,0;1.5708rad)
  Shapes = -> [Cylinder060,Cylinder061]
FEATURE [Part::Box] Box035  label="removeToCreteHoleForPlugHousing049"
  AttacherType = Attacher::AttachEngine3D
  Height = 28.6
  Length = 20
  Placement = pos=(106.15,0,21.7) rot=(0,0,1;0rad)
  Width = 19
FEATURE [Part::MultiFuse] Fusion133  label="removeToCreteHoleForPlugHousing045"
  Placement = pos=(0,0,-28.3) rot=(0,0,1;0rad)
  Shapes = -> [Box035,Fusion134]
FEATURE [Part::MultiFuse] Fusion138  label="removeToCreteHoleForPlugHousing051"
  Placement = pos=(70,19,36) rot=(0,1,0;1.5708rad)
  Shapes = -> [Cylinder056,Cylinder057]
FEATURE [Part::MultiFuse] Fusion137  label="removeToCreteHoleForPlugHousing050"
  Placement = pos=(0,0,28.3) rot=(0,0,1;0rad)
  Shapes = -> [Box034,Fusion138]
FEATURE [Part::MultiFuse] Fusion132  label="removeToCreatePlugHousingBottomBit002"
  Shapes = -> [Fusion133,Fusion137]
FEATURE [Part::MultiFuse] Fusion136  label="removeToCreatePlugHousingBottomBit003"
  Shapes = -> [Fusion135,Fusion132]
FEATURE [Part::Cut] Cut058  label="bottomPlugHousingBit002"
  Base = -> Extrude063
  Placement = pos=(-0.09,0,0) rot=(0,0,1;0rad)
  Tool = -> Fusion136
FEATURE [Sketcher::SketchObject] Sketch073  label="bottomSketch003"
  FullyConstrained = true
  sketch-geometry (45):
    g0: LineSegment StartX=6.29999 StartY=8 StartZ=0 EndX=3.29999 EndY=8 EndZ=0
    g1: LineSegment StartX=3.29999 StartY=8 StartZ=0 EndX=3.29999 EndY=-6.03275e-07 EndZ=0
    g2: ArcOfCircle CenterX=8.29999 CenterY=5 CenterZ=0 NormalX=0 NormalY=0 NormalZ=1 AngleXU=0 Radius=2 StartAngle=3.14159 EndAngle=4.71239
    g3: LineSegment StartX=6.29999 StartY=8 StartZ=0 EndX=6.29999 EndY=5 EndZ=0
    g4: ArcOfCircle CenterX=105 CenterY=19 CenterZ=0 NormalX=0 NormalY=0 NormalZ=1 AngleXU=0 Radius=12.7 StartAngle=4.71239 EndAngle=5.94289
    g5-g11: Circle x7 (B-spline internal-alignment scaffolding for g12; pole/knot coordinates omitted)
    g12: BSplineCurve PolesCount=7 KnotsCount=5 Degree=3 IsPeriodic=0
    g13-g17: GeomPoint x5 (B-spline internal-alignment scaffolding for g12; pole/knot coordinates omitted)
    g18: ArcOfCircle CenterX=105 CenterY=19 CenterZ=0 NormalX=0 NormalY=0 NormalZ=1 AngleXU=0 Radius=15.7 StartAngle=5.81226 EndAngle=6.28319
    g19: BSplineCurve PolesCount=5 KnotsCount=3 Degree=3 IsPeriodic=0
    g20: LineSegment StartX=8.29999 StartY=3 StartZ=0 EndX=101.7 EndY=3 EndZ=0
    g21: LineSegment StartX=3.29999 StartY=-6.03275e-07 StartZ=0 EndX=105 EndY=-6.03275e-07 EndZ=0
    g22: LineSegment StartX=120.974 StartY=8.71251 StartZ=0 EndX=122.332 EndY=7.83778 EndZ=0
    g23: LineSegment StartX=105 StartY=-6.03274e-07 StartZ=0 EndX=113 EndY=-6.03274e-07 EndZ=0
    g24: ArcOfCircle CenterX=105 CenterY=19 CenterZ=0 NormalX=0 NormalY=0 NormalZ=1 AngleXU=0 Radius=20.6155 StartAngle=5.11091 EndAngle=5.71103
    g25: ArcOfCircle CenterX=117.7 CenterY=19 CenterZ=0 NormalX=0 NormalY=0 NormalZ=1 AngleXU=0 Radius=3 StartAngle=1.2e-15 EndAngle=2.10468
    g26: Circle CenterX=116.345 CenterY=16.3232 CenterZ=0 NormalX=0 NormalY=0 NormalZ=1 AngleXU=0 Radius=1
    g27: Circle CenterX=117.24 CenterY=15.7584 CenterZ=0 NormalX=0 NormalY=0 NormalZ=1 AngleXU=0 Radius=1
    g28: Circle CenterX=116.972 CenterY=14.7612 CenterZ=0 NormalX=0 NormalY=0 NormalZ=1 AngleXU=0 Radius=1
    g29: BSplineCurve PolesCount=3 KnotsCount=2 Degree=2 IsPeriodic=0
    g30: GeomPoint X=116.345 Y=16.3232 Z=0
    g31: GeomPoint X=116.972 Y=14.7612 Z=0
    g32: Circle CenterX=115.828 CenterY=17.157 CenterZ=0 NormalX=0 NormalY=0 NormalZ=1 AngleXU=0 Radius=1
    g33: Circle CenterX=115.841 CenterY=16.639 CenterZ=0 NormalX=0 NormalY=0 NormalZ=1 AngleXU=0 Radius=1
    g34: Circle CenterX=116.345 CenterY=16.3232 CenterZ=0 NormalX=0 NormalY=0 NormalZ=1 AngleXU=0 Radius=1
    g35: BSplineCurve PolesCount=3 KnotsCount=2 Degree=2 IsPeriodic=0
    g36: GeomPoint X=115.828 Y=17.157 Z=0
    g37: GeomPoint X=116.345 Y=16.3232 Z=0
    g38: LineSegment StartX=115.828 StartY=17.157 StartZ=0 EndX=115.828 EndY=20.8307 EndZ=0
    g39: Circle CenterX=115.828 CenterY=20.8307 CenterZ=0 NormalX=0 NormalY=0 NormalZ=1 AngleXU=0 Radius=1
    g40: Circle CenterX=115.831 CenterY=21.3396 CenterZ=0 NormalX=0 NormalY=0 NormalZ=1 AngleXU=0 Radius=1
    g41: Circle CenterX=116.173 CenterY=21.5825 CenterZ=0 NormalX=0 NormalY=0 NormalZ=1 AngleXU=0 Radius=1
    g42: BSplineCurve PolesCount=3 KnotsCount=2 Degree=2 IsPeriodic=0
    g43: GeomPoint X=115.828 Y=20.8307 Z=0
    g44: GeomPoint X=116.173 Y=21.5825 Z=0
  constraints (70):
    c: Horizontal(g0)
    c: Distance(g0) = 3
    c: Coincident(g1,g0)
    c: Vertical(g1)
    c: Block(g2)
    c: Block(g0)
    c: Coincident(g3,g0)
    c: Coincident(g3,g2)
    c: Vertical(g3)
    c: Block(g1)
    c: Block(g4)
    c: Coincident(g19,g4)
    c: Block(g19)
    c: Equal(g5, g6-g11) x6
    c: InternalAlignment(g5-g11 -> g12) x7
    c: InternalAlignment(g13-g17 -> g12) x5
    c: Block(g12)
    c: Coincident(g18,g12)
    c: Block(g18)
    c: Coincident(g20,g2)
    c: Coincident(g20,g19)
    c: Horizontal(g20)
    c: Distance(g20) = 93.4
    c: Coincident(g21,g1)
    c: Horizontal(g21)
    c: Distance(g21) = 101.7
    c: Horizontal(g23)
    c: Distance(g23) = 8
    c: Coincident(g24,g23)
    c: Block(g23)
    c: Coincident(g22,g24)
    c: Block(g24)
    c: Block(g22)
    c: Distance(g22) = 1.61553
    c: Coincident(g25,g18)
    c: Block(g25)
    c: Weight(g26) = 1
    c: Equal(g26,g27)
    c: Equal(g26,g28)
    c: Coincident(g29,g4)
    c: InternalAlignment(g26,g29)
    c: InternalAlignment(g27,g29)
    c: InternalAlignment(g28,g29)
    c: InternalAlignment(g30,g29)
    c: InternalAlignment(g31,g29)
    c: Block(g29)
    c: Weight(g32) = 1
    c: Equal(g32,g33)
    c: Equal(g32,g34)
    c: Coincident(g35,g29)
    c: InternalAlignment(g32,g35)
    c: InternalAlignment(g33,g35)
    c: InternalAlignment(g34,g35)
    c: InternalAlignment(g36,g35)
    c: InternalAlignment(g37,g35)
    c: Block(g35)
    c: Coincident(g38,g35)
    c: Vertical(g38)
    c: Block(g38)
    c: Coincident(g42,g38)
    c: Weight(g39) = 1
    c: Equal(g39,g40)
    c: Equal(g39,g41)
    c: Coincident(g42,g25)
    c: InternalAlignment(g39,g42)
    c: InternalAlignment(g40,g42)
    c: InternalAlignment(g41,g42)
    c: InternalAlignment(g43,g42)
    c: InternalAlignment(g44,g42)
    c: Block(g42)
FEATURE [Part::Extrusion] Extrude064  label="bottom016"
  Base = -> Sketch073
  Dir = (0,0,1)
  DirMode = 2
  FaceMakerClass = Part::FaceMakerBullseye
  LengthFwd = 71.4
  LengthRev = 0
  Placement = pos=(0,0,0.3) rot=(0,0,1;0rad)
  Solid = true
  Symmetric = false
FEATURE [Part::Revolution] Revolve157  label="removeToCreateScrewAndThreadedInsertHole063"
  Angle = 360
  Axis = (0,1,0)
  Base = (0,0,0)
  FaceMakerClass = Part::FaceMakerBullseye
  Placement = pos=(12.5,0,10) rot=(0,0,1;0rad)
  Solid = false
  Source = -> Face141
  Symmetric = false
FEATURE [Sketcher::SketchObject] Sketch074
  FullyConstrained = true
  Placement = pos=(117,19,0) rot=(0.57735,0.57735,0.57735;2.0944rad)
  sketch-geometry (48):
    g0: LineSegment StartX=-49.19 StartY=69.25 StartZ=0 EndX=-49.19 EndY=66.25 EndZ=0
    g1: LineSegment StartX=-49.19 StartY=63.5 StartZ=0 EndX=-49.19 EndY=60.5 EndZ=0
    g2: LineSegment StartX=-49.19 StartY=57.75 StartZ=0 EndX=-49.19 EndY=54.75 EndZ=0
    g3: LineSegment StartX=-49.19 StartY=52 StartZ=0 EndX=-49.19 EndY=49 EndZ=0
    g4: LineSegment StartX=-49.19 StartY=46.25 StartZ=0 EndX=-49.19 EndY=43.25 EndZ=0
    g5: LineSegment StartX=-49.19 StartY=40.5 StartZ=0 EndX=-49.19 EndY=37.5 EndZ=0
    g6: LineSegment StartX=-49.19 StartY=34.5 StartZ=0 EndX=-49.19 EndY=31.5 EndZ=0
    g7: LineSegment StartX=-49.19 StartY=28.75 StartZ=0 EndX=-49.19 EndY=25.75 EndZ=0
    g8: LineSegment StartX=-49.19 StartY=23 StartZ=0 EndX=-49.19 EndY=20 EndZ=0
    g9: LineSegment StartX=-49.19 StartY=17.25 StartZ=0 EndX=-49.19 EndY=14.25 EndZ=0
    g10: LineSegment StartX=-49.19 StartY=11.5 StartZ=0 EndX=-49.19 EndY=8.5 EndZ=0
    g11: LineSegment StartX=-49.19 StartY=5.75 StartZ=0 EndX=-49.19 EndY=2.75 EndZ=0
    g12: ArcOfCircle CenterX=-1.5 CenterY=67.75 CenterZ=0 NormalX=0 NormalY=0 NormalZ=1 AngleXU=0 Radius=1.5 StartAngle=4.71239 EndAngle=7.85398
    g13: ArcOfCircle CenterX=-1.5 CenterY=62 CenterZ=0 NormalX=0 NormalY=0 NormalZ=1 AngleXU=0 Radius=1.5 StartAngle=4.71239 EndAngle=7.85398
    g14: ArcOfCircle CenterX=-1.5 CenterY=56.25 CenterZ=0 NormalX=0 NormalY=0 NormalZ=1 AngleXU=0 Radius=1.5 StartAngle=4.71239 EndAngle=7.85398
    g15: ArcOfCircle CenterX=-11.49 CenterY=50.5 CenterZ=0 NormalX=0 NormalY=0 NormalZ=1 AngleXU=0 Radius=1.5 StartAngle=4.71239 EndAngle=7.85398
    g16: ArcOfCircle CenterX=-16.28 CenterY=44.75 CenterZ=0 NormalX=0 NormalY=0 NormalZ=1 AngleXU=0 Radius=1.5 StartAngle=4.71239 EndAngle=7.85398
    g17: ArcOfCircle CenterX=-18.2337 CenterY=39 CenterZ=0 NormalX=0 NormalY=0 NormalZ=1 AngleXU=0 Radius=1.5 StartAngle=4.71485 EndAngle=7.85398
    g18: ArcOfCircle CenterX=-16.2837 CenterY=27.25 CenterZ=0 NormalX=0 NormalY=0 NormalZ=1 AngleXU=0 Radius=1.5 StartAngle=4.71485 EndAngle=7.85398
    g19: ArcOfCircle CenterX=-18.2337 CenterY=33 CenterZ=0 NormalX=0 NormalY=0 NormalZ=1 AngleXU=0 Radius=1.5 StartAngle=4.71485 EndAngle=7.85398
    g20: ArcOfCircle CenterX=-11.49 CenterY=21.5 CenterZ=0 NormalX=0 NormalY=0 NormalZ=1 AngleXU=0 Radius=1.5 StartAngle=4.71239 EndAngle=7.85398
    g21: ArcOfCircle CenterX=-1.5 CenterY=4.25 CenterZ=0 NormalX=0 NormalY=0 NormalZ=1 AngleXU=0 Radius=1.5 StartAngle=4.71239 EndAngle=7.85398
    g22: ArcOfCircle CenterX=-1.5 CenterY=10 CenterZ=0 NormalX=0 NormalY=0 NormalZ=1 AngleXU=0 Radius=1.5 StartAngle=4.71239 EndAngle=7.85398
    g23: ArcOfCircle CenterX=-1.5 CenterY=15.75 CenterZ=0 NormalX=0 NormalY=0 NormalZ=1 AngleXU=0 Radius=1.5 StartAngle=4.71239 EndAngle=7.85398
    g24: LineSegment StartX=-49.19 StartY=69.25 StartZ=0 EndX=-1.5 EndY=69.25 EndZ=0
    g25: LineSegment StartX=-49.19 StartY=66.25 StartZ=0 EndX=-1.5 EndY=66.25 EndZ=0
    g26: LineSegment StartX=-49.19 StartY=63.5 StartZ=0 EndX=-1.5 EndY=63.5 EndZ=0
    g27: LineSegment StartX=-49.19 StartY=60.5 StartZ=0 EndX=-1.5 EndY=60.5 EndZ=0
    g28: LineSegment StartX=-49.19 StartY=57.75 StartZ=0 EndX=-1.5 EndY=57.75 EndZ=0
    g29: LineSegment StartX=-49.19 StartY=54.75 StartZ=0 EndX=-1.5 EndY=54.75 EndZ=0
    g30: LineSegment StartX=-49.19 StartY=52 StartZ=0 EndX=-11.49 EndY=52 EndZ=0
    g31: LineSegment StartX=-49.19 StartY=49 StartZ=0 EndX=-11.49 EndY=49 EndZ=0
    g32: LineSegment StartX=-49.19 StartY=46.25 StartZ=0 EndX=-16.28 EndY=46.25 EndZ=0
    g33: LineSegment StartX=-49.19 StartY=43.25 StartZ=0 EndX=-16.28 EndY=43.25 EndZ=0
    g34: LineSegment StartX=-49.19 StartY=40.5 StartZ=0 EndX=-18.2337 EndY=40.5 EndZ=0
    g35: LineSegment StartX=-49.19 StartY=37.5 StartZ=0 EndX=-18.23 EndY=37.5 EndZ=0
    g36: LineSegment StartX=-49.19 StartY=34.5 StartZ=0 EndX=-18.2337 EndY=34.5 EndZ=0
    g37: LineSegment StartX=-49.19 StartY=31.5 StartZ=0 EndX=-18.23 EndY=31.5 EndZ=0
    g38: LineSegment StartX=-49.19 StartY=28.75 StartZ=0 EndX=-16.2837 EndY=28.75 EndZ=0
    g39: LineSegment StartX=-49.19 StartY=25.75 StartZ=0 EndX=-16.28 EndY=25.75 EndZ=0
    g40: LineSegment StartX=-49.19 StartY=23 StartZ=0 EndX=-11.49 EndY=23 EndZ=0
    g41: LineSegment StartX=-49.19 StartY=20 StartZ=0 EndX=-11.49 EndY=20 EndZ=0
    g42: LineSegment StartX=-49.19 StartY=17.25 StartZ=0 EndX=-1.5 EndY=17.25 EndZ=0
    g43: LineSegment StartX=-49.19 StartY=14.25 StartZ=0 EndX=-1.5 EndY=14.25 EndZ=0
    g44: LineSegment StartX=-49.19 StartY=11.5 StartZ=0 EndX=-1.5 EndY=11.5 EndZ=0
    g45: LineSegment StartX=-49.19 StartY=8.5 StartZ=0 EndX=-1.5 EndY=8.5 EndZ=0
    g46: LineSegment StartX=-49.19 StartY=5.75 StartZ=0 EndX=-1.5 EndY=5.75 EndZ=0
    g47: LineSegment StartX=-49.19 StartY=2.75 StartZ=0 EndX=-1.5 EndY=2.75 EndZ=0
  constraints (120):
    c: Vertical(g0)
    c: Distance(g0) = 3
    c: Block(g0)
    c: Vertical(g1)
    c: Distance(g1) = 3
    c: Vertical(g2)
    c: Equal(g0,g2) = 3
    c: Block(g2)
    c: Vertical(g3)
    c: Equal(g1,g3) = 3
    c: Vertical(g4)
    c: Equal(g0,g4) = 3
    c: Block(g4)
    c: Vertical(g5)
    c: Equal(g1,g5) = 3
    c: Vertical(g6)
    c: Equal(g0,g6) = 3
    c: Block(g6)
    c: Vertical(g7)
    c: Equal(g1,g7) = 3
    c: Vertical(g8)
    c: Equal(g0,g8) = 3
    c: Block(g8)
    c: Vertical(g9)
    c: Equal(g1,g9) = 3
    c: Vertical(g10)
    c: Equal(g0,g10) = 3
    c: Block(g10)
    c: Vertical(g11)
    c: Equal(g1,g11) = 3
    c: Block(g12)
    c: Block(g13)
    c: Block(g14)
    c: Block(g15)
    c: Block(g16)
    c: Block(g17)
    c: Block(g18)
    c: Block(g19)
    c: Block(g20)
    c: Block(g21)
    c: Block(g22)
    c: Block(g23)
    c: Block(g11)
    c: Block(g9)
    c: Block(g7)
    c: Block(g5)
    c: Block(g3)
    c: Block(g1)
    c: Coincident(g24,g0)
    c: Coincident(g24,g12)
    c: Horizontal(g24)
    c: Coincident(g25,g0)
    c: Coincident(g25,g12)
    c: Horizontal(g25)
    c: Coincident(g26,g1)
    c: Coincident(g26,g13)
    c: Horizontal(g26)
    c: Coincident(g27,g1)
    c: Coincident(g27,g13)
    c: Horizontal(g27)
    c: Coincident(g28,g2)
    c: Coincident(g28,g14)
    c: Horizontal(g28)
    c: Coincident(g29,g2)
    c: Coincident(g29,g14)
    c: Horizontal(g29)
    c: Coincident(g30,g3)
    c: Coincident(g30,g15)
    c: Horizontal(g30)
    c: Coincident(g31,g3)
    c: Coincident(g31,g15)
    c: Horizontal(g31)
    c: Coincident(g32,g4)
    c: Coincident(g32,g16)
    c: Horizontal(g32)
    c: Coincident(g33,g4)
    c: Coincident(g33,g16)
    c: Horizontal(g33)
    c: Coincident(g34,g5)
    c: Coincident(g34,g17)
    c: Horizontal(g34)
    c: Coincident(g35,g5)
    c: Coincident(g35,g17)
    c: Horizontal(g35)
    c: Coincident(g36,g6)
    c: Coincident(g36,g19)
    c: Horizontal(g36)
    c: Coincident(g37,g6)
    c: Coincident(g37,g19)
    c: Horizontal(g37)
    c: Coincident(g38,g7)
    c: Coincident(g38,g18)
    c: Horizontal(g38)
    c: Coincident(g39,g7)
    c: Coincident(g39,g18)
    c: Horizontal(g39)
    c: Coincident(g40,g8)
    c: Coincident(g40,g20)
    c: Horizontal(g40)
    c: Coincident(g41,g8)
    c: Coincident(g41,g20)
    c: Horizontal(g41)
    c: Coincident(g42,g9)
    c: Coincident(g42,g23)
    c: Horizontal(g42)
    c: Coincident(g43,g9)
    c: Coincident(g43,g23)
    c: Horizontal(g43)
    c: Coincident(g44,g10)
    c: Coincident(g44,g22)
    c: Horizontal(g44)
    c: Coincident(g45,g10)
    c: Coincident(g45,g22)
    c: Horizontal(g45)
    c: Coincident(g46,g11)
    c: Coincident(g46,g21)
    c: Horizontal(g46)
    c: Coincident(g47,g11)
    c: Coincident(g47,g21)
    c: Horizontal(g47)
FEATURE [Part::Extrusion] Extrude065
  Base = -> Sketch074
  Dir = (1,0,0)
  DirMode = 2
  FaceMakerClass = Part::FaceMakerBullseye
  LengthFwd = 23
  LengthRev = 0
  Placement = pos=(-19,0,0) rot=(0,0,1;0rad)
  Solid = true
  Symmetric = false
FEATURE [Part::Fillet] Fillet056  label="removeToCreateVentalationHoles003"
  Base = -> Extrude065
  Edges = <same value as first occurrence — deduplicated (x6 in doc)>
  Placement = pos=(7,0.02,0) rot=(0,0,1;0rad)
FEATURE [Part::Revolution] Revolve158  label="removeToCreateScrewAndThreadedInsertHole065"
  Angle = 360
  Axis = (0,1,0)
  Base = (0,0,0)
  FaceMakerClass = Part::FaceMakerBullseye
  Placement = pos=(12.5,0,62) rot=(0,0,1;0rad)
  Solid = false
  Source = -> Face146
  Symmetric = false
FEATURE [Part::Revolution] Revolve159  label="removeToCreateScrewAndThreadedInsertHole066"
  Angle = 360
  Axis = (0,1,0)
  Base = (0,0,0)
  FaceMakerClass = Part::FaceMakerBullseye
  Placement = pos=(89.5,0,68.5) rot=(0,0,1;0rad)
  Solid = false
  Source = -> Face143
  Symmetric = false
FEATURE [Part::Revolution] Revolve160  label="removeToCreateScrewAndThreadedInsertHole067"
  Angle = 360
  Axis = (0,1,0)
  Base = (0,0,0)
  FaceMakerClass = Part::FaceMakerBullseye
  Placement = pos=(89.5,0,3.5) rot=(0,0,1;0rad)
  Solid = false
  Source = -> Face142
  Symmetric = false
FEATURE [Part::Revolution] Revolve161  label="removeToCreateScrewAndThreadedInsertHole068"
  Angle = 360
  Axis = (0,1,0)
  Base = (0,0,0)
  FaceMakerClass = Part::FaceMakerBullseye
  Placement = pos=(109.5,4.7,3.5) rot=(0,0,1;0rad)
  Solid = false
  Source = -> Face145
  Symmetric = false
FEATURE [Part::Revolution] Revolve162  label="removeToCreateScrewAndThreadedInsertHole069"
  Angle = 360
  Axis = (0,1,0)
  Base = (0,0,0)
  FaceMakerClass = Part::FaceMakerBullseye
  Placement = pos=(109.5,4.7,68.5) rot=(0,0,1;0rad)
  Solid = false
  Source = -> Face144
  Symmetric = false
FEATURE [Part::MultiFuse] Fusion141  label="removeToCreateScrewAndThreadedInsertHole064"
  Shapes = -> [Revolve162,Revolve161,Revolve160,Revolve159,Revolve158,Revolve157]
FEATURE [Part::Cylinder] Cylinder062
  Angle = 360
  AttacherType = Attacher::AttachEngine3D
  Height = 20
  Placement = pos=(0,0,36.15) rot=(0,0,1;0rad)
  Radius = 14
FEATURE [Part::Cylinder] Cylinder063
  Angle = 360
  AttacherType = Attacher::AttachEngine3D
  Height = 10
  Placement = pos=(0,0,36.15) rot=(0,0,1;0rad)
  Radius = 4
FEATURE [Part::MultiFuse] Fusion139  label="removeToCreteHoleForPlugHousing052"
  Placement = pos=(70,19,36) rot=(0,1,0;1.5708rad)
  Shapes = -> [Cylinder062,Cylinder063]
FEATURE [Part::Cut] Cut060  label="bottom017"
  Base = -> Extrude064
  Tool = -> Fusion139
FEATURE [Part::Cut] Cut061  label="bottom019"
  Base = -> Cut060
  Tool = -> Fusion141
FEATURE [Part::MultiFuse] Fusion140  label="bottom018"
  Shapes = -> [Cut061,Cut058]
FEATURE [Part::Cut] Cut059  label="bottom020"
  Base = -> Fusion140
  Tool = -> Fillet056
FEATURE [Part::Box] Box036  label="Cube021"
  AttacherType = Attacher::AttachEngine3D
  Height = 80
  Length = 26
  Placement = pos=(0,-1,-5) rot=(0,0,1;0rad)
  Width = 11
FEATURE [Part::Cut] Cut062  label="removeFromBottom002"
  Base = -> Cut057
  Tool = -> Box036
FEATURE [Part::Cut] Cut063
  Base = -> Cut059
  Tool = -> Cut062
FEATURE [Part::Cut] Cut064  label="pcbStands"
  Base = -> Fusion095
  Tool = -> Fusion127
FEATURE [Sketcher::SketchObject] Sketch075  label="topSketch022"
  FullyConstrained = true
  sketch-geometry (6):
    g0: LineSegment StartX=19 StartY=38 StartZ=0 EndX=117 EndY=38 EndZ=0
    g1: ArcOfCircle CenterX=19 CenterY=19 CenterZ=0 NormalX=0 NormalY=0 NormalZ=1 AngleXU=0 Radius=19 StartAngle=1.5708 EndAngle=3.14159
    g2: LineSegment StartX=117 StartY=38 StartZ=0 EndX=117 EndY=19 EndZ=0
    g3: LineSegment StartX=98 StartY=1.0161e-12 StartZ=0 EndX=5.22862e-06 EndY=1.0161e-12 EndZ=0
    g4: LineSegment StartX=5.22862e-06 StartY=19 StartZ=0 EndX=5.22862e-06 EndY=1.0161e-12 EndZ=0
    g5: ArcOfCircle CenterX=98 CenterY=19 CenterZ=0 NormalX=0 NormalY=0 NormalZ=1 AngleXU=0 Radius=19 StartAngle=4.71239 EndAngle=6.28319
  constraints (16):
    c: Horizontal(g0)
    c: Distance(g0) = 98
    c: Coincident(g1,g0)
    c: Block(g1)
    c: Coincident(g2,g0)
    c: Vertical(g2)
    c: Distance(g2) = 19
    c: Horizontal(g3)
    c: Coincident(g4,g1)
    c: Vertical(g4)
    c: Coincident(g3,g4)
    c: Block(g3)
    c: Coincident(g5,g2)
    c: Coincident(g5,g3)
    c: Block(g0)
    c: Block(g5)
FEATURE [Part::Extrusion] Extrude067  label="sideB003"
  Base = -> Sketch075
  Dir = (0,0,1)
  DirMode = 2
  FaceMakerClass = Part::FaceMakerBullseye
  LengthFwd = 3
  LengthRev = 0
  Placement = pos=(0,0,71.7) rot=(0,0,1;0rad)
  Solid = true
  Symmetric = false
FEATURE [Sketcher::SketchObject] Sketch076  label="topSketch023"
  FullyConstrained = true
  sketch-geometry (6):
    g0: LineSegment StartX=19 StartY=38 StartZ=0 EndX=117 EndY=38 EndZ=0
    g1: ArcOfCircle CenterX=19 CenterY=19 CenterZ=0 NormalX=0 NormalY=0 NormalZ=1 AngleXU=0 Radius=19 StartAngle=1.5708 EndAngle=3.14159
    g2: LineSegment StartX=117 StartY=38 StartZ=0 EndX=117 EndY=19 EndZ=0
    g3: LineSegment StartX=98 StartY=1.0161e-12 StartZ=0 EndX=5.22862e-06 EndY=1.0161e-12 EndZ=0
    g4: LineSegment StartX=5.22862e-06 StartY=19 StartZ=0 EndX=5.22862e-06 EndY=1.0161e-12 EndZ=0
    g5: ArcOfCircle CenterX=98 CenterY=19 CenterZ=0 NormalX=0 NormalY=0 NormalZ=1 AngleXU=0 Radius=19 StartAngle=4.71239 EndAngle=6.28319
  constraints (16):
    c: Horizontal(g0)
    c: Distance(g0) = 98
    c: Coincident(g1,g0)
    c: Block(g1)
    c: Coincident(g2,g0)
    c: Vertical(g2)
    c: Distance(g2) = 19
    c: Horizontal(g3)
    c: Coincident(g4,g1)
    c: Vertical(g4)
    c: Coincident(g3,g4)
    c: Block(g3)
    c: Coincident(g5,g2)
    c: Coincident(g5,g3)
    c: Block(g0)
    c: Block(g5)
FEATURE [Part::Extrusion] Extrude066  label="sideA003"
  Base = -> Sketch076
  Dir = (0,0,1)
  DirMode = 2
  FaceMakerClass = Part::FaceMakerBullseye
  LengthFwd = 3
  LengthRev = 0
  Placement = pos=(0,0,-2.7) rot=(0,0,1;0rad)
  Solid = true
  Symmetric = false
FEATURE [Part::MultiFuse] Fusion142  label="removeFromBottom003"
  Placement = pos=(2,0,0) rot=(0,0,1;0rad)
  Shapes = -> [Extrude066,Extrude067]
FEATURE [Part::Cut] Cut065  label="screwRetainers002"
  Base = -> Fusion096
  Tool = -> Fusion142
FEATURE [Sketcher::SketchObject] Sketch077
  FullyConstrained = true
  Placement = pos=(117,19,0) rot=(0.57735,0.57735,0.57735;2.0944rad)
  sketch-geometry (8):
    g0: LineSegment StartX=-49.19 StartY=63.5 StartZ=0 EndX=-49.19 EndY=60.5 EndZ=0
    g1: LineSegment StartX=-49.19 StartY=11.5 StartZ=0 EndX=-49.19 EndY=8.5 EndZ=0
    g2: ArcOfCircle CenterX=-1.5 CenterY=62 CenterZ=0 NormalX=0 NormalY=0 NormalZ=1 AngleXU=0 Radius=1.5 StartAngle=4.71239 EndAngle=7.85398
    g3: ArcOfCircle CenterX=-1.5 CenterY=10 CenterZ=0 NormalX=0 NormalY=0 NormalZ=1 AngleXU=0 Radius=1.5 StartAngle=4.71239 EndAngle=7.85398
    g4: LineSegment StartX=-49.19 StartY=63.5 StartZ=0 EndX=-1.5 EndY=63.5 EndZ=0
    g5: LineSegment StartX=-49.19 StartY=60.5 StartZ=0 EndX=-1.5 EndY=60.5 EndZ=0
    g6: LineSegment StartX=-49.19 StartY=11.5 StartZ=0 EndX=-1.5 EndY=11.5 EndZ=0
    g7: LineSegment StartX=-49.19 StartY=8.5 StartZ=0 EndX=-1.5 EndY=8.5 EndZ=0
  constraints (19):
    c: Vertical(g0)
    c: Distance(g0) = 3
    c: Vertical(g1)
    c: Block(g1)
    c: Block(g2)
    c: Block(g3)
    c: Block(g0)
    c: Coincident(g4,g0)
    c: Coincident(g4,g2)
    c: Horizontal(g4)
    c: Coincident(g5,g0)
    c: Coincident(g5,g2)
    c: Horizontal(g5)
    c: Coincident(g6,g1)
    c: Coincident(g6,g3)
    c: Horizontal(g6)
    c: Coincident(g7,g1)
    c: Coincident(g7,g3)
    c: Horizontal(g7)
FEATURE [Part::Extrusion] Extrude068
  Base = -> Sketch077
  Dir = (1,0,0)
  DirMode = 2
  FaceMakerClass = Part::FaceMakerBullseye
  LengthFwd = 10
  LengthRev = 0
  Solid = true
  Symmetric = false
FEATURE [Part::Fillet] Fillet057  label="removeFromtMoreFrontCaseScrewRetainers002"
  Base = -> Extrude068
  Edges = 4 edges r=1.49: [Edge6,Edge11,Edge18,Edge23]
  Placement = pos=(-12,0,0) rot=(0,0,1;0rad)
FEATURE [Sketcher::SketchObject] Sketch078
  FullyConstrained = true
  Placement = pos=(117,19,0) rot=(0.57735,0.57735,0.57735;2.0944rad)
  sketch-geometry (8):
    g0: LineSegment StartX=-49.19 StartY=69.25 StartZ=0 EndX=-49.19 EndY=66.25 EndZ=0
    g1: LineSegment StartX=-49.19 StartY=5.75 StartZ=0 EndX=-49.19 EndY=2.75 EndZ=0
    g2: ArcOfCircle CenterX=-1.5 CenterY=67.75 CenterZ=0 NormalX=0 NormalY=0 NormalZ=1 AngleXU=0 Radius=1.5 StartAngle=4.71239 EndAngle=7.85398
    g3: ArcOfCircle CenterX=-1.5 CenterY=4.25 CenterZ=0 NormalX=0 NormalY=0 NormalZ=1 AngleXU=0 Radius=1.5 StartAngle=4.71239 EndAngle=7.85398
    g4: LineSegment StartX=-49.19 StartY=69.25 StartZ=0 EndX=-1.5 EndY=69.25 EndZ=0
    g5: LineSegment StartX=-49.19 StartY=66.25 StartZ=0 EndX=-1.5 EndY=66.25 EndZ=0
    g6: LineSegment StartX=-49.19 StartY=5.75 StartZ=0 EndX=-1.5 EndY=5.75 EndZ=0
    g7: LineSegment StartX=-49.19 StartY=2.75 StartZ=0 EndX=-1.5 EndY=2.75 EndZ=0
  constraints (19):
    c: Vertical(g0)
    c: Distance(g0) = 3
    c: Block(g0)
    c: Vertical(g1)
    c: Block(g2)
    c: Block(g3)
    c: Block(g1)
    c: Coincident(g4,g0)
    c: Coincident(g4,g2)
    c: Horizontal(g4)
    c: Coincident(g5,g0)
    c: Coincident(g5,g2)
    c: Horizontal(g5)
    c: Coincident(g6,g1)
    c: Coincident(g6,g3)
    c: Horizontal(g6)
    c: Coincident(g7,g1)
    c: Coincident(g7,g3)
    c: Horizontal(g7)
FEATURE [Part::Extrusion] Extrude069
  Base = -> Sketch078
  Dir = (1,0,0)
  DirMode = 2
  FaceMakerClass = Part::FaceMakerBullseye
  LengthFwd = 10
  LengthRev = 0
  Solid = true
  Symmetric = false
FEATURE [Part::Fillet] Fillet058  label="removeFromtMoreFrontCaseScrewRetainers003"
  Base = -> Extrude069
  Edges = 4 edges r=1.49: [Edge6,Edge11,Edge18,Edge23]
  Placement = pos=(-4,0,0) rot=(0,0,1;0rad)
FEATURE [Part::Cut] Cut066
  Base = -> Cut065
  Tool = -> Fillet058
FEATURE [Part::Cut] Cut067  label="screwPillars"
  Base = -> Cut066
  Tool = -> Fillet057
FEATURE [Part::MultiFuse] Fusion143  label="bottom021"
  Shapes = -> [Cut031,Cut063]
FEATURE [Part::Cylinder] Cylinder
  Angle = 360
  AttacherType = Attacher::AttachEngine3D
  Height = 10
  Placement = pos=(20.65,12,4.68) rot=(1,0,0;1.5708rad)
  Radius = 2
FEATURE [Part::Cylinder] Cylinder064
  Angle = 360
  AttacherType = Attacher::AttachEngine3D
  Height = 10
  Placement = pos=(20.65,12,67.38) rot=(1,0,0;1.5708rad)
  Radius = 2
FEATURE [Part::Cylinder] Cylinder065
  Angle = 360
  AttacherType = Attacher::AttachEngine3D
  Height = 10
  Placement = pos=(77.15,12,67.38) rot=(1,0,0;1.5708rad)
  Radius = 2
FEATURE [Part::Cylinder] Cylinder066
  Angle = 360
  AttacherType = Attacher::AttachEngine3D
  Height = 10
  Placement = pos=(77.15,12,4.68) rot=(1,0,0;1.5708rad)
  Radius = 2
FEATURE [Part::MultiFuse] Fusion144  label="removeFromThreadedInsertHousing"
  Shapes = -> [Cylinder065,Cylinder064,Cylinder,Cylinder066]
FEATURE [Part::Cut] Cut068  label="pcbStands001"
  Base = -> Cut064
  Tool = -> Fusion144
FEATURE [Part::MultiFuse] Fusion145
  Shapes = -> [Cut068,Fusion143]
FEATURE [Part::MultiFuse] Fusion146
  Shapes = -> [Fusion145]
FEATURE [Part::MultiFuse] Fusion147  label="bottom022"
  Shapes = -> [Cut067,Fusion146]
FEATURE [Part::MultiFuse] Fusion148  label="casePillars005"
  Shapes = -> [Cut047,Fusion092]
FEATURE [Part::MultiFuse] Fusion149  label="bottom023"
  Shapes = -> [Fusion124,Fusion113,Fusion147]
FEATURE [Part::MultiFuse] Fusion150  label="topBits"
  Shapes = -> [Cut025,Fusion148,Cut030,Fillet034]
FEATURE [Part::Feature] Face149 .. Face152  x4 (patterned run collapsed; names and placements below)
  shape: bbox 3.2 x 1.5 x 2e-07 mm, 1 faces, 0 solids (baked)
FEATURE [Part::Feature] Face153
  shape: bbox 3.6 x 3.2 x 2e-07 mm, 1 faces, 0 solids (baked)
FEATURE [Part::Feature] Face154
  shape: bbox 3.6 x 3.2 x 2e-07 mm, 1 faces, 0 solids (baked)
FEATURE [Sketcher::SketchObject] Sketch079  label="topSketch024"
  FullyConstrained = true
  sketch-geometry (6):
    g0: LineSegment StartX=19 StartY=38 StartZ=0 EndX=117 EndY=38 EndZ=0
    g1: ArcOfCircle CenterX=19 CenterY=19 CenterZ=0 NormalX=0 NormalY=0 NormalZ=1 AngleXU=0 Radius=19 StartAngle=1.5708 EndAngle=3.14159
    g2: LineSegment StartX=117 StartY=38 StartZ=0 EndX=117 EndY=19 EndZ=0
    g3: LineSegment StartX=98 StartY=1.0161e-12 StartZ=0 EndX=5.22862e-06 EndY=1.0161e-12 EndZ=0
    g4: LineSegment StartX=5.22862e-06 StartY=19 StartZ=0 EndX=5.22862e-06 EndY=1.0161e-12 EndZ=0
    g5: ArcOfCircle CenterX=98 CenterY=19 CenterZ=0 NormalX=0 NormalY=0 NormalZ=1 AngleXU=0 Radius=19 StartAngle=4.71239 EndAngle=6.28319
  constraints (16):
    c: Horizontal(g0)
    c: Distance(g0) = 98
    c: Coincident(g1,g0)
    c: Block(g1)
    c: Coincident(g2,g0)
    c: Vertical(g2)
    c: Distance(g2) = 19
    c: Horizontal(g3)
    c: Coincident(g4,g1)
    c: Vertical(g4)
    c: Coincident(g3,g4)
    c: Block(g3)
    c: Coincident(g5,g2)
    c: Coincident(g5,g3)
    c: Block(g0)
    c: Block(g5)
FEATURE [Sketcher::SketchObject] Sketch080  label="topSketch025"
  FullyConstrained = true
  sketch-geometry (6):
    g0: LineSegment StartX=19 StartY=38 StartZ=0 EndX=117 EndY=38 EndZ=0
    g1: ArcOfCircle CenterX=19 CenterY=19 CenterZ=0 NormalX=0 NormalY=0 NormalZ=1 AngleXU=0 Radius=19 StartAngle=1.5708 EndAngle=3.14159
    g2: LineSegment StartX=117 StartY=38 StartZ=0 EndX=117 EndY=19 EndZ=0
    g3: LineSegment StartX=98 StartY=1.0161e-12 StartZ=0 EndX=5.22862e-06 EndY=1.0161e-12 EndZ=0
    g4: LineSegment StartX=5.22862e-06 StartY=19 StartZ=0 EndX=5.22862e-06 EndY=1.0161e-12 EndZ=0
    g5: ArcOfCircle CenterX=98 CenterY=19 CenterZ=0 NormalX=0 NormalY=0 NormalZ=1 AngleXU=0 Radius=19 StartAngle=4.71239 EndAngle=6.28319
  constraints (16):
    c: Horizontal(g0)
    c: Distance(g0) = 98
    c: Coincident(g1,g0)
    c: Block(g1)
    c: Coincident(g2,g0)
    c: Vertical(g2)
    c: Distance(g2) = 19
    c: Horizontal(g3)
    c: Coincident(g4,g1)
    c: Vertical(g4)
    c: Coincident(g3,g4)
    c: Block(g3)
    c: Coincident(g5,g2)
    c: Coincident(g5,g3)
    c: Block(g0)
    c: Block(g5)
FEATURE [Part::Extrusion] Extrude070  label="sideA004"
  Base = -> Sketch080
  Dir = (0,0,1)
  DirMode = 2
  FaceMakerClass = Part::FaceMakerBullseye
  LengthFwd = 3
  LengthRev = 0
  Placement = pos=(0,0,-2.7) rot=(0,0,1;0rad)
  Solid = true
  Symmetric = false
FEATURE [Sketcher::SketchObject] Sketch081
  FullyConstrained = true
  Placement = pos=(117,19,0) rot=(0.57735,0.57735,0.57735;2.0944rad)
  sketch-geometry (8):
    g0: LineSegment StartX=-49.19 StartY=63.5 StartZ=0 EndX=-49.19 EndY=60.5 EndZ=0
    g1: LineSegment StartX=-49.19 StartY=11.5 StartZ=0 EndX=-49.19 EndY=8.5 EndZ=0
    g2: ArcOfCircle CenterX=-1.5 CenterY=62 CenterZ=0 NormalX=0 NormalY=0 NormalZ=1 AngleXU=0 Radius=1.5 StartAngle=4.71239 EndAngle=7.85398
    g3: ArcOfCircle CenterX=-1.5 CenterY=10 CenterZ=0 NormalX=0 NormalY=0 NormalZ=1 AngleXU=0 Radius=1.5 StartAngle=4.71239 EndAngle=7.85398
    g4: LineSegment StartX=-49.19 StartY=63.5 StartZ=0 EndX=-1.5 EndY=63.5 EndZ=0
    g5: LineSegment StartX=-49.19 StartY=60.5 StartZ=0 EndX=-1.5 EndY=60.5 EndZ=0
    g6: LineSegment StartX=-49.19 StartY=11.5 StartZ=0 EndX=-1.5 EndY=11.5 EndZ=0
    g7: LineSegment StartX=-49.19 StartY=8.5 StartZ=0 EndX=-1.5 EndY=8.5 EndZ=0
  constraints (19):
    c: Vertical(g0)
    c: Distance(g0) = 3
    c: Vertical(g1)
    c: Block(g1)
    c: Block(g2)
    c: Block(g3)
    c: Block(g0)
    c: Coincident(g4,g0)
    c: Coincident(g4,g2)
    c: Horizontal(g4)
    c: Coincident(g5,g0)
    c: Coincident(g5,g2)
    c: Horizontal(g5)
    c: Coincident(g6,g1)
    c: Coincident(g6,g3)
    c: Horizontal(g6)
    c: Coincident(g7,g1)
    c: Coincident(g7,g3)
    c: Horizontal(g7)
FEATURE [Part::Extrusion] Extrude071  label="sideB004"
  Base = -> Sketch079
  Dir = (0,0,1)
  DirMode = 2
  FaceMakerClass = Part::FaceMakerBullseye
  LengthFwd = 3
  LengthRev = 0
  Placement = pos=(0,0,71.7) rot=(0,0,1;0rad)
  Solid = true
  Symmetric = false
FEATURE [Part::MultiFuse] Fusion152  label="removeFromBottom004"
  Placement = pos=(2,0,0) rot=(0,0,1;0rad)
  Shapes = -> [Extrude070,Extrude071]
FEATURE [Part::Extrusion] Extrude072
  Base = -> Sketch081
  Dir = (1,0,0)
  DirMode = 2
  FaceMakerClass = Part::FaceMakerBullseye
  LengthFwd = 10
  LengthRev = 0
  Solid = true
  Symmetric = false
FEATURE [Part::Fillet] Fillet059  label="removeFromtMoreFrontCaseScrewRetainers004"
  Base = -> Extrude072
  Edges = 4 edges r=1.49: [Edge6,Edge11,Edge18,Edge23]
  Placement = pos=(-12,0,0) rot=(0,0,1;0rad)
FEATURE [Sketcher::SketchObject] Sketch082
  FullyConstrained = true
  Placement = pos=(117,19,0) rot=(0.57735,0.57735,0.57735;2.0944rad)
  sketch-geometry (8):
    g0: LineSegment StartX=-49.19 StartY=69.25 StartZ=0 EndX=-49.19 EndY=66.25 EndZ=0
    g1: LineSegment StartX=-49.19 StartY=5.75 StartZ=0 EndX=-49.19 EndY=2.75 EndZ=0
    g2: ArcOfCircle CenterX=-1.5 CenterY=67.75 CenterZ=0 NormalX=0 NormalY=0 NormalZ=1 AngleXU=0 Radius=1.5 StartAngle=4.71239 EndAngle=7.85398
    g3: ArcOfCircle CenterX=-1.5 CenterY=4.25 CenterZ=0 NormalX=0 NormalY=0 NormalZ=1 AngleXU=0 Radius=1.5 StartAngle=4.71239 EndAngle=7.85398
    g4: LineSegment StartX=-49.19 StartY=69.25 StartZ=0 EndX=-1.5 EndY=69.25 EndZ=0
    g5: LineSegment StartX=-49.19 StartY=66.25 StartZ=0 EndX=-1.5 EndY=66.25 EndZ=0
    g6: LineSegment StartX=-49.19 StartY=5.75 StartZ=0 EndX=-1.5 EndY=5.75 EndZ=0
    g7: LineSegment StartX=-49.19 StartY=2.75 StartZ=0 EndX=-1.5 EndY=2.75 EndZ=0
  constraints (19):
    c: Vertical(g0)
    c: Distance(g0) = 3
    c: Block(g0)
    c: Vertical(g1)
    c: Block(g2)
    c: Block(g3)
    c: Block(g1)
    c: Coincident(g4,g0)
    c: Coincident(g4,g2)
    c: Horizontal(g4)
    c: Coincident(g5,g0)
    c: Coincident(g5,g2)
    c: Horizontal(g5)
    c: Coincident(g6,g1)
    c: Coincident(g6,g3)
    c: Horizontal(g6)
    c: Coincident(g7,g1)
    c: Coincident(g7,g3)
    c: Horizontal(g7)
FEATURE [Part::Extrusion] Extrude073
  Base = -> Sketch082
  Dir = (1,0,0)
  DirMode = 2
  FaceMakerClass = Part::FaceMakerBullseye
  LengthFwd = 10
  LengthRev = 0
  Solid = true
  Symmetric = false
FEATURE [Part::Fillet] Fillet060  label="removeFromtMoreFrontCaseScrewRetainers005"
  Base = -> Extrude073
  Edges = 4 edges r=1.49: [Edge6,Edge11,Edge18,Edge23]
  Placement = pos=(-4,0,0) rot=(0,0,1;0rad)
FEATURE [Part::Revolution] Revolve163  label="backCaseScrewRetainer004"
  Angle = 360
  Axis = (0,1,0)
  Base = (0,0,0)
  FaceMakerClass = Part::FaceMakerBullseye
  Placement = pos=(12.5,3,62) rot=(0,0,1;0rad)
  Solid = false
  Source = -> Face149
  Symmetric = false
FEATURE [Part::Revolution] Revolve164  label="frontCaseScrewRetainer006"
  Angle = 360
  Axis = (0,1,0)
  Base = (0,0,0)
  FaceMakerClass = Part::FaceMakerBullseye
  Placement = pos=(89.5,3,68.5) rot=(0,0,1;0rad)
  Solid = false
  Source = -> Face151
  Symmetric = false
FEATURE [Part::Revolution] Revolve165  label="frontCaseScrewRetainer007"
  Angle = 360
  Axis = (0,1,0)
  Base = (0,0,0)
  FaceMakerClass = Part::FaceMakerBullseye
  Placement = pos=(89.5,3,3.5) rot=(0,0,1;0rad)
  Solid = false
  Source = -> Face152
  Symmetric = false
FEATURE [Part::Revolution] Revolve166  label="backCaseScrewRetainer005"
  Angle = 360
  Axis = (0,1,0)
  Base = (0,0,0)
  FaceMakerClass = Part::FaceMakerBullseye
  Placement = pos=(12.5,3,10) rot=(0,0,1;0rad)
  Solid = false
  Source = -> Face150
  Symmetric = false
FEATURE [Part::Revolution] Revolve167  label="moreFrontCaseScrewRetainer006"
  Angle = 360
  Axis = (0,1,0)
  Base = (0,0,0)
  FaceMakerClass = Part::FaceMakerBullseye
  Placement = pos=(109.5,4.5,68.5) rot=(0,0,1;0rad)
  Solid = false
  Source = -> Face153
  Symmetric = false
FEATURE [Part::Revolution] Revolve168  label="moreFrontCaseScrewRetainer007"
  Angle = 360
  Axis = (0,1,0)
  Base = (0,0,0)
  FaceMakerClass = Part::FaceMakerBullseye
  Placement = pos=(109.5,4.5,3.5) rot=(0,0,1;0rad)
  Solid = false
  Source = -> Face154
  Symmetric = false
FEATURE [Part::MultiFuse] Fusion151  label="screwRetainers003"
  Shapes = -> [Revolve168,Revolve167,Revolve166,Revolve165,Revolve164,Revolve163]
FEATURE [Part::Cut] Cut069  label="screwRetainers004"
  Base = -> Fusion151
  Tool = -> Fusion152
FEATURE [Part::Cut] Cut070
  Base = -> Cut069
  Tool = -> Fillet060
FEATURE [Part::Cut] Cut071  label="screwPillars001"
  Base = -> Cut070
  Tool = -> Fillet059
FEATURE [Part::MultiFuse] Fusion153  label="bottom024"
  Shapes = -> [Fusion149,Cut071]
FEATURE [Part::Cylinder] Cylinder067
  Angle = 360
  AttacherType = Attacher::AttachEngine3D
  Height = 10
  Placement = pos=(20.65,12,4.68) rot=(1,0,0;1.5708rad)
  Radius = 2
FEATURE [Part::Cylinder] Cylinder068
  Angle = 360
  AttacherType = Attacher::AttachEngine3D
  Height = 10
  Placement = pos=(20.65,12,67.38) rot=(1,0,0;1.5708rad)
  Radius = 2
FEATURE [Part::Cylinder] Cylinder069
  Angle = 360
  AttacherType = Attacher::AttachEngine3D
  Height = 10
  Placement = pos=(77.15,12,67.38) rot=(1,0,0;1.5708rad)
  Radius = 2
FEATURE [Part::Cylinder] Cylinder070
  Angle = 360
  AttacherType = Attacher::AttachEngine3D
  Height = 10
  Placement = pos=(77.15,12,4.68) rot=(1,0,0;1.5708rad)
  Radius = 2
FEATURE [Part::MultiFuse] Fusion154  label="removeFromThreadedInsertHousing001"
  Shapes = -> [Cylinder069,Cylinder068,Cylinder067,Cylinder070]
FEATURE [Part::Cut] Cut072  label="bottom025"
  Base = -> Fusion153
  Tool = -> Fusion154
FEATURE [Image::ImagePlane] ImagePlane
  XSize = 339
  YSize = 72
FEATURE [Sketcher::SketchObject] Sketch083
  FullyConstrained = true
  MapMode = 5
  Support = -> [XY_Plane]
  sketch-geometry (338):
    g0: LineSegment StartX=-151.619 StartY=28.8932 StartZ=0 EndX=-140.819 EndY=28.8932 EndZ=0
    g1: LineSegment StartX=-151.619 StartY=24.0313 StartZ=0 EndX=-151.619 EndY=28.8932 EndZ=0
    g2: LineSegment StartX=-140.819 StartY=17.7713 StartZ=0 EndX=-151.619 EndY=17.7713 EndZ=0
    g3: LineSegment StartX=-151.619 StartY=17.7713 StartZ=0 EndX=-151.619 EndY=22.6313 EndZ=0
    g4: LineSegment StartX=-151.619 StartY=22.6313 StartZ=0 EndX=-145.128 EndY=22.6313 EndZ=0
    g5: LineSegment StartX=-145.128 StartY=24.0313 StartZ=0 EndX=-140.819 EndY=28.8932 EndZ=0
    g6: LineSegment StartX=-145.128 StartY=22.6313 StartZ=0 EndX=-140.819 EndY=17.7713 EndZ=0
    g7: ArcOfCircle CenterX=-155.157 CenterY=23.3323 CenterZ=0 NormalX=0 NormalY=0 NormalZ=1 AngleXU=0 Radius=6.92354 StartAngle=1.03434 EndAngle=5.24885
    g8: ArcOfCircle CenterX=-155.157 CenterY=23.3323 CenterZ=0 NormalX=0 NormalY=0 NormalZ=1 AngleXU=0 Radius=12.6269 StartAngle=1.28675 EndAngle=4.99643
    g9: LineSegment StartX=-151.619 StartY=35.4532 StartZ=0 EndX=-151.619 EndY=29.2832 EndZ=0
    g10: LineSegment StartX=-151.619 StartY=17.3813 StartZ=0 EndX=-151.619 EndY=11.2113 EndZ=0
    g11-g21: Circle x11 (B-spline internal-alignment scaffolding for g22; pole/knot coordinates omitted)
    g22: BSplineCurve PolesCount=11 KnotsCount=9 Degree=3 IsPeriodic=0
    g23-g31: GeomPoint x9 (B-spline internal-alignment scaffolding for g22; pole/knot coordinates omitted)
    g32-g49: Circle x18 (B-spline internal-alignment scaffolding for g50; pole/knot coordinates omitted)
    g50: BSplineCurve PolesCount=18 KnotsCount=16 Degree=3 IsPeriodic=0
    g51-g66: GeomPoint x16 (B-spline internal-alignment scaffolding for g50; pole/knot coordinates omitted)
    g67: LineSegment StartX=-117.124 StartY=30.093 StartZ=0 EndX=-117.603 EndY=26.5272 EndZ=0
    g68: LineSegment StartX=-117.603 StartY=17.8472 StartZ=0 EndX=-117.124 EndY=14.2659 EndZ=0
    g69: Ellipse CenterX=-109.671 CenterY=20.025 CenterZ=0 NormalX=0 NormalY=0 NormalZ=1 MajorRadius=3.34798 MinorRadius=2.71052 AngleXU=-1.56793
    g70: GeomPoint X=-109.666 Y=18.0598 Z=0
    g71: GeomPoint X=-109.677 Y=21.9902 Z=0
    g72: Ellipse CenterX=-109.671 CenterY=20.0123 CenterZ=0 NormalX=0 NormalY=0 NormalZ=1 MajorRadius=6.93002 MinorRadius=6.36273 AngleXU=-3.13976
    g73: GeomPoint X=-112.417 Y=20.0073 Z=0
    g74: GeomPoint X=-106.925 Y=20.0173 Z=0
    g75: Ellipse CenterX=-51.7682 CenterY=20.1463 CenterZ=0 NormalX=0 NormalY=0 NormalZ=1 MajorRadius=3.19279 MinorRadius=2.71052 AngleXU=-1.52774
    g76: GeomPoint X=-51.6955 Y=18.4606 Z=0
    g77: GeomPoint X=-51.8408 Y=21.832 Z=0
    g78: GeomPoint X=-54.5142 Y=20.1413 Z=0
    g79: GeomPoint X=-49.0221 Y=20.1513 Z=0
    g80: Ellipse CenterX=-51.7682 CenterY=20.1463 CenterZ=0 NormalX=0 NormalY=0 NormalZ=1 MajorRadius=6.93002 MinorRadius=6.36273 AngleXU=-3.13976
    g81: Ellipse CenterX=-22.8436 CenterY=20.1783 CenterZ=0 NormalX=0 NormalY=0 NormalZ=1 MajorRadius=3.31512 MinorRadius=2.71052 AngleXU=-1.60214
    g82: GeomPoint X=-22.9034 Y=18.2706 Z=0
    g83: GeomPoint X=-22.7838 Y=22.0861 Z=0
    g84: GeomPoint X=-25.5897 Y=20.1733 Z=0
    g85: GeomPoint X=-20.0976 Y=20.1833 Z=0
    g86: Ellipse CenterX=-22.8436 CenterY=20.1783 CenterZ=0 NormalX=0 NormalY=0 NormalZ=1 MajorRadius=6.93002 MinorRadius=6.36273 AngleXU=-3.13976
    g87: LineSegment StartX=-101.889 StartY=14.1107 StartZ=0 EndX=-97.7455 EndY=14.1107 EndZ=0
    g88: LineSegment StartX=-93.8155 StartY=14.1107 StartZ=0 EndX=-89.6755 EndY=14.1107 EndZ=0
    g89: LineSegment StartX=-85.7455 StartY=14.1107 StartZ=0 EndX=-81.6055 EndY=14.1107 EndZ=0
    g90: LineSegment StartX=-101.889 StartY=14.1107 StartZ=0 EndX=-101.889 EndY=25.9907 EndZ=0
    g91: LineSegment StartX=-101.889 StartY=25.9907 StartZ=0 EndX=-97.8594 EndY=25.9907 EndZ=0
    g92: LineSegment StartX=-97.8594 StartY=25.9907 StartZ=0 EndX=-97.8594 EndY=24.0907 EndZ=0
    g93: LineSegment StartX=-97.7455 StartY=14.1107 StartZ=0 EndX=-97.7455 EndY=19.9107 EndZ=0
    g94: LineSegment StartX=-89.6755 StartY=14.1107 StartZ=0 EndX=-89.6755 EndY=19.9107 EndZ=0
    g95: LineSegment StartX=-93.8155 StartY=14.1107 StartZ=0 EndX=-93.8155 EndY=21.0107 EndZ=0
    g96-g106: Circle x11 (B-spline internal-alignment scaffolding for g107; pole/knot coordinates omitted)
    g107: BSplineCurve PolesCount=11 KnotsCount=9 Degree=3 IsPeriodic=0
    g108-g116: GeomPoint x9 (B-spline internal-alignment scaffolding for g107; pole/knot coordinates omitted)
    g117: BSplineCurve PolesCount=11 KnotsCount=9 Degree=3 IsPeriodic=0
    g118-g125: Circle x8 (B-spline internal-alignment scaffolding for g126; pole/knot coordinates omitted)
    g126: BSplineCurve PolesCount=8 KnotsCount=6 Degree=3 IsPeriodic=0
    g127-g132: GeomPoint x6 (B-spline internal-alignment scaffolding for g126; pole/knot coordinates omitted)
    g133: BSplineCurve PolesCount=8 KnotsCount=6 Degree=3 IsPeriodic=0
    g134: LineSegment StartX=-85.7455 StartY=21.0107 StartZ=0 EndX=-85.7455 EndY=14.1107 EndZ=0
    g135: LineSegment StartX=-80.0879 StartY=14.1107 StartZ=0 EndX=-75.944 EndY=14.1107 EndZ=0
    g136: LineSegment StartX=-72.014 StartY=14.1107 StartZ=0 EndX=-67.874 EndY=14.1107 EndZ=0
    g137: LineSegment StartX=-63.944 StartY=14.1107 StartZ=0 EndX=-59.804 EndY=14.1107 EndZ=0
    g138: LineSegment StartX=-80.0879 StartY=14.1107 StartZ=0 EndX=-80.0879 EndY=25.9907 EndZ=0
    g139: LineSegment StartX=-80.0879 StartY=25.9907 StartZ=0 EndX=-76.0579 EndY=25.9907 EndZ=0
    g140: LineSegment StartX=-76.0579 StartY=25.9907 StartZ=0 EndX=-76.0579 EndY=24.0907 EndZ=0
    g141: LineSegment StartX=-75.944 StartY=14.1107 StartZ=0 EndX=-75.944 EndY=19.9107 EndZ=0
    g142: LineSegment StartX=-67.874 StartY=14.1107 StartZ=0 EndX=-67.874 EndY=19.9107 EndZ=0
    g143: LineSegment StartX=-72.014 StartY=14.1107 StartZ=0 EndX=-72.014 EndY=21.0107 EndZ=0
    g144-g148: Circle x5 (B-spline internal-alignment scaffolding for g149; pole/knot coordinates omitted)
    g149: BSplineCurve PolesCount=11 KnotsCount=9 Degree=3 IsPeriodic=0
    g150-g158: GeomPoint x9 (B-spline internal-alignment scaffolding for g149; pole/knot coordinates omitted)
    g159: BSplineCurve PolesCount=11 KnotsCount=9 Degree=3 IsPeriodic=0
    g160-g167: Circle x8 (B-spline internal-alignment scaffolding for g168; pole/knot coordinates omitted)
    g168: BSplineCurve PolesCount=8 KnotsCount=6 Degree=3 IsPeriodic=0
    g169-g174: GeomPoint x6 (B-spline internal-alignment scaffolding for g168; pole/knot coordinates omitted)
    g175: BSplineCurve PolesCount=8 KnotsCount=6 Degree=3 IsPeriodic=0
    g176: LineSegment StartX=-63.944 StartY=21.0107 StartZ=0 EndX=-63.944 EndY=14.1107 EndZ=0
    g177: LineSegment StartX=-59.804 StartY=14.1107 StartZ=0 EndX=-59.804 EndY=21.5868 EndZ=0
    g178: BSplineCurve PolesCount=4 KnotsCount=2 Degree=3 IsPeriodic=0
    g179: GeomPoint X=-59.804 Y=21.5868 Z=0
    g180: GeomPoint X=-60.2379 Y=24.0907 Z=0
    g181: LineSegment StartX=-81.6055 StartY=14.1107 StartZ=0 EndX=-81.6055 EndY=21.5868 EndZ=0
    g182: LineSegment StartX=-151.619 StartY=24.0313 StartZ=0 EndX=-145.128 EndY=24.0313 EndZ=0
    g183: Circle CenterX=-82.0394 CenterY=24.0907 CenterZ=0 NormalX=0 NormalY=0 NormalZ=1 AngleXU=0 Radius=1
    g184: Circle CenterX=-81.7131 CenterY=23.2736 CenterZ=0 NormalX=0 NormalY=0 NormalZ=1 AngleXU=0 Radius=1
    g185: Circle CenterX=-81.6055 CenterY=21.5868 CenterZ=0 NormalX=0 NormalY=0 NormalZ=1 AngleXU=0 Radius=1
    g186: BSplineCurve PolesCount=3 KnotsCount=2 Degree=2 IsPeriodic=0
    g187: GeomPoint X=-82.0394 Y=24.0907 Z=0
    g188: GeomPoint X=-81.6055 Y=21.5868 Z=0
    g189: Ellipse CenterX=-37.3522 CenterY=19.9515 CenterZ=0 NormalX=0 NormalY=0 NormalZ=1 MajorRadius=2.99755 MinorRadius=2.49 AngleXU=1.5708
    g190: GeomPoint X=-37.3522 Y=21.6203 Z=0
    g191: GeomPoint X=-37.3522 Y=18.2826 Z=0
    g192: ArcOfEllipse CenterX=-38.7647 CenterY=20.06 CenterZ=0 NormalX=0 NormalY=0 NormalZ=1 MajorRadius=6.30025 MinorRadius=5.3849 AngleXU=1.57276 StartAngle=5.50632 EndAngle=10.3035
    g193: GeomPoint X=-38.7711 Y=23.3304 Z=0
    g194: GeomPoint X=-38.7583 Y=16.7895 Z=0
    g195: LineSegment StartX=-34.6109 StartY=14.1107 StartZ=0 EndX=-30.8984 EndY=14.1107 EndZ=0
    g196: LineSegment StartX=-30.8984 StartY=14.1107 StartZ=0 EndX=-30.8984 EndY=31.1784 EndZ=0
    g197: LineSegment StartX=-30.8984 StartY=31.1784 StartZ=0 EndX=-34.9984 EndY=31.1784 EndZ=0
    g198: LineSegment StartX=-34.9984 StartY=24.5602 StartZ=0 EndX=-34.9984 EndY=31.1784 EndZ=0
    g199: LineSegment StartX=-34.6109 StartY=16.0476 StartZ=0 EndX=-34.6109 EndY=14.1107 EndZ=0
    g200: LineSegment StartX=-14.8781 StartY=14.1107 StartZ=0 EndX=-10.5106 EndY=14.1107 EndZ=0
    g201: LineSegment StartX=-14.8781 StartY=14.1107 StartZ=0 EndX=-14.8781 EndY=25.8504 EndZ=0
    g202: LineSegment StartX=-14.8781 StartY=25.8504 StartZ=0 EndX=-10.8534 EndY=25.8504 EndZ=0
    g203: LineSegment StartX=-10.8534 StartY=25.8504 StartZ=0 EndX=-10.8534 EndY=24.0923 EndZ=0
    g204: LineSegment StartX=-10.5106 StartY=14.1107 StartZ=0 EndX=-10.5106 EndY=19.7752 EndZ=0
    g205: LineSegment StartX=-5.96397 StartY=25.9304 StartZ=0 EndX=-5.96397 EndY=22.574 EndZ=0
    g206-g214: Circle x9 (B-spline internal-alignment scaffolding for g215; pole/knot coordinates omitted)
    g215: BSplineCurve PolesCount=9 KnotsCount=7 Degree=3 IsPeriodic=0
    g216-g222: GeomPoint x7 (B-spline internal-alignment scaffolding for g215; pole/knot coordinates omitted)
    g223-g232: Circle x10 (B-spline internal-alignment scaffolding for g233; pole/knot coordinates omitted)
    g233: BSplineCurve PolesCount=10 KnotsCount=8 Degree=3 IsPeriodic=0
    g234-g241: GeomPoint x8 (B-spline internal-alignment scaffolding for g233; pole/knot coordinates omitted)
    g242: LineSegment StartX=-1.58923 StartY=21.0696 StartZ=0 EndX=2.62034 EndY=21.0696 EndZ=0
    g243: LineSegment StartX=-1.55856 StartY=18.7342 StartZ=0 EndX=6.45946 EndY=18.7342 EndZ=0
    g244: LineSegment StartX=5.29231 StartY=17.386 StartZ=0 EndX=5.29231 EndY=14.3674 EndZ=0
    g245-g269: Circle x25 (B-spline internal-alignment scaffolding for g270; pole/knot coordinates omitted)
    g270: BSplineCurve PolesCount=25 KnotsCount=23 Degree=3 IsPeriodic=0
    g271-g293: GeomPoint x23 (B-spline internal-alignment scaffolding for g270; pole/knot coordinates omitted)
    g294-g304: Circle x11 (B-spline internal-alignment scaffolding for g305; pole/knot coordinates omitted)
    g305: BSplineCurve PolesCount=11 KnotsCount=9 Degree=3 IsPeriodic=0
    g306-g314: GeomPoint x9 (B-spline internal-alignment scaffolding for g305; pole/knot coordinates omitted)
    g315-g326: Circle x12 (B-spline internal-alignment scaffolding for g327; pole/knot coordinates omitted)
    g327: BSplineCurve PolesCount=12 KnotsCount=10 Degree=3 IsPeriodic=0
    g328-g337: GeomPoint x10 (B-spline internal-alignment scaffolding for g327; pole/knot coordinates omitted)
  constraints (252):
    c: Coincident(g1,g0)
    c: Horizontal(g0)
    c: Vertical(g1)
    c: Coincident(g2,g3)
    c: Coincident(g3,g4)
    c: Horizontal(g4)
    c: Horizontal(g2)
    c: Vertical(g3)
    c: Block(g1)
    c: Distance(g3) = 4.86
    c: Block(g4)
    c: Distance(g0) = 10.8
    c: Distance(g2) = 10.8
    c: Coincident(g5,g0)
    c: Coincident(g6,g4)
    c: Coincident(g6,g2)
    c: Block(g8)
    c: Block(g7)
    c: Coincident(g9,g8)
    c: Coincident(g9,g7)
    c: Vertical(g9)
    c: Coincident(g10,g7)
    c: Coincident(g10,g8)
    c: Vertical(g10)
    c: Weight(g11) = 1
    c: Equal(g11, g12-g21) x10
    c: InternalAlignment(g11-g21 -> g22) x11
    c: InternalAlignment(g23-g31 -> g22) x9
    c: Block(g22)
    c: Weight(g32) = 1
    c: Equal(g32, g33-g49) x17
    c: InternalAlignment(g32-g49 -> g50) x18
    c: InternalAlignment(g51-g66 -> g50) x16
    c: Block(g50)
    c: Coincident(g67,g50)
    c: Coincident(g67,g22)
    c: Coincident(g68,g22)
    c: Coincident(g68,g50)
    c: InternalAlignment(g70,g69)
    c: InternalAlignment(g71,g69)
    c: Block(g69)
    c: InternalAlignment(g73,g72)
    c: InternalAlignment(g74,g72)
    c: Block(g72)
    c: InternalAlignment(g76,g75)
    c: InternalAlignment(g77,g75)
    c: InternalAlignment(g78,g80)
    c: InternalAlignment(g79,g80)
    c: Block(g80)
    c: Coincident(g75,g80)
    c: Block(g75)
    c: InternalAlignment(g82,g81)
    c: InternalAlignment(g83,g81)
    c: InternalAlignment(g84,g86)
    c: InternalAlignment(g85,g86)
    c: Block(g86)
    c: Coincident(g81,g86)
    c: Block(g81)
    c: Horizontal(g87)
    c: Block(g87)
    c: Horizontal(g88)
    c: Distance(g88) = 4.14
    c: Horizontal(g89)
    c: Equal(g88,g89) = 4.14
    c: Block(g89)
    c: Block(g88)
    c: Coincident(g90,g87)
    c: Vertical(g90)
    c: Distance(g90) = 11.88
    c: Coincident(g91,g90)
    c: Horizontal(g91)
    c: Coincident(g92,g91)
    c: Vertical(g92)
    c: Distance(g91) = 4.03
    c: Distance(g92) = 1.9
    c: Coincident(g93,g87)
    c: Vertical(g93)
    c: Vertical(g94)
    c: Coincident(g94,g88)
    c: Distance(g93) = 5.8
    c: Distance(g94) = 5.8
    c: Vertical(g95)
    c: Coincident(g95,g88)
    c: Distance(g95) = 6.9
    c: Coincident(g107,g92)
    c: Weight(g96) = 1
    c: Equal(g96, g97-g106) x10
    c: InternalAlignment(g96-g106 -> g107) x11
    c: InternalAlignment(g108-g116 -> g107) x9
    c: Block(g107)
    c: Block(g117)
    c: Coincident(g126,g93)
    c: Weight(g118) = 1
    c: Equal(g118, g119-g125) x7
    c: Coincident(g126,g95)
    c: InternalAlignment(g118-g125 -> g126) x8
    c: InternalAlignment(g127-g132 -> g126) x6
    c: Coincident(g133,g94)
    c: Block(g126)
    c: Block(g133)
    c: Coincident(g134,g133)
    c: Coincident(g134,g89)
    c: Vertical(g134)
    c: Horizontal(g135)
    c: Block(g135)
    c: Horizontal(g136)
    c: Equal(g88,g136) = 4.14
    c: Horizontal(g137)
    c: Equal(g136,g137) = 4.14
    c: Block(g137)
    c: Block(g136)
    c: Coincident(g138,g135)
    c: Vertical(g138)
    c: Equal(g90,g138) = 11.88
    c: Coincident(g139,g138)
    c: Horizontal(g139)
    c: Coincident(g140,g139)
    c: Vertical(g140)
    c: Equal(g91,g139) = 4.03
    c: Equal(g92,g140) = 1.9
    c: Coincident(g141,g135)
    c: Vertical(g141)
    c: Vertical(g142)
    c: Coincident(g142,g136)
    c: Equal(g93,g141) = 5.8
    c: Equal(g94,g142) = 5.8
    c: Vertical(g143)
    c: Coincident(g143,g136)
    c: Equal(g95,g143) = 6.9
    c: Coincident(g149,g140)
    c: Equal(g96,g144) = 1
    c: Equal(g144, g145-g148) x4
    c: InternalAlignment(g144-g148 -> g149) x5
    c: InternalAlignment(g150-g158 -> g149) x9
    c: Block(g149)
    c: Block(g159)
    c: Coincident(g168,g141)
    c: Equal(g118,g160) = 1
    c: Equal(g160, g161-g167) x7
    c: Coincident(g168,g143)
    c: InternalAlignment(g160-g167 -> g168) x8
    c: InternalAlignment(g169-g174 -> g168) x6
    c: Coincident(g175,g142)
    c: Block(g168)
    c: Block(g175)
    c: Coincident(g176,g175)
    c: Coincident(g176,g137)
    c: Vertical(g176)
    c: Coincident(g177,g137)
    c: Vertical(g177)
    c: Coincident(g178,g177)
    c: Coincident(g178,g159)
    c: InternalAlignment(g179,g178)
    c: InternalAlignment(g180,g178)
    c: Block(g178)
    c: Vertical(g181)
    c: Coincident(g181,g89)
    c: Block(g5)
    c: Coincident(g182,g1)
    c: Coincident(g182,g5)
    c: Horizontal(g182)
    c: Coincident(g186,g117)
    c: Weight(g183) = 1
    c: Equal(g183,g184)
    c: Equal(g183,g185)
    c: Coincident(g186,g181)
    c: InternalAlignment(g183,g186)
    c: InternalAlignment(g184,g186)
    c: InternalAlignment(g185,g186)
    c: InternalAlignment(g187,g186)
    c: InternalAlignment(g188,g186)
    c: Block(g186)
    c: InternalAlignment(g190,g189)
    c: InternalAlignment(g191,g189)
    c: Block(g189)
    c: InternalAlignment(g193,g192)
    c: InternalAlignment(g194,g192)
    c: Block(g192)
    c: Horizontal(g195)
    c: Block(g195)
    c: Coincident(g196,g195)
    c: Vertical(g196)
    c: Block(g196)
    c: Distance(g195) = 3.71244
    c: Coincident(g197,g196)
    c: Horizontal(g197)
    c: Distance(g197) = 4.1
    c: Coincident(g198,g192)
    c: Coincident(g198,g197)
    c: Vertical(g198)
    c: Block(g198)
    c: Coincident(g199,g192)
    c: Coincident(g199,g195)
    c: Vertical(g199)
    c: Block(g199)
    c: Horizontal(g200)
    c: Block(g200)
    c: Coincident(g201,g200)
    c: Vertical(g201)
    c: Block(g201)
    c: Coincident(g202,g201)
    c: Horizontal(g202)
    c: Block(g202)
    c: Coincident(g203,g202)
    c: Vertical(g203)
    c: Block(g203)
    c: Coincident(g204,g200)
    c: Vertical(g204)
    c: Block(g204)
    c: Coincident(g215,g203)
    c: Weight(g206) = 1
    c: Equal(g206, g207-g214) x8
    c: Coincident(g215,g205)
    c: InternalAlignment(g206-g214 -> g215) x9
    c: InternalAlignment(g216-g222 -> g215) x7
    c: Coincident(g233,g204)
    c: Weight(g223) = 1
    c: Equal(g223, g224-g232) x9
    c: Coincident(g233,g205)
    c: InternalAlignment(g223-g232 -> g233) x10
    c: InternalAlignment(g234-g241 -> g233) x8
    c: Vertical(g205)
    c: Block(g205)
    c: Block(g215)
    c: Block(g233)
    c: Horizontal(g242)
    c: Horizontal(g243)
    c: Block(g242)
    c: Block(g243)
    c: Vertical(g244)
    c: Block(g244)
    c: Coincident(g270,g243)
    c: Weight(g245) = 1
    c: Equal(g245, g246-g269) x24
    c: Coincident(g270,g244)
    c: InternalAlignment(g245-g269 -> g270) x25
    c: InternalAlignment(g271-g293 -> g270) x23
    c: Coincident(g305,g242)
    c: Weight(g294) = 1
    c: Equal(g294, g295-g304) x10
    c: Coincident(g305,g242)
    c: InternalAlignment(g294-g304 -> g305) x11
    c: InternalAlignment(g306-g314 -> g305) x9
    c: Block(g305)
    c: Coincident(g327,g243)
    c: Weight(g315) = 1
    c: Equal(g315, g316-g326) x11
    c: Coincident(g327,g244)
    c: InternalAlignment(g315-g326 -> g327) x12
    c: InternalAlignment(g328-g337 -> g327) x10
    c: Block(g327)
    c: Block(g270)
FEATURE [PartDesign::Body] Body  label="CommodoreLogoAndText"
  Group = -> [Sketch083]
  Origin = -> Origin
FEATURE [Part::Extrusion] Extrude074  label="CommodoreLogoAndText001"
  Base = -> Sketch083
  Dir = (0,0,1)
  DirMode = 2
  FaceMakerClass = Part::FaceMakerBullseye
  LengthFwd = 10
  LengthRev = 0
  Solid = true
  Symmetric = false
FEATURE [Part::FeaturePython] Clone  label="CommodoreLogoAndTextScale"  # Draft clone (typed FeaturePython)
  AttacherType = Attacher::AttachEngine3D
  Fuse = false
  Objects = -> [Extrude074]
  Placement = pos=(111,5.37,-11.6) rot=(0,0,1;0rad)
  Scale = (0.62,0.62,1)
FEATURE [Part::Mirroring] Part__Mirroring  label="CommodoreLogoAndTextScale (Mirror #1)"
  Base = (0,0,0)
  Normal = (1,0,0)
  Placement = pos=(123.576,0,0) rot=(0,0,1;0rad)
  Source = -> Clone
FEATURE [Sketcher::SketchObject] Sketch084
  FullyConstrained = true
  MapMode = 5
  Support = -> [XY_Plane001]
  sketch-geometry (338):
    g0: LineSegment StartX=-151.619 StartY=28.8932 StartZ=0 EndX=-140.819 EndY=28.8932 EndZ=0
    g1: LineSegment StartX=-151.619 StartY=24.0313 StartZ=0 EndX=-151.619 EndY=28.8932 EndZ=0
    g2: LineSegment StartX=-140.819 StartY=17.7713 StartZ=0 EndX=-151.619 EndY=17.7713 EndZ=0
    g3: LineSegment StartX=-151.619 StartY=17.7713 StartZ=0 EndX=-151.619 EndY=22.6313 EndZ=0
    g4: LineSegment StartX=-151.619 StartY=22.6313 StartZ=0 EndX=-145.128 EndY=22.6313 EndZ=0
    g5: LineSegment StartX=-145.128 StartY=24.0313 StartZ=0 EndX=-140.819 EndY=28.8932 EndZ=0
    g6: LineSegment StartX=-145.128 StartY=22.6313 StartZ=0 EndX=-140.819 EndY=17.7713 EndZ=0
    g7: ArcOfCircle CenterX=-155.157 CenterY=23.3323 CenterZ=0 NormalX=0 NormalY=0 NormalZ=1 AngleXU=0 Radius=6.92354 StartAngle=1.03434 EndAngle=5.24885
    g8: ArcOfCircle CenterX=-155.157 CenterY=23.3323 CenterZ=0 NormalX=0 NormalY=0 NormalZ=1 AngleXU=0 Radius=12.6269 StartAngle=1.28675 EndAngle=4.99643
    g9: LineSegment StartX=-151.619 StartY=35.4532 StartZ=0 EndX=-151.619 EndY=29.2832 EndZ=0
    g10: LineSegment StartX=-151.619 StartY=17.3813 StartZ=0 EndX=-151.619 EndY=11.2113 EndZ=0
    g11-g21: Circle x11 (B-spline internal-alignment scaffolding for g22; pole/knot coordinates omitted)
    g22: BSplineCurve PolesCount=11 KnotsCount=9 Degree=3 IsPeriodic=0
    g23-g31: GeomPoint x9 (B-spline internal-alignment scaffolding for g22; pole/knot coordinates omitted)
    g32-g49: Circle x18 (B-spline internal-alignment scaffolding for g50; pole/knot coordinates omitted)
    g50: BSplineCurve PolesCount=18 KnotsCount=16 Degree=3 IsPeriodic=0
    g51-g66: GeomPoint x16 (B-spline internal-alignment scaffolding for g50; pole/knot coordinates omitted)
    g67: LineSegment StartX=-117.124 StartY=30.093 StartZ=0 EndX=-117.603 EndY=26.5272 EndZ=0
    g68: LineSegment StartX=-117.603 StartY=17.8472 StartZ=0 EndX=-117.124 EndY=14.2659 EndZ=0
    g69: Ellipse CenterX=-109.671 CenterY=20.025 CenterZ=0 NormalX=0 NormalY=0 NormalZ=1 MajorRadius=3.34798 MinorRadius=2.71052 AngleXU=-1.56793
    g70: GeomPoint X=-109.666 Y=18.0598 Z=0
    g71: GeomPoint X=-109.677 Y=21.9902 Z=0
    g72: Ellipse CenterX=-109.671 CenterY=20.0123 CenterZ=0 NormalX=0 NormalY=0 NormalZ=1 MajorRadius=6.93002 MinorRadius=6.36273 AngleXU=-3.13976
    g73: GeomPoint X=-112.417 Y=20.0073 Z=0
    g74: GeomPoint X=-106.925 Y=20.0173 Z=0
    g75: Ellipse CenterX=-51.7682 CenterY=20.1463 CenterZ=0 NormalX=0 NormalY=0 NormalZ=1 MajorRadius=3.19279 MinorRadius=2.71052 AngleXU=-1.52774
    g76: GeomPoint X=-51.6955 Y=18.4606 Z=0
    g77: GeomPoint X=-51.8408 Y=21.832 Z=0
    g78: GeomPoint X=-54.5142 Y=20.1413 Z=0
    g79: GeomPoint X=-49.0221 Y=20.1513 Z=0
    g80: Ellipse CenterX=-51.7682 CenterY=20.1463 CenterZ=0 NormalX=0 NormalY=0 NormalZ=1 MajorRadius=6.93002 MinorRadius=6.36273 AngleXU=-3.13976
    g81: Ellipse CenterX=-22.8436 CenterY=20.1783 CenterZ=0 NormalX=0 NormalY=0 NormalZ=1 MajorRadius=3.31512 MinorRadius=2.71052 AngleXU=-1.60214
    g82: GeomPoint X=-22.9034 Y=18.2706 Z=0
    g83: GeomPoint X=-22.7838 Y=22.0861 Z=0
    g84: GeomPoint X=-25.5897 Y=20.1733 Z=0
    g85: GeomPoint X=-20.0976 Y=20.1833 Z=0
    g86: Ellipse CenterX=-22.8436 CenterY=20.1783 CenterZ=0 NormalX=0 NormalY=0 NormalZ=1 MajorRadius=6.93002 MinorRadius=6.36273 AngleXU=-3.13976
    g87: LineSegment StartX=-101.889 StartY=14.1107 StartZ=0 EndX=-97.7455 EndY=14.1107 EndZ=0
    g88: LineSegment StartX=-93.8155 StartY=14.1107 StartZ=0 EndX=-89.6755 EndY=14.1107 EndZ=0
    g89: LineSegment StartX=-85.7455 StartY=14.1107 StartZ=0 EndX=-81.6055 EndY=14.1107 EndZ=0
    g90: LineSegment StartX=-101.889 StartY=14.1107 StartZ=0 EndX=-101.889 EndY=25.9907 EndZ=0
    g91: LineSegment StartX=-101.889 StartY=25.9907 StartZ=0 EndX=-97.8594 EndY=25.9907 EndZ=0
    g92: LineSegment StartX=-97.8594 StartY=25.9907 StartZ=0 EndX=-97.8594 EndY=24.0907 EndZ=0
    g93: LineSegment StartX=-97.7455 StartY=14.1107 StartZ=0 EndX=-97.7455 EndY=19.9107 EndZ=0
    g94: LineSegment StartX=-89.6755 StartY=14.1107 StartZ=0 EndX=-89.6755 EndY=19.9107 EndZ=0
    g95: LineSegment StartX=-93.8155 StartY=14.1107 StartZ=0 EndX=-93.8155 EndY=21.0107 EndZ=0
    g96-g106: Circle x11 (B-spline internal-alignment scaffolding for g107; pole/knot coordinates omitted)
    g107: BSplineCurve PolesCount=11 KnotsCount=9 Degree=3 IsPeriodic=0
    g108-g116: GeomPoint x9 (B-spline internal-alignment scaffolding for g107; pole/knot coordinates omitted)
    g117: BSplineCurve PolesCount=11 KnotsCount=9 Degree=3 IsPeriodic=0
    g118-g125: Circle x8 (B-spline internal-alignment scaffolding for g126; pole/knot coordinates omitted)
    g126: BSplineCurve PolesCount=8 KnotsCount=6 Degree=3 IsPeriodic=0
    g127-g132: GeomPoint x6 (B-spline internal-alignment scaffolding for g126; pole/knot coordinates omitted)
    g133: BSplineCurve PolesCount=8 KnotsCount=6 Degree=3 IsPeriodic=0
    g134: LineSegment StartX=-85.7455 StartY=21.0107 StartZ=0 EndX=-85.7455 EndY=14.1107 EndZ=0
    g135: LineSegment StartX=-80.0879 StartY=14.1107 StartZ=0 EndX=-75.944 EndY=14.1107 EndZ=0
    g136: LineSegment StartX=-72.014 StartY=14.1107 StartZ=0 EndX=-67.874 EndY=14.1107 EndZ=0
    g137: LineSegment StartX=-63.944 StartY=14.1107 StartZ=0 EndX=-59.804 EndY=14.1107 EndZ=0
    g138: LineSegment StartX=-80.0879 StartY=14.1107 StartZ=0 EndX=-80.0879 EndY=25.9907 EndZ=0
    g139: LineSegment StartX=-80.0879 StartY=25.9907 StartZ=0 EndX=-76.0579 EndY=25.9907 EndZ=0
    g140: LineSegment StartX=-76.0579 StartY=25.9907 StartZ=0 EndX=-76.0579 EndY=24.0907 EndZ=0
    g141: LineSegment StartX=-75.944 StartY=14.1107 StartZ=0 EndX=-75.944 EndY=19.9107 EndZ=0
    g142: LineSegment StartX=-67.874 StartY=14.1107 StartZ=0 EndX=-67.874 EndY=19.9107 EndZ=0
    g143: LineSegment StartX=-72.014 StartY=14.1107 StartZ=0 EndX=-72.014 EndY=21.0107 EndZ=0
    g144-g148: Circle x5 (B-spline internal-alignment scaffolding for g149; pole/knot coordinates omitted)
    g149: BSplineCurve PolesCount=11 KnotsCount=9 Degree=3 IsPeriodic=0
    g150-g158: GeomPoint x9 (B-spline internal-alignment scaffolding for g149; pole/knot coordinates omitted)
    g159: BSplineCurve PolesCount=11 KnotsCount=9 Degree=3 IsPeriodic=0
    g160-g167: Circle x8 (B-spline internal-alignment scaffolding for g168; pole/knot coordinates omitted)
    g168: BSplineCurve PolesCount=8 KnotsCount=6 Degree=3 IsPeriodic=0
    g169-g174: GeomPoint x6 (B-spline internal-alignment scaffolding for g168; pole/knot coordinates omitted)
    g175: BSplineCurve PolesCount=8 KnotsCount=6 Degree=3 IsPeriodic=0
    g176: LineSegment StartX=-63.944 StartY=21.0107 StartZ=0 EndX=-63.944 EndY=14.1107 EndZ=0
    g177: LineSegment StartX=-59.804 StartY=14.1107 StartZ=0 EndX=-59.804 EndY=21.5868 EndZ=0
    g178: BSplineCurve PolesCount=4 KnotsCount=2 Degree=3 IsPeriodic=0
    g179: GeomPoint X=-59.804 Y=21.5868 Z=0
    g180: GeomPoint X=-60.2379 Y=24.0907 Z=0
    g181: LineSegment StartX=-81.6055 StartY=14.1107 StartZ=0 EndX=-81.6055 EndY=21.5868 EndZ=0
    g182: LineSegment StartX=-151.619 StartY=24.0313 StartZ=0 EndX=-145.128 EndY=24.0313 EndZ=0
    g183: Circle CenterX=-82.0394 CenterY=24.0907 CenterZ=0 NormalX=0 NormalY=0 NormalZ=1 AngleXU=0 Radius=1
    g184: Circle CenterX=-81.7131 CenterY=23.2736 CenterZ=0 NormalX=0 NormalY=0 NormalZ=1 AngleXU=0 Radius=1
    g185: Circle CenterX=-81.6055 CenterY=21.5868 CenterZ=0 NormalX=0 NormalY=0 NormalZ=1 AngleXU=0 Radius=1
    g186: BSplineCurve PolesCount=3 KnotsCount=2 Degree=2 IsPeriodic=0
    g187: GeomPoint X=-82.0394 Y=24.0907 Z=0
    g188: GeomPoint X=-81.6055 Y=21.5868 Z=0
    g189: Ellipse CenterX=-37.3522 CenterY=19.9515 CenterZ=0 NormalX=0 NormalY=0 NormalZ=1 MajorRadius=2.99755 MinorRadius=2.49 AngleXU=1.5708
    g190: GeomPoint X=-37.3522 Y=21.6203 Z=0
    g191: GeomPoint X=-37.3522 Y=18.2826 Z=0
    g192: ArcOfEllipse CenterX=-38.7647 CenterY=20.06 CenterZ=0 NormalX=0 NormalY=0 NormalZ=1 MajorRadius=6.30025 MinorRadius=5.3849 AngleXU=1.57276 StartAngle=5.50632 EndAngle=10.3035
    g193: GeomPoint X=-38.7711 Y=23.3304 Z=0
    g194: GeomPoint X=-38.7583 Y=16.7895 Z=0
    g195: LineSegment StartX=-34.6109 StartY=14.1107 StartZ=0 EndX=-30.8984 EndY=14.1107 EndZ=0
    g196: LineSegment StartX=-30.8984 StartY=14.1107 StartZ=0 EndX=-30.8984 EndY=31.1784 EndZ=0
    g197: LineSegment StartX=-30.8984 StartY=31.1784 StartZ=0 EndX=-34.9984 EndY=31.1784 EndZ=0
    g198: LineSegment StartX=-34.9984 StartY=24.5602 StartZ=0 EndX=-34.9984 EndY=31.1784 EndZ=0
    g199: LineSegment StartX=-34.6109 StartY=16.0476 StartZ=0 EndX=-34.6109 EndY=14.1107 EndZ=0
    g200: LineSegment StartX=-14.8781 StartY=14.1107 StartZ=0 EndX=-10.5106 EndY=14.1107 EndZ=0
    g201: LineSegment StartX=-14.8781 StartY=14.1107 StartZ=0 EndX=-14.8781 EndY=25.8504 EndZ=0
    g202: LineSegment StartX=-14.8781 StartY=25.8504 StartZ=0 EndX=-10.8534 EndY=25.8504 EndZ=0
    g203: LineSegment StartX=-10.8534 StartY=25.8504 StartZ=0 EndX=-10.8534 EndY=24.0923 EndZ=0
    g204: LineSegment StartX=-10.5106 StartY=14.1107 StartZ=0 EndX=-10.5106 EndY=19.7752 EndZ=0
    g205: LineSegment StartX=-5.96397 StartY=25.9304 StartZ=0 EndX=-5.96397 EndY=22.574 EndZ=0
    g206-g214: Circle x9 (B-spline internal-alignment scaffolding for g215; pole/knot coordinates omitted)
    g215: BSplineCurve PolesCount=9 KnotsCount=7 Degree=3 IsPeriodic=0
    g216-g222: GeomPoint x7 (B-spline internal-alignment scaffolding for g215; pole/knot coordinates omitted)
    g223-g232: Circle x10 (B-spline internal-alignment scaffolding for g233; pole/knot coordinates omitted)
    g233: BSplineCurve PolesCount=10 KnotsCount=8 Degree=3 IsPeriodic=0
    g234-g241: GeomPoint x8 (B-spline internal-alignment scaffolding for g233; pole/knot coordinates omitted)
    g242: LineSegment StartX=-1.58923 StartY=21.0696 StartZ=0 EndX=2.62034 EndY=21.0696 EndZ=0
    g243: LineSegment StartX=-1.55856 StartY=18.7342 StartZ=0 EndX=6.45946 EndY=18.7342 EndZ=0
    g244: LineSegment StartX=5.29231 StartY=17.386 StartZ=0 EndX=5.29231 EndY=14.3674 EndZ=0
    g245-g269: Circle x25 (B-spline internal-alignment scaffolding for g270; pole/knot coordinates omitted)
    g270: BSplineCurve PolesCount=25 KnotsCount=23 Degree=3 IsPeriodic=0
    g271-g293: GeomPoint x23 (B-spline internal-alignment scaffolding for g270; pole/knot coordinates omitted)
    g294-g304: Circle x11 (B-spline internal-alignment scaffolding for g305; pole/knot coordinates omitted)
    g305: BSplineCurve PolesCount=11 KnotsCount=9 Degree=3 IsPeriodic=0
    g306-g314: GeomPoint x9 (B-spline internal-alignment scaffolding for g305; pole/knot coordinates omitted)
    g315-g326: Circle x12 (B-spline internal-alignment scaffolding for g327; pole/knot coordinates omitted)
    g327: BSplineCurve PolesCount=12 KnotsCount=10 Degree=3 IsPeriodic=0
    g328-g337: GeomPoint x10 (B-spline internal-alignment scaffolding for g327; pole/knot coordinates omitted)
  constraints (252):
    c: Coincident(g1,g0)
    c: Horizontal(g0)
    c: Vertical(g1)
    c: Coincident(g2,g3)
    c: Coincident(g3,g4)
    c: Horizontal(g4)
    c: Horizontal(g2)
    c: Vertical(g3)
    c: Block(g1)
    c: Distance(g3) = 4.86
    c: Block(g4)
    c: Distance(g0) = 10.8
    c: Distance(g2) = 10.8
    c: Coincident(g5,g0)
    c: Coincident(g6,g4)
    c: Coincident(g6,g2)
    c: Block(g8)
    c: Block(g7)
    c: Coincident(g9,g8)
    c: Coincident(g9,g7)
    c: Vertical(g9)
    c: Coincident(g10,g7)
    c: Coincident(g10,g8)
    c: Vertical(g10)
    c: Weight(g11) = 1
    c: Equal(g11, g12-g21) x10
    c: InternalAlignment(g11-g21 -> g22) x11
    c: InternalAlignment(g23-g31 -> g22) x9
    c: Block(g22)
    c: Weight(g32) = 1
    c: Equal(g32, g33-g49) x17
    c: InternalAlignment(g32-g49 -> g50) x18
    c: InternalAlignment(g51-g66 -> g50) x16
    c: Block(g50)
    c: Coincident(g67,g50)
    c: Coincident(g67,g22)
    c: Coincident(g68,g22)
    c: Coincident(g68,g50)
    c: InternalAlignment(g70,g69)
    c: InternalAlignment(g71,g69)
    c: Block(g69)
    c: InternalAlignment(g73,g72)
    c: InternalAlignment(g74,g72)
    c: Block(g72)
    c: InternalAlignment(g76,g75)
    c: InternalAlignment(g77,g75)
    c: InternalAlignment(g78,g80)
    c: InternalAlignment(g79,g80)
    c: Block(g80)
    c: Coincident(g75,g80)
    c: Block(g75)
    c: InternalAlignment(g82,g81)
    c: InternalAlignment(g83,g81)
    c: InternalAlignment(g84,g86)
    c: InternalAlignment(g85,g86)
    c: Block(g86)
    c: Coincident(g81,g86)
    c: Block(g81)
    c: Horizontal(g87)
    c: Block(g87)
    c: Horizontal(g88)
    c: Distance(g88) = 4.14
    c: Horizontal(g89)
    c: Equal(g88,g89) = 4.14
    c: Block(g89)
    c: Block(g88)
    c: Coincident(g90,g87)
    c: Vertical(g90)
    c: Distance(g90) = 11.88
    c: Coincident(g91,g90)
    c: Horizontal(g91)
    c: Coincident(g92,g91)
    c: Vertical(g92)
    c: Distance(g91) = 4.03
    c: Distance(g92) = 1.9
    c: Coincident(g93,g87)
    c: Vertical(g93)
    c: Vertical(g94)
    c: Coincident(g94,g88)
    c: Distance(g93) = 5.8
    c: Distance(g94) = 5.8
    c: Vertical(g95)
    c: Coincident(g95,g88)
    c: Distance(g95) = 6.9
    c: Coincident(g107,g92)
    c: Weight(g96) = 1
    c: Equal(g96, g97-g106) x10
    c: InternalAlignment(g96-g106 -> g107) x11
    c: InternalAlignment(g108-g116 -> g107) x9
    c: Block(g107)
    c: Block(g117)
    c: Coincident(g126,g93)
    c: Weight(g118) = 1
    c: Equal(g118, g119-g125) x7
    c: Coincident(g126,g95)
    c: InternalAlignment(g118-g125 -> g126) x8
    c: InternalAlignment(g127-g132 -> g126) x6
    c: Coincident(g133,g94)
    c: Block(g126)
    c: Block(g133)
    c: Coincident(g134,g133)
    c: Coincident(g134,g89)
    c: Vertical(g134)
    c: Horizontal(g135)
    c: Block(g135)
    c: Horizontal(g136)
    c: Equal(g88,g136) = 4.14
    c: Horizontal(g137)
    c: Equal(g136,g137) = 4.14
    c: Block(g137)
    c: Block(g136)
    c: Coincident(g138,g135)
    c: Vertical(g138)
    c: Equal(g90,g138) = 11.88
    c: Coincident(g139,g138)
    c: Horizontal(g139)
    c: Coincident(g140,g139)
    c: Vertical(g140)
    c: Equal(g91,g139) = 4.03
    c: Equal(g92,g140) = 1.9
    c: Coincident(g141,g135)
    c: Vertical(g141)
    c: Vertical(g142)
    c: Coincident(g142,g136)
    c: Equal(g93,g141) = 5.8
    c: Equal(g94,g142) = 5.8
    c: Vertical(g143)
    c: Coincident(g143,g136)
    c: Equal(g95,g143) = 6.9
    c: Coincident(g149,g140)
    c: Equal(g96,g144) = 1
    c: Equal(g144, g145-g148) x4
    c: InternalAlignment(g144-g148 -> g149) x5
    c: InternalAlignment(g150-g158 -> g149) x9
    c: Block(g149)
    c: Block(g159)
    c: Coincident(g168,g141)
    c: Equal(g118,g160) = 1
    c: Equal(g160, g161-g167) x7
    c: Coincident(g168,g143)
    c: InternalAlignment(g160-g167 -> g168) x8
    c: InternalAlignment(g169-g174 -> g168) x6
    c: Coincident(g175,g142)
    c: Block(g168)
    c: Block(g175)
    c: Coincident(g176,g175)
    c: Coincident(g176,g137)
    c: Vertical(g176)
    c: Coincident(g177,g137)
    c: Vertical(g177)
    c: Coincident(g178,g177)
    c: Coincident(g178,g159)
    c: InternalAlignment(g179,g178)
    c: InternalAlignment(g180,g178)
    c: Block(g178)
    c: Vertical(g181)
    c: Coincident(g181,g89)
    c: Block(g5)
    c: Coincident(g182,g1)
    c: Coincident(g182,g5)
    c: Horizontal(g182)
    c: Coincident(g186,g117)
    c: Weight(g183) = 1
    c: Equal(g183,g184)
    c: Equal(g183,g185)
    c: Coincident(g186,g181)
    c: InternalAlignment(g183,g186)
    c: InternalAlignment(g184,g186)
    c: InternalAlignment(g185,g186)
    c: InternalAlignment(g187,g186)
    c: InternalAlignment(g188,g186)
    c: Block(g186)
    c: InternalAlignment(g190,g189)
    c: InternalAlignment(g191,g189)
    c: Block(g189)
    c: InternalAlignment(g193,g192)
    c: InternalAlignment(g194,g192)
    c: Block(g192)
    c: Horizontal(g195)
    c: Block(g195)
    c: Coincident(g196,g195)
    c: Vertical(g196)
    c: Block(g196)
    c: Distance(g195) = 3.71244
    c: Coincident(g197,g196)
    c: Horizontal(g197)
    c: Distance(g197) = 4.1
    c: Coincident(g198,g192)
    c: Coincident(g198,g197)
    c: Vertical(g198)
    c: Block(g198)
    c: Coincident(g199,g192)
    c: Coincident(g199,g195)
    c: Vertical(g199)
    c: Block(g199)
    c: Horizontal(g200)
    c: Block(g200)
    c: Coincident(g201,g200)
    c: Vertical(g201)
    c: Block(g201)
    c: Coincident(g202,g201)
    c: Horizontal(g202)
    c: Block(g202)
    c: Coincident(g203,g202)
    c: Vertical(g203)
    c: Block(g203)
    c: Coincident(g204,g200)
    c: Vertical(g204)
    c: Block(g204)
    c: Coincident(g215,g203)
    c: Weight(g206) = 1
    c: Equal(g206, g207-g214) x8
    c: Coincident(g215,g205)
    c: InternalAlignment(g206-g214 -> g215) x9
    c: InternalAlignment(g216-g222 -> g215) x7
    c: Coincident(g233,g204)
    c: Weight(g223) = 1
    c: Equal(g223, g224-g232) x9
    c: Coincident(g233,g205)
    c: InternalAlignment(g223-g232 -> g233) x10
    c: InternalAlignment(g234-g241 -> g233) x8
    c: Vertical(g205)
    c: Block(g205)
    c: Block(g215)
    c: Block(g233)
    c: Horizontal(g242)
    c: Horizontal(g243)
    c: Block(g242)
    c: Block(g243)
    c: Vertical(g244)
    c: Block(g244)
    c: Coincident(g270,g243)
    c: Weight(g245) = 1
    c: Equal(g245, g246-g269) x24
    c: Coincident(g270,g244)
    c: InternalAlignment(g245-g269 -> g270) x25
    c: InternalAlignment(g271-g293 -> g270) x23
    c: Coincident(g305,g242)
    c: Weight(g294) = 1
    c: Equal(g294, g295-g304) x10
    c: Coincident(g305,g242)
    c: InternalAlignment(g294-g304 -> g305) x11
    c: InternalAlignment(g306-g314 -> g305) x9
    c: Block(g305)
    c: Coincident(g327,g243)
    c: Weight(g315) = 1
    c: Equal(g315, g316-g326) x11
    c: Coincident(g327,g244)
    c: InternalAlignment(g315-g326 -> g327) x12
    c: InternalAlignment(g328-g337 -> g327) x10
    c: Block(g327)
    c: Block(g270)
FEATURE [Part::Extrusion] Extrude075  label="CommodoreLogoAndText002"
  Base = -> Sketch084
  Dir = (0,0,1)
  DirMode = 2
  FaceMakerClass = Part::FaceMakerBullseye
  LengthFwd = 10
  LengthRev = 0
  Solid = true
  Symmetric = false
FEATURE [Part::FeaturePython] Clone001  label="CommodoreLogoAndTextScale001"  # Draft clone (typed FeaturePython)
  AttacherType = Attacher::AttachEngine3D
  Fuse = false
  Objects = -> [Extrude075]
  Placement = pos=(112.566,5.37,73.6) rot=(0,0,1;0rad)
  Scale = (0.62,0.62,1)
FEATURE [Part::Cut] Cut073  label="sideA005"
  Base = -> Extrude002
  Tool = -> Part__Mirroring
FEATURE [Part::Cut] Cut074  label="sideB005"
  Base = -> Extrude028
  Tool = -> Clone001
FEATURE [Part::Box] Box037  label="Cube022"
  AttacherType = Attacher::AttachEngine3D
  Height = 10
  Length = 7
  Placement = pos=(9,4.8,0) rot=(0,0,1;0rad)
  Width = 6.7
